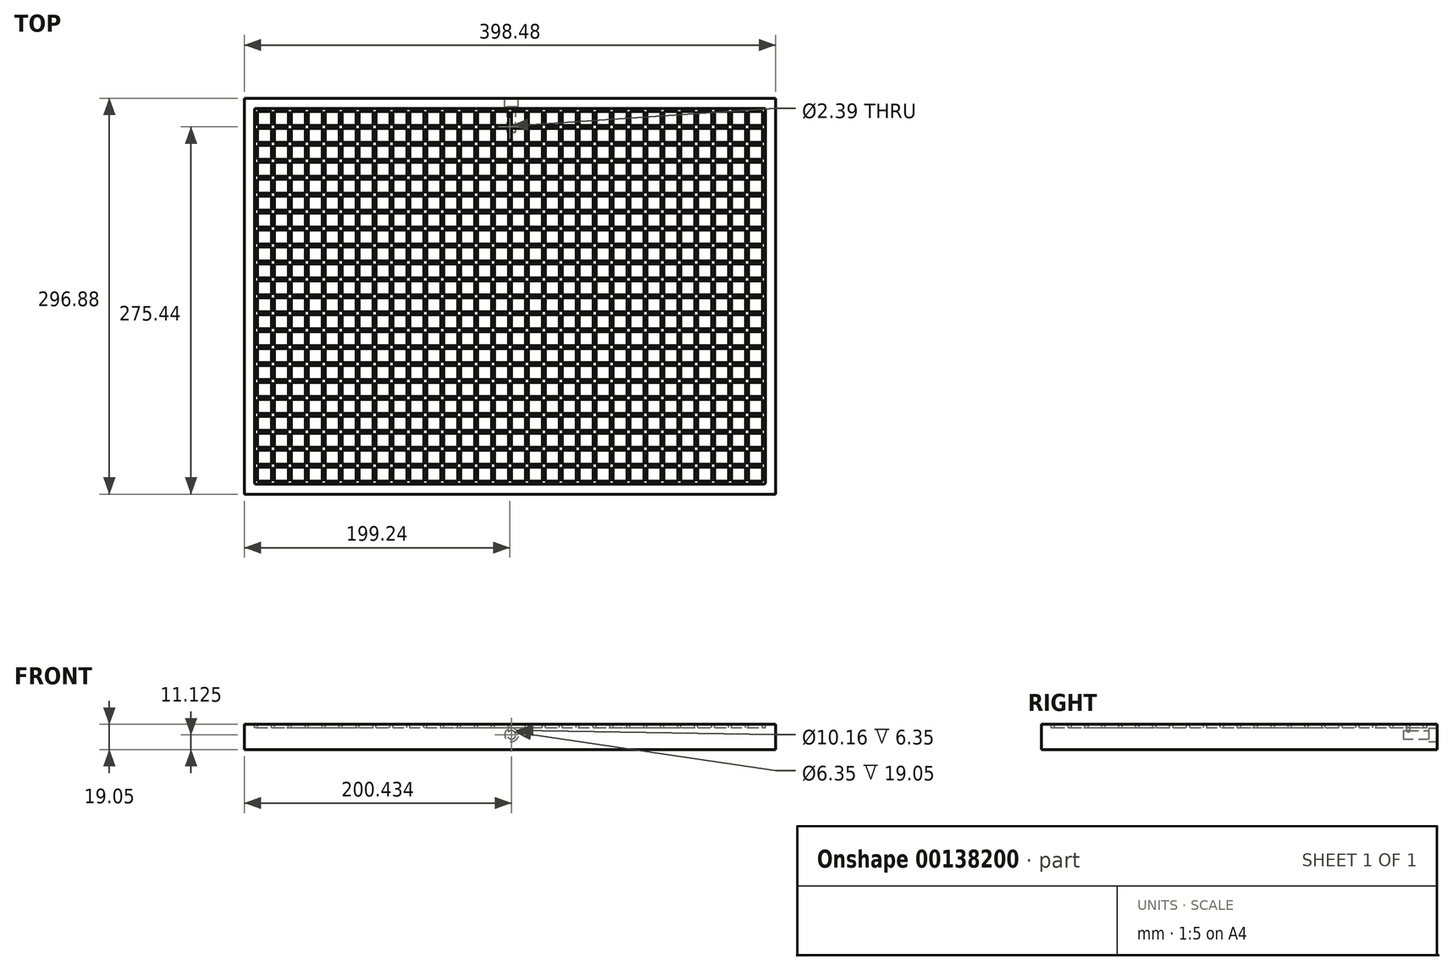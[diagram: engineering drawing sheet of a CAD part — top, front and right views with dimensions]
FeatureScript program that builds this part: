
annotation { "Feature Type Name" : "Feature", "Feature Type Description" : "" }
export const myFeature = defineFeature(function(context is Context, id is Id, definition is map)
    precondition{}
    {
        {
            var Q0;
            Q0=qCreatedBy(makeId("Top.planeOp"),FACE);
            var sketch = newSketch(context, id + "F0", { "sketchPlane" : qUnion([Q0])});
            skLineSegment(sketch, "E0.bottom", {"start": v(0, 0) * mm, "end": v(406.4, 0) * mm});
            skLineSegment(sketch, "E0.top", {"start": v(0, 304.8) * mm, "end": v(406.4, 304.8) * mm});
            skLineSegment(sketch, "E0.left", {"start": v(0, 0) * mm, "end": v(0, 304.8) * mm});
            skLineSegment(sketch, "E0.right", {"start": v(406.4, 0) * mm, "end": v(406.4, 304.8) * mm});
            skSolve(sketch);
        }
        {
            var Q0;
            Q0=qSketchRegion(id+"F0",true);
            extrude(context, id + "F1", {"entities" : qUnion([Q0]), "depth" : 19.05 * mm});
        }
        {
            var Q0;
            Q0=makeQuery(id+"F1.opExtrude","CAP_FACE",FACE,{"disambiguationData":[OSD([sQuery(id+"F0.wireOp",EDGE,"E0.bottom"),sQuery(id+"F0.wireOp",EDGE,"E0.top"),sQuery(id+"F0.wireOp",EDGE,"E0.left"),sQuery(id+"F0.wireOp",EDGE,"E0.right")])],"isStart":false});
            var sketch = newSketch(context, id + "F2", { "sketchPlane" : qUnion([Q0])});
            skLineSegment(sketch, "E1.bottom", {"start": v(12.7, 11.5) * mm, "end": v(393.7, 11.5) * mm});
            skLineSegment(sketch, "E1.top", {"start": v(12.7, 293.3) * mm, "end": v(393.7, 293.3) * mm});
            skLineSegment(sketch, "E1.left", {"start": v(11.5, 12.7) * mm, "end": v(11.5, 292.1) * mm});
            skLineSegment(sketch, "E1.right", {"start": v(394.9, 12.7) * mm, "end": v(394.9, 292.1) * mm});
            skLineSegment(sketch, "E2.bottom", {"start": v(13.9, 13.9) * mm, "end": v(24.2, 13.9) * mm});
            skLineSegment(sketch, "E2.top", {"start": v(13.9, 24.2) * mm, "end": v(24.2, 24.2) * mm});
            skLineSegment(sketch, "E2.left", {"start": v(13.9, 13.9) * mm, "end": v(13.9, 24.2) * mm});
            skLineSegment(sketch, "E2.right", {"start": v(24.2, 13.9) * mm, "end": v(24.2, 24.2) * mm});
            skLineSegment(sketch, "E3.0.1.0", {"start": v(13.9, 26.6) * mm, "end": v(13.9, 36.9) * mm});
            skLineSegment(sketch, "E3.0.1.1", {"start": v(13.9, 36.9) * mm, "end": v(24.2, 36.9) * mm});
            skLineSegment(sketch, "E3.0.1.2", {"start": v(13.9, 26.6) * mm, "end": v(24.2, 26.6) * mm});
            skLineSegment(sketch, "E3.0.1.3", {"start": v(24.2, 26.6) * mm, "end": v(24.2, 36.9) * mm});
            skLineSegment(sketch, "E3.0.2.0", {"start": v(13.9, 39.3) * mm, "end": v(13.9, 49.6) * mm});
            skLineSegment(sketch, "E3.0.2.1", {"start": v(13.9, 49.6) * mm, "end": v(24.2, 49.6) * mm});
            skLineSegment(sketch, "E3.0.2.2", {"start": v(13.9, 39.3) * mm, "end": v(24.2, 39.3) * mm});
            skLineSegment(sketch, "E3.0.2.3", {"start": v(24.2, 39.3) * mm, "end": v(24.2, 49.6) * mm});
            skLineSegment(sketch, "E3.0.3.0", {"start": v(13.9, 52) * mm, "end": v(13.9, 62.3) * mm});
            skLineSegment(sketch, "E3.0.3.1", {"start": v(13.9, 62.3) * mm, "end": v(24.2, 62.3) * mm});
            skLineSegment(sketch, "E3.0.3.2", {"start": v(13.9, 52) * mm, "end": v(24.2, 52) * mm});
            skLineSegment(sketch, "E3.0.3.3", {"start": v(24.2, 52) * mm, "end": v(24.2, 62.3) * mm});
            skLineSegment(sketch, "E3.0.4.0", {"start": v(13.9, 64.7) * mm, "end": v(13.9, 75) * mm});
            skLineSegment(sketch, "E3.0.4.1", {"start": v(13.9, 75) * mm, "end": v(24.2, 75) * mm});
            skLineSegment(sketch, "E3.0.4.2", {"start": v(13.9, 64.7) * mm, "end": v(24.2, 64.7) * mm});
            skLineSegment(sketch, "E3.0.4.3", {"start": v(24.2, 64.7) * mm, "end": v(24.2, 75) * mm});
            skLineSegment(sketch, "E3.0.5.0", {"start": v(13.9, 77.4) * mm, "end": v(13.9, 87.7) * mm});
            skLineSegment(sketch, "E3.0.5.1", {"start": v(13.9, 87.7) * mm, "end": v(24.2, 87.7) * mm});
            skLineSegment(sketch, "E3.0.5.2", {"start": v(13.9, 77.4) * mm, "end": v(24.2, 77.4) * mm});
            skLineSegment(sketch, "E3.0.5.3", {"start": v(24.2, 77.4) * mm, "end": v(24.2, 87.7) * mm});
            skLineSegment(sketch, "E3.0.6.0", {"start": v(13.9, 90.1) * mm, "end": v(13.9, 100.4) * mm});
            skLineSegment(sketch, "E3.0.6.1", {"start": v(13.9, 100.4) * mm, "end": v(24.2, 100.4) * mm});
            skLineSegment(sketch, "E3.0.6.2", {"start": v(13.9, 90.1) * mm, "end": v(24.2, 90.1) * mm});
            skLineSegment(sketch, "E3.0.6.3", {"start": v(24.2, 90.1) * mm, "end": v(24.2, 100.4) * mm});
            skLineSegment(sketch, "E3.0.7.0", {"start": v(13.9, 102.8) * mm, "end": v(13.9, 113.1) * mm});
            skLineSegment(sketch, "E3.0.7.1", {"start": v(13.9, 113.1) * mm, "end": v(24.2, 113.1) * mm});
            skLineSegment(sketch, "E3.0.7.2", {"start": v(13.9, 102.8) * mm, "end": v(24.2, 102.8) * mm});
            skLineSegment(sketch, "E3.0.7.3", {"start": v(24.2, 102.8) * mm, "end": v(24.2, 113.1) * mm});
            skLineSegment(sketch, "E3.0.8.0", {"start": v(13.9, 115.5) * mm, "end": v(13.9, 125.8) * mm});
            skLineSegment(sketch, "E3.0.8.1", {"start": v(13.9, 125.8) * mm, "end": v(24.2, 125.8) * mm});
            skLineSegment(sketch, "E3.0.8.2", {"start": v(13.9, 115.5) * mm, "end": v(24.2, 115.5) * mm});
            skLineSegment(sketch, "E3.0.8.3", {"start": v(24.2, 115.5) * mm, "end": v(24.2, 125.8) * mm});
            skLineSegment(sketch, "E3.0.9.0", {"start": v(13.9, 128.2) * mm, "end": v(13.9, 138.5) * mm});
            skLineSegment(sketch, "E3.0.9.1", {"start": v(13.9, 138.5) * mm, "end": v(24.2, 138.5) * mm});
            skLineSegment(sketch, "E3.0.9.2", {"start": v(13.9, 128.2) * mm, "end": v(24.2, 128.2) * mm});
            skLineSegment(sketch, "E3.0.9.3", {"start": v(24.2, 128.2) * mm, "end": v(24.2, 138.5) * mm});
            skLineSegment(sketch, "E3.0.10.0", {"start": v(13.9, 140.9) * mm, "end": v(13.9, 151.2) * mm});
            skLineSegment(sketch, "E3.0.10.1", {"start": v(13.9, 151.2) * mm, "end": v(24.2, 151.2) * mm});
            skLineSegment(sketch, "E3.0.10.2", {"start": v(13.9, 140.9) * mm, "end": v(24.2, 140.9) * mm});
            skLineSegment(sketch, "E3.0.10.3", {"start": v(24.2, 140.9) * mm, "end": v(24.2, 151.2) * mm});
            skLineSegment(sketch, "E3.0.11.0", {"start": v(13.9, 153.6) * mm, "end": v(13.9, 163.9) * mm});
            skLineSegment(sketch, "E3.0.11.1", {"start": v(13.9, 163.9) * mm, "end": v(24.2, 163.9) * mm});
            skLineSegment(sketch, "E3.0.11.2", {"start": v(13.9, 153.6) * mm, "end": v(24.2, 153.6) * mm});
            skLineSegment(sketch, "E3.0.11.3", {"start": v(24.2, 153.6) * mm, "end": v(24.2, 163.9) * mm});
            skLineSegment(sketch, "E3.0.12.0", {"start": v(13.9, 166.3) * mm, "end": v(13.9, 176.6) * mm});
            skLineSegment(sketch, "E3.0.12.1", {"start": v(13.9, 176.6) * mm, "end": v(24.2, 176.6) * mm});
            skLineSegment(sketch, "E3.0.12.2", {"start": v(13.9, 166.3) * mm, "end": v(24.2, 166.3) * mm});
            skLineSegment(sketch, "E3.0.12.3", {"start": v(24.2, 166.3) * mm, "end": v(24.2, 176.6) * mm});
            skLineSegment(sketch, "E3.0.13.0", {"start": v(13.9, 179) * mm, "end": v(13.9, 189.3) * mm});
            skLineSegment(sketch, "E3.0.13.1", {"start": v(13.9, 189.3) * mm, "end": v(24.2, 189.3) * mm});
            skLineSegment(sketch, "E3.0.13.2", {"start": v(13.9, 179) * mm, "end": v(24.2, 179) * mm});
            skLineSegment(sketch, "E3.0.13.3", {"start": v(24.2, 179) * mm, "end": v(24.2, 189.3) * mm});
            skLineSegment(sketch, "E3.0.14.0", {"start": v(13.9, 191.7) * mm, "end": v(13.9, 202) * mm});
            skLineSegment(sketch, "E3.0.14.1", {"start": v(13.9, 202) * mm, "end": v(24.2, 202) * mm});
            skLineSegment(sketch, "E3.0.14.2", {"start": v(13.9, 191.7) * mm, "end": v(24.2, 191.7) * mm});
            skLineSegment(sketch, "E3.0.14.3", {"start": v(24.2, 191.7) * mm, "end": v(24.2, 202) * mm});
            skLineSegment(sketch, "E3.0.15.0", {"start": v(13.9, 204.4) * mm, "end": v(13.9, 214.7) * mm});
            skLineSegment(sketch, "E3.0.15.1", {"start": v(13.9, 214.7) * mm, "end": v(24.2, 214.7) * mm});
            skLineSegment(sketch, "E3.0.15.2", {"start": v(13.9, 204.4) * mm, "end": v(24.2, 204.4) * mm});
            skLineSegment(sketch, "E3.0.15.3", {"start": v(24.2, 204.4) * mm, "end": v(24.2, 214.7) * mm});
            skLineSegment(sketch, "E3.0.16.0", {"start": v(13.9, 217.1) * mm, "end": v(13.9, 227.4) * mm});
            skLineSegment(sketch, "E3.0.16.1", {"start": v(13.9, 227.4) * mm, "end": v(24.2, 227.4) * mm});
            skLineSegment(sketch, "E3.0.16.2", {"start": v(13.9, 217.1) * mm, "end": v(24.2, 217.1) * mm});
            skLineSegment(sketch, "E3.0.16.3", {"start": v(24.2, 217.1) * mm, "end": v(24.2, 227.4) * mm});
            skLineSegment(sketch, "E3.0.17.0", {"start": v(13.9, 229.8) * mm, "end": v(13.9, 240.1) * mm});
            skLineSegment(sketch, "E3.0.17.1", {"start": v(13.9, 240.1) * mm, "end": v(24.2, 240.1) * mm});
            skLineSegment(sketch, "E3.0.17.2", {"start": v(13.9, 229.8) * mm, "end": v(24.2, 229.8) * mm});
            skLineSegment(sketch, "E3.0.17.3", {"start": v(24.2, 229.8) * mm, "end": v(24.2, 240.1) * mm});
            skLineSegment(sketch, "E3.0.18.0", {"start": v(13.9, 242.5) * mm, "end": v(13.9, 252.8) * mm});
            skLineSegment(sketch, "E3.0.18.1", {"start": v(13.9, 252.8) * mm, "end": v(24.2, 252.8) * mm});
            skLineSegment(sketch, "E3.0.18.2", {"start": v(13.9, 242.5) * mm, "end": v(24.2, 242.5) * mm});
            skLineSegment(sketch, "E3.0.18.3", {"start": v(24.2, 242.5) * mm, "end": v(24.2, 252.8) * mm});
            skLineSegment(sketch, "E3.0.19.0", {"start": v(13.9, 255.2) * mm, "end": v(13.9, 265.5) * mm});
            skLineSegment(sketch, "E3.0.19.1", {"start": v(13.9, 265.5) * mm, "end": v(24.2, 265.5) * mm});
            skLineSegment(sketch, "E3.0.19.2", {"start": v(13.9, 255.2) * mm, "end": v(24.2, 255.2) * mm});
            skLineSegment(sketch, "E3.0.19.3", {"start": v(24.2, 255.2) * mm, "end": v(24.2, 265.5) * mm});
            skLineSegment(sketch, "E3.0.20.0", {"start": v(13.9, 267.9) * mm, "end": v(13.9, 278.2) * mm});
            skLineSegment(sketch, "E3.0.20.1", {"start": v(13.9, 278.2) * mm, "end": v(24.2, 278.2) * mm});
            skLineSegment(sketch, "E3.0.20.2", {"start": v(13.9, 267.9) * mm, "end": v(24.2, 267.9) * mm});
            skLineSegment(sketch, "E3.0.20.3", {"start": v(24.2, 267.9) * mm, "end": v(24.2, 278.2) * mm});
            skLineSegment(sketch, "E3.0.21.0", {"start": v(13.9, 280.6) * mm, "end": v(13.9, 290.9) * mm});
            skLineSegment(sketch, "E3.0.21.1", {"start": v(13.9, 290.9) * mm, "end": v(24.2, 290.9) * mm});
            skLineSegment(sketch, "E3.0.21.2", {"start": v(13.9, 280.6) * mm, "end": v(24.2, 280.6) * mm});
            skLineSegment(sketch, "E3.0.21.3", {"start": v(24.2, 280.6) * mm, "end": v(24.2, 290.9) * mm});
            skLineSegment(sketch, "E3.1.0.0", {"start": v(26.6, 13.9) * mm, "end": v(26.6, 24.2) * mm});
            skLineSegment(sketch, "E3.1.0.1", {"start": v(26.6, 24.2) * mm, "end": v(36.9, 24.2) * mm});
            skLineSegment(sketch, "E3.1.0.2", {"start": v(26.6, 13.9) * mm, "end": v(36.9, 13.9) * mm});
            skLineSegment(sketch, "E3.1.0.3", {"start": v(36.9, 13.9) * mm, "end": v(36.9, 24.2) * mm});
            skLineSegment(sketch, "E3.1.1.0", {"start": v(26.6, 26.6) * mm, "end": v(26.6, 36.9) * mm});
            skLineSegment(sketch, "E3.1.1.1", {"start": v(26.6, 36.9) * mm, "end": v(36.9, 36.9) * mm});
            skLineSegment(sketch, "E3.1.1.2", {"start": v(26.6, 26.6) * mm, "end": v(36.9, 26.6) * mm});
            skLineSegment(sketch, "E3.1.1.3", {"start": v(36.9, 26.6) * mm, "end": v(36.9, 36.9) * mm});
            skLineSegment(sketch, "E3.1.2.0", {"start": v(26.6, 39.3) * mm, "end": v(26.6, 49.6) * mm});
            skLineSegment(sketch, "E3.1.2.1", {"start": v(26.6, 49.6) * mm, "end": v(36.9, 49.6) * mm});
            skLineSegment(sketch, "E3.1.2.2", {"start": v(26.6, 39.3) * mm, "end": v(36.9, 39.3) * mm});
            skLineSegment(sketch, "E3.1.2.3", {"start": v(36.9, 39.3) * mm, "end": v(36.9, 49.6) * mm});
            skLineSegment(sketch, "E3.1.3.0", {"start": v(26.6, 52) * mm, "end": v(26.6, 62.3) * mm});
            skLineSegment(sketch, "E3.1.3.1", {"start": v(26.6, 62.3) * mm, "end": v(36.9, 62.3) * mm});
            skLineSegment(sketch, "E3.1.3.2", {"start": v(26.6, 52) * mm, "end": v(36.9, 52) * mm});
            skLineSegment(sketch, "E3.1.3.3", {"start": v(36.9, 52) * mm, "end": v(36.9, 62.3) * mm});
            skLineSegment(sketch, "E3.1.4.0", {"start": v(26.6, 64.7) * mm, "end": v(26.6, 75) * mm});
            skLineSegment(sketch, "E3.1.4.1", {"start": v(26.6, 75) * mm, "end": v(36.9, 75) * mm});
            skLineSegment(sketch, "E3.1.4.2", {"start": v(26.6, 64.7) * mm, "end": v(36.9, 64.7) * mm});
            skLineSegment(sketch, "E3.1.4.3", {"start": v(36.9, 64.7) * mm, "end": v(36.9, 75) * mm});
            skLineSegment(sketch, "E3.1.5.0", {"start": v(26.6, 77.4) * mm, "end": v(26.6, 87.7) * mm});
            skLineSegment(sketch, "E3.1.5.1", {"start": v(26.6, 87.7) * mm, "end": v(36.9, 87.7) * mm});
            skLineSegment(sketch, "E3.1.5.2", {"start": v(26.6, 77.4) * mm, "end": v(36.9, 77.4) * mm});
            skLineSegment(sketch, "E3.1.5.3", {"start": v(36.9, 77.4) * mm, "end": v(36.9, 87.7) * mm});
            skLineSegment(sketch, "E3.1.6.0", {"start": v(26.6, 90.1) * mm, "end": v(26.6, 100.4) * mm});
            skLineSegment(sketch, "E3.1.6.1", {"start": v(26.6, 100.4) * mm, "end": v(36.9, 100.4) * mm});
            skLineSegment(sketch, "E3.1.6.2", {"start": v(26.6, 90.1) * mm, "end": v(36.9, 90.1) * mm});
            skLineSegment(sketch, "E3.1.6.3", {"start": v(36.9, 90.1) * mm, "end": v(36.9, 100.4) * mm});
            skLineSegment(sketch, "E3.1.7.0", {"start": v(26.6, 102.8) * mm, "end": v(26.6, 113.1) * mm});
            skLineSegment(sketch, "E3.1.7.1", {"start": v(26.6, 113.1) * mm, "end": v(36.9, 113.1) * mm});
            skLineSegment(sketch, "E3.1.7.2", {"start": v(26.6, 102.8) * mm, "end": v(36.9, 102.8) * mm});
            skLineSegment(sketch, "E3.1.7.3", {"start": v(36.9, 102.8) * mm, "end": v(36.9, 113.1) * mm});
            skLineSegment(sketch, "E3.1.8.0", {"start": v(26.6, 115.5) * mm, "end": v(26.6, 125.8) * mm});
            skLineSegment(sketch, "E3.1.8.1", {"start": v(26.6, 125.8) * mm, "end": v(36.9, 125.8) * mm});
            skLineSegment(sketch, "E3.1.8.2", {"start": v(26.6, 115.5) * mm, "end": v(36.9, 115.5) * mm});
            skLineSegment(sketch, "E3.1.8.3", {"start": v(36.9, 115.5) * mm, "end": v(36.9, 125.8) * mm});
            skLineSegment(sketch, "E3.1.9.0", {"start": v(26.6, 128.2) * mm, "end": v(26.6, 138.5) * mm});
            skLineSegment(sketch, "E3.1.9.1", {"start": v(26.6, 138.5) * mm, "end": v(36.9, 138.5) * mm});
            skLineSegment(sketch, "E3.1.9.2", {"start": v(26.6, 128.2) * mm, "end": v(36.9, 128.2) * mm});
            skLineSegment(sketch, "E3.1.9.3", {"start": v(36.9, 128.2) * mm, "end": v(36.9, 138.5) * mm});
            skLineSegment(sketch, "E3.1.10.0", {"start": v(26.6, 140.9) * mm, "end": v(26.6, 151.2) * mm});
            skLineSegment(sketch, "E3.1.10.1", {"start": v(26.6, 151.2) * mm, "end": v(36.9, 151.2) * mm});
            skLineSegment(sketch, "E3.1.10.2", {"start": v(26.6, 140.9) * mm, "end": v(36.9, 140.9) * mm});
            skLineSegment(sketch, "E3.1.10.3", {"start": v(36.9, 140.9) * mm, "end": v(36.9, 151.2) * mm});
            skLineSegment(sketch, "E3.1.11.0", {"start": v(26.6, 153.6) * mm, "end": v(26.6, 163.9) * mm});
            skLineSegment(sketch, "E3.1.11.1", {"start": v(26.6, 163.9) * mm, "end": v(36.9, 163.9) * mm});
            skLineSegment(sketch, "E3.1.11.2", {"start": v(26.6, 153.6) * mm, "end": v(36.9, 153.6) * mm});
            skLineSegment(sketch, "E3.1.11.3", {"start": v(36.9, 153.6) * mm, "end": v(36.9, 163.9) * mm});
            skLineSegment(sketch, "E3.1.12.0", {"start": v(26.6, 166.3) * mm, "end": v(26.6, 176.6) * mm});
            skLineSegment(sketch, "E3.1.12.1", {"start": v(26.6, 176.6) * mm, "end": v(36.9, 176.6) * mm});
            skLineSegment(sketch, "E3.1.12.2", {"start": v(26.6, 166.3) * mm, "end": v(36.9, 166.3) * mm});
            skLineSegment(sketch, "E3.1.12.3", {"start": v(36.9, 166.3) * mm, "end": v(36.9, 176.6) * mm});
            skLineSegment(sketch, "E3.1.13.0", {"start": v(26.6, 179) * mm, "end": v(26.6, 189.3) * mm});
            skLineSegment(sketch, "E3.1.13.1", {"start": v(26.6, 189.3) * mm, "end": v(36.9, 189.3) * mm});
            skLineSegment(sketch, "E3.1.13.2", {"start": v(26.6, 179) * mm, "end": v(36.9, 179) * mm});
            skLineSegment(sketch, "E3.1.13.3", {"start": v(36.9, 179) * mm, "end": v(36.9, 189.3) * mm});
            skLineSegment(sketch, "E3.1.14.0", {"start": v(26.6, 191.7) * mm, "end": v(26.6, 202) * mm});
            skLineSegment(sketch, "E3.1.14.1", {"start": v(26.6, 202) * mm, "end": v(36.9, 202) * mm});
            skLineSegment(sketch, "E3.1.14.2", {"start": v(26.6, 191.7) * mm, "end": v(36.9, 191.7) * mm});
            skLineSegment(sketch, "E3.1.14.3", {"start": v(36.9, 191.7) * mm, "end": v(36.9, 202) * mm});
            skLineSegment(sketch, "E3.1.15.0", {"start": v(26.6, 204.4) * mm, "end": v(26.6, 214.7) * mm});
            skLineSegment(sketch, "E3.1.15.1", {"start": v(26.6, 214.7) * mm, "end": v(36.9, 214.7) * mm});
            skLineSegment(sketch, "E3.1.15.2", {"start": v(26.6, 204.4) * mm, "end": v(36.9, 204.4) * mm});
            skLineSegment(sketch, "E3.1.15.3", {"start": v(36.9, 204.4) * mm, "end": v(36.9, 214.7) * mm});
            skLineSegment(sketch, "E3.1.16.0", {"start": v(26.6, 217.1) * mm, "end": v(26.6, 227.4) * mm});
            skLineSegment(sketch, "E3.1.16.1", {"start": v(26.6, 227.4) * mm, "end": v(36.9, 227.4) * mm});
            skLineSegment(sketch, "E3.1.16.2", {"start": v(26.6, 217.1) * mm, "end": v(36.9, 217.1) * mm});
            skLineSegment(sketch, "E3.1.16.3", {"start": v(36.9, 217.1) * mm, "end": v(36.9, 227.4) * mm});
            skLineSegment(sketch, "E3.1.17.0", {"start": v(26.6, 229.8) * mm, "end": v(26.6, 240.1) * mm});
            skLineSegment(sketch, "E3.1.17.1", {"start": v(26.6, 240.1) * mm, "end": v(36.9, 240.1) * mm});
            skLineSegment(sketch, "E3.1.17.2", {"start": v(26.6, 229.8) * mm, "end": v(36.9, 229.8) * mm});
            skLineSegment(sketch, "E3.1.17.3", {"start": v(36.9, 229.8) * mm, "end": v(36.9, 240.1) * mm});
            skLineSegment(sketch, "E3.1.18.0", {"start": v(26.6, 242.5) * mm, "end": v(26.6, 252.8) * mm});
            skLineSegment(sketch, "E3.1.18.1", {"start": v(26.6, 252.8) * mm, "end": v(36.9, 252.8) * mm});
            skLineSegment(sketch, "E3.1.18.2", {"start": v(26.6, 242.5) * mm, "end": v(36.9, 242.5) * mm});
            skLineSegment(sketch, "E3.1.18.3", {"start": v(36.9, 242.5) * mm, "end": v(36.9, 252.8) * mm});
            skLineSegment(sketch, "E3.1.19.0", {"start": v(26.6, 255.2) * mm, "end": v(26.6, 265.5) * mm});
            skLineSegment(sketch, "E3.1.19.1", {"start": v(26.6, 265.5) * mm, "end": v(36.9, 265.5) * mm});
            skLineSegment(sketch, "E3.1.19.2", {"start": v(26.6, 255.2) * mm, "end": v(36.9, 255.2) * mm});
            skLineSegment(sketch, "E3.1.19.3", {"start": v(36.9, 255.2) * mm, "end": v(36.9, 265.5) * mm});
            skLineSegment(sketch, "E3.1.20.0", {"start": v(26.6, 267.9) * mm, "end": v(26.6, 278.2) * mm});
            skLineSegment(sketch, "E3.1.20.1", {"start": v(26.6, 278.2) * mm, "end": v(36.9, 278.2) * mm});
            skLineSegment(sketch, "E3.1.20.2", {"start": v(26.6, 267.9) * mm, "end": v(36.9, 267.9) * mm});
            skLineSegment(sketch, "E3.1.20.3", {"start": v(36.9, 267.9) * mm, "end": v(36.9, 278.2) * mm});
            skLineSegment(sketch, "E3.1.21.0", {"start": v(26.6, 280.6) * mm, "end": v(26.6, 290.9) * mm});
            skLineSegment(sketch, "E3.1.21.1", {"start": v(26.6, 290.9) * mm, "end": v(36.9, 290.9) * mm});
            skLineSegment(sketch, "E3.1.21.2", {"start": v(26.6, 280.6) * mm, "end": v(36.9, 280.6) * mm});
            skLineSegment(sketch, "E3.1.21.3", {"start": v(36.9, 280.6) * mm, "end": v(36.9, 290.9) * mm});
            skLineSegment(sketch, "E3.2.0.0", {"start": v(39.3, 13.9) * mm, "end": v(39.3, 24.2) * mm});
            skLineSegment(sketch, "E3.2.0.1", {"start": v(39.3, 24.2) * mm, "end": v(49.6, 24.2) * mm});
            skLineSegment(sketch, "E3.2.0.2", {"start": v(39.3, 13.9) * mm, "end": v(49.6, 13.9) * mm});
            skLineSegment(sketch, "E3.2.0.3", {"start": v(49.6, 13.9) * mm, "end": v(49.6, 24.2) * mm});
            skLineSegment(sketch, "E3.2.1.0", {"start": v(39.3, 26.6) * mm, "end": v(39.3, 36.9) * mm});
            skLineSegment(sketch, "E3.2.1.1", {"start": v(39.3, 36.9) * mm, "end": v(49.6, 36.9) * mm});
            skLineSegment(sketch, "E3.2.1.2", {"start": v(39.3, 26.6) * mm, "end": v(49.6, 26.6) * mm});
            skLineSegment(sketch, "E3.2.1.3", {"start": v(49.6, 26.6) * mm, "end": v(49.6, 36.9) * mm});
            skLineSegment(sketch, "E3.2.2.0", {"start": v(39.3, 39.3) * mm, "end": v(39.3, 49.6) * mm});
            skLineSegment(sketch, "E3.2.2.1", {"start": v(39.3, 49.6) * mm, "end": v(49.6, 49.6) * mm});
            skLineSegment(sketch, "E3.2.2.2", {"start": v(39.3, 39.3) * mm, "end": v(49.6, 39.3) * mm});
            skLineSegment(sketch, "E3.2.2.3", {"start": v(49.6, 39.3) * mm, "end": v(49.6, 49.6) * mm});
            skLineSegment(sketch, "E3.2.3.0", {"start": v(39.3, 52) * mm, "end": v(39.3, 62.3) * mm});
            skLineSegment(sketch, "E3.2.3.1", {"start": v(39.3, 62.3) * mm, "end": v(49.6, 62.3) * mm});
            skLineSegment(sketch, "E3.2.3.2", {"start": v(39.3, 52) * mm, "end": v(49.6, 52) * mm});
            skLineSegment(sketch, "E3.2.3.3", {"start": v(49.6, 52) * mm, "end": v(49.6, 62.3) * mm});
            skLineSegment(sketch, "E3.2.4.0", {"start": v(39.3, 64.7) * mm, "end": v(39.3, 75) * mm});
            skLineSegment(sketch, "E3.2.4.1", {"start": v(39.3, 75) * mm, "end": v(49.6, 75) * mm});
            skLineSegment(sketch, "E3.2.4.2", {"start": v(39.3, 64.7) * mm, "end": v(49.6, 64.7) * mm});
            skLineSegment(sketch, "E3.2.4.3", {"start": v(49.6, 64.7) * mm, "end": v(49.6, 75) * mm});
            skLineSegment(sketch, "E3.2.5.0", {"start": v(39.3, 77.4) * mm, "end": v(39.3, 87.7) * mm});
            skLineSegment(sketch, "E3.2.5.1", {"start": v(39.3, 87.7) * mm, "end": v(49.6, 87.7) * mm});
            skLineSegment(sketch, "E3.2.5.2", {"start": v(39.3, 77.4) * mm, "end": v(49.6, 77.4) * mm});
            skLineSegment(sketch, "E3.2.5.3", {"start": v(49.6, 77.4) * mm, "end": v(49.6, 87.7) * mm});
            skLineSegment(sketch, "E3.2.6.0", {"start": v(39.3, 90.1) * mm, "end": v(39.3, 100.4) * mm});
            skLineSegment(sketch, "E3.2.6.1", {"start": v(39.3, 100.4) * mm, "end": v(49.6, 100.4) * mm});
            skLineSegment(sketch, "E3.2.6.2", {"start": v(39.3, 90.1) * mm, "end": v(49.6, 90.1) * mm});
            skLineSegment(sketch, "E3.2.6.3", {"start": v(49.6, 90.1) * mm, "end": v(49.6, 100.4) * mm});
            skLineSegment(sketch, "E3.2.7.0", {"start": v(39.3, 102.8) * mm, "end": v(39.3, 113.1) * mm});
            skLineSegment(sketch, "E3.2.7.1", {"start": v(39.3, 113.1) * mm, "end": v(49.6, 113.1) * mm});
            skLineSegment(sketch, "E3.2.7.2", {"start": v(39.3, 102.8) * mm, "end": v(49.6, 102.8) * mm});
            skLineSegment(sketch, "E3.2.7.3", {"start": v(49.6, 102.8) * mm, "end": v(49.6, 113.1) * mm});
            skLineSegment(sketch, "E3.2.8.0", {"start": v(39.3, 115.5) * mm, "end": v(39.3, 125.8) * mm});
            skLineSegment(sketch, "E3.2.8.1", {"start": v(39.3, 125.8) * mm, "end": v(49.6, 125.8) * mm});
            skLineSegment(sketch, "E3.2.8.2", {"start": v(39.3, 115.5) * mm, "end": v(49.6, 115.5) * mm});
            skLineSegment(sketch, "E3.2.8.3", {"start": v(49.6, 115.5) * mm, "end": v(49.6, 125.8) * mm});
            skLineSegment(sketch, "E3.2.9.0", {"start": v(39.3, 128.2) * mm, "end": v(39.3, 138.5) * mm});
            skLineSegment(sketch, "E3.2.9.1", {"start": v(39.3, 138.5) * mm, "end": v(49.6, 138.5) * mm});
            skLineSegment(sketch, "E3.2.9.2", {"start": v(39.3, 128.2) * mm, "end": v(49.6, 128.2) * mm});
            skLineSegment(sketch, "E3.2.9.3", {"start": v(49.6, 128.2) * mm, "end": v(49.6, 138.5) * mm});
            skLineSegment(sketch, "E3.2.10.0", {"start": v(39.3, 140.9) * mm, "end": v(39.3, 151.2) * mm});
            skLineSegment(sketch, "E3.2.10.1", {"start": v(39.3, 151.2) * mm, "end": v(49.6, 151.2) * mm});
            skLineSegment(sketch, "E3.2.10.2", {"start": v(39.3, 140.9) * mm, "end": v(49.6, 140.9) * mm});
            skLineSegment(sketch, "E3.2.10.3", {"start": v(49.6, 140.9) * mm, "end": v(49.6, 151.2) * mm});
            skLineSegment(sketch, "E3.2.11.0", {"start": v(39.3, 153.6) * mm, "end": v(39.3, 163.9) * mm});
            skLineSegment(sketch, "E3.2.11.1", {"start": v(39.3, 163.9) * mm, "end": v(49.6, 163.9) * mm});
            skLineSegment(sketch, "E3.2.11.2", {"start": v(39.3, 153.6) * mm, "end": v(49.6, 153.6) * mm});
            skLineSegment(sketch, "E3.2.11.3", {"start": v(49.6, 153.6) * mm, "end": v(49.6, 163.9) * mm});
            skLineSegment(sketch, "E3.2.12.0", {"start": v(39.3, 166.3) * mm, "end": v(39.3, 176.6) * mm});
            skLineSegment(sketch, "E3.2.12.1", {"start": v(39.3, 176.6) * mm, "end": v(49.6, 176.6) * mm});
            skLineSegment(sketch, "E3.2.12.2", {"start": v(39.3, 166.3) * mm, "end": v(49.6, 166.3) * mm});
            skLineSegment(sketch, "E3.2.12.3", {"start": v(49.6, 166.3) * mm, "end": v(49.6, 176.6) * mm});
            skLineSegment(sketch, "E3.2.13.0", {"start": v(39.3, 179) * mm, "end": v(39.3, 189.3) * mm});
            skLineSegment(sketch, "E3.2.13.1", {"start": v(39.3, 189.3) * mm, "end": v(49.6, 189.3) * mm});
            skLineSegment(sketch, "E3.2.13.2", {"start": v(39.3, 179) * mm, "end": v(49.6, 179) * mm});
            skLineSegment(sketch, "E3.2.13.3", {"start": v(49.6, 179) * mm, "end": v(49.6, 189.3) * mm});
            skLineSegment(sketch, "E3.2.14.0", {"start": v(39.3, 191.7) * mm, "end": v(39.3, 202) * mm});
            skLineSegment(sketch, "E3.2.14.1", {"start": v(39.3, 202) * mm, "end": v(49.6, 202) * mm});
            skLineSegment(sketch, "E3.2.14.2", {"start": v(39.3, 191.7) * mm, "end": v(49.6, 191.7) * mm});
            skLineSegment(sketch, "E3.2.14.3", {"start": v(49.6, 191.7) * mm, "end": v(49.6, 202) * mm});
            skLineSegment(sketch, "E3.2.15.0", {"start": v(39.3, 204.4) * mm, "end": v(39.3, 214.7) * mm});
            skLineSegment(sketch, "E3.2.15.1", {"start": v(39.3, 214.7) * mm, "end": v(49.6, 214.7) * mm});
            skLineSegment(sketch, "E3.2.15.2", {"start": v(39.3, 204.4) * mm, "end": v(49.6, 204.4) * mm});
            skLineSegment(sketch, "E3.2.15.3", {"start": v(49.6, 204.4) * mm, "end": v(49.6, 214.7) * mm});
            skLineSegment(sketch, "E3.2.16.0", {"start": v(39.3, 217.1) * mm, "end": v(39.3, 227.4) * mm});
            skLineSegment(sketch, "E3.2.16.1", {"start": v(39.3, 227.4) * mm, "end": v(49.6, 227.4) * mm});
            skLineSegment(sketch, "E3.2.16.2", {"start": v(39.3, 217.1) * mm, "end": v(49.6, 217.1) * mm});
            skLineSegment(sketch, "E3.2.16.3", {"start": v(49.6, 217.1) * mm, "end": v(49.6, 227.4) * mm});
            skLineSegment(sketch, "E3.2.17.0", {"start": v(39.3, 229.8) * mm, "end": v(39.3, 240.1) * mm});
            skLineSegment(sketch, "E3.2.17.1", {"start": v(39.3, 240.1) * mm, "end": v(49.6, 240.1) * mm});
            skLineSegment(sketch, "E3.2.17.2", {"start": v(39.3, 229.8) * mm, "end": v(49.6, 229.8) * mm});
            skLineSegment(sketch, "E3.2.17.3", {"start": v(49.6, 229.8) * mm, "end": v(49.6, 240.1) * mm});
            skLineSegment(sketch, "E3.2.18.0", {"start": v(39.3, 242.5) * mm, "end": v(39.3, 252.8) * mm});
            skLineSegment(sketch, "E3.2.18.1", {"start": v(39.3, 252.8) * mm, "end": v(49.6, 252.8) * mm});
            skLineSegment(sketch, "E3.2.18.2", {"start": v(39.3, 242.5) * mm, "end": v(49.6, 242.5) * mm});
            skLineSegment(sketch, "E3.2.18.3", {"start": v(49.6, 242.5) * mm, "end": v(49.6, 252.8) * mm});
            skLineSegment(sketch, "E3.2.19.0", {"start": v(39.3, 255.2) * mm, "end": v(39.3, 265.5) * mm});
            skLineSegment(sketch, "E3.2.19.1", {"start": v(39.3, 265.5) * mm, "end": v(49.6, 265.5) * mm});
            skLineSegment(sketch, "E3.2.19.2", {"start": v(39.3, 255.2) * mm, "end": v(49.6, 255.2) * mm});
            skLineSegment(sketch, "E3.2.19.3", {"start": v(49.6, 255.2) * mm, "end": v(49.6, 265.5) * mm});
            skLineSegment(sketch, "E3.2.20.0", {"start": v(39.3, 267.9) * mm, "end": v(39.3, 278.2) * mm});
            skLineSegment(sketch, "E3.2.20.1", {"start": v(39.3, 278.2) * mm, "end": v(49.6, 278.2) * mm});
            skLineSegment(sketch, "E3.2.20.2", {"start": v(39.3, 267.9) * mm, "end": v(49.6, 267.9) * mm});
            skLineSegment(sketch, "E3.2.20.3", {"start": v(49.6, 267.9) * mm, "end": v(49.6, 278.2) * mm});
            skLineSegment(sketch, "E3.2.21.0", {"start": v(39.3, 280.6) * mm, "end": v(39.3, 290.9) * mm});
            skLineSegment(sketch, "E3.2.21.1", {"start": v(39.3, 290.9) * mm, "end": v(49.6, 290.9) * mm});
            skLineSegment(sketch, "E3.2.21.2", {"start": v(39.3, 280.6) * mm, "end": v(49.6, 280.6) * mm});
            skLineSegment(sketch, "E3.2.21.3", {"start": v(49.6, 280.6) * mm, "end": v(49.6, 290.9) * mm});
            skLineSegment(sketch, "E3.3.0.0", {"start": v(52, 13.9) * mm, "end": v(52, 24.2) * mm});
            skLineSegment(sketch, "E3.3.0.1", {"start": v(52, 24.2) * mm, "end": v(62.3, 24.2) * mm});
            skLineSegment(sketch, "E3.3.0.2", {"start": v(52, 13.9) * mm, "end": v(62.3, 13.9) * mm});
            skLineSegment(sketch, "E3.3.0.3", {"start": v(62.3, 13.9) * mm, "end": v(62.3, 24.2) * mm});
            skLineSegment(sketch, "E3.3.1.0", {"start": v(52, 26.6) * mm, "end": v(52, 36.9) * mm});
            skLineSegment(sketch, "E3.3.1.1", {"start": v(52, 36.9) * mm, "end": v(62.3, 36.9) * mm});
            skLineSegment(sketch, "E3.3.1.2", {"start": v(52, 26.6) * mm, "end": v(62.3, 26.6) * mm});
            skLineSegment(sketch, "E3.3.1.3", {"start": v(62.3, 26.6) * mm, "end": v(62.3, 36.9) * mm});
            skLineSegment(sketch, "E3.3.2.0", {"start": v(52, 39.3) * mm, "end": v(52, 49.6) * mm});
            skLineSegment(sketch, "E3.3.2.1", {"start": v(52, 49.6) * mm, "end": v(62.3, 49.6) * mm});
            skLineSegment(sketch, "E3.3.2.2", {"start": v(52, 39.3) * mm, "end": v(62.3, 39.3) * mm});
            skLineSegment(sketch, "E3.3.2.3", {"start": v(62.3, 39.3) * mm, "end": v(62.3, 49.6) * mm});
            skLineSegment(sketch, "E3.3.3.0", {"start": v(52, 52) * mm, "end": v(52, 62.3) * mm});
            skLineSegment(sketch, "E3.3.3.1", {"start": v(52, 62.3) * mm, "end": v(62.3, 62.3) * mm});
            skLineSegment(sketch, "E3.3.3.2", {"start": v(52, 52) * mm, "end": v(62.3, 52) * mm});
            skLineSegment(sketch, "E3.3.3.3", {"start": v(62.3, 52) * mm, "end": v(62.3, 62.3) * mm});
            skLineSegment(sketch, "E3.3.4.0", {"start": v(52, 64.7) * mm, "end": v(52, 75) * mm});
            skLineSegment(sketch, "E3.3.4.1", {"start": v(52, 75) * mm, "end": v(62.3, 75) * mm});
            skLineSegment(sketch, "E3.3.4.2", {"start": v(52, 64.7) * mm, "end": v(62.3, 64.7) * mm});
            skLineSegment(sketch, "E3.3.4.3", {"start": v(62.3, 64.7) * mm, "end": v(62.3, 75) * mm});
            skLineSegment(sketch, "E3.3.5.0", {"start": v(52, 77.4) * mm, "end": v(52, 87.7) * mm});
            skLineSegment(sketch, "E3.3.5.1", {"start": v(52, 87.7) * mm, "end": v(62.3, 87.7) * mm});
            skLineSegment(sketch, "E3.3.5.2", {"start": v(52, 77.4) * mm, "end": v(62.3, 77.4) * mm});
            skLineSegment(sketch, "E3.3.5.3", {"start": v(62.3, 77.4) * mm, "end": v(62.3, 87.7) * mm});
            skLineSegment(sketch, "E3.3.6.0", {"start": v(52, 90.1) * mm, "end": v(52, 100.4) * mm});
            skLineSegment(sketch, "E3.3.6.1", {"start": v(52, 100.4) * mm, "end": v(62.3, 100.4) * mm});
            skLineSegment(sketch, "E3.3.6.2", {"start": v(52, 90.1) * mm, "end": v(62.3, 90.1) * mm});
            skLineSegment(sketch, "E3.3.6.3", {"start": v(62.3, 90.1) * mm, "end": v(62.3, 100.4) * mm});
            skLineSegment(sketch, "E3.3.7.0", {"start": v(52, 102.8) * mm, "end": v(52, 113.1) * mm});
            skLineSegment(sketch, "E3.3.7.1", {"start": v(52, 113.1) * mm, "end": v(62.3, 113.1) * mm});
            skLineSegment(sketch, "E3.3.7.2", {"start": v(52, 102.8) * mm, "end": v(62.3, 102.8) * mm});
            skLineSegment(sketch, "E3.3.7.3", {"start": v(62.3, 102.8) * mm, "end": v(62.3, 113.1) * mm});
            skLineSegment(sketch, "E3.3.8.0", {"start": v(52, 115.5) * mm, "end": v(52, 125.8) * mm});
            skLineSegment(sketch, "E3.3.8.1", {"start": v(52, 125.8) * mm, "end": v(62.3, 125.8) * mm});
            skLineSegment(sketch, "E3.3.8.2", {"start": v(52, 115.5) * mm, "end": v(62.3, 115.5) * mm});
            skLineSegment(sketch, "E3.3.8.3", {"start": v(62.3, 115.5) * mm, "end": v(62.3, 125.8) * mm});
            skLineSegment(sketch, "E3.3.9.0", {"start": v(52, 128.2) * mm, "end": v(52, 138.5) * mm});
            skLineSegment(sketch, "E3.3.9.1", {"start": v(52, 138.5) * mm, "end": v(62.3, 138.5) * mm});
            skLineSegment(sketch, "E3.3.9.2", {"start": v(52, 128.2) * mm, "end": v(62.3, 128.2) * mm});
            skLineSegment(sketch, "E3.3.9.3", {"start": v(62.3, 128.2) * mm, "end": v(62.3, 138.5) * mm});
            skLineSegment(sketch, "E3.3.10.0", {"start": v(52, 140.9) * mm, "end": v(52, 151.2) * mm});
            skLineSegment(sketch, "E3.3.10.1", {"start": v(52, 151.2) * mm, "end": v(62.3, 151.2) * mm});
            skLineSegment(sketch, "E3.3.10.2", {"start": v(52, 140.9) * mm, "end": v(62.3, 140.9) * mm});
            skLineSegment(sketch, "E3.3.10.3", {"start": v(62.3, 140.9) * mm, "end": v(62.3, 151.2) * mm});
            skLineSegment(sketch, "E3.3.11.0", {"start": v(52, 153.6) * mm, "end": v(52, 163.9) * mm});
            skLineSegment(sketch, "E3.3.11.1", {"start": v(52, 163.9) * mm, "end": v(62.3, 163.9) * mm});
            skLineSegment(sketch, "E3.3.11.2", {"start": v(52, 153.6) * mm, "end": v(62.3, 153.6) * mm});
            skLineSegment(sketch, "E3.3.11.3", {"start": v(62.3, 153.6) * mm, "end": v(62.3, 163.9) * mm});
            skLineSegment(sketch, "E3.3.12.0", {"start": v(52, 166.3) * mm, "end": v(52, 176.6) * mm});
            skLineSegment(sketch, "E3.3.12.1", {"start": v(52, 176.6) * mm, "end": v(62.3, 176.6) * mm});
            skLineSegment(sketch, "E3.3.12.2", {"start": v(52, 166.3) * mm, "end": v(62.3, 166.3) * mm});
            skLineSegment(sketch, "E3.3.12.3", {"start": v(62.3, 166.3) * mm, "end": v(62.3, 176.6) * mm});
            skLineSegment(sketch, "E3.3.13.0", {"start": v(52, 179) * mm, "end": v(52, 189.3) * mm});
            skLineSegment(sketch, "E3.3.13.1", {"start": v(52, 189.3) * mm, "end": v(62.3, 189.3) * mm});
            skLineSegment(sketch, "E3.3.13.2", {"start": v(52, 179) * mm, "end": v(62.3, 179) * mm});
            skLineSegment(sketch, "E3.3.13.3", {"start": v(62.3, 179) * mm, "end": v(62.3, 189.3) * mm});
            skLineSegment(sketch, "E3.3.14.0", {"start": v(52, 191.7) * mm, "end": v(52, 202) * mm});
            skLineSegment(sketch, "E3.3.14.1", {"start": v(52, 202) * mm, "end": v(62.3, 202) * mm});
            skLineSegment(sketch, "E3.3.14.2", {"start": v(52, 191.7) * mm, "end": v(62.3, 191.7) * mm});
            skLineSegment(sketch, "E3.3.14.3", {"start": v(62.3, 191.7) * mm, "end": v(62.3, 202) * mm});
            skLineSegment(sketch, "E3.3.15.0", {"start": v(52, 204.4) * mm, "end": v(52, 214.7) * mm});
            skLineSegment(sketch, "E3.3.15.1", {"start": v(52, 214.7) * mm, "end": v(62.3, 214.7) * mm});
            skLineSegment(sketch, "E3.3.15.2", {"start": v(52, 204.4) * mm, "end": v(62.3, 204.4) * mm});
            skLineSegment(sketch, "E3.3.15.3", {"start": v(62.3, 204.4) * mm, "end": v(62.3, 214.7) * mm});
            skLineSegment(sketch, "E3.3.16.0", {"start": v(52, 217.1) * mm, "end": v(52, 227.4) * mm});
            skLineSegment(sketch, "E3.3.16.1", {"start": v(52, 227.4) * mm, "end": v(62.3, 227.4) * mm});
            skLineSegment(sketch, "E3.3.16.2", {"start": v(52, 217.1) * mm, "end": v(62.3, 217.1) * mm});
            skLineSegment(sketch, "E3.3.16.3", {"start": v(62.3, 217.1) * mm, "end": v(62.3, 227.4) * mm});
            skLineSegment(sketch, "E3.3.17.0", {"start": v(52, 229.8) * mm, "end": v(52, 240.1) * mm});
            skLineSegment(sketch, "E3.3.17.1", {"start": v(52, 240.1) * mm, "end": v(62.3, 240.1) * mm});
            skLineSegment(sketch, "E3.3.17.2", {"start": v(52, 229.8) * mm, "end": v(62.3, 229.8) * mm});
            skLineSegment(sketch, "E3.3.17.3", {"start": v(62.3, 229.8) * mm, "end": v(62.3, 240.1) * mm});
            skLineSegment(sketch, "E3.3.18.0", {"start": v(52, 242.5) * mm, "end": v(52, 252.8) * mm});
            skLineSegment(sketch, "E3.3.18.1", {"start": v(52, 252.8) * mm, "end": v(62.3, 252.8) * mm});
            skLineSegment(sketch, "E3.3.18.2", {"start": v(52, 242.5) * mm, "end": v(62.3, 242.5) * mm});
            skLineSegment(sketch, "E3.3.18.3", {"start": v(62.3, 242.5) * mm, "end": v(62.3, 252.8) * mm});
            skLineSegment(sketch, "E3.3.19.0", {"start": v(52, 255.2) * mm, "end": v(52, 265.5) * mm});
            skLineSegment(sketch, "E3.3.19.1", {"start": v(52, 265.5) * mm, "end": v(62.3, 265.5) * mm});
            skLineSegment(sketch, "E3.3.19.2", {"start": v(52, 255.2) * mm, "end": v(62.3, 255.2) * mm});
            skLineSegment(sketch, "E3.3.19.3", {"start": v(62.3, 255.2) * mm, "end": v(62.3, 265.5) * mm});
            skLineSegment(sketch, "E3.3.20.0", {"start": v(52, 267.9) * mm, "end": v(52, 278.2) * mm});
            skLineSegment(sketch, "E3.3.20.1", {"start": v(52, 278.2) * mm, "end": v(62.3, 278.2) * mm});
            skLineSegment(sketch, "E3.3.20.2", {"start": v(52, 267.9) * mm, "end": v(62.3, 267.9) * mm});
            skLineSegment(sketch, "E3.3.20.3", {"start": v(62.3, 267.9) * mm, "end": v(62.3, 278.2) * mm});
            skLineSegment(sketch, "E3.3.21.0", {"start": v(52, 280.6) * mm, "end": v(52, 290.9) * mm});
            skLineSegment(sketch, "E3.3.21.1", {"start": v(52, 290.9) * mm, "end": v(62.3, 290.9) * mm});
            skLineSegment(sketch, "E3.3.21.2", {"start": v(52, 280.6) * mm, "end": v(62.3, 280.6) * mm});
            skLineSegment(sketch, "E3.3.21.3", {"start": v(62.3, 280.6) * mm, "end": v(62.3, 290.9) * mm});
            skLineSegment(sketch, "E3.4.0.0", {"start": v(64.7, 13.9) * mm, "end": v(64.7, 24.2) * mm});
            skLineSegment(sketch, "E3.4.0.1", {"start": v(64.7, 24.2) * mm, "end": v(75, 24.2) * mm});
            skLineSegment(sketch, "E3.4.0.2", {"start": v(64.7, 13.9) * mm, "end": v(75, 13.9) * mm});
            skLineSegment(sketch, "E3.4.0.3", {"start": v(75, 13.9) * mm, "end": v(75, 24.2) * mm});
            skLineSegment(sketch, "E3.4.1.0", {"start": v(64.7, 26.6) * mm, "end": v(64.7, 36.9) * mm});
            skLineSegment(sketch, "E3.4.1.1", {"start": v(64.7, 36.9) * mm, "end": v(75, 36.9) * mm});
            skLineSegment(sketch, "E3.4.1.2", {"start": v(64.7, 26.6) * mm, "end": v(75, 26.6) * mm});
            skLineSegment(sketch, "E3.4.1.3", {"start": v(75, 26.6) * mm, "end": v(75, 36.9) * mm});
            skLineSegment(sketch, "E3.4.2.0", {"start": v(64.7, 39.3) * mm, "end": v(64.7, 49.6) * mm});
            skLineSegment(sketch, "E3.4.2.1", {"start": v(64.7, 49.6) * mm, "end": v(75, 49.6) * mm});
            skLineSegment(sketch, "E3.4.2.2", {"start": v(64.7, 39.3) * mm, "end": v(75, 39.3) * mm});
            skLineSegment(sketch, "E3.4.2.3", {"start": v(75, 39.3) * mm, "end": v(75, 49.6) * mm});
            skLineSegment(sketch, "E3.4.3.0", {"start": v(64.7, 52) * mm, "end": v(64.7, 62.3) * mm});
            skLineSegment(sketch, "E3.4.3.1", {"start": v(64.7, 62.3) * mm, "end": v(75, 62.3) * mm});
            skLineSegment(sketch, "E3.4.3.2", {"start": v(64.7, 52) * mm, "end": v(75, 52) * mm});
            skLineSegment(sketch, "E3.4.3.3", {"start": v(75, 52) * mm, "end": v(75, 62.3) * mm});
            skLineSegment(sketch, "E3.4.4.0", {"start": v(64.7, 64.7) * mm, "end": v(64.7, 75) * mm});
            skLineSegment(sketch, "E3.4.4.1", {"start": v(64.7, 75) * mm, "end": v(75, 75) * mm});
            skLineSegment(sketch, "E3.4.4.2", {"start": v(64.7, 64.7) * mm, "end": v(75, 64.7) * mm});
            skLineSegment(sketch, "E3.4.4.3", {"start": v(75, 64.7) * mm, "end": v(75, 75) * mm});
            skLineSegment(sketch, "E3.4.5.0", {"start": v(64.7, 77.4) * mm, "end": v(64.7, 87.7) * mm});
            skLineSegment(sketch, "E3.4.5.1", {"start": v(64.7, 87.7) * mm, "end": v(75, 87.7) * mm});
            skLineSegment(sketch, "E3.4.5.2", {"start": v(64.7, 77.4) * mm, "end": v(75, 77.4) * mm});
            skLineSegment(sketch, "E3.4.5.3", {"start": v(75, 77.4) * mm, "end": v(75, 87.7) * mm});
            skLineSegment(sketch, "E3.4.6.0", {"start": v(64.7, 90.1) * mm, "end": v(64.7, 100.4) * mm});
            skLineSegment(sketch, "E3.4.6.1", {"start": v(64.7, 100.4) * mm, "end": v(75, 100.4) * mm});
            skLineSegment(sketch, "E3.4.6.2", {"start": v(64.7, 90.1) * mm, "end": v(75, 90.1) * mm});
            skLineSegment(sketch, "E3.4.6.3", {"start": v(75, 90.1) * mm, "end": v(75, 100.4) * mm});
            skLineSegment(sketch, "E3.4.7.0", {"start": v(64.7, 102.8) * mm, "end": v(64.7, 113.1) * mm});
            skLineSegment(sketch, "E3.4.7.1", {"start": v(64.7, 113.1) * mm, "end": v(75, 113.1) * mm});
            skLineSegment(sketch, "E3.4.7.2", {"start": v(64.7, 102.8) * mm, "end": v(75, 102.8) * mm});
            skLineSegment(sketch, "E3.4.7.3", {"start": v(75, 102.8) * mm, "end": v(75, 113.1) * mm});
            skLineSegment(sketch, "E3.4.8.0", {"start": v(64.7, 115.5) * mm, "end": v(64.7, 125.8) * mm});
            skLineSegment(sketch, "E3.4.8.1", {"start": v(64.7, 125.8) * mm, "end": v(75, 125.8) * mm});
            skLineSegment(sketch, "E3.4.8.2", {"start": v(64.7, 115.5) * mm, "end": v(75, 115.5) * mm});
            skLineSegment(sketch, "E3.4.8.3", {"start": v(75, 115.5) * mm, "end": v(75, 125.8) * mm});
            skLineSegment(sketch, "E3.4.9.0", {"start": v(64.7, 128.2) * mm, "end": v(64.7, 138.5) * mm});
            skLineSegment(sketch, "E3.4.9.1", {"start": v(64.7, 138.5) * mm, "end": v(75, 138.5) * mm});
            skLineSegment(sketch, "E3.4.9.2", {"start": v(64.7, 128.2) * mm, "end": v(75, 128.2) * mm});
            skLineSegment(sketch, "E3.4.9.3", {"start": v(75, 128.2) * mm, "end": v(75, 138.5) * mm});
            skLineSegment(sketch, "E3.4.10.0", {"start": v(64.7, 140.9) * mm, "end": v(64.7, 151.2) * mm});
            skLineSegment(sketch, "E3.4.10.1", {"start": v(64.7, 151.2) * mm, "end": v(75, 151.2) * mm});
            skLineSegment(sketch, "E3.4.10.2", {"start": v(64.7, 140.9) * mm, "end": v(75, 140.9) * mm});
            skLineSegment(sketch, "E3.4.10.3", {"start": v(75, 140.9) * mm, "end": v(75, 151.2) * mm});
            skLineSegment(sketch, "E3.4.11.0", {"start": v(64.7, 153.6) * mm, "end": v(64.7, 163.9) * mm});
            skLineSegment(sketch, "E3.4.11.1", {"start": v(64.7, 163.9) * mm, "end": v(75, 163.9) * mm});
            skLineSegment(sketch, "E3.4.11.2", {"start": v(64.7, 153.6) * mm, "end": v(75, 153.6) * mm});
            skLineSegment(sketch, "E3.4.11.3", {"start": v(75, 153.6) * mm, "end": v(75, 163.9) * mm});
            skLineSegment(sketch, "E3.4.12.0", {"start": v(64.7, 166.3) * mm, "end": v(64.7, 176.6) * mm});
            skLineSegment(sketch, "E3.4.12.1", {"start": v(64.7, 176.6) * mm, "end": v(75, 176.6) * mm});
            skLineSegment(sketch, "E3.4.12.2", {"start": v(64.7, 166.3) * mm, "end": v(75, 166.3) * mm});
            skLineSegment(sketch, "E3.4.12.3", {"start": v(75, 166.3) * mm, "end": v(75, 176.6) * mm});
            skLineSegment(sketch, "E3.4.13.0", {"start": v(64.7, 179) * mm, "end": v(64.7, 189.3) * mm});
            skLineSegment(sketch, "E3.4.13.1", {"start": v(64.7, 189.3) * mm, "end": v(75, 189.3) * mm});
            skLineSegment(sketch, "E3.4.13.2", {"start": v(64.7, 179) * mm, "end": v(75, 179) * mm});
            skLineSegment(sketch, "E3.4.13.3", {"start": v(75, 179) * mm, "end": v(75, 189.3) * mm});
            skLineSegment(sketch, "E3.4.14.0", {"start": v(64.7, 191.7) * mm, "end": v(64.7, 202) * mm});
            skLineSegment(sketch, "E3.4.14.1", {"start": v(64.7, 202) * mm, "end": v(75, 202) * mm});
            skLineSegment(sketch, "E3.4.14.2", {"start": v(64.7, 191.7) * mm, "end": v(75, 191.7) * mm});
            skLineSegment(sketch, "E3.4.14.3", {"start": v(75, 191.7) * mm, "end": v(75, 202) * mm});
            skLineSegment(sketch, "E3.4.15.0", {"start": v(64.7, 204.4) * mm, "end": v(64.7, 214.7) * mm});
            skLineSegment(sketch, "E3.4.15.1", {"start": v(64.7, 214.7) * mm, "end": v(75, 214.7) * mm});
            skLineSegment(sketch, "E3.4.15.2", {"start": v(64.7, 204.4) * mm, "end": v(75, 204.4) * mm});
            skLineSegment(sketch, "E3.4.15.3", {"start": v(75, 204.4) * mm, "end": v(75, 214.7) * mm});
            skLineSegment(sketch, "E3.4.16.0", {"start": v(64.7, 217.1) * mm, "end": v(64.7, 227.4) * mm});
            skLineSegment(sketch, "E3.4.16.1", {"start": v(64.7, 227.4) * mm, "end": v(75, 227.4) * mm});
            skLineSegment(sketch, "E3.4.16.2", {"start": v(64.7, 217.1) * mm, "end": v(75, 217.1) * mm});
            skLineSegment(sketch, "E3.4.16.3", {"start": v(75, 217.1) * mm, "end": v(75, 227.4) * mm});
            skLineSegment(sketch, "E3.4.17.0", {"start": v(64.7, 229.8) * mm, "end": v(64.7, 240.1) * mm});
            skLineSegment(sketch, "E3.4.17.1", {"start": v(64.7, 240.1) * mm, "end": v(75, 240.1) * mm});
            skLineSegment(sketch, "E3.4.17.2", {"start": v(64.7, 229.8) * mm, "end": v(75, 229.8) * mm});
            skLineSegment(sketch, "E3.4.17.3", {"start": v(75, 229.8) * mm, "end": v(75, 240.1) * mm});
            skLineSegment(sketch, "E3.4.18.0", {"start": v(64.7, 242.5) * mm, "end": v(64.7, 252.8) * mm});
            skLineSegment(sketch, "E3.4.18.1", {"start": v(64.7, 252.8) * mm, "end": v(75, 252.8) * mm});
            skLineSegment(sketch, "E3.4.18.2", {"start": v(64.7, 242.5) * mm, "end": v(75, 242.5) * mm});
            skLineSegment(sketch, "E3.4.18.3", {"start": v(75, 242.5) * mm, "end": v(75, 252.8) * mm});
            skLineSegment(sketch, "E3.4.19.0", {"start": v(64.7, 255.2) * mm, "end": v(64.7, 265.5) * mm});
            skLineSegment(sketch, "E3.4.19.1", {"start": v(64.7, 265.5) * mm, "end": v(75, 265.5) * mm});
            skLineSegment(sketch, "E3.4.19.2", {"start": v(64.7, 255.2) * mm, "end": v(75, 255.2) * mm});
            skLineSegment(sketch, "E3.4.19.3", {"start": v(75, 255.2) * mm, "end": v(75, 265.5) * mm});
            skLineSegment(sketch, "E3.4.20.0", {"start": v(64.7, 267.9) * mm, "end": v(64.7, 278.2) * mm});
            skLineSegment(sketch, "E3.4.20.1", {"start": v(64.7, 278.2) * mm, "end": v(75, 278.2) * mm});
            skLineSegment(sketch, "E3.4.20.2", {"start": v(64.7, 267.9) * mm, "end": v(75, 267.9) * mm});
            skLineSegment(sketch, "E3.4.20.3", {"start": v(75, 267.9) * mm, "end": v(75, 278.2) * mm});
            skLineSegment(sketch, "E3.4.21.0", {"start": v(64.7, 280.6) * mm, "end": v(64.7, 290.9) * mm});
            skLineSegment(sketch, "E3.4.21.1", {"start": v(64.7, 290.9) * mm, "end": v(75, 290.9) * mm});
            skLineSegment(sketch, "E3.4.21.2", {"start": v(64.7, 280.6) * mm, "end": v(75, 280.6) * mm});
            skLineSegment(sketch, "E3.4.21.3", {"start": v(75, 280.6) * mm, "end": v(75, 290.9) * mm});
            skLineSegment(sketch, "E3.5.0.0", {"start": v(77.4, 13.9) * mm, "end": v(77.4, 24.2) * mm});
            skLineSegment(sketch, "E3.5.0.1", {"start": v(77.4, 24.2) * mm, "end": v(87.7, 24.2) * mm});
            skLineSegment(sketch, "E3.5.0.2", {"start": v(77.4, 13.9) * mm, "end": v(87.7, 13.9) * mm});
            skLineSegment(sketch, "E3.5.0.3", {"start": v(87.7, 13.9) * mm, "end": v(87.7, 24.2) * mm});
            skLineSegment(sketch, "E3.5.1.0", {"start": v(77.4, 26.6) * mm, "end": v(77.4, 36.9) * mm});
            skLineSegment(sketch, "E3.5.1.1", {"start": v(77.4, 36.9) * mm, "end": v(87.7, 36.9) * mm});
            skLineSegment(sketch, "E3.5.1.2", {"start": v(77.4, 26.6) * mm, "end": v(87.7, 26.6) * mm});
            skLineSegment(sketch, "E3.5.1.3", {"start": v(87.7, 26.6) * mm, "end": v(87.7, 36.9) * mm});
            skLineSegment(sketch, "E3.5.2.0", {"start": v(77.4, 39.3) * mm, "end": v(77.4, 49.6) * mm});
            skLineSegment(sketch, "E3.5.2.1", {"start": v(77.4, 49.6) * mm, "end": v(87.7, 49.6) * mm});
            skLineSegment(sketch, "E3.5.2.2", {"start": v(77.4, 39.3) * mm, "end": v(87.7, 39.3) * mm});
            skLineSegment(sketch, "E3.5.2.3", {"start": v(87.7, 39.3) * mm, "end": v(87.7, 49.6) * mm});
            skLineSegment(sketch, "E3.5.3.0", {"start": v(77.4, 52) * mm, "end": v(77.4, 62.3) * mm});
            skLineSegment(sketch, "E3.5.3.1", {"start": v(77.4, 62.3) * mm, "end": v(87.7, 62.3) * mm});
            skLineSegment(sketch, "E3.5.3.2", {"start": v(77.4, 52) * mm, "end": v(87.7, 52) * mm});
            skLineSegment(sketch, "E3.5.3.3", {"start": v(87.7, 52) * mm, "end": v(87.7, 62.3) * mm});
            skLineSegment(sketch, "E3.5.4.0", {"start": v(77.4, 64.7) * mm, "end": v(77.4, 75) * mm});
            skLineSegment(sketch, "E3.5.4.1", {"start": v(77.4, 75) * mm, "end": v(87.7, 75) * mm});
            skLineSegment(sketch, "E3.5.4.2", {"start": v(77.4, 64.7) * mm, "end": v(87.7, 64.7) * mm});
            skLineSegment(sketch, "E3.5.4.3", {"start": v(87.7, 64.7) * mm, "end": v(87.7, 75) * mm});
            skLineSegment(sketch, "E3.5.5.0", {"start": v(77.4, 77.4) * mm, "end": v(77.4, 87.7) * mm});
            skLineSegment(sketch, "E3.5.5.1", {"start": v(77.4, 87.7) * mm, "end": v(87.7, 87.7) * mm});
            skLineSegment(sketch, "E3.5.5.2", {"start": v(77.4, 77.4) * mm, "end": v(87.7, 77.4) * mm});
            skLineSegment(sketch, "E3.5.5.3", {"start": v(87.7, 77.4) * mm, "end": v(87.7, 87.7) * mm});
            skLineSegment(sketch, "E3.5.6.0", {"start": v(77.4, 90.1) * mm, "end": v(77.4, 100.4) * mm});
            skLineSegment(sketch, "E3.5.6.1", {"start": v(77.4, 100.4) * mm, "end": v(87.7, 100.4) * mm});
            skLineSegment(sketch, "E3.5.6.2", {"start": v(77.4, 90.1) * mm, "end": v(87.7, 90.1) * mm});
            skLineSegment(sketch, "E3.5.6.3", {"start": v(87.7, 90.1) * mm, "end": v(87.7, 100.4) * mm});
            skLineSegment(sketch, "E3.5.7.0", {"start": v(77.4, 102.8) * mm, "end": v(77.4, 113.1) * mm});
            skLineSegment(sketch, "E3.5.7.1", {"start": v(77.4, 113.1) * mm, "end": v(87.7, 113.1) * mm});
            skLineSegment(sketch, "E3.5.7.2", {"start": v(77.4, 102.8) * mm, "end": v(87.7, 102.8) * mm});
            skLineSegment(sketch, "E3.5.7.3", {"start": v(87.7, 102.8) * mm, "end": v(87.7, 113.1) * mm});
            skLineSegment(sketch, "E3.5.8.0", {"start": v(77.4, 115.5) * mm, "end": v(77.4, 125.8) * mm});
            skLineSegment(sketch, "E3.5.8.1", {"start": v(77.4, 125.8) * mm, "end": v(87.7, 125.8) * mm});
            skLineSegment(sketch, "E3.5.8.2", {"start": v(77.4, 115.5) * mm, "end": v(87.7, 115.5) * mm});
            skLineSegment(sketch, "E3.5.8.3", {"start": v(87.7, 115.5) * mm, "end": v(87.7, 125.8) * mm});
            skLineSegment(sketch, "E3.5.9.0", {"start": v(77.4, 128.2) * mm, "end": v(77.4, 138.5) * mm});
            skLineSegment(sketch, "E3.5.9.1", {"start": v(77.4, 138.5) * mm, "end": v(87.7, 138.5) * mm});
            skLineSegment(sketch, "E3.5.9.2", {"start": v(77.4, 128.2) * mm, "end": v(87.7, 128.2) * mm});
            skLineSegment(sketch, "E3.5.9.3", {"start": v(87.7, 128.2) * mm, "end": v(87.7, 138.5) * mm});
            skLineSegment(sketch, "E3.5.10.0", {"start": v(77.4, 140.9) * mm, "end": v(77.4, 151.2) * mm});
            skLineSegment(sketch, "E3.5.10.1", {"start": v(77.4, 151.2) * mm, "end": v(87.7, 151.2) * mm});
            skLineSegment(sketch, "E3.5.10.2", {"start": v(77.4, 140.9) * mm, "end": v(87.7, 140.9) * mm});
            skLineSegment(sketch, "E3.5.10.3", {"start": v(87.7, 140.9) * mm, "end": v(87.7, 151.2) * mm});
            skLineSegment(sketch, "E3.5.11.0", {"start": v(77.4, 153.6) * mm, "end": v(77.4, 163.9) * mm});
            skLineSegment(sketch, "E3.5.11.1", {"start": v(77.4, 163.9) * mm, "end": v(87.7, 163.9) * mm});
            skLineSegment(sketch, "E3.5.11.2", {"start": v(77.4, 153.6) * mm, "end": v(87.7, 153.6) * mm});
            skLineSegment(sketch, "E3.5.11.3", {"start": v(87.7, 153.6) * mm, "end": v(87.7, 163.9) * mm});
            skLineSegment(sketch, "E3.5.12.0", {"start": v(77.4, 166.3) * mm, "end": v(77.4, 176.6) * mm});
            skLineSegment(sketch, "E3.5.12.1", {"start": v(77.4, 176.6) * mm, "end": v(87.7, 176.6) * mm});
            skLineSegment(sketch, "E3.5.12.2", {"start": v(77.4, 166.3) * mm, "end": v(87.7, 166.3) * mm});
            skLineSegment(sketch, "E3.5.12.3", {"start": v(87.7, 166.3) * mm, "end": v(87.7, 176.6) * mm});
            skLineSegment(sketch, "E3.5.13.0", {"start": v(77.4, 179) * mm, "end": v(77.4, 189.3) * mm});
            skLineSegment(sketch, "E3.5.13.1", {"start": v(77.4, 189.3) * mm, "end": v(87.7, 189.3) * mm});
            skLineSegment(sketch, "E3.5.13.2", {"start": v(77.4, 179) * mm, "end": v(87.7, 179) * mm});
            skLineSegment(sketch, "E3.5.13.3", {"start": v(87.7, 179) * mm, "end": v(87.7, 189.3) * mm});
            skLineSegment(sketch, "E3.5.14.0", {"start": v(77.4, 191.7) * mm, "end": v(77.4, 202) * mm});
            skLineSegment(sketch, "E3.5.14.1", {"start": v(77.4, 202) * mm, "end": v(87.7, 202) * mm});
            skLineSegment(sketch, "E3.5.14.2", {"start": v(77.4, 191.7) * mm, "end": v(87.7, 191.7) * mm});
            skLineSegment(sketch, "E3.5.14.3", {"start": v(87.7, 191.7) * mm, "end": v(87.7, 202) * mm});
            skLineSegment(sketch, "E3.5.15.0", {"start": v(77.4, 204.4) * mm, "end": v(77.4, 214.7) * mm});
            skLineSegment(sketch, "E3.5.15.1", {"start": v(77.4, 214.7) * mm, "end": v(87.7, 214.7) * mm});
            skLineSegment(sketch, "E3.5.15.2", {"start": v(77.4, 204.4) * mm, "end": v(87.7, 204.4) * mm});
            skLineSegment(sketch, "E3.5.15.3", {"start": v(87.7, 204.4) * mm, "end": v(87.7, 214.7) * mm});
            skLineSegment(sketch, "E3.5.16.0", {"start": v(77.4, 217.1) * mm, "end": v(77.4, 227.4) * mm});
            skLineSegment(sketch, "E3.5.16.1", {"start": v(77.4, 227.4) * mm, "end": v(87.7, 227.4) * mm});
            skLineSegment(sketch, "E3.5.16.2", {"start": v(77.4, 217.1) * mm, "end": v(87.7, 217.1) * mm});
            skLineSegment(sketch, "E3.5.16.3", {"start": v(87.7, 217.1) * mm, "end": v(87.7, 227.4) * mm});
            skLineSegment(sketch, "E3.5.17.0", {"start": v(77.4, 229.8) * mm, "end": v(77.4, 240.1) * mm});
            skLineSegment(sketch, "E3.5.17.1", {"start": v(77.4, 240.1) * mm, "end": v(87.7, 240.1) * mm});
            skLineSegment(sketch, "E3.5.17.2", {"start": v(77.4, 229.8) * mm, "end": v(87.7, 229.8) * mm});
            skLineSegment(sketch, "E3.5.17.3", {"start": v(87.7, 229.8) * mm, "end": v(87.7, 240.1) * mm});
            skLineSegment(sketch, "E3.5.18.0", {"start": v(77.4, 242.5) * mm, "end": v(77.4, 252.8) * mm});
            skLineSegment(sketch, "E3.5.18.1", {"start": v(77.4, 252.8) * mm, "end": v(87.7, 252.8) * mm});
            skLineSegment(sketch, "E3.5.18.2", {"start": v(77.4, 242.5) * mm, "end": v(87.7, 242.5) * mm});
            skLineSegment(sketch, "E3.5.18.3", {"start": v(87.7, 242.5) * mm, "end": v(87.7, 252.8) * mm});
            skLineSegment(sketch, "E3.5.19.0", {"start": v(77.4, 255.2) * mm, "end": v(77.4, 265.5) * mm});
            skLineSegment(sketch, "E3.5.19.1", {"start": v(77.4, 265.5) * mm, "end": v(87.7, 265.5) * mm});
            skLineSegment(sketch, "E3.5.19.2", {"start": v(77.4, 255.2) * mm, "end": v(87.7, 255.2) * mm});
            skLineSegment(sketch, "E3.5.19.3", {"start": v(87.7, 255.2) * mm, "end": v(87.7, 265.5) * mm});
            skLineSegment(sketch, "E3.5.20.0", {"start": v(77.4, 267.9) * mm, "end": v(77.4, 278.2) * mm});
            skLineSegment(sketch, "E3.5.20.1", {"start": v(77.4, 278.2) * mm, "end": v(87.7, 278.2) * mm});
            skLineSegment(sketch, "E3.5.20.2", {"start": v(77.4, 267.9) * mm, "end": v(87.7, 267.9) * mm});
            skLineSegment(sketch, "E3.5.20.3", {"start": v(87.7, 267.9) * mm, "end": v(87.7, 278.2) * mm});
            skLineSegment(sketch, "E3.5.21.0", {"start": v(77.4, 280.6) * mm, "end": v(77.4, 290.9) * mm});
            skLineSegment(sketch, "E3.5.21.1", {"start": v(77.4, 290.9) * mm, "end": v(87.7, 290.9) * mm});
            skLineSegment(sketch, "E3.5.21.2", {"start": v(77.4, 280.6) * mm, "end": v(87.7, 280.6) * mm});
            skLineSegment(sketch, "E3.5.21.3", {"start": v(87.7, 280.6) * mm, "end": v(87.7, 290.9) * mm});
            skLineSegment(sketch, "E3.6.0.0", {"start": v(90.1, 13.9) * mm, "end": v(90.1, 24.2) * mm});
            skLineSegment(sketch, "E3.6.0.1", {"start": v(90.1, 24.2) * mm, "end": v(100.4, 24.2) * mm});
            skLineSegment(sketch, "E3.6.0.2", {"start": v(90.1, 13.9) * mm, "end": v(100.4, 13.9) * mm});
            skLineSegment(sketch, "E3.6.0.3", {"start": v(100.4, 13.9) * mm, "end": v(100.4, 24.2) * mm});
            skLineSegment(sketch, "E3.6.1.0", {"start": v(90.1, 26.6) * mm, "end": v(90.1, 36.9) * mm});
            skLineSegment(sketch, "E3.6.1.1", {"start": v(90.1, 36.9) * mm, "end": v(100.4, 36.9) * mm});
            skLineSegment(sketch, "E3.6.1.2", {"start": v(90.1, 26.6) * mm, "end": v(100.4, 26.6) * mm});
            skLineSegment(sketch, "E3.6.1.3", {"start": v(100.4, 26.6) * mm, "end": v(100.4, 36.9) * mm});
            skLineSegment(sketch, "E3.6.2.0", {"start": v(90.1, 39.3) * mm, "end": v(90.1, 49.6) * mm});
            skLineSegment(sketch, "E3.6.2.1", {"start": v(90.1, 49.6) * mm, "end": v(100.4, 49.6) * mm});
            skLineSegment(sketch, "E3.6.2.2", {"start": v(90.1, 39.3) * mm, "end": v(100.4, 39.3) * mm});
            skLineSegment(sketch, "E3.6.2.3", {"start": v(100.4, 39.3) * mm, "end": v(100.4, 49.6) * mm});
            skLineSegment(sketch, "E3.6.3.0", {"start": v(90.1, 52) * mm, "end": v(90.1, 62.3) * mm});
            skLineSegment(sketch, "E3.6.3.1", {"start": v(90.1, 62.3) * mm, "end": v(100.4, 62.3) * mm});
            skLineSegment(sketch, "E3.6.3.2", {"start": v(90.1, 52) * mm, "end": v(100.4, 52) * mm});
            skLineSegment(sketch, "E3.6.3.3", {"start": v(100.4, 52) * mm, "end": v(100.4, 62.3) * mm});
            skLineSegment(sketch, "E3.6.4.0", {"start": v(90.1, 64.7) * mm, "end": v(90.1, 75) * mm});
            skLineSegment(sketch, "E3.6.4.1", {"start": v(90.1, 75) * mm, "end": v(100.4, 75) * mm});
            skLineSegment(sketch, "E3.6.4.2", {"start": v(90.1, 64.7) * mm, "end": v(100.4, 64.7) * mm});
            skLineSegment(sketch, "E3.6.4.3", {"start": v(100.4, 64.7) * mm, "end": v(100.4, 75) * mm});
            skLineSegment(sketch, "E3.6.5.0", {"start": v(90.1, 77.4) * mm, "end": v(90.1, 87.7) * mm});
            skLineSegment(sketch, "E3.6.5.1", {"start": v(90.1, 87.7) * mm, "end": v(100.4, 87.7) * mm});
            skLineSegment(sketch, "E3.6.5.2", {"start": v(90.1, 77.4) * mm, "end": v(100.4, 77.4) * mm});
            skLineSegment(sketch, "E3.6.5.3", {"start": v(100.4, 77.4) * mm, "end": v(100.4, 87.7) * mm});
            skLineSegment(sketch, "E3.6.6.0", {"start": v(90.1, 90.1) * mm, "end": v(90.1, 100.4) * mm});
            skLineSegment(sketch, "E3.6.6.1", {"start": v(90.1, 100.4) * mm, "end": v(100.4, 100.4) * mm});
            skLineSegment(sketch, "E3.6.6.2", {"start": v(90.1, 90.1) * mm, "end": v(100.4, 90.1) * mm});
            skLineSegment(sketch, "E3.6.6.3", {"start": v(100.4, 90.1) * mm, "end": v(100.4, 100.4) * mm});
            skLineSegment(sketch, "E3.6.7.0", {"start": v(90.1, 102.8) * mm, "end": v(90.1, 113.1) * mm});
            skLineSegment(sketch, "E3.6.7.1", {"start": v(90.1, 113.1) * mm, "end": v(100.4, 113.1) * mm});
            skLineSegment(sketch, "E3.6.7.2", {"start": v(90.1, 102.8) * mm, "end": v(100.4, 102.8) * mm});
            skLineSegment(sketch, "E3.6.7.3", {"start": v(100.4, 102.8) * mm, "end": v(100.4, 113.1) * mm});
            skLineSegment(sketch, "E3.6.8.0", {"start": v(90.1, 115.5) * mm, "end": v(90.1, 125.8) * mm});
            skLineSegment(sketch, "E3.6.8.1", {"start": v(90.1, 125.8) * mm, "end": v(100.4, 125.8) * mm});
            skLineSegment(sketch, "E3.6.8.2", {"start": v(90.1, 115.5) * mm, "end": v(100.4, 115.5) * mm});
            skLineSegment(sketch, "E3.6.8.3", {"start": v(100.4, 115.5) * mm, "end": v(100.4, 125.8) * mm});
            skLineSegment(sketch, "E3.6.9.0", {"start": v(90.1, 128.2) * mm, "end": v(90.1, 138.5) * mm});
            skLineSegment(sketch, "E3.6.9.1", {"start": v(90.1, 138.5) * mm, "end": v(100.4, 138.5) * mm});
            skLineSegment(sketch, "E3.6.9.2", {"start": v(90.1, 128.2) * mm, "end": v(100.4, 128.2) * mm});
            skLineSegment(sketch, "E3.6.9.3", {"start": v(100.4, 128.2) * mm, "end": v(100.4, 138.5) * mm});
            skLineSegment(sketch, "E3.6.10.0", {"start": v(90.1, 140.9) * mm, "end": v(90.1, 151.2) * mm});
            skLineSegment(sketch, "E3.6.10.1", {"start": v(90.1, 151.2) * mm, "end": v(100.4, 151.2) * mm});
            skLineSegment(sketch, "E3.6.10.2", {"start": v(90.1, 140.9) * mm, "end": v(100.4, 140.9) * mm});
            skLineSegment(sketch, "E3.6.10.3", {"start": v(100.4, 140.9) * mm, "end": v(100.4, 151.2) * mm});
            skLineSegment(sketch, "E3.6.11.0", {"start": v(90.1, 153.6) * mm, "end": v(90.1, 163.9) * mm});
            skLineSegment(sketch, "E3.6.11.1", {"start": v(90.1, 163.9) * mm, "end": v(100.4, 163.9) * mm});
            skLineSegment(sketch, "E3.6.11.2", {"start": v(90.1, 153.6) * mm, "end": v(100.4, 153.6) * mm});
            skLineSegment(sketch, "E3.6.11.3", {"start": v(100.4, 153.6) * mm, "end": v(100.4, 163.9) * mm});
            skLineSegment(sketch, "E3.6.12.0", {"start": v(90.1, 166.3) * mm, "end": v(90.1, 176.6) * mm});
            skLineSegment(sketch, "E3.6.12.1", {"start": v(90.1, 176.6) * mm, "end": v(100.4, 176.6) * mm});
            skLineSegment(sketch, "E3.6.12.2", {"start": v(90.1, 166.3) * mm, "end": v(100.4, 166.3) * mm});
            skLineSegment(sketch, "E3.6.12.3", {"start": v(100.4, 166.3) * mm, "end": v(100.4, 176.6) * mm});
            skLineSegment(sketch, "E3.6.13.0", {"start": v(90.1, 179) * mm, "end": v(90.1, 189.3) * mm});
            skLineSegment(sketch, "E3.6.13.1", {"start": v(90.1, 189.3) * mm, "end": v(100.4, 189.3) * mm});
            skLineSegment(sketch, "E3.6.13.2", {"start": v(90.1, 179) * mm, "end": v(100.4, 179) * mm});
            skLineSegment(sketch, "E3.6.13.3", {"start": v(100.4, 179) * mm, "end": v(100.4, 189.3) * mm});
            skLineSegment(sketch, "E3.6.14.0", {"start": v(90.1, 191.7) * mm, "end": v(90.1, 202) * mm});
            skLineSegment(sketch, "E3.6.14.1", {"start": v(90.1, 202) * mm, "end": v(100.4, 202) * mm});
            skLineSegment(sketch, "E3.6.14.2", {"start": v(90.1, 191.7) * mm, "end": v(100.4, 191.7) * mm});
            skLineSegment(sketch, "E3.6.14.3", {"start": v(100.4, 191.7) * mm, "end": v(100.4, 202) * mm});
            skLineSegment(sketch, "E3.6.15.0", {"start": v(90.1, 204.4) * mm, "end": v(90.1, 214.7) * mm});
            skLineSegment(sketch, "E3.6.15.1", {"start": v(90.1, 214.7) * mm, "end": v(100.4, 214.7) * mm});
            skLineSegment(sketch, "E3.6.15.2", {"start": v(90.1, 204.4) * mm, "end": v(100.4, 204.4) * mm});
            skLineSegment(sketch, "E3.6.15.3", {"start": v(100.4, 204.4) * mm, "end": v(100.4, 214.7) * mm});
            skLineSegment(sketch, "E3.6.16.0", {"start": v(90.1, 217.1) * mm, "end": v(90.1, 227.4) * mm});
            skLineSegment(sketch, "E3.6.16.1", {"start": v(90.1, 227.4) * mm, "end": v(100.4, 227.4) * mm});
            skLineSegment(sketch, "E3.6.16.2", {"start": v(90.1, 217.1) * mm, "end": v(100.4, 217.1) * mm});
            skLineSegment(sketch, "E3.6.16.3", {"start": v(100.4, 217.1) * mm, "end": v(100.4, 227.4) * mm});
            skLineSegment(sketch, "E3.6.17.0", {"start": v(90.1, 229.8) * mm, "end": v(90.1, 240.1) * mm});
            skLineSegment(sketch, "E3.6.17.1", {"start": v(90.1, 240.1) * mm, "end": v(100.4, 240.1) * mm});
            skLineSegment(sketch, "E3.6.17.2", {"start": v(90.1, 229.8) * mm, "end": v(100.4, 229.8) * mm});
            skLineSegment(sketch, "E3.6.17.3", {"start": v(100.4, 229.8) * mm, "end": v(100.4, 240.1) * mm});
            skLineSegment(sketch, "E3.6.18.0", {"start": v(90.1, 242.5) * mm, "end": v(90.1, 252.8) * mm});
            skLineSegment(sketch, "E3.6.18.1", {"start": v(90.1, 252.8) * mm, "end": v(100.4, 252.8) * mm});
            skLineSegment(sketch, "E3.6.18.2", {"start": v(90.1, 242.5) * mm, "end": v(100.4, 242.5) * mm});
            skLineSegment(sketch, "E3.6.18.3", {"start": v(100.4, 242.5) * mm, "end": v(100.4, 252.8) * mm});
            skLineSegment(sketch, "E3.6.19.0", {"start": v(90.1, 255.2) * mm, "end": v(90.1, 265.5) * mm});
            skLineSegment(sketch, "E3.6.19.1", {"start": v(90.1, 265.5) * mm, "end": v(100.4, 265.5) * mm});
            skLineSegment(sketch, "E3.6.19.2", {"start": v(90.1, 255.2) * mm, "end": v(100.4, 255.2) * mm});
            skLineSegment(sketch, "E3.6.19.3", {"start": v(100.4, 255.2) * mm, "end": v(100.4, 265.5) * mm});
            skLineSegment(sketch, "E3.6.20.0", {"start": v(90.1, 267.9) * mm, "end": v(90.1, 278.2) * mm});
            skLineSegment(sketch, "E3.6.20.1", {"start": v(90.1, 278.2) * mm, "end": v(100.4, 278.2) * mm});
            skLineSegment(sketch, "E3.6.20.2", {"start": v(90.1, 267.9) * mm, "end": v(100.4, 267.9) * mm});
            skLineSegment(sketch, "E3.6.20.3", {"start": v(100.4, 267.9) * mm, "end": v(100.4, 278.2) * mm});
            skLineSegment(sketch, "E3.6.21.0", {"start": v(90.1, 280.6) * mm, "end": v(90.1, 290.9) * mm});
            skLineSegment(sketch, "E3.6.21.1", {"start": v(90.1, 290.9) * mm, "end": v(100.4, 290.9) * mm});
            skLineSegment(sketch, "E3.6.21.2", {"start": v(90.1, 280.6) * mm, "end": v(100.4, 280.6) * mm});
            skLineSegment(sketch, "E3.6.21.3", {"start": v(100.4, 280.6) * mm, "end": v(100.4, 290.9) * mm});
            skLineSegment(sketch, "E3.7.0.0", {"start": v(102.8, 13.9) * mm, "end": v(102.8, 24.2) * mm});
            skLineSegment(sketch, "E3.7.0.1", {"start": v(102.8, 24.2) * mm, "end": v(113.1, 24.2) * mm});
            skLineSegment(sketch, "E3.7.0.2", {"start": v(102.8, 13.9) * mm, "end": v(113.1, 13.9) * mm});
            skLineSegment(sketch, "E3.7.0.3", {"start": v(113.1, 13.9) * mm, "end": v(113.1, 24.2) * mm});
            skLineSegment(sketch, "E3.7.1.0", {"start": v(102.8, 26.6) * mm, "end": v(102.8, 36.9) * mm});
            skLineSegment(sketch, "E3.7.1.1", {"start": v(102.8, 36.9) * mm, "end": v(113.1, 36.9) * mm});
            skLineSegment(sketch, "E3.7.1.2", {"start": v(102.8, 26.6) * mm, "end": v(113.1, 26.6) * mm});
            skLineSegment(sketch, "E3.7.1.3", {"start": v(113.1, 26.6) * mm, "end": v(113.1, 36.9) * mm});
            skLineSegment(sketch, "E3.7.2.0", {"start": v(102.8, 39.3) * mm, "end": v(102.8, 49.6) * mm});
            skLineSegment(sketch, "E3.7.2.1", {"start": v(102.8, 49.6) * mm, "end": v(113.1, 49.6) * mm});
            skLineSegment(sketch, "E3.7.2.2", {"start": v(102.8, 39.3) * mm, "end": v(113.1, 39.3) * mm});
            skLineSegment(sketch, "E3.7.2.3", {"start": v(113.1, 39.3) * mm, "end": v(113.1, 49.6) * mm});
            skLineSegment(sketch, "E3.7.3.0", {"start": v(102.8, 52) * mm, "end": v(102.8, 62.3) * mm});
            skLineSegment(sketch, "E3.7.3.1", {"start": v(102.8, 62.3) * mm, "end": v(113.1, 62.3) * mm});
            skLineSegment(sketch, "E3.7.3.2", {"start": v(102.8, 52) * mm, "end": v(113.1, 52) * mm});
            skLineSegment(sketch, "E3.7.3.3", {"start": v(113.1, 52) * mm, "end": v(113.1, 62.3) * mm});
            skLineSegment(sketch, "E3.7.4.0", {"start": v(102.8, 64.7) * mm, "end": v(102.8, 75) * mm});
            skLineSegment(sketch, "E3.7.4.1", {"start": v(102.8, 75) * mm, "end": v(113.1, 75) * mm});
            skLineSegment(sketch, "E3.7.4.2", {"start": v(102.8, 64.7) * mm, "end": v(113.1, 64.7) * mm});
            skLineSegment(sketch, "E3.7.4.3", {"start": v(113.1, 64.7) * mm, "end": v(113.1, 75) * mm});
            skLineSegment(sketch, "E3.7.5.0", {"start": v(102.8, 77.4) * mm, "end": v(102.8, 87.7) * mm});
            skLineSegment(sketch, "E3.7.5.1", {"start": v(102.8, 87.7) * mm, "end": v(113.1, 87.7) * mm});
            skLineSegment(sketch, "E3.7.5.2", {"start": v(102.8, 77.4) * mm, "end": v(113.1, 77.4) * mm});
            skLineSegment(sketch, "E3.7.5.3", {"start": v(113.1, 77.4) * mm, "end": v(113.1, 87.7) * mm});
            skLineSegment(sketch, "E3.7.6.0", {"start": v(102.8, 90.1) * mm, "end": v(102.8, 100.4) * mm});
            skLineSegment(sketch, "E3.7.6.1", {"start": v(102.8, 100.4) * mm, "end": v(113.1, 100.4) * mm});
            skLineSegment(sketch, "E3.7.6.2", {"start": v(102.8, 90.1) * mm, "end": v(113.1, 90.1) * mm});
            skLineSegment(sketch, "E3.7.6.3", {"start": v(113.1, 90.1) * mm, "end": v(113.1, 100.4) * mm});
            skLineSegment(sketch, "E3.7.7.0", {"start": v(102.8, 102.8) * mm, "end": v(102.8, 113.1) * mm});
            skLineSegment(sketch, "E3.7.7.1", {"start": v(102.8, 113.1) * mm, "end": v(113.1, 113.1) * mm});
            skLineSegment(sketch, "E3.7.7.2", {"start": v(102.8, 102.8) * mm, "end": v(113.1, 102.8) * mm});
            skLineSegment(sketch, "E3.7.7.3", {"start": v(113.1, 102.8) * mm, "end": v(113.1, 113.1) * mm});
            skLineSegment(sketch, "E3.7.8.0", {"start": v(102.8, 115.5) * mm, "end": v(102.8, 125.8) * mm});
            skLineSegment(sketch, "E3.7.8.1", {"start": v(102.8, 125.8) * mm, "end": v(113.1, 125.8) * mm});
            skLineSegment(sketch, "E3.7.8.2", {"start": v(102.8, 115.5) * mm, "end": v(113.1, 115.5) * mm});
            skLineSegment(sketch, "E3.7.8.3", {"start": v(113.1, 115.5) * mm, "end": v(113.1, 125.8) * mm});
            skLineSegment(sketch, "E3.7.9.0", {"start": v(102.8, 128.2) * mm, "end": v(102.8, 138.5) * mm});
            skLineSegment(sketch, "E3.7.9.1", {"start": v(102.8, 138.5) * mm, "end": v(113.1, 138.5) * mm});
            skLineSegment(sketch, "E3.7.9.2", {"start": v(102.8, 128.2) * mm, "end": v(113.1, 128.2) * mm});
            skLineSegment(sketch, "E3.7.9.3", {"start": v(113.1, 128.2) * mm, "end": v(113.1, 138.5) * mm});
            skLineSegment(sketch, "E3.7.10.0", {"start": v(102.8, 140.9) * mm, "end": v(102.8, 151.2) * mm});
            skLineSegment(sketch, "E3.7.10.1", {"start": v(102.8, 151.2) * mm, "end": v(113.1, 151.2) * mm});
            skLineSegment(sketch, "E3.7.10.2", {"start": v(102.8, 140.9) * mm, "end": v(113.1, 140.9) * mm});
            skLineSegment(sketch, "E3.7.10.3", {"start": v(113.1, 140.9) * mm, "end": v(113.1, 151.2) * mm});
            skLineSegment(sketch, "E3.7.11.0", {"start": v(102.8, 153.6) * mm, "end": v(102.8, 163.9) * mm});
            skLineSegment(sketch, "E3.7.11.1", {"start": v(102.8, 163.9) * mm, "end": v(113.1, 163.9) * mm});
            skLineSegment(sketch, "E3.7.11.2", {"start": v(102.8, 153.6) * mm, "end": v(113.1, 153.6) * mm});
            skLineSegment(sketch, "E3.7.11.3", {"start": v(113.1, 153.6) * mm, "end": v(113.1, 163.9) * mm});
            skLineSegment(sketch, "E3.7.12.0", {"start": v(102.8, 166.3) * mm, "end": v(102.8, 176.6) * mm});
            skLineSegment(sketch, "E3.7.12.1", {"start": v(102.8, 176.6) * mm, "end": v(113.1, 176.6) * mm});
            skLineSegment(sketch, "E3.7.12.2", {"start": v(102.8, 166.3) * mm, "end": v(113.1, 166.3) * mm});
            skLineSegment(sketch, "E3.7.12.3", {"start": v(113.1, 166.3) * mm, "end": v(113.1, 176.6) * mm});
            skLineSegment(sketch, "E3.7.13.0", {"start": v(102.8, 179) * mm, "end": v(102.8, 189.3) * mm});
            skLineSegment(sketch, "E3.7.13.1", {"start": v(102.8, 189.3) * mm, "end": v(113.1, 189.3) * mm});
            skLineSegment(sketch, "E3.7.13.2", {"start": v(102.8, 179) * mm, "end": v(113.1, 179) * mm});
            skLineSegment(sketch, "E3.7.13.3", {"start": v(113.1, 179) * mm, "end": v(113.1, 189.3) * mm});
            skLineSegment(sketch, "E3.7.14.0", {"start": v(102.8, 191.7) * mm, "end": v(102.8, 202) * mm});
            skLineSegment(sketch, "E3.7.14.1", {"start": v(102.8, 202) * mm, "end": v(113.1, 202) * mm});
            skLineSegment(sketch, "E3.7.14.2", {"start": v(102.8, 191.7) * mm, "end": v(113.1, 191.7) * mm});
            skLineSegment(sketch, "E3.7.14.3", {"start": v(113.1, 191.7) * mm, "end": v(113.1, 202) * mm});
            skLineSegment(sketch, "E3.7.15.0", {"start": v(102.8, 204.4) * mm, "end": v(102.8, 214.7) * mm});
            skLineSegment(sketch, "E3.7.15.1", {"start": v(102.8, 214.7) * mm, "end": v(113.1, 214.7) * mm});
            skLineSegment(sketch, "E3.7.15.2", {"start": v(102.8, 204.4) * mm, "end": v(113.1, 204.4) * mm});
            skLineSegment(sketch, "E3.7.15.3", {"start": v(113.1, 204.4) * mm, "end": v(113.1, 214.7) * mm});
            skLineSegment(sketch, "E3.7.16.0", {"start": v(102.8, 217.1) * mm, "end": v(102.8, 227.4) * mm});
            skLineSegment(sketch, "E3.7.16.1", {"start": v(102.8, 227.4) * mm, "end": v(113.1, 227.4) * mm});
            skLineSegment(sketch, "E3.7.16.2", {"start": v(102.8, 217.1) * mm, "end": v(113.1, 217.1) * mm});
            skLineSegment(sketch, "E3.7.16.3", {"start": v(113.1, 217.1) * mm, "end": v(113.1, 227.4) * mm});
            skLineSegment(sketch, "E3.7.17.0", {"start": v(102.8, 229.8) * mm, "end": v(102.8, 240.1) * mm});
            skLineSegment(sketch, "E3.7.17.1", {"start": v(102.8, 240.1) * mm, "end": v(113.1, 240.1) * mm});
            skLineSegment(sketch, "E3.7.17.2", {"start": v(102.8, 229.8) * mm, "end": v(113.1, 229.8) * mm});
            skLineSegment(sketch, "E3.7.17.3", {"start": v(113.1, 229.8) * mm, "end": v(113.1, 240.1) * mm});
            skLineSegment(sketch, "E3.7.18.0", {"start": v(102.8, 242.5) * mm, "end": v(102.8, 252.8) * mm});
            skLineSegment(sketch, "E3.7.18.1", {"start": v(102.8, 252.8) * mm, "end": v(113.1, 252.8) * mm});
            skLineSegment(sketch, "E3.7.18.2", {"start": v(102.8, 242.5) * mm, "end": v(113.1, 242.5) * mm});
            skLineSegment(sketch, "E3.7.18.3", {"start": v(113.1, 242.5) * mm, "end": v(113.1, 252.8) * mm});
            skLineSegment(sketch, "E3.7.19.0", {"start": v(102.8, 255.2) * mm, "end": v(102.8, 265.5) * mm});
            skLineSegment(sketch, "E3.7.19.1", {"start": v(102.8, 265.5) * mm, "end": v(113.1, 265.5) * mm});
            skLineSegment(sketch, "E3.7.19.2", {"start": v(102.8, 255.2) * mm, "end": v(113.1, 255.2) * mm});
            skLineSegment(sketch, "E3.7.19.3", {"start": v(113.1, 255.2) * mm, "end": v(113.1, 265.5) * mm});
            skLineSegment(sketch, "E3.7.20.0", {"start": v(102.8, 267.9) * mm, "end": v(102.8, 278.2) * mm});
            skLineSegment(sketch, "E3.7.20.1", {"start": v(102.8, 278.2) * mm, "end": v(113.1, 278.2) * mm});
            skLineSegment(sketch, "E3.7.20.2", {"start": v(102.8, 267.9) * mm, "end": v(113.1, 267.9) * mm});
            skLineSegment(sketch, "E3.7.20.3", {"start": v(113.1, 267.9) * mm, "end": v(113.1, 278.2) * mm});
            skLineSegment(sketch, "E3.7.21.0", {"start": v(102.8, 280.6) * mm, "end": v(102.8, 290.9) * mm});
            skLineSegment(sketch, "E3.7.21.1", {"start": v(102.8, 290.9) * mm, "end": v(113.1, 290.9) * mm});
            skLineSegment(sketch, "E3.7.21.2", {"start": v(102.8, 280.6) * mm, "end": v(113.1, 280.6) * mm});
            skLineSegment(sketch, "E3.7.21.3", {"start": v(113.1, 280.6) * mm, "end": v(113.1, 290.9) * mm});
            skLineSegment(sketch, "E3.8.0.0", {"start": v(115.5, 13.9) * mm, "end": v(115.5, 24.2) * mm});
            skLineSegment(sketch, "E3.8.0.1", {"start": v(115.5, 24.2) * mm, "end": v(125.8, 24.2) * mm});
            skLineSegment(sketch, "E3.8.0.2", {"start": v(115.5, 13.9) * mm, "end": v(125.8, 13.9) * mm});
            skLineSegment(sketch, "E3.8.0.3", {"start": v(125.8, 13.9) * mm, "end": v(125.8, 24.2) * mm});
            skLineSegment(sketch, "E3.8.1.0", {"start": v(115.5, 26.6) * mm, "end": v(115.5, 36.9) * mm});
            skLineSegment(sketch, "E3.8.1.1", {"start": v(115.5, 36.9) * mm, "end": v(125.8, 36.9) * mm});
            skLineSegment(sketch, "E3.8.1.2", {"start": v(115.5, 26.6) * mm, "end": v(125.8, 26.6) * mm});
            skLineSegment(sketch, "E3.8.1.3", {"start": v(125.8, 26.6) * mm, "end": v(125.8, 36.9) * mm});
            skLineSegment(sketch, "E3.8.2.0", {"start": v(115.5, 39.3) * mm, "end": v(115.5, 49.6) * mm});
            skLineSegment(sketch, "E3.8.2.1", {"start": v(115.5, 49.6) * mm, "end": v(125.8, 49.6) * mm});
            skLineSegment(sketch, "E3.8.2.2", {"start": v(115.5, 39.3) * mm, "end": v(125.8, 39.3) * mm});
            skLineSegment(sketch, "E3.8.2.3", {"start": v(125.8, 39.3) * mm, "end": v(125.8, 49.6) * mm});
            skLineSegment(sketch, "E3.8.3.0", {"start": v(115.5, 52) * mm, "end": v(115.5, 62.3) * mm});
            skLineSegment(sketch, "E3.8.3.1", {"start": v(115.5, 62.3) * mm, "end": v(125.8, 62.3) * mm});
            skLineSegment(sketch, "E3.8.3.2", {"start": v(115.5, 52) * mm, "end": v(125.8, 52) * mm});
            skLineSegment(sketch, "E3.8.3.3", {"start": v(125.8, 52) * mm, "end": v(125.8, 62.3) * mm});
            skLineSegment(sketch, "E3.8.4.0", {"start": v(115.5, 64.7) * mm, "end": v(115.5, 75) * mm});
            skLineSegment(sketch, "E3.8.4.1", {"start": v(115.5, 75) * mm, "end": v(125.8, 75) * mm});
            skLineSegment(sketch, "E3.8.4.2", {"start": v(115.5, 64.7) * mm, "end": v(125.8, 64.7) * mm});
            skLineSegment(sketch, "E3.8.4.3", {"start": v(125.8, 64.7) * mm, "end": v(125.8, 75) * mm});
            skLineSegment(sketch, "E3.8.5.0", {"start": v(115.5, 77.4) * mm, "end": v(115.5, 87.7) * mm});
            skLineSegment(sketch, "E3.8.5.1", {"start": v(115.5, 87.7) * mm, "end": v(125.8, 87.7) * mm});
            skLineSegment(sketch, "E3.8.5.2", {"start": v(115.5, 77.4) * mm, "end": v(125.8, 77.4) * mm});
            skLineSegment(sketch, "E3.8.5.3", {"start": v(125.8, 77.4) * mm, "end": v(125.8, 87.7) * mm});
            skLineSegment(sketch, "E3.8.6.0", {"start": v(115.5, 90.1) * mm, "end": v(115.5, 100.4) * mm});
            skLineSegment(sketch, "E3.8.6.1", {"start": v(115.5, 100.4) * mm, "end": v(125.8, 100.4) * mm});
            skLineSegment(sketch, "E3.8.6.2", {"start": v(115.5, 90.1) * mm, "end": v(125.8, 90.1) * mm});
            skLineSegment(sketch, "E3.8.6.3", {"start": v(125.8, 90.1) * mm, "end": v(125.8, 100.4) * mm});
            skLineSegment(sketch, "E3.8.7.0", {"start": v(115.5, 102.8) * mm, "end": v(115.5, 113.1) * mm});
            skLineSegment(sketch, "E3.8.7.1", {"start": v(115.5, 113.1) * mm, "end": v(125.8, 113.1) * mm});
            skLineSegment(sketch, "E3.8.7.2", {"start": v(115.5, 102.8) * mm, "end": v(125.8, 102.8) * mm});
            skLineSegment(sketch, "E3.8.7.3", {"start": v(125.8, 102.8) * mm, "end": v(125.8, 113.1) * mm});
            skLineSegment(sketch, "E3.8.8.0", {"start": v(115.5, 115.5) * mm, "end": v(115.5, 125.8) * mm});
            skLineSegment(sketch, "E3.8.8.1", {"start": v(115.5, 125.8) * mm, "end": v(125.8, 125.8) * mm});
            skLineSegment(sketch, "E3.8.8.2", {"start": v(115.5, 115.5) * mm, "end": v(125.8, 115.5) * mm});
            skLineSegment(sketch, "E3.8.8.3", {"start": v(125.8, 115.5) * mm, "end": v(125.8, 125.8) * mm});
            skLineSegment(sketch, "E3.8.9.0", {"start": v(115.5, 128.2) * mm, "end": v(115.5, 138.5) * mm});
            skLineSegment(sketch, "E3.8.9.1", {"start": v(115.5, 138.5) * mm, "end": v(125.8, 138.5) * mm});
            skLineSegment(sketch, "E3.8.9.2", {"start": v(115.5, 128.2) * mm, "end": v(125.8, 128.2) * mm});
            skLineSegment(sketch, "E3.8.9.3", {"start": v(125.8, 128.2) * mm, "end": v(125.8, 138.5) * mm});
            skLineSegment(sketch, "E3.8.10.0", {"start": v(115.5, 140.9) * mm, "end": v(115.5, 151.2) * mm});
            skLineSegment(sketch, "E3.8.10.1", {"start": v(115.5, 151.2) * mm, "end": v(125.8, 151.2) * mm});
            skLineSegment(sketch, "E3.8.10.2", {"start": v(115.5, 140.9) * mm, "end": v(125.8, 140.9) * mm});
            skLineSegment(sketch, "E3.8.10.3", {"start": v(125.8, 140.9) * mm, "end": v(125.8, 151.2) * mm});
            skLineSegment(sketch, "E3.8.11.0", {"start": v(115.5, 153.6) * mm, "end": v(115.5, 163.9) * mm});
            skLineSegment(sketch, "E3.8.11.1", {"start": v(115.5, 163.9) * mm, "end": v(125.8, 163.9) * mm});
            skLineSegment(sketch, "E3.8.11.2", {"start": v(115.5, 153.6) * mm, "end": v(125.8, 153.6) * mm});
            skLineSegment(sketch, "E3.8.11.3", {"start": v(125.8, 153.6) * mm, "end": v(125.8, 163.9) * mm});
            skLineSegment(sketch, "E3.8.12.0", {"start": v(115.5, 166.3) * mm, "end": v(115.5, 176.6) * mm});
            skLineSegment(sketch, "E3.8.12.1", {"start": v(115.5, 176.6) * mm, "end": v(125.8, 176.6) * mm});
            skLineSegment(sketch, "E3.8.12.2", {"start": v(115.5, 166.3) * mm, "end": v(125.8, 166.3) * mm});
            skLineSegment(sketch, "E3.8.12.3", {"start": v(125.8, 166.3) * mm, "end": v(125.8, 176.6) * mm});
            skLineSegment(sketch, "E3.8.13.0", {"start": v(115.5, 179) * mm, "end": v(115.5, 189.3) * mm});
            skLineSegment(sketch, "E3.8.13.1", {"start": v(115.5, 189.3) * mm, "end": v(125.8, 189.3) * mm});
            skLineSegment(sketch, "E3.8.13.2", {"start": v(115.5, 179) * mm, "end": v(125.8, 179) * mm});
            skLineSegment(sketch, "E3.8.13.3", {"start": v(125.8, 179) * mm, "end": v(125.8, 189.3) * mm});
            skLineSegment(sketch, "E3.8.14.0", {"start": v(115.5, 191.7) * mm, "end": v(115.5, 202) * mm});
            skLineSegment(sketch, "E3.8.14.1", {"start": v(115.5, 202) * mm, "end": v(125.8, 202) * mm});
            skLineSegment(sketch, "E3.8.14.2", {"start": v(115.5, 191.7) * mm, "end": v(125.8, 191.7) * mm});
            skLineSegment(sketch, "E3.8.14.3", {"start": v(125.8, 191.7) * mm, "end": v(125.8, 202) * mm});
            skLineSegment(sketch, "E3.8.15.0", {"start": v(115.5, 204.4) * mm, "end": v(115.5, 214.7) * mm});
            skLineSegment(sketch, "E3.8.15.1", {"start": v(115.5, 214.7) * mm, "end": v(125.8, 214.7) * mm});
            skLineSegment(sketch, "E3.8.15.2", {"start": v(115.5, 204.4) * mm, "end": v(125.8, 204.4) * mm});
            skLineSegment(sketch, "E3.8.15.3", {"start": v(125.8, 204.4) * mm, "end": v(125.8, 214.7) * mm});
            skLineSegment(sketch, "E3.8.16.0", {"start": v(115.5, 217.1) * mm, "end": v(115.5, 227.4) * mm});
            skLineSegment(sketch, "E3.8.16.1", {"start": v(115.5, 227.4) * mm, "end": v(125.8, 227.4) * mm});
            skLineSegment(sketch, "E3.8.16.2", {"start": v(115.5, 217.1) * mm, "end": v(125.8, 217.1) * mm});
            skLineSegment(sketch, "E3.8.16.3", {"start": v(125.8, 217.1) * mm, "end": v(125.8, 227.4) * mm});
            skLineSegment(sketch, "E3.8.17.0", {"start": v(115.5, 229.8) * mm, "end": v(115.5, 240.1) * mm});
            skLineSegment(sketch, "E3.8.17.1", {"start": v(115.5, 240.1) * mm, "end": v(125.8, 240.1) * mm});
            skLineSegment(sketch, "E3.8.17.2", {"start": v(115.5, 229.8) * mm, "end": v(125.8, 229.8) * mm});
            skLineSegment(sketch, "E3.8.17.3", {"start": v(125.8, 229.8) * mm, "end": v(125.8, 240.1) * mm});
            skLineSegment(sketch, "E3.8.18.0", {"start": v(115.5, 242.5) * mm, "end": v(115.5, 252.8) * mm});
            skLineSegment(sketch, "E3.8.18.1", {"start": v(115.5, 252.8) * mm, "end": v(125.8, 252.8) * mm});
            skLineSegment(sketch, "E3.8.18.2", {"start": v(115.5, 242.5) * mm, "end": v(125.8, 242.5) * mm});
            skLineSegment(sketch, "E3.8.18.3", {"start": v(125.8, 242.5) * mm, "end": v(125.8, 252.8) * mm});
            skLineSegment(sketch, "E3.8.19.0", {"start": v(115.5, 255.2) * mm, "end": v(115.5, 265.5) * mm});
            skLineSegment(sketch, "E3.8.19.1", {"start": v(115.5, 265.5) * mm, "end": v(125.8, 265.5) * mm});
            skLineSegment(sketch, "E3.8.19.2", {"start": v(115.5, 255.2) * mm, "end": v(125.8, 255.2) * mm});
            skLineSegment(sketch, "E3.8.19.3", {"start": v(125.8, 255.2) * mm, "end": v(125.8, 265.5) * mm});
            skLineSegment(sketch, "E3.8.20.0", {"start": v(115.5, 267.9) * mm, "end": v(115.5, 278.2) * mm});
            skLineSegment(sketch, "E3.8.20.1", {"start": v(115.5, 278.2) * mm, "end": v(125.8, 278.2) * mm});
            skLineSegment(sketch, "E3.8.20.2", {"start": v(115.5, 267.9) * mm, "end": v(125.8, 267.9) * mm});
            skLineSegment(sketch, "E3.8.20.3", {"start": v(125.8, 267.9) * mm, "end": v(125.8, 278.2) * mm});
            skLineSegment(sketch, "E3.8.21.0", {"start": v(115.5, 280.6) * mm, "end": v(115.5, 290.9) * mm});
            skLineSegment(sketch, "E3.8.21.1", {"start": v(115.5, 290.9) * mm, "end": v(125.8, 290.9) * mm});
            skLineSegment(sketch, "E3.8.21.2", {"start": v(115.5, 280.6) * mm, "end": v(125.8, 280.6) * mm});
            skLineSegment(sketch, "E3.8.21.3", {"start": v(125.8, 280.6) * mm, "end": v(125.8, 290.9) * mm});
            skLineSegment(sketch, "E3.9.0.0", {"start": v(128.2, 13.9) * mm, "end": v(128.2, 24.2) * mm});
            skLineSegment(sketch, "E3.9.0.1", {"start": v(128.2, 24.2) * mm, "end": v(138.5, 24.2) * mm});
            skLineSegment(sketch, "E3.9.0.2", {"start": v(128.2, 13.9) * mm, "end": v(138.5, 13.9) * mm});
            skLineSegment(sketch, "E3.9.0.3", {"start": v(138.5, 13.9) * mm, "end": v(138.5, 24.2) * mm});
            skLineSegment(sketch, "E3.9.1.0", {"start": v(128.2, 26.6) * mm, "end": v(128.2, 36.9) * mm});
            skLineSegment(sketch, "E3.9.1.1", {"start": v(128.2, 36.9) * mm, "end": v(138.5, 36.9) * mm});
            skLineSegment(sketch, "E3.9.1.2", {"start": v(128.2, 26.6) * mm, "end": v(138.5, 26.6) * mm});
            skLineSegment(sketch, "E3.9.1.3", {"start": v(138.5, 26.6) * mm, "end": v(138.5, 36.9) * mm});
            skLineSegment(sketch, "E3.9.2.0", {"start": v(128.2, 39.3) * mm, "end": v(128.2, 49.6) * mm});
            skLineSegment(sketch, "E3.9.2.1", {"start": v(128.2, 49.6) * mm, "end": v(138.5, 49.6) * mm});
            skLineSegment(sketch, "E3.9.2.2", {"start": v(128.2, 39.3) * mm, "end": v(138.5, 39.3) * mm});
            skLineSegment(sketch, "E3.9.2.3", {"start": v(138.5, 39.3) * mm, "end": v(138.5, 49.6) * mm});
            skLineSegment(sketch, "E3.9.3.0", {"start": v(128.2, 52) * mm, "end": v(128.2, 62.3) * mm});
            skLineSegment(sketch, "E3.9.3.1", {"start": v(128.2, 62.3) * mm, "end": v(138.5, 62.3) * mm});
            skLineSegment(sketch, "E3.9.3.2", {"start": v(128.2, 52) * mm, "end": v(138.5, 52) * mm});
            skLineSegment(sketch, "E3.9.3.3", {"start": v(138.5, 52) * mm, "end": v(138.5, 62.3) * mm});
            skLineSegment(sketch, "E3.9.4.0", {"start": v(128.2, 64.7) * mm, "end": v(128.2, 75) * mm});
            skLineSegment(sketch, "E3.9.4.1", {"start": v(128.2, 75) * mm, "end": v(138.5, 75) * mm});
            skLineSegment(sketch, "E3.9.4.2", {"start": v(128.2, 64.7) * mm, "end": v(138.5, 64.7) * mm});
            skLineSegment(sketch, "E3.9.4.3", {"start": v(138.5, 64.7) * mm, "end": v(138.5, 75) * mm});
            skLineSegment(sketch, "E3.9.5.0", {"start": v(128.2, 77.4) * mm, "end": v(128.2, 87.7) * mm});
            skLineSegment(sketch, "E3.9.5.1", {"start": v(128.2, 87.7) * mm, "end": v(138.5, 87.7) * mm});
            skLineSegment(sketch, "E3.9.5.2", {"start": v(128.2, 77.4) * mm, "end": v(138.5, 77.4) * mm});
            skLineSegment(sketch, "E3.9.5.3", {"start": v(138.5, 77.4) * mm, "end": v(138.5, 87.7) * mm});
            skLineSegment(sketch, "E3.9.6.0", {"start": v(128.2, 90.1) * mm, "end": v(128.2, 100.4) * mm});
            skLineSegment(sketch, "E3.9.6.1", {"start": v(128.2, 100.4) * mm, "end": v(138.5, 100.4) * mm});
            skLineSegment(sketch, "E3.9.6.2", {"start": v(128.2, 90.1) * mm, "end": v(138.5, 90.1) * mm});
            skLineSegment(sketch, "E3.9.6.3", {"start": v(138.5, 90.1) * mm, "end": v(138.5, 100.4) * mm});
            skLineSegment(sketch, "E3.9.7.0", {"start": v(128.2, 102.8) * mm, "end": v(128.2, 113.1) * mm});
            skLineSegment(sketch, "E3.9.7.1", {"start": v(128.2, 113.1) * mm, "end": v(138.5, 113.1) * mm});
            skLineSegment(sketch, "E3.9.7.2", {"start": v(128.2, 102.8) * mm, "end": v(138.5, 102.8) * mm});
            skLineSegment(sketch, "E3.9.7.3", {"start": v(138.5, 102.8) * mm, "end": v(138.5, 113.1) * mm});
            skLineSegment(sketch, "E3.9.8.0", {"start": v(128.2, 115.5) * mm, "end": v(128.2, 125.8) * mm});
            skLineSegment(sketch, "E3.9.8.1", {"start": v(128.2, 125.8) * mm, "end": v(138.5, 125.8) * mm});
            skLineSegment(sketch, "E3.9.8.2", {"start": v(128.2, 115.5) * mm, "end": v(138.5, 115.5) * mm});
            skLineSegment(sketch, "E3.9.8.3", {"start": v(138.5, 115.5) * mm, "end": v(138.5, 125.8) * mm});
            skLineSegment(sketch, "E3.9.9.0", {"start": v(128.2, 128.2) * mm, "end": v(128.2, 138.5) * mm});
            skLineSegment(sketch, "E3.9.9.1", {"start": v(128.2, 138.5) * mm, "end": v(138.5, 138.5) * mm});
            skLineSegment(sketch, "E3.9.9.2", {"start": v(128.2, 128.2) * mm, "end": v(138.5, 128.2) * mm});
            skLineSegment(sketch, "E3.9.9.3", {"start": v(138.5, 128.2) * mm, "end": v(138.5, 138.5) * mm});
            skLineSegment(sketch, "E3.9.10.0", {"start": v(128.2, 140.9) * mm, "end": v(128.2, 151.2) * mm});
            skLineSegment(sketch, "E3.9.10.1", {"start": v(128.2, 151.2) * mm, "end": v(138.5, 151.2) * mm});
            skLineSegment(sketch, "E3.9.10.2", {"start": v(128.2, 140.9) * mm, "end": v(138.5, 140.9) * mm});
            skLineSegment(sketch, "E3.9.10.3", {"start": v(138.5, 140.9) * mm, "end": v(138.5, 151.2) * mm});
            skLineSegment(sketch, "E3.9.11.0", {"start": v(128.2, 153.6) * mm, "end": v(128.2, 163.9) * mm});
            skLineSegment(sketch, "E3.9.11.1", {"start": v(128.2, 163.9) * mm, "end": v(138.5, 163.9) * mm});
            skLineSegment(sketch, "E3.9.11.2", {"start": v(128.2, 153.6) * mm, "end": v(138.5, 153.6) * mm});
            skLineSegment(sketch, "E3.9.11.3", {"start": v(138.5, 153.6) * mm, "end": v(138.5, 163.9) * mm});
            skLineSegment(sketch, "E3.9.12.0", {"start": v(128.2, 166.3) * mm, "end": v(128.2, 176.6) * mm});
            skLineSegment(sketch, "E3.9.12.1", {"start": v(128.2, 176.6) * mm, "end": v(138.5, 176.6) * mm});
            skLineSegment(sketch, "E3.9.12.2", {"start": v(128.2, 166.3) * mm, "end": v(138.5, 166.3) * mm});
            skLineSegment(sketch, "E3.9.12.3", {"start": v(138.5, 166.3) * mm, "end": v(138.5, 176.6) * mm});
            skLineSegment(sketch, "E3.9.13.0", {"start": v(128.2, 179) * mm, "end": v(128.2, 189.3) * mm});
            skLineSegment(sketch, "E3.9.13.1", {"start": v(128.2, 189.3) * mm, "end": v(138.5, 189.3) * mm});
            skLineSegment(sketch, "E3.9.13.2", {"start": v(128.2, 179) * mm, "end": v(138.5, 179) * mm});
            skLineSegment(sketch, "E3.9.13.3", {"start": v(138.5, 179) * mm, "end": v(138.5, 189.3) * mm});
            skLineSegment(sketch, "E3.9.14.0", {"start": v(128.2, 191.7) * mm, "end": v(128.2, 202) * mm});
            skLineSegment(sketch, "E3.9.14.1", {"start": v(128.2, 202) * mm, "end": v(138.5, 202) * mm});
            skLineSegment(sketch, "E3.9.14.2", {"start": v(128.2, 191.7) * mm, "end": v(138.5, 191.7) * mm});
            skLineSegment(sketch, "E3.9.14.3", {"start": v(138.5, 191.7) * mm, "end": v(138.5, 202) * mm});
            skLineSegment(sketch, "E3.9.15.0", {"start": v(128.2, 204.4) * mm, "end": v(128.2, 214.7) * mm});
            skLineSegment(sketch, "E3.9.15.1", {"start": v(128.2, 214.7) * mm, "end": v(138.5, 214.7) * mm});
            skLineSegment(sketch, "E3.9.15.2", {"start": v(128.2, 204.4) * mm, "end": v(138.5, 204.4) * mm});
            skLineSegment(sketch, "E3.9.15.3", {"start": v(138.5, 204.4) * mm, "end": v(138.5, 214.7) * mm});
            skLineSegment(sketch, "E3.9.16.0", {"start": v(128.2, 217.1) * mm, "end": v(128.2, 227.4) * mm});
            skLineSegment(sketch, "E3.9.16.1", {"start": v(128.2, 227.4) * mm, "end": v(138.5, 227.4) * mm});
            skLineSegment(sketch, "E3.9.16.2", {"start": v(128.2, 217.1) * mm, "end": v(138.5, 217.1) * mm});
            skLineSegment(sketch, "E3.9.16.3", {"start": v(138.5, 217.1) * mm, "end": v(138.5, 227.4) * mm});
            skLineSegment(sketch, "E3.9.17.0", {"start": v(128.2, 229.8) * mm, "end": v(128.2, 240.1) * mm});
            skLineSegment(sketch, "E3.9.17.1", {"start": v(128.2, 240.1) * mm, "end": v(138.5, 240.1) * mm});
            skLineSegment(sketch, "E3.9.17.2", {"start": v(128.2, 229.8) * mm, "end": v(138.5, 229.8) * mm});
            skLineSegment(sketch, "E3.9.17.3", {"start": v(138.5, 229.8) * mm, "end": v(138.5, 240.1) * mm});
            skLineSegment(sketch, "E3.9.18.0", {"start": v(128.2, 242.5) * mm, "end": v(128.2, 252.8) * mm});
            skLineSegment(sketch, "E3.9.18.1", {"start": v(128.2, 252.8) * mm, "end": v(138.5, 252.8) * mm});
            skLineSegment(sketch, "E3.9.18.2", {"start": v(128.2, 242.5) * mm, "end": v(138.5, 242.5) * mm});
            skLineSegment(sketch, "E3.9.18.3", {"start": v(138.5, 242.5) * mm, "end": v(138.5, 252.8) * mm});
            skLineSegment(sketch, "E3.9.19.0", {"start": v(128.2, 255.2) * mm, "end": v(128.2, 265.5) * mm});
            skLineSegment(sketch, "E3.9.19.1", {"start": v(128.2, 265.5) * mm, "end": v(138.5, 265.5) * mm});
            skLineSegment(sketch, "E3.9.19.2", {"start": v(128.2, 255.2) * mm, "end": v(138.5, 255.2) * mm});
            skLineSegment(sketch, "E3.9.19.3", {"start": v(138.5, 255.2) * mm, "end": v(138.5, 265.5) * mm});
            skLineSegment(sketch, "E3.9.20.0", {"start": v(128.2, 267.9) * mm, "end": v(128.2, 278.2) * mm});
            skLineSegment(sketch, "E3.9.20.1", {"start": v(128.2, 278.2) * mm, "end": v(138.5, 278.2) * mm});
            skLineSegment(sketch, "E3.9.20.2", {"start": v(128.2, 267.9) * mm, "end": v(138.5, 267.9) * mm});
            skLineSegment(sketch, "E3.9.20.3", {"start": v(138.5, 267.9) * mm, "end": v(138.5, 278.2) * mm});
            skLineSegment(sketch, "E3.9.21.0", {"start": v(128.2, 280.6) * mm, "end": v(128.2, 290.9) * mm});
            skLineSegment(sketch, "E3.9.21.1", {"start": v(128.2, 290.9) * mm, "end": v(138.5, 290.9) * mm});
            skLineSegment(sketch, "E3.9.21.2", {"start": v(128.2, 280.6) * mm, "end": v(138.5, 280.6) * mm});
            skLineSegment(sketch, "E3.9.21.3", {"start": v(138.5, 280.6) * mm, "end": v(138.5, 290.9) * mm});
            skLineSegment(sketch, "E3.10.0.0", {"start": v(140.9, 13.9) * mm, "end": v(140.9, 24.2) * mm});
            skLineSegment(sketch, "E3.10.0.1", {"start": v(140.9, 24.2) * mm, "end": v(151.2, 24.2) * mm});
            skLineSegment(sketch, "E3.10.0.2", {"start": v(140.9, 13.9) * mm, "end": v(151.2, 13.9) * mm});
            skLineSegment(sketch, "E3.10.0.3", {"start": v(151.2, 13.9) * mm, "end": v(151.2, 24.2) * mm});
            skLineSegment(sketch, "E3.10.1.0", {"start": v(140.9, 26.6) * mm, "end": v(140.9, 36.9) * mm});
            skLineSegment(sketch, "E3.10.1.1", {"start": v(140.9, 36.9) * mm, "end": v(151.2, 36.9) * mm});
            skLineSegment(sketch, "E3.10.1.2", {"start": v(140.9, 26.6) * mm, "end": v(151.2, 26.6) * mm});
            skLineSegment(sketch, "E3.10.1.3", {"start": v(151.2, 26.6) * mm, "end": v(151.2, 36.9) * mm});
            skLineSegment(sketch, "E3.10.2.0", {"start": v(140.9, 39.3) * mm, "end": v(140.9, 49.6) * mm});
            skLineSegment(sketch, "E3.10.2.1", {"start": v(140.9, 49.6) * mm, "end": v(151.2, 49.6) * mm});
            skLineSegment(sketch, "E3.10.2.2", {"start": v(140.9, 39.3) * mm, "end": v(151.2, 39.3) * mm});
            skLineSegment(sketch, "E3.10.2.3", {"start": v(151.2, 39.3) * mm, "end": v(151.2, 49.6) * mm});
            skLineSegment(sketch, "E3.10.3.0", {"start": v(140.9, 52) * mm, "end": v(140.9, 62.3) * mm});
            skLineSegment(sketch, "E3.10.3.1", {"start": v(140.9, 62.3) * mm, "end": v(151.2, 62.3) * mm});
            skLineSegment(sketch, "E3.10.3.2", {"start": v(140.9, 52) * mm, "end": v(151.2, 52) * mm});
            skLineSegment(sketch, "E3.10.3.3", {"start": v(151.2, 52) * mm, "end": v(151.2, 62.3) * mm});
            skLineSegment(sketch, "E3.10.4.0", {"start": v(140.9, 64.7) * mm, "end": v(140.9, 75) * mm});
            skLineSegment(sketch, "E3.10.4.1", {"start": v(140.9, 75) * mm, "end": v(151.2, 75) * mm});
            skLineSegment(sketch, "E3.10.4.2", {"start": v(140.9, 64.7) * mm, "end": v(151.2, 64.7) * mm});
            skLineSegment(sketch, "E3.10.4.3", {"start": v(151.2, 64.7) * mm, "end": v(151.2, 75) * mm});
            skLineSegment(sketch, "E3.10.5.0", {"start": v(140.9, 77.4) * mm, "end": v(140.9, 87.7) * mm});
            skLineSegment(sketch, "E3.10.5.1", {"start": v(140.9, 87.7) * mm, "end": v(151.2, 87.7) * mm});
            skLineSegment(sketch, "E3.10.5.2", {"start": v(140.9, 77.4) * mm, "end": v(151.2, 77.4) * mm});
            skLineSegment(sketch, "E3.10.5.3", {"start": v(151.2, 77.4) * mm, "end": v(151.2, 87.7) * mm});
            skLineSegment(sketch, "E3.10.6.0", {"start": v(140.9, 90.1) * mm, "end": v(140.9, 100.4) * mm});
            skLineSegment(sketch, "E3.10.6.1", {"start": v(140.9, 100.4) * mm, "end": v(151.2, 100.4) * mm});
            skLineSegment(sketch, "E3.10.6.2", {"start": v(140.9, 90.1) * mm, "end": v(151.2, 90.1) * mm});
            skLineSegment(sketch, "E3.10.6.3", {"start": v(151.2, 90.1) * mm, "end": v(151.2, 100.4) * mm});
            skLineSegment(sketch, "E3.10.7.0", {"start": v(140.9, 102.8) * mm, "end": v(140.9, 113.1) * mm});
            skLineSegment(sketch, "E3.10.7.1", {"start": v(140.9, 113.1) * mm, "end": v(151.2, 113.1) * mm});
            skLineSegment(sketch, "E3.10.7.2", {"start": v(140.9, 102.8) * mm, "end": v(151.2, 102.8) * mm});
            skLineSegment(sketch, "E3.10.7.3", {"start": v(151.2, 102.8) * mm, "end": v(151.2, 113.1) * mm});
            skLineSegment(sketch, "E3.10.8.0", {"start": v(140.9, 115.5) * mm, "end": v(140.9, 125.8) * mm});
            skLineSegment(sketch, "E3.10.8.1", {"start": v(140.9, 125.8) * mm, "end": v(151.2, 125.8) * mm});
            skLineSegment(sketch, "E3.10.8.2", {"start": v(140.9, 115.5) * mm, "end": v(151.2, 115.5) * mm});
            skLineSegment(sketch, "E3.10.8.3", {"start": v(151.2, 115.5) * mm, "end": v(151.2, 125.8) * mm});
            skLineSegment(sketch, "E3.10.9.0", {"start": v(140.9, 128.2) * mm, "end": v(140.9, 138.5) * mm});
            skLineSegment(sketch, "E3.10.9.1", {"start": v(140.9, 138.5) * mm, "end": v(151.2, 138.5) * mm});
            skLineSegment(sketch, "E3.10.9.2", {"start": v(140.9, 128.2) * mm, "end": v(151.2, 128.2) * mm});
            skLineSegment(sketch, "E3.10.9.3", {"start": v(151.2, 128.2) * mm, "end": v(151.2, 138.5) * mm});
            skLineSegment(sketch, "E3.10.10.0", {"start": v(140.9, 140.9) * mm, "end": v(140.9, 151.2) * mm});
            skLineSegment(sketch, "E3.10.10.1", {"start": v(140.9, 151.2) * mm, "end": v(151.2, 151.2) * mm});
            skLineSegment(sketch, "E3.10.10.2", {"start": v(140.9, 140.9) * mm, "end": v(151.2, 140.9) * mm});
            skLineSegment(sketch, "E3.10.10.3", {"start": v(151.2, 140.9) * mm, "end": v(151.2, 151.2) * mm});
            skLineSegment(sketch, "E3.10.11.0", {"start": v(140.9, 153.6) * mm, "end": v(140.9, 163.9) * mm});
            skLineSegment(sketch, "E3.10.11.1", {"start": v(140.9, 163.9) * mm, "end": v(151.2, 163.9) * mm});
            skLineSegment(sketch, "E3.10.11.2", {"start": v(140.9, 153.6) * mm, "end": v(151.2, 153.6) * mm});
            skLineSegment(sketch, "E3.10.11.3", {"start": v(151.2, 153.6) * mm, "end": v(151.2, 163.9) * mm});
            skLineSegment(sketch, "E3.10.12.0", {"start": v(140.9, 166.3) * mm, "end": v(140.9, 176.6) * mm});
            skLineSegment(sketch, "E3.10.12.1", {"start": v(140.9, 176.6) * mm, "end": v(151.2, 176.6) * mm});
            skLineSegment(sketch, "E3.10.12.2", {"start": v(140.9, 166.3) * mm, "end": v(151.2, 166.3) * mm});
            skLineSegment(sketch, "E3.10.12.3", {"start": v(151.2, 166.3) * mm, "end": v(151.2, 176.6) * mm});
            skLineSegment(sketch, "E3.10.13.0", {"start": v(140.9, 179) * mm, "end": v(140.9, 189.3) * mm});
            skLineSegment(sketch, "E3.10.13.1", {"start": v(140.9, 189.3) * mm, "end": v(151.2, 189.3) * mm});
            skLineSegment(sketch, "E3.10.13.2", {"start": v(140.9, 179) * mm, "end": v(151.2, 179) * mm});
            skLineSegment(sketch, "E3.10.13.3", {"start": v(151.2, 179) * mm, "end": v(151.2, 189.3) * mm});
            skLineSegment(sketch, "E3.10.14.0", {"start": v(140.9, 191.7) * mm, "end": v(140.9, 202) * mm});
            skLineSegment(sketch, "E3.10.14.1", {"start": v(140.9, 202) * mm, "end": v(151.2, 202) * mm});
            skLineSegment(sketch, "E3.10.14.2", {"start": v(140.9, 191.7) * mm, "end": v(151.2, 191.7) * mm});
            skLineSegment(sketch, "E3.10.14.3", {"start": v(151.2, 191.7) * mm, "end": v(151.2, 202) * mm});
            skLineSegment(sketch, "E3.10.15.0", {"start": v(140.9, 204.4) * mm, "end": v(140.9, 214.7) * mm});
            skLineSegment(sketch, "E3.10.15.1", {"start": v(140.9, 214.7) * mm, "end": v(151.2, 214.7) * mm});
            skLineSegment(sketch, "E3.10.15.2", {"start": v(140.9, 204.4) * mm, "end": v(151.2, 204.4) * mm});
            skLineSegment(sketch, "E3.10.15.3", {"start": v(151.2, 204.4) * mm, "end": v(151.2, 214.7) * mm});
            skLineSegment(sketch, "E3.10.16.0", {"start": v(140.9, 217.1) * mm, "end": v(140.9, 227.4) * mm});
            skLineSegment(sketch, "E3.10.16.1", {"start": v(140.9, 227.4) * mm, "end": v(151.2, 227.4) * mm});
            skLineSegment(sketch, "E3.10.16.2", {"start": v(140.9, 217.1) * mm, "end": v(151.2, 217.1) * mm});
            skLineSegment(sketch, "E3.10.16.3", {"start": v(151.2, 217.1) * mm, "end": v(151.2, 227.4) * mm});
            skLineSegment(sketch, "E3.10.17.0", {"start": v(140.9, 229.8) * mm, "end": v(140.9, 240.1) * mm});
            skLineSegment(sketch, "E3.10.17.1", {"start": v(140.9, 240.1) * mm, "end": v(151.2, 240.1) * mm});
            skLineSegment(sketch, "E3.10.17.2", {"start": v(140.9, 229.8) * mm, "end": v(151.2, 229.8) * mm});
            skLineSegment(sketch, "E3.10.17.3", {"start": v(151.2, 229.8) * mm, "end": v(151.2, 240.1) * mm});
            skLineSegment(sketch, "E3.10.18.0", {"start": v(140.9, 242.5) * mm, "end": v(140.9, 252.8) * mm});
            skLineSegment(sketch, "E3.10.18.1", {"start": v(140.9, 252.8) * mm, "end": v(151.2, 252.8) * mm});
            skLineSegment(sketch, "E3.10.18.2", {"start": v(140.9, 242.5) * mm, "end": v(151.2, 242.5) * mm});
            skLineSegment(sketch, "E3.10.18.3", {"start": v(151.2, 242.5) * mm, "end": v(151.2, 252.8) * mm});
            skLineSegment(sketch, "E3.10.19.0", {"start": v(140.9, 255.2) * mm, "end": v(140.9, 265.5) * mm});
            skLineSegment(sketch, "E3.10.19.1", {"start": v(140.9, 265.5) * mm, "end": v(151.2, 265.5) * mm});
            skLineSegment(sketch, "E3.10.19.2", {"start": v(140.9, 255.2) * mm, "end": v(151.2, 255.2) * mm});
            skLineSegment(sketch, "E3.10.19.3", {"start": v(151.2, 255.2) * mm, "end": v(151.2, 265.5) * mm});
            skLineSegment(sketch, "E3.10.20.0", {"start": v(140.9, 267.9) * mm, "end": v(140.9, 278.2) * mm});
            skLineSegment(sketch, "E3.10.20.1", {"start": v(140.9, 278.2) * mm, "end": v(151.2, 278.2) * mm});
            skLineSegment(sketch, "E3.10.20.2", {"start": v(140.9, 267.9) * mm, "end": v(151.2, 267.9) * mm});
            skLineSegment(sketch, "E3.10.20.3", {"start": v(151.2, 267.9) * mm, "end": v(151.2, 278.2) * mm});
            skLineSegment(sketch, "E3.10.21.0", {"start": v(140.9, 280.6) * mm, "end": v(140.9, 290.9) * mm});
            skLineSegment(sketch, "E3.10.21.1", {"start": v(140.9, 290.9) * mm, "end": v(151.2, 290.9) * mm});
            skLineSegment(sketch, "E3.10.21.2", {"start": v(140.9, 280.6) * mm, "end": v(151.2, 280.6) * mm});
            skLineSegment(sketch, "E3.10.21.3", {"start": v(151.2, 280.6) * mm, "end": v(151.2, 290.9) * mm});
            skLineSegment(sketch, "E3.11.0.0", {"start": v(153.6, 13.9) * mm, "end": v(153.6, 24.2) * mm});
            skLineSegment(sketch, "E3.11.0.1", {"start": v(153.6, 24.2) * mm, "end": v(163.9, 24.2) * mm});
            skLineSegment(sketch, "E3.11.0.2", {"start": v(153.6, 13.9) * mm, "end": v(163.9, 13.9) * mm});
            skLineSegment(sketch, "E3.11.0.3", {"start": v(163.9, 13.9) * mm, "end": v(163.9, 24.2) * mm});
            skLineSegment(sketch, "E3.11.1.0", {"start": v(153.6, 26.6) * mm, "end": v(153.6, 36.9) * mm});
            skLineSegment(sketch, "E3.11.1.1", {"start": v(153.6, 36.9) * mm, "end": v(163.9, 36.9) * mm});
            skLineSegment(sketch, "E3.11.1.2", {"start": v(153.6, 26.6) * mm, "end": v(163.9, 26.6) * mm});
            skLineSegment(sketch, "E3.11.1.3", {"start": v(163.9, 26.6) * mm, "end": v(163.9, 36.9) * mm});
            skLineSegment(sketch, "E3.11.2.0", {"start": v(153.6, 39.3) * mm, "end": v(153.6, 49.6) * mm});
            skLineSegment(sketch, "E3.11.2.1", {"start": v(153.6, 49.6) * mm, "end": v(163.9, 49.6) * mm});
            skLineSegment(sketch, "E3.11.2.2", {"start": v(153.6, 39.3) * mm, "end": v(163.9, 39.3) * mm});
            skLineSegment(sketch, "E3.11.2.3", {"start": v(163.9, 39.3) * mm, "end": v(163.9, 49.6) * mm});
            skLineSegment(sketch, "E3.11.3.0", {"start": v(153.6, 52) * mm, "end": v(153.6, 62.3) * mm});
            skLineSegment(sketch, "E3.11.3.1", {"start": v(153.6, 62.3) * mm, "end": v(163.9, 62.3) * mm});
            skLineSegment(sketch, "E3.11.3.2", {"start": v(153.6, 52) * mm, "end": v(163.9, 52) * mm});
            skLineSegment(sketch, "E3.11.3.3", {"start": v(163.9, 52) * mm, "end": v(163.9, 62.3) * mm});
            skLineSegment(sketch, "E3.11.4.0", {"start": v(153.6, 64.7) * mm, "end": v(153.6, 75) * mm});
            skLineSegment(sketch, "E3.11.4.1", {"start": v(153.6, 75) * mm, "end": v(163.9, 75) * mm});
            skLineSegment(sketch, "E3.11.4.2", {"start": v(153.6, 64.7) * mm, "end": v(163.9, 64.7) * mm});
            skLineSegment(sketch, "E3.11.4.3", {"start": v(163.9, 64.7) * mm, "end": v(163.9, 75) * mm});
            skLineSegment(sketch, "E3.11.5.0", {"start": v(153.6, 77.4) * mm, "end": v(153.6, 87.7) * mm});
            skLineSegment(sketch, "E3.11.5.1", {"start": v(153.6, 87.7) * mm, "end": v(163.9, 87.7) * mm});
            skLineSegment(sketch, "E3.11.5.2", {"start": v(153.6, 77.4) * mm, "end": v(163.9, 77.4) * mm});
            skLineSegment(sketch, "E3.11.5.3", {"start": v(163.9, 77.4) * mm, "end": v(163.9, 87.7) * mm});
            skLineSegment(sketch, "E3.11.6.0", {"start": v(153.6, 90.1) * mm, "end": v(153.6, 100.4) * mm});
            skLineSegment(sketch, "E3.11.6.1", {"start": v(153.6, 100.4) * mm, "end": v(163.9, 100.4) * mm});
            skLineSegment(sketch, "E3.11.6.2", {"start": v(153.6, 90.1) * mm, "end": v(163.9, 90.1) * mm});
            skLineSegment(sketch, "E3.11.6.3", {"start": v(163.9, 90.1) * mm, "end": v(163.9, 100.4) * mm});
            skLineSegment(sketch, "E3.11.7.0", {"start": v(153.6, 102.8) * mm, "end": v(153.6, 113.1) * mm});
            skLineSegment(sketch, "E3.11.7.1", {"start": v(153.6, 113.1) * mm, "end": v(163.9, 113.1) * mm});
            skLineSegment(sketch, "E3.11.7.2", {"start": v(153.6, 102.8) * mm, "end": v(163.9, 102.8) * mm});
            skLineSegment(sketch, "E3.11.7.3", {"start": v(163.9, 102.8) * mm, "end": v(163.9, 113.1) * mm});
            skLineSegment(sketch, "E3.11.8.0", {"start": v(153.6, 115.5) * mm, "end": v(153.6, 125.8) * mm});
            skLineSegment(sketch, "E3.11.8.1", {"start": v(153.6, 125.8) * mm, "end": v(163.9, 125.8) * mm});
            skLineSegment(sketch, "E3.11.8.2", {"start": v(153.6, 115.5) * mm, "end": v(163.9, 115.5) * mm});
            skLineSegment(sketch, "E3.11.8.3", {"start": v(163.9, 115.5) * mm, "end": v(163.9, 125.8) * mm});
            skLineSegment(sketch, "E3.11.9.0", {"start": v(153.6, 128.2) * mm, "end": v(153.6, 138.5) * mm});
            skLineSegment(sketch, "E3.11.9.1", {"start": v(153.6, 138.5) * mm, "end": v(163.9, 138.5) * mm});
            skLineSegment(sketch, "E3.11.9.2", {"start": v(153.6, 128.2) * mm, "end": v(163.9, 128.2) * mm});
            skLineSegment(sketch, "E3.11.9.3", {"start": v(163.9, 128.2) * mm, "end": v(163.9, 138.5) * mm});
            skLineSegment(sketch, "E3.11.10.0", {"start": v(153.6, 140.9) * mm, "end": v(153.6, 151.2) * mm});
            skLineSegment(sketch, "E3.11.10.1", {"start": v(153.6, 151.2) * mm, "end": v(163.9, 151.2) * mm});
            skLineSegment(sketch, "E3.11.10.2", {"start": v(153.6, 140.9) * mm, "end": v(163.9, 140.9) * mm});
            skLineSegment(sketch, "E3.11.10.3", {"start": v(163.9, 140.9) * mm, "end": v(163.9, 151.2) * mm});
            skLineSegment(sketch, "E3.11.11.0", {"start": v(153.6, 153.6) * mm, "end": v(153.6, 163.9) * mm});
            skLineSegment(sketch, "E3.11.11.1", {"start": v(153.6, 163.9) * mm, "end": v(163.9, 163.9) * mm});
            skLineSegment(sketch, "E3.11.11.2", {"start": v(153.6, 153.6) * mm, "end": v(163.9, 153.6) * mm});
            skLineSegment(sketch, "E3.11.11.3", {"start": v(163.9, 153.6) * mm, "end": v(163.9, 163.9) * mm});
            skLineSegment(sketch, "E3.11.12.0", {"start": v(153.6, 166.3) * mm, "end": v(153.6, 176.6) * mm});
            skLineSegment(sketch, "E3.11.12.1", {"start": v(153.6, 176.6) * mm, "end": v(163.9, 176.6) * mm});
            skLineSegment(sketch, "E3.11.12.2", {"start": v(153.6, 166.3) * mm, "end": v(163.9, 166.3) * mm});
            skLineSegment(sketch, "E3.11.12.3", {"start": v(163.9, 166.3) * mm, "end": v(163.9, 176.6) * mm});
            skLineSegment(sketch, "E3.11.13.0", {"start": v(153.6, 179) * mm, "end": v(153.6, 189.3) * mm});
            skLineSegment(sketch, "E3.11.13.1", {"start": v(153.6, 189.3) * mm, "end": v(163.9, 189.3) * mm});
            skLineSegment(sketch, "E3.11.13.2", {"start": v(153.6, 179) * mm, "end": v(163.9, 179) * mm});
            skLineSegment(sketch, "E3.11.13.3", {"start": v(163.9, 179) * mm, "end": v(163.9, 189.3) * mm});
            skLineSegment(sketch, "E3.11.14.0", {"start": v(153.6, 191.7) * mm, "end": v(153.6, 202) * mm});
            skLineSegment(sketch, "E3.11.14.1", {"start": v(153.6, 202) * mm, "end": v(163.9, 202) * mm});
            skLineSegment(sketch, "E3.11.14.2", {"start": v(153.6, 191.7) * mm, "end": v(163.9, 191.7) * mm});
            skLineSegment(sketch, "E3.11.14.3", {"start": v(163.9, 191.7) * mm, "end": v(163.9, 202) * mm});
            skLineSegment(sketch, "E3.11.15.0", {"start": v(153.6, 204.4) * mm, "end": v(153.6, 214.7) * mm});
            skLineSegment(sketch, "E3.11.15.1", {"start": v(153.6, 214.7) * mm, "end": v(163.9, 214.7) * mm});
            skLineSegment(sketch, "E3.11.15.2", {"start": v(153.6, 204.4) * mm, "end": v(163.9, 204.4) * mm});
            skLineSegment(sketch, "E3.11.15.3", {"start": v(163.9, 204.4) * mm, "end": v(163.9, 214.7) * mm});
            skLineSegment(sketch, "E3.11.16.0", {"start": v(153.6, 217.1) * mm, "end": v(153.6, 227.4) * mm});
            skLineSegment(sketch, "E3.11.16.1", {"start": v(153.6, 227.4) * mm, "end": v(163.9, 227.4) * mm});
            skLineSegment(sketch, "E3.11.16.2", {"start": v(153.6, 217.1) * mm, "end": v(163.9, 217.1) * mm});
            skLineSegment(sketch, "E3.11.16.3", {"start": v(163.9, 217.1) * mm, "end": v(163.9, 227.4) * mm});
            skLineSegment(sketch, "E3.11.17.0", {"start": v(153.6, 229.8) * mm, "end": v(153.6, 240.1) * mm});
            skLineSegment(sketch, "E3.11.17.1", {"start": v(153.6, 240.1) * mm, "end": v(163.9, 240.1) * mm});
            skLineSegment(sketch, "E3.11.17.2", {"start": v(153.6, 229.8) * mm, "end": v(163.9, 229.8) * mm});
            skLineSegment(sketch, "E3.11.17.3", {"start": v(163.9, 229.8) * mm, "end": v(163.9, 240.1) * mm});
            skLineSegment(sketch, "E3.11.18.0", {"start": v(153.6, 242.5) * mm, "end": v(153.6, 252.8) * mm});
            skLineSegment(sketch, "E3.11.18.1", {"start": v(153.6, 252.8) * mm, "end": v(163.9, 252.8) * mm});
            skLineSegment(sketch, "E3.11.18.2", {"start": v(153.6, 242.5) * mm, "end": v(163.9, 242.5) * mm});
            skLineSegment(sketch, "E3.11.18.3", {"start": v(163.9, 242.5) * mm, "end": v(163.9, 252.8) * mm});
            skLineSegment(sketch, "E3.11.19.0", {"start": v(153.6, 255.2) * mm, "end": v(153.6, 265.5) * mm});
            skLineSegment(sketch, "E3.11.19.1", {"start": v(153.6, 265.5) * mm, "end": v(163.9, 265.5) * mm});
            skLineSegment(sketch, "E3.11.19.2", {"start": v(153.6, 255.2) * mm, "end": v(163.9, 255.2) * mm});
            skLineSegment(sketch, "E3.11.19.3", {"start": v(163.9, 255.2) * mm, "end": v(163.9, 265.5) * mm});
            skLineSegment(sketch, "E3.11.20.0", {"start": v(153.6, 267.9) * mm, "end": v(153.6, 278.2) * mm});
            skLineSegment(sketch, "E3.11.20.1", {"start": v(153.6, 278.2) * mm, "end": v(163.9, 278.2) * mm});
            skLineSegment(sketch, "E3.11.20.2", {"start": v(153.6, 267.9) * mm, "end": v(163.9, 267.9) * mm});
            skLineSegment(sketch, "E3.11.20.3", {"start": v(163.9, 267.9) * mm, "end": v(163.9, 278.2) * mm});
            skLineSegment(sketch, "E3.11.21.0", {"start": v(153.6, 280.6) * mm, "end": v(153.6, 290.9) * mm});
            skLineSegment(sketch, "E3.11.21.1", {"start": v(153.6, 290.9) * mm, "end": v(163.9, 290.9) * mm});
            skLineSegment(sketch, "E3.11.21.2", {"start": v(153.6, 280.6) * mm, "end": v(163.9, 280.6) * mm});
            skLineSegment(sketch, "E3.11.21.3", {"start": v(163.9, 280.6) * mm, "end": v(163.9, 290.9) * mm});
            skLineSegment(sketch, "E3.12.0.0", {"start": v(166.3, 13.9) * mm, "end": v(166.3, 24.2) * mm});
            skLineSegment(sketch, "E3.12.0.1", {"start": v(166.3, 24.2) * mm, "end": v(176.6, 24.2) * mm});
            skLineSegment(sketch, "E3.12.0.2", {"start": v(166.3, 13.9) * mm, "end": v(176.6, 13.9) * mm});
            skLineSegment(sketch, "E3.12.0.3", {"start": v(176.6, 13.9) * mm, "end": v(176.6, 24.2) * mm});
            skLineSegment(sketch, "E3.12.1.0", {"start": v(166.3, 26.6) * mm, "end": v(166.3, 36.9) * mm});
            skLineSegment(sketch, "E3.12.1.1", {"start": v(166.3, 36.9) * mm, "end": v(176.6, 36.9) * mm});
            skLineSegment(sketch, "E3.12.1.2", {"start": v(166.3, 26.6) * mm, "end": v(176.6, 26.6) * mm});
            skLineSegment(sketch, "E3.12.1.3", {"start": v(176.6, 26.6) * mm, "end": v(176.6, 36.9) * mm});
            skLineSegment(sketch, "E3.12.2.0", {"start": v(166.3, 39.3) * mm, "end": v(166.3, 49.6) * mm});
            skLineSegment(sketch, "E3.12.2.1", {"start": v(166.3, 49.6) * mm, "end": v(176.6, 49.6) * mm});
            skLineSegment(sketch, "E3.12.2.2", {"start": v(166.3, 39.3) * mm, "end": v(176.6, 39.3) * mm});
            skLineSegment(sketch, "E3.12.2.3", {"start": v(176.6, 39.3) * mm, "end": v(176.6, 49.6) * mm});
            skLineSegment(sketch, "E3.12.3.0", {"start": v(166.3, 52) * mm, "end": v(166.3, 62.3) * mm});
            skLineSegment(sketch, "E3.12.3.1", {"start": v(166.3, 62.3) * mm, "end": v(176.6, 62.3) * mm});
            skLineSegment(sketch, "E3.12.3.2", {"start": v(166.3, 52) * mm, "end": v(176.6, 52) * mm});
            skLineSegment(sketch, "E3.12.3.3", {"start": v(176.6, 52) * mm, "end": v(176.6, 62.3) * mm});
            skLineSegment(sketch, "E3.12.4.0", {"start": v(166.3, 64.7) * mm, "end": v(166.3, 75) * mm});
            skLineSegment(sketch, "E3.12.4.1", {"start": v(166.3, 75) * mm, "end": v(176.6, 75) * mm});
            skLineSegment(sketch, "E3.12.4.2", {"start": v(166.3, 64.7) * mm, "end": v(176.6, 64.7) * mm});
            skLineSegment(sketch, "E3.12.4.3", {"start": v(176.6, 64.7) * mm, "end": v(176.6, 75) * mm});
            skLineSegment(sketch, "E3.12.5.0", {"start": v(166.3, 77.4) * mm, "end": v(166.3, 87.7) * mm});
            skLineSegment(sketch, "E3.12.5.1", {"start": v(166.3, 87.7) * mm, "end": v(176.6, 87.7) * mm});
            skLineSegment(sketch, "E3.12.5.2", {"start": v(166.3, 77.4) * mm, "end": v(176.6, 77.4) * mm});
            skLineSegment(sketch, "E3.12.5.3", {"start": v(176.6, 77.4) * mm, "end": v(176.6, 87.7) * mm});
            skLineSegment(sketch, "E3.12.6.0", {"start": v(166.3, 90.1) * mm, "end": v(166.3, 100.4) * mm});
            skLineSegment(sketch, "E3.12.6.1", {"start": v(166.3, 100.4) * mm, "end": v(176.6, 100.4) * mm});
            skLineSegment(sketch, "E3.12.6.2", {"start": v(166.3, 90.1) * mm, "end": v(176.6, 90.1) * mm});
            skLineSegment(sketch, "E3.12.6.3", {"start": v(176.6, 90.1) * mm, "end": v(176.6, 100.4) * mm});
            skLineSegment(sketch, "E3.12.7.0", {"start": v(166.3, 102.8) * mm, "end": v(166.3, 113.1) * mm});
            skLineSegment(sketch, "E3.12.7.1", {"start": v(166.3, 113.1) * mm, "end": v(176.6, 113.1) * mm});
            skLineSegment(sketch, "E3.12.7.2", {"start": v(166.3, 102.8) * mm, "end": v(176.6, 102.8) * mm});
            skLineSegment(sketch, "E3.12.7.3", {"start": v(176.6, 102.8) * mm, "end": v(176.6, 113.1) * mm});
            skLineSegment(sketch, "E3.12.8.0", {"start": v(166.3, 115.5) * mm, "end": v(166.3, 125.8) * mm});
            skLineSegment(sketch, "E3.12.8.1", {"start": v(166.3, 125.8) * mm, "end": v(176.6, 125.8) * mm});
            skLineSegment(sketch, "E3.12.8.2", {"start": v(166.3, 115.5) * mm, "end": v(176.6, 115.5) * mm});
            skLineSegment(sketch, "E3.12.8.3", {"start": v(176.6, 115.5) * mm, "end": v(176.6, 125.8) * mm});
            skLineSegment(sketch, "E3.12.9.0", {"start": v(166.3, 128.2) * mm, "end": v(166.3, 138.5) * mm});
            skLineSegment(sketch, "E3.12.9.1", {"start": v(166.3, 138.5) * mm, "end": v(176.6, 138.5) * mm});
            skLineSegment(sketch, "E3.12.9.2", {"start": v(166.3, 128.2) * mm, "end": v(176.6, 128.2) * mm});
            skLineSegment(sketch, "E3.12.9.3", {"start": v(176.6, 128.2) * mm, "end": v(176.6, 138.5) * mm});
            skLineSegment(sketch, "E3.12.10.0", {"start": v(166.3, 140.9) * mm, "end": v(166.3, 151.2) * mm});
            skLineSegment(sketch, "E3.12.10.1", {"start": v(166.3, 151.2) * mm, "end": v(176.6, 151.2) * mm});
            skLineSegment(sketch, "E3.12.10.2", {"start": v(166.3, 140.9) * mm, "end": v(176.6, 140.9) * mm});
            skLineSegment(sketch, "E3.12.10.3", {"start": v(176.6, 140.9) * mm, "end": v(176.6, 151.2) * mm});
            skLineSegment(sketch, "E3.12.11.0", {"start": v(166.3, 153.6) * mm, "end": v(166.3, 163.9) * mm});
            skLineSegment(sketch, "E3.12.11.1", {"start": v(166.3, 163.9) * mm, "end": v(176.6, 163.9) * mm});
            skLineSegment(sketch, "E3.12.11.2", {"start": v(166.3, 153.6) * mm, "end": v(176.6, 153.6) * mm});
            skLineSegment(sketch, "E3.12.11.3", {"start": v(176.6, 153.6) * mm, "end": v(176.6, 163.9) * mm});
            skLineSegment(sketch, "E3.12.12.0", {"start": v(166.3, 166.3) * mm, "end": v(166.3, 176.6) * mm});
            skLineSegment(sketch, "E3.12.12.1", {"start": v(166.3, 176.6) * mm, "end": v(176.6, 176.6) * mm});
            skLineSegment(sketch, "E3.12.12.2", {"start": v(166.3, 166.3) * mm, "end": v(176.6, 166.3) * mm});
            skLineSegment(sketch, "E3.12.12.3", {"start": v(176.6, 166.3) * mm, "end": v(176.6, 176.6) * mm});
            skLineSegment(sketch, "E3.12.13.0", {"start": v(166.3, 179) * mm, "end": v(166.3, 189.3) * mm});
            skLineSegment(sketch, "E3.12.13.1", {"start": v(166.3, 189.3) * mm, "end": v(176.6, 189.3) * mm});
            skLineSegment(sketch, "E3.12.13.2", {"start": v(166.3, 179) * mm, "end": v(176.6, 179) * mm});
            skLineSegment(sketch, "E3.12.13.3", {"start": v(176.6, 179) * mm, "end": v(176.6, 189.3) * mm});
            skLineSegment(sketch, "E3.12.14.0", {"start": v(166.3, 191.7) * mm, "end": v(166.3, 202) * mm});
            skLineSegment(sketch, "E3.12.14.1", {"start": v(166.3, 202) * mm, "end": v(176.6, 202) * mm});
            skLineSegment(sketch, "E3.12.14.2", {"start": v(166.3, 191.7) * mm, "end": v(176.6, 191.7) * mm});
            skLineSegment(sketch, "E3.12.14.3", {"start": v(176.6, 191.7) * mm, "end": v(176.6, 202) * mm});
            skLineSegment(sketch, "E3.12.15.0", {"start": v(166.3, 204.4) * mm, "end": v(166.3, 214.7) * mm});
            skLineSegment(sketch, "E3.12.15.1", {"start": v(166.3, 214.7) * mm, "end": v(176.6, 214.7) * mm});
            skLineSegment(sketch, "E3.12.15.2", {"start": v(166.3, 204.4) * mm, "end": v(176.6, 204.4) * mm});
            skLineSegment(sketch, "E3.12.15.3", {"start": v(176.6, 204.4) * mm, "end": v(176.6, 214.7) * mm});
            skLineSegment(sketch, "E3.12.16.0", {"start": v(166.3, 217.1) * mm, "end": v(166.3, 227.4) * mm});
            skLineSegment(sketch, "E3.12.16.1", {"start": v(166.3, 227.4) * mm, "end": v(176.6, 227.4) * mm});
            skLineSegment(sketch, "E3.12.16.2", {"start": v(166.3, 217.1) * mm, "end": v(176.6, 217.1) * mm});
            skLineSegment(sketch, "E3.12.16.3", {"start": v(176.6, 217.1) * mm, "end": v(176.6, 227.4) * mm});
            skLineSegment(sketch, "E3.12.17.0", {"start": v(166.3, 229.8) * mm, "end": v(166.3, 240.1) * mm});
            skLineSegment(sketch, "E3.12.17.1", {"start": v(166.3, 240.1) * mm, "end": v(176.6, 240.1) * mm});
            skLineSegment(sketch, "E3.12.17.2", {"start": v(166.3, 229.8) * mm, "end": v(176.6, 229.8) * mm});
            skLineSegment(sketch, "E3.12.17.3", {"start": v(176.6, 229.8) * mm, "end": v(176.6, 240.1) * mm});
            skLineSegment(sketch, "E3.12.18.0", {"start": v(166.3, 242.5) * mm, "end": v(166.3, 252.8) * mm});
            skLineSegment(sketch, "E3.12.18.1", {"start": v(166.3, 252.8) * mm, "end": v(176.6, 252.8) * mm});
            skLineSegment(sketch, "E3.12.18.2", {"start": v(166.3, 242.5) * mm, "end": v(176.6, 242.5) * mm});
            skLineSegment(sketch, "E3.12.18.3", {"start": v(176.6, 242.5) * mm, "end": v(176.6, 252.8) * mm});
            skLineSegment(sketch, "E3.12.19.0", {"start": v(166.3, 255.2) * mm, "end": v(166.3, 265.5) * mm});
            skLineSegment(sketch, "E3.12.19.1", {"start": v(166.3, 265.5) * mm, "end": v(176.6, 265.5) * mm});
            skLineSegment(sketch, "E3.12.19.2", {"start": v(166.3, 255.2) * mm, "end": v(176.6, 255.2) * mm});
            skLineSegment(sketch, "E3.12.19.3", {"start": v(176.6, 255.2) * mm, "end": v(176.6, 265.5) * mm});
            skLineSegment(sketch, "E3.12.20.0", {"start": v(166.3, 267.9) * mm, "end": v(166.3, 278.2) * mm});
            skLineSegment(sketch, "E3.12.20.1", {"start": v(166.3, 278.2) * mm, "end": v(176.6, 278.2) * mm});
            skLineSegment(sketch, "E3.12.20.2", {"start": v(166.3, 267.9) * mm, "end": v(176.6, 267.9) * mm});
            skLineSegment(sketch, "E3.12.20.3", {"start": v(176.6, 267.9) * mm, "end": v(176.6, 278.2) * mm});
            skLineSegment(sketch, "E3.12.21.0", {"start": v(166.3, 280.6) * mm, "end": v(166.3, 290.9) * mm});
            skLineSegment(sketch, "E3.12.21.1", {"start": v(166.3, 290.9) * mm, "end": v(176.6, 290.9) * mm});
            skLineSegment(sketch, "E3.12.21.2", {"start": v(166.3, 280.6) * mm, "end": v(176.6, 280.6) * mm});
            skLineSegment(sketch, "E3.12.21.3", {"start": v(176.6, 280.6) * mm, "end": v(176.6, 290.9) * mm});
            skLineSegment(sketch, "E3.13.0.0", {"start": v(179, 13.9) * mm, "end": v(179, 24.2) * mm});
            skLineSegment(sketch, "E3.13.0.1", {"start": v(179, 24.2) * mm, "end": v(189.3, 24.2) * mm});
            skLineSegment(sketch, "E3.13.0.2", {"start": v(179, 13.9) * mm, "end": v(189.3, 13.9) * mm});
            skLineSegment(sketch, "E3.13.0.3", {"start": v(189.3, 13.9) * mm, "end": v(189.3, 24.2) * mm});
            skLineSegment(sketch, "E3.13.1.0", {"start": v(179, 26.6) * mm, "end": v(179, 36.9) * mm});
            skLineSegment(sketch, "E3.13.1.1", {"start": v(179, 36.9) * mm, "end": v(189.3, 36.9) * mm});
            skLineSegment(sketch, "E3.13.1.2", {"start": v(179, 26.6) * mm, "end": v(189.3, 26.6) * mm});
            skLineSegment(sketch, "E3.13.1.3", {"start": v(189.3, 26.6) * mm, "end": v(189.3, 36.9) * mm});
            skLineSegment(sketch, "E3.13.2.0", {"start": v(179, 39.3) * mm, "end": v(179, 49.6) * mm});
            skLineSegment(sketch, "E3.13.2.1", {"start": v(179, 49.6) * mm, "end": v(189.3, 49.6) * mm});
            skLineSegment(sketch, "E3.13.2.2", {"start": v(179, 39.3) * mm, "end": v(189.3, 39.3) * mm});
            skLineSegment(sketch, "E3.13.2.3", {"start": v(189.3, 39.3) * mm, "end": v(189.3, 49.6) * mm});
            skLineSegment(sketch, "E3.13.3.0", {"start": v(179, 52) * mm, "end": v(179, 62.3) * mm});
            skLineSegment(sketch, "E3.13.3.1", {"start": v(179, 62.3) * mm, "end": v(189.3, 62.3) * mm});
            skLineSegment(sketch, "E3.13.3.2", {"start": v(179, 52) * mm, "end": v(189.3, 52) * mm});
            skLineSegment(sketch, "E3.13.3.3", {"start": v(189.3, 52) * mm, "end": v(189.3, 62.3) * mm});
            skLineSegment(sketch, "E3.13.4.0", {"start": v(179, 64.7) * mm, "end": v(179, 75) * mm});
            skLineSegment(sketch, "E3.13.4.1", {"start": v(179, 75) * mm, "end": v(189.3, 75) * mm});
            skLineSegment(sketch, "E3.13.4.2", {"start": v(179, 64.7) * mm, "end": v(189.3, 64.7) * mm});
            skLineSegment(sketch, "E3.13.4.3", {"start": v(189.3, 64.7) * mm, "end": v(189.3, 75) * mm});
            skLineSegment(sketch, "E3.13.5.0", {"start": v(179, 77.4) * mm, "end": v(179, 87.7) * mm});
            skLineSegment(sketch, "E3.13.5.1", {"start": v(179, 87.7) * mm, "end": v(189.3, 87.7) * mm});
            skLineSegment(sketch, "E3.13.5.2", {"start": v(179, 77.4) * mm, "end": v(189.3, 77.4) * mm});
            skLineSegment(sketch, "E3.13.5.3", {"start": v(189.3, 77.4) * mm, "end": v(189.3, 87.7) * mm});
            skLineSegment(sketch, "E3.13.6.0", {"start": v(179, 90.1) * mm, "end": v(179, 100.4) * mm});
            skLineSegment(sketch, "E3.13.6.1", {"start": v(179, 100.4) * mm, "end": v(189.3, 100.4) * mm});
            skLineSegment(sketch, "E3.13.6.2", {"start": v(179, 90.1) * mm, "end": v(189.3, 90.1) * mm});
            skLineSegment(sketch, "E3.13.6.3", {"start": v(189.3, 90.1) * mm, "end": v(189.3, 100.4) * mm});
            skLineSegment(sketch, "E3.13.7.0", {"start": v(179, 102.8) * mm, "end": v(179, 113.1) * mm});
            skLineSegment(sketch, "E3.13.7.1", {"start": v(179, 113.1) * mm, "end": v(189.3, 113.1) * mm});
            skLineSegment(sketch, "E3.13.7.2", {"start": v(179, 102.8) * mm, "end": v(189.3, 102.8) * mm});
            skLineSegment(sketch, "E3.13.7.3", {"start": v(189.3, 102.8) * mm, "end": v(189.3, 113.1) * mm});
            skLineSegment(sketch, "E3.13.8.0", {"start": v(179, 115.5) * mm, "end": v(179, 125.8) * mm});
            skLineSegment(sketch, "E3.13.8.1", {"start": v(179, 125.8) * mm, "end": v(189.3, 125.8) * mm});
            skLineSegment(sketch, "E3.13.8.2", {"start": v(179, 115.5) * mm, "end": v(189.3, 115.5) * mm});
            skLineSegment(sketch, "E3.13.8.3", {"start": v(189.3, 115.5) * mm, "end": v(189.3, 125.8) * mm});
            skLineSegment(sketch, "E3.13.9.0", {"start": v(179, 128.2) * mm, "end": v(179, 138.5) * mm});
            skLineSegment(sketch, "E3.13.9.1", {"start": v(179, 138.5) * mm, "end": v(189.3, 138.5) * mm});
            skLineSegment(sketch, "E3.13.9.2", {"start": v(179, 128.2) * mm, "end": v(189.3, 128.2) * mm});
            skLineSegment(sketch, "E3.13.9.3", {"start": v(189.3, 128.2) * mm, "end": v(189.3, 138.5) * mm});
            skLineSegment(sketch, "E3.13.10.0", {"start": v(179, 140.9) * mm, "end": v(179, 151.2) * mm});
            skLineSegment(sketch, "E3.13.10.1", {"start": v(179, 151.2) * mm, "end": v(189.3, 151.2) * mm});
            skLineSegment(sketch, "E3.13.10.2", {"start": v(179, 140.9) * mm, "end": v(189.3, 140.9) * mm});
            skLineSegment(sketch, "E3.13.10.3", {"start": v(189.3, 140.9) * mm, "end": v(189.3, 151.2) * mm});
            skLineSegment(sketch, "E3.13.11.0", {"start": v(179, 153.6) * mm, "end": v(179, 163.9) * mm});
            skLineSegment(sketch, "E3.13.11.1", {"start": v(179, 163.9) * mm, "end": v(189.3, 163.9) * mm});
            skLineSegment(sketch, "E3.13.11.2", {"start": v(179, 153.6) * mm, "end": v(189.3, 153.6) * mm});
            skLineSegment(sketch, "E3.13.11.3", {"start": v(189.3, 153.6) * mm, "end": v(189.3, 163.9) * mm});
            skLineSegment(sketch, "E3.13.12.0", {"start": v(179, 166.3) * mm, "end": v(179, 176.6) * mm});
            skLineSegment(sketch, "E3.13.12.1", {"start": v(179, 176.6) * mm, "end": v(189.3, 176.6) * mm});
            skLineSegment(sketch, "E3.13.12.2", {"start": v(179, 166.3) * mm, "end": v(189.3, 166.3) * mm});
            skLineSegment(sketch, "E3.13.12.3", {"start": v(189.3, 166.3) * mm, "end": v(189.3, 176.6) * mm});
            skLineSegment(sketch, "E3.13.13.0", {"start": v(179, 179) * mm, "end": v(179, 189.3) * mm});
            skLineSegment(sketch, "E3.13.13.1", {"start": v(179, 189.3) * mm, "end": v(189.3, 189.3) * mm});
            skLineSegment(sketch, "E3.13.13.2", {"start": v(179, 179) * mm, "end": v(189.3, 179) * mm});
            skLineSegment(sketch, "E3.13.13.3", {"start": v(189.3, 179) * mm, "end": v(189.3, 189.3) * mm});
            skLineSegment(sketch, "E3.13.14.0", {"start": v(179, 191.7) * mm, "end": v(179, 202) * mm});
            skLineSegment(sketch, "E3.13.14.1", {"start": v(179, 202) * mm, "end": v(189.3, 202) * mm});
            skLineSegment(sketch, "E3.13.14.2", {"start": v(179, 191.7) * mm, "end": v(189.3, 191.7) * mm});
            skLineSegment(sketch, "E3.13.14.3", {"start": v(189.3, 191.7) * mm, "end": v(189.3, 202) * mm});
            skLineSegment(sketch, "E3.13.15.0", {"start": v(179, 204.4) * mm, "end": v(179, 214.7) * mm});
            skLineSegment(sketch, "E3.13.15.1", {"start": v(179, 214.7) * mm, "end": v(189.3, 214.7) * mm});
            skLineSegment(sketch, "E3.13.15.2", {"start": v(179, 204.4) * mm, "end": v(189.3, 204.4) * mm});
            skLineSegment(sketch, "E3.13.15.3", {"start": v(189.3, 204.4) * mm, "end": v(189.3, 214.7) * mm});
            skLineSegment(sketch, "E3.13.16.0", {"start": v(179, 217.1) * mm, "end": v(179, 227.4) * mm});
            skLineSegment(sketch, "E3.13.16.1", {"start": v(179, 227.4) * mm, "end": v(189.3, 227.4) * mm});
            skLineSegment(sketch, "E3.13.16.2", {"start": v(179, 217.1) * mm, "end": v(189.3, 217.1) * mm});
            skLineSegment(sketch, "E3.13.16.3", {"start": v(189.3, 217.1) * mm, "end": v(189.3, 227.4) * mm});
            skLineSegment(sketch, "E3.13.17.0", {"start": v(179, 229.8) * mm, "end": v(179, 240.1) * mm});
            skLineSegment(sketch, "E3.13.17.1", {"start": v(179, 240.1) * mm, "end": v(189.3, 240.1) * mm});
            skLineSegment(sketch, "E3.13.17.2", {"start": v(179, 229.8) * mm, "end": v(189.3, 229.8) * mm});
            skLineSegment(sketch, "E3.13.17.3", {"start": v(189.3, 229.8) * mm, "end": v(189.3, 240.1) * mm});
            skLineSegment(sketch, "E3.13.18.0", {"start": v(179, 242.5) * mm, "end": v(179, 252.8) * mm});
            skLineSegment(sketch, "E3.13.18.1", {"start": v(179, 252.8) * mm, "end": v(189.3, 252.8) * mm});
            skLineSegment(sketch, "E3.13.18.2", {"start": v(179, 242.5) * mm, "end": v(189.3, 242.5) * mm});
            skLineSegment(sketch, "E3.13.18.3", {"start": v(189.3, 242.5) * mm, "end": v(189.3, 252.8) * mm});
            skLineSegment(sketch, "E3.13.19.0", {"start": v(179, 255.2) * mm, "end": v(179, 265.5) * mm});
            skLineSegment(sketch, "E3.13.19.1", {"start": v(179, 265.5) * mm, "end": v(189.3, 265.5) * mm});
            skLineSegment(sketch, "E3.13.19.2", {"start": v(179, 255.2) * mm, "end": v(189.3, 255.2) * mm});
            skLineSegment(sketch, "E3.13.19.3", {"start": v(189.3, 255.2) * mm, "end": v(189.3, 265.5) * mm});
            skLineSegment(sketch, "E3.13.20.0", {"start": v(179, 267.9) * mm, "end": v(179, 278.2) * mm});
            skLineSegment(sketch, "E3.13.20.1", {"start": v(179, 278.2) * mm, "end": v(189.3, 278.2) * mm});
            skLineSegment(sketch, "E3.13.20.2", {"start": v(179, 267.9) * mm, "end": v(189.3, 267.9) * mm});
            skLineSegment(sketch, "E3.13.20.3", {"start": v(189.3, 267.9) * mm, "end": v(189.3, 278.2) * mm});
            skLineSegment(sketch, "E3.13.21.0", {"start": v(179, 280.6) * mm, "end": v(179, 290.9) * mm});
            skLineSegment(sketch, "E3.13.21.1", {"start": v(179, 290.9) * mm, "end": v(189.3, 290.9) * mm});
            skLineSegment(sketch, "E3.13.21.2", {"start": v(179, 280.6) * mm, "end": v(189.3, 280.6) * mm});
            skLineSegment(sketch, "E3.13.21.3", {"start": v(189.3, 280.6) * mm, "end": v(189.3, 290.9) * mm});
            skLineSegment(sketch, "E3.14.0.0", {"start": v(191.7, 13.9) * mm, "end": v(191.7, 24.2) * mm});
            skLineSegment(sketch, "E3.14.0.1", {"start": v(191.7, 24.2) * mm, "end": v(202, 24.2) * mm});
            skLineSegment(sketch, "E3.14.0.2", {"start": v(191.7, 13.9) * mm, "end": v(202, 13.9) * mm});
            skLineSegment(sketch, "E3.14.0.3", {"start": v(202, 13.9) * mm, "end": v(202, 24.2) * mm});
            skLineSegment(sketch, "E3.14.1.0", {"start": v(191.7, 26.6) * mm, "end": v(191.7, 36.9) * mm});
            skLineSegment(sketch, "E3.14.1.1", {"start": v(191.7, 36.9) * mm, "end": v(202, 36.9) * mm});
            skLineSegment(sketch, "E3.14.1.2", {"start": v(191.7, 26.6) * mm, "end": v(202, 26.6) * mm});
            skLineSegment(sketch, "E3.14.1.3", {"start": v(202, 26.6) * mm, "end": v(202, 36.9) * mm});
            skLineSegment(sketch, "E3.14.2.0", {"start": v(191.7, 39.3) * mm, "end": v(191.7, 49.6) * mm});
            skLineSegment(sketch, "E3.14.2.1", {"start": v(191.7, 49.6) * mm, "end": v(202, 49.6) * mm});
            skLineSegment(sketch, "E3.14.2.2", {"start": v(191.7, 39.3) * mm, "end": v(202, 39.3) * mm});
            skLineSegment(sketch, "E3.14.2.3", {"start": v(202, 39.3) * mm, "end": v(202, 49.6) * mm});
            skLineSegment(sketch, "E3.14.3.0", {"start": v(191.7, 52) * mm, "end": v(191.7, 62.3) * mm});
            skLineSegment(sketch, "E3.14.3.1", {"start": v(191.7, 62.3) * mm, "end": v(202, 62.3) * mm});
            skLineSegment(sketch, "E3.14.3.2", {"start": v(191.7, 52) * mm, "end": v(202, 52) * mm});
            skLineSegment(sketch, "E3.14.3.3", {"start": v(202, 52) * mm, "end": v(202, 62.3) * mm});
            skLineSegment(sketch, "E3.14.4.0", {"start": v(191.7, 64.7) * mm, "end": v(191.7, 75) * mm});
            skLineSegment(sketch, "E3.14.4.1", {"start": v(191.7, 75) * mm, "end": v(202, 75) * mm});
            skLineSegment(sketch, "E3.14.4.2", {"start": v(191.7, 64.7) * mm, "end": v(202, 64.7) * mm});
            skLineSegment(sketch, "E3.14.4.3", {"start": v(202, 64.7) * mm, "end": v(202, 75) * mm});
            skLineSegment(sketch, "E3.14.5.0", {"start": v(191.7, 77.4) * mm, "end": v(191.7, 87.7) * mm});
            skLineSegment(sketch, "E3.14.5.1", {"start": v(191.7, 87.7) * mm, "end": v(202, 87.7) * mm});
            skLineSegment(sketch, "E3.14.5.2", {"start": v(191.7, 77.4) * mm, "end": v(202, 77.4) * mm});
            skLineSegment(sketch, "E3.14.5.3", {"start": v(202, 77.4) * mm, "end": v(202, 87.7) * mm});
            skLineSegment(sketch, "E3.14.6.0", {"start": v(191.7, 90.1) * mm, "end": v(191.7, 100.4) * mm});
            skLineSegment(sketch, "E3.14.6.1", {"start": v(191.7, 100.4) * mm, "end": v(202, 100.4) * mm});
            skLineSegment(sketch, "E3.14.6.2", {"start": v(191.7, 90.1) * mm, "end": v(202, 90.1) * mm});
            skLineSegment(sketch, "E3.14.6.3", {"start": v(202, 90.1) * mm, "end": v(202, 100.4) * mm});
            skLineSegment(sketch, "E3.14.7.0", {"start": v(191.7, 102.8) * mm, "end": v(191.7, 113.1) * mm});
            skLineSegment(sketch, "E3.14.7.1", {"start": v(191.7, 113.1) * mm, "end": v(202, 113.1) * mm});
            skLineSegment(sketch, "E3.14.7.2", {"start": v(191.7, 102.8) * mm, "end": v(202, 102.8) * mm});
            skLineSegment(sketch, "E3.14.7.3", {"start": v(202, 102.8) * mm, "end": v(202, 113.1) * mm});
            skLineSegment(sketch, "E3.14.8.0", {"start": v(191.7, 115.5) * mm, "end": v(191.7, 125.8) * mm});
            skLineSegment(sketch, "E3.14.8.1", {"start": v(191.7, 125.8) * mm, "end": v(202, 125.8) * mm});
            skLineSegment(sketch, "E3.14.8.2", {"start": v(191.7, 115.5) * mm, "end": v(202, 115.5) * mm});
            skLineSegment(sketch, "E3.14.8.3", {"start": v(202, 115.5) * mm, "end": v(202, 125.8) * mm});
            skLineSegment(sketch, "E3.14.9.0", {"start": v(191.7, 128.2) * mm, "end": v(191.7, 138.5) * mm});
            skLineSegment(sketch, "E3.14.9.1", {"start": v(191.7, 138.5) * mm, "end": v(202, 138.5) * mm});
            skLineSegment(sketch, "E3.14.9.2", {"start": v(191.7, 128.2) * mm, "end": v(202, 128.2) * mm});
            skLineSegment(sketch, "E3.14.9.3", {"start": v(202, 128.2) * mm, "end": v(202, 138.5) * mm});
            skLineSegment(sketch, "E3.14.10.0", {"start": v(191.7, 140.9) * mm, "end": v(191.7, 151.2) * mm});
            skLineSegment(sketch, "E3.14.10.1", {"start": v(191.7, 151.2) * mm, "end": v(202, 151.2) * mm});
            skLineSegment(sketch, "E3.14.10.2", {"start": v(191.7, 140.9) * mm, "end": v(202, 140.9) * mm});
            skLineSegment(sketch, "E3.14.10.3", {"start": v(202, 140.9) * mm, "end": v(202, 151.2) * mm});
            skLineSegment(sketch, "E3.14.11.0", {"start": v(191.7, 153.6) * mm, "end": v(191.7, 163.9) * mm});
            skLineSegment(sketch, "E3.14.11.1", {"start": v(191.7, 163.9) * mm, "end": v(202, 163.9) * mm});
            skLineSegment(sketch, "E3.14.11.2", {"start": v(191.7, 153.6) * mm, "end": v(202, 153.6) * mm});
            skLineSegment(sketch, "E3.14.11.3", {"start": v(202, 153.6) * mm, "end": v(202, 163.9) * mm});
            skLineSegment(sketch, "E3.14.12.0", {"start": v(191.7, 166.3) * mm, "end": v(191.7, 176.6) * mm});
            skLineSegment(sketch, "E3.14.12.1", {"start": v(191.7, 176.6) * mm, "end": v(202, 176.6) * mm});
            skLineSegment(sketch, "E3.14.12.2", {"start": v(191.7, 166.3) * mm, "end": v(202, 166.3) * mm});
            skLineSegment(sketch, "E3.14.12.3", {"start": v(202, 166.3) * mm, "end": v(202, 176.6) * mm});
            skLineSegment(sketch, "E3.14.13.0", {"start": v(191.7, 179) * mm, "end": v(191.7, 189.3) * mm});
            skLineSegment(sketch, "E3.14.13.1", {"start": v(191.7, 189.3) * mm, "end": v(202, 189.3) * mm});
            skLineSegment(sketch, "E3.14.13.2", {"start": v(191.7, 179) * mm, "end": v(202, 179) * mm});
            skLineSegment(sketch, "E3.14.13.3", {"start": v(202, 179) * mm, "end": v(202, 189.3) * mm});
            skLineSegment(sketch, "E3.14.14.0", {"start": v(191.7, 191.7) * mm, "end": v(191.7, 202) * mm});
            skLineSegment(sketch, "E3.14.14.1", {"start": v(191.7, 202) * mm, "end": v(202, 202) * mm});
            skLineSegment(sketch, "E3.14.14.2", {"start": v(191.7, 191.7) * mm, "end": v(202, 191.7) * mm});
            skLineSegment(sketch, "E3.14.14.3", {"start": v(202, 191.7) * mm, "end": v(202, 202) * mm});
            skLineSegment(sketch, "E3.14.15.0", {"start": v(191.7, 204.4) * mm, "end": v(191.7, 214.7) * mm});
            skLineSegment(sketch, "E3.14.15.1", {"start": v(191.7, 214.7) * mm, "end": v(202, 214.7) * mm});
            skLineSegment(sketch, "E3.14.15.2", {"start": v(191.7, 204.4) * mm, "end": v(202, 204.4) * mm});
            skLineSegment(sketch, "E3.14.15.3", {"start": v(202, 204.4) * mm, "end": v(202, 214.7) * mm});
            skLineSegment(sketch, "E3.14.16.0", {"start": v(191.7, 217.1) * mm, "end": v(191.7, 227.4) * mm});
            skLineSegment(sketch, "E3.14.16.1", {"start": v(191.7, 227.4) * mm, "end": v(202, 227.4) * mm});
            skLineSegment(sketch, "E3.14.16.2", {"start": v(191.7, 217.1) * mm, "end": v(202, 217.1) * mm});
            skLineSegment(sketch, "E3.14.16.3", {"start": v(202, 217.1) * mm, "end": v(202, 227.4) * mm});
            skLineSegment(sketch, "E3.14.17.0", {"start": v(191.7, 229.8) * mm, "end": v(191.7, 240.1) * mm});
            skLineSegment(sketch, "E3.14.17.1", {"start": v(191.7, 240.1) * mm, "end": v(202, 240.1) * mm});
            skLineSegment(sketch, "E3.14.17.2", {"start": v(191.7, 229.8) * mm, "end": v(202, 229.8) * mm});
            skLineSegment(sketch, "E3.14.17.3", {"start": v(202, 229.8) * mm, "end": v(202, 240.1) * mm});
            skLineSegment(sketch, "E3.14.18.0", {"start": v(191.7, 242.5) * mm, "end": v(191.7, 252.8) * mm});
            skLineSegment(sketch, "E3.14.18.1", {"start": v(191.7, 252.8) * mm, "end": v(202, 252.8) * mm});
            skLineSegment(sketch, "E3.14.18.2", {"start": v(191.7, 242.5) * mm, "end": v(202, 242.5) * mm});
            skLineSegment(sketch, "E3.14.18.3", {"start": v(202, 242.5) * mm, "end": v(202, 252.8) * mm});
            skLineSegment(sketch, "E3.14.19.0", {"start": v(191.7, 255.2) * mm, "end": v(191.7, 265.5) * mm});
            skLineSegment(sketch, "E3.14.19.1", {"start": v(191.7, 265.5) * mm, "end": v(202, 265.5) * mm});
            skLineSegment(sketch, "E3.14.19.2", {"start": v(191.7, 255.2) * mm, "end": v(202, 255.2) * mm});
            skLineSegment(sketch, "E3.14.19.3", {"start": v(202, 255.2) * mm, "end": v(202, 265.5) * mm});
            skLineSegment(sketch, "E3.14.20.0", {"start": v(191.7, 267.9) * mm, "end": v(191.7, 278.2) * mm});
            skLineSegment(sketch, "E3.14.20.1", {"start": v(191.7, 278.2) * mm, "end": v(202, 278.2) * mm});
            skLineSegment(sketch, "E3.14.20.2", {"start": v(191.7, 267.9) * mm, "end": v(202, 267.9) * mm});
            skLineSegment(sketch, "E3.14.20.3", {"start": v(202, 267.9) * mm, "end": v(202, 278.2) * mm});
            skLineSegment(sketch, "E3.14.21.0", {"start": v(191.7, 280.6) * mm, "end": v(191.7, 290.9) * mm});
            skLineSegment(sketch, "E3.14.21.1", {"start": v(191.7, 290.9) * mm, "end": v(202, 290.9) * mm});
            skLineSegment(sketch, "E3.14.21.2", {"start": v(191.7, 280.6) * mm, "end": v(202, 280.6) * mm});
            skLineSegment(sketch, "E3.14.21.3", {"start": v(202, 280.6) * mm, "end": v(202, 290.9) * mm});
            skLineSegment(sketch, "E3.15.0.0", {"start": v(204.4, 13.9) * mm, "end": v(204.4, 24.2) * mm});
            skLineSegment(sketch, "E3.15.0.1", {"start": v(204.4, 24.2) * mm, "end": v(214.7, 24.2) * mm});
            skLineSegment(sketch, "E3.15.0.2", {"start": v(204.4, 13.9) * mm, "end": v(214.7, 13.9) * mm});
            skLineSegment(sketch, "E3.15.0.3", {"start": v(214.7, 13.9) * mm, "end": v(214.7, 24.2) * mm});
            skLineSegment(sketch, "E3.15.1.0", {"start": v(204.4, 26.6) * mm, "end": v(204.4, 36.9) * mm});
            skLineSegment(sketch, "E3.15.1.1", {"start": v(204.4, 36.9) * mm, "end": v(214.7, 36.9) * mm});
            skLineSegment(sketch, "E3.15.1.2", {"start": v(204.4, 26.6) * mm, "end": v(214.7, 26.6) * mm});
            skLineSegment(sketch, "E3.15.1.3", {"start": v(214.7, 26.6) * mm, "end": v(214.7, 36.9) * mm});
            skLineSegment(sketch, "E3.15.2.0", {"start": v(204.4, 39.3) * mm, "end": v(204.4, 49.6) * mm});
            skLineSegment(sketch, "E3.15.2.1", {"start": v(204.4, 49.6) * mm, "end": v(214.7, 49.6) * mm});
            skLineSegment(sketch, "E3.15.2.2", {"start": v(204.4, 39.3) * mm, "end": v(214.7, 39.3) * mm});
            skLineSegment(sketch, "E3.15.2.3", {"start": v(214.7, 39.3) * mm, "end": v(214.7, 49.6) * mm});
            skLineSegment(sketch, "E3.15.3.0", {"start": v(204.4, 52) * mm, "end": v(204.4, 62.3) * mm});
            skLineSegment(sketch, "E3.15.3.1", {"start": v(204.4, 62.3) * mm, "end": v(214.7, 62.3) * mm});
            skLineSegment(sketch, "E3.15.3.2", {"start": v(204.4, 52) * mm, "end": v(214.7, 52) * mm});
            skLineSegment(sketch, "E3.15.3.3", {"start": v(214.7, 52) * mm, "end": v(214.7, 62.3) * mm});
            skLineSegment(sketch, "E3.15.4.0", {"start": v(204.4, 64.7) * mm, "end": v(204.4, 75) * mm});
            skLineSegment(sketch, "E3.15.4.1", {"start": v(204.4, 75) * mm, "end": v(214.7, 75) * mm});
            skLineSegment(sketch, "E3.15.4.2", {"start": v(204.4, 64.7) * mm, "end": v(214.7, 64.7) * mm});
            skLineSegment(sketch, "E3.15.4.3", {"start": v(214.7, 64.7) * mm, "end": v(214.7, 75) * mm});
            skLineSegment(sketch, "E3.15.5.0", {"start": v(204.4, 77.4) * mm, "end": v(204.4, 87.7) * mm});
            skLineSegment(sketch, "E3.15.5.1", {"start": v(204.4, 87.7) * mm, "end": v(214.7, 87.7) * mm});
            skLineSegment(sketch, "E3.15.5.2", {"start": v(204.4, 77.4) * mm, "end": v(214.7, 77.4) * mm});
            skLineSegment(sketch, "E3.15.5.3", {"start": v(214.7, 77.4) * mm, "end": v(214.7, 87.7) * mm});
            skLineSegment(sketch, "E3.15.6.0", {"start": v(204.4, 90.1) * mm, "end": v(204.4, 100.4) * mm});
            skLineSegment(sketch, "E3.15.6.1", {"start": v(204.4, 100.4) * mm, "end": v(214.7, 100.4) * mm});
            skLineSegment(sketch, "E3.15.6.2", {"start": v(204.4, 90.1) * mm, "end": v(214.7, 90.1) * mm});
            skLineSegment(sketch, "E3.15.6.3", {"start": v(214.7, 90.1) * mm, "end": v(214.7, 100.4) * mm});
            skLineSegment(sketch, "E3.15.7.0", {"start": v(204.4, 102.8) * mm, "end": v(204.4, 113.1) * mm});
            skLineSegment(sketch, "E3.15.7.1", {"start": v(204.4, 113.1) * mm, "end": v(214.7, 113.1) * mm});
            skLineSegment(sketch, "E3.15.7.2", {"start": v(204.4, 102.8) * mm, "end": v(214.7, 102.8) * mm});
            skLineSegment(sketch, "E3.15.7.3", {"start": v(214.7, 102.8) * mm, "end": v(214.7, 113.1) * mm});
            skLineSegment(sketch, "E3.15.8.0", {"start": v(204.4, 115.5) * mm, "end": v(204.4, 125.8) * mm});
            skLineSegment(sketch, "E3.15.8.1", {"start": v(204.4, 125.8) * mm, "end": v(214.7, 125.8) * mm});
            skLineSegment(sketch, "E3.15.8.2", {"start": v(204.4, 115.5) * mm, "end": v(214.7, 115.5) * mm});
            skLineSegment(sketch, "E3.15.8.3", {"start": v(214.7, 115.5) * mm, "end": v(214.7, 125.8) * mm});
            skLineSegment(sketch, "E3.15.9.0", {"start": v(204.4, 128.2) * mm, "end": v(204.4, 138.5) * mm});
            skLineSegment(sketch, "E3.15.9.1", {"start": v(204.4, 138.5) * mm, "end": v(214.7, 138.5) * mm});
            skLineSegment(sketch, "E3.15.9.2", {"start": v(204.4, 128.2) * mm, "end": v(214.7, 128.2) * mm});
            skLineSegment(sketch, "E3.15.9.3", {"start": v(214.7, 128.2) * mm, "end": v(214.7, 138.5) * mm});
            skLineSegment(sketch, "E3.15.10.0", {"start": v(204.4, 140.9) * mm, "end": v(204.4, 151.2) * mm});
            skLineSegment(sketch, "E3.15.10.1", {"start": v(204.4, 151.2) * mm, "end": v(214.7, 151.2) * mm});
            skLineSegment(sketch, "E3.15.10.2", {"start": v(204.4, 140.9) * mm, "end": v(214.7, 140.9) * mm});
            skLineSegment(sketch, "E3.15.10.3", {"start": v(214.7, 140.9) * mm, "end": v(214.7, 151.2) * mm});
            skLineSegment(sketch, "E3.15.11.0", {"start": v(204.4, 153.6) * mm, "end": v(204.4, 163.9) * mm});
            skLineSegment(sketch, "E3.15.11.1", {"start": v(204.4, 163.9) * mm, "end": v(214.7, 163.9) * mm});
            skLineSegment(sketch, "E3.15.11.2", {"start": v(204.4, 153.6) * mm, "end": v(214.7, 153.6) * mm});
            skLineSegment(sketch, "E3.15.11.3", {"start": v(214.7, 153.6) * mm, "end": v(214.7, 163.9) * mm});
            skLineSegment(sketch, "E3.15.12.0", {"start": v(204.4, 166.3) * mm, "end": v(204.4, 176.6) * mm});
            skLineSegment(sketch, "E3.15.12.1", {"start": v(204.4, 176.6) * mm, "end": v(214.7, 176.6) * mm});
            skLineSegment(sketch, "E3.15.12.2", {"start": v(204.4, 166.3) * mm, "end": v(214.7, 166.3) * mm});
            skLineSegment(sketch, "E3.15.12.3", {"start": v(214.7, 166.3) * mm, "end": v(214.7, 176.6) * mm});
            skLineSegment(sketch, "E3.15.13.0", {"start": v(204.4, 179) * mm, "end": v(204.4, 189.3) * mm});
            skLineSegment(sketch, "E3.15.13.1", {"start": v(204.4, 189.3) * mm, "end": v(214.7, 189.3) * mm});
            skLineSegment(sketch, "E3.15.13.2", {"start": v(204.4, 179) * mm, "end": v(214.7, 179) * mm});
            skLineSegment(sketch, "E3.15.13.3", {"start": v(214.7, 179) * mm, "end": v(214.7, 189.3) * mm});
            skLineSegment(sketch, "E3.15.14.0", {"start": v(204.4, 191.7) * mm, "end": v(204.4, 202) * mm});
            skLineSegment(sketch, "E3.15.14.1", {"start": v(204.4, 202) * mm, "end": v(214.7, 202) * mm});
            skLineSegment(sketch, "E3.15.14.2", {"start": v(204.4, 191.7) * mm, "end": v(214.7, 191.7) * mm});
            skLineSegment(sketch, "E3.15.14.3", {"start": v(214.7, 191.7) * mm, "end": v(214.7, 202) * mm});
            skLineSegment(sketch, "E3.15.15.0", {"start": v(204.4, 204.4) * mm, "end": v(204.4, 214.7) * mm});
            skLineSegment(sketch, "E3.15.15.1", {"start": v(204.4, 214.7) * mm, "end": v(214.7, 214.7) * mm});
            skLineSegment(sketch, "E3.15.15.2", {"start": v(204.4, 204.4) * mm, "end": v(214.7, 204.4) * mm});
            skLineSegment(sketch, "E3.15.15.3", {"start": v(214.7, 204.4) * mm, "end": v(214.7, 214.7) * mm});
            skLineSegment(sketch, "E3.15.16.0", {"start": v(204.4, 217.1) * mm, "end": v(204.4, 227.4) * mm});
            skLineSegment(sketch, "E3.15.16.1", {"start": v(204.4, 227.4) * mm, "end": v(214.7, 227.4) * mm});
            skLineSegment(sketch, "E3.15.16.2", {"start": v(204.4, 217.1) * mm, "end": v(214.7, 217.1) * mm});
            skLineSegment(sketch, "E3.15.16.3", {"start": v(214.7, 217.1) * mm, "end": v(214.7, 227.4) * mm});
            skLineSegment(sketch, "E3.15.17.0", {"start": v(204.4, 229.8) * mm, "end": v(204.4, 240.1) * mm});
            skLineSegment(sketch, "E3.15.17.1", {"start": v(204.4, 240.1) * mm, "end": v(214.7, 240.1) * mm});
            skLineSegment(sketch, "E3.15.17.2", {"start": v(204.4, 229.8) * mm, "end": v(214.7, 229.8) * mm});
            skLineSegment(sketch, "E3.15.17.3", {"start": v(214.7, 229.8) * mm, "end": v(214.7, 240.1) * mm});
            skLineSegment(sketch, "E3.15.18.0", {"start": v(204.4, 242.5) * mm, "end": v(204.4, 252.8) * mm});
            skLineSegment(sketch, "E3.15.18.1", {"start": v(204.4, 252.8) * mm, "end": v(214.7, 252.8) * mm});
            skLineSegment(sketch, "E3.15.18.2", {"start": v(204.4, 242.5) * mm, "end": v(214.7, 242.5) * mm});
            skLineSegment(sketch, "E3.15.18.3", {"start": v(214.7, 242.5) * mm, "end": v(214.7, 252.8) * mm});
            skLineSegment(sketch, "E3.15.19.0", {"start": v(204.4, 255.2) * mm, "end": v(204.4, 265.5) * mm});
            skLineSegment(sketch, "E3.15.19.1", {"start": v(204.4, 265.5) * mm, "end": v(214.7, 265.5) * mm});
            skLineSegment(sketch, "E3.15.19.2", {"start": v(204.4, 255.2) * mm, "end": v(214.7, 255.2) * mm});
            skLineSegment(sketch, "E3.15.19.3", {"start": v(214.7, 255.2) * mm, "end": v(214.7, 265.5) * mm});
            skLineSegment(sketch, "E3.15.20.0", {"start": v(204.4, 267.9) * mm, "end": v(204.4, 278.2) * mm});
            skLineSegment(sketch, "E3.15.20.1", {"start": v(204.4, 278.2) * mm, "end": v(214.7, 278.2) * mm});
            skLineSegment(sketch, "E3.15.20.2", {"start": v(204.4, 267.9) * mm, "end": v(214.7, 267.9) * mm});
            skLineSegment(sketch, "E3.15.20.3", {"start": v(214.7, 267.9) * mm, "end": v(214.7, 278.2) * mm});
            skLineSegment(sketch, "E3.15.21.0", {"start": v(204.4, 280.6) * mm, "end": v(204.4, 290.9) * mm});
            skLineSegment(sketch, "E3.15.21.1", {"start": v(204.4, 290.9) * mm, "end": v(214.7, 290.9) * mm});
            skLineSegment(sketch, "E3.15.21.2", {"start": v(204.4, 280.6) * mm, "end": v(214.7, 280.6) * mm});
            skLineSegment(sketch, "E3.15.21.3", {"start": v(214.7, 280.6) * mm, "end": v(214.7, 290.9) * mm});
            skLineSegment(sketch, "E3.16.0.0", {"start": v(217.1, 13.9) * mm, "end": v(217.1, 24.2) * mm});
            skLineSegment(sketch, "E3.16.0.1", {"start": v(217.1, 24.2) * mm, "end": v(227.4, 24.2) * mm});
            skLineSegment(sketch, "E3.16.0.2", {"start": v(217.1, 13.9) * mm, "end": v(227.4, 13.9) * mm});
            skLineSegment(sketch, "E3.16.0.3", {"start": v(227.4, 13.9) * mm, "end": v(227.4, 24.2) * mm});
            skLineSegment(sketch, "E3.16.1.0", {"start": v(217.1, 26.6) * mm, "end": v(217.1, 36.9) * mm});
            skLineSegment(sketch, "E3.16.1.1", {"start": v(217.1, 36.9) * mm, "end": v(227.4, 36.9) * mm});
            skLineSegment(sketch, "E3.16.1.2", {"start": v(217.1, 26.6) * mm, "end": v(227.4, 26.6) * mm});
            skLineSegment(sketch, "E3.16.1.3", {"start": v(227.4, 26.6) * mm, "end": v(227.4, 36.9) * mm});
            skLineSegment(sketch, "E3.16.2.0", {"start": v(217.1, 39.3) * mm, "end": v(217.1, 49.6) * mm});
            skLineSegment(sketch, "E3.16.2.1", {"start": v(217.1, 49.6) * mm, "end": v(227.4, 49.6) * mm});
            skLineSegment(sketch, "E3.16.2.2", {"start": v(217.1, 39.3) * mm, "end": v(227.4, 39.3) * mm});
            skLineSegment(sketch, "E3.16.2.3", {"start": v(227.4, 39.3) * mm, "end": v(227.4, 49.6) * mm});
            skLineSegment(sketch, "E3.16.3.0", {"start": v(217.1, 52) * mm, "end": v(217.1, 62.3) * mm});
            skLineSegment(sketch, "E3.16.3.1", {"start": v(217.1, 62.3) * mm, "end": v(227.4, 62.3) * mm});
            skLineSegment(sketch, "E3.16.3.2", {"start": v(217.1, 52) * mm, "end": v(227.4, 52) * mm});
            skLineSegment(sketch, "E3.16.3.3", {"start": v(227.4, 52) * mm, "end": v(227.4, 62.3) * mm});
            skLineSegment(sketch, "E3.16.4.0", {"start": v(217.1, 64.7) * mm, "end": v(217.1, 75) * mm});
            skLineSegment(sketch, "E3.16.4.1", {"start": v(217.1, 75) * mm, "end": v(227.4, 75) * mm});
            skLineSegment(sketch, "E3.16.4.2", {"start": v(217.1, 64.7) * mm, "end": v(227.4, 64.7) * mm});
            skLineSegment(sketch, "E3.16.4.3", {"start": v(227.4, 64.7) * mm, "end": v(227.4, 75) * mm});
            skLineSegment(sketch, "E3.16.5.0", {"start": v(217.1, 77.4) * mm, "end": v(217.1, 87.7) * mm});
            skLineSegment(sketch, "E3.16.5.1", {"start": v(217.1, 87.7) * mm, "end": v(227.4, 87.7) * mm});
            skLineSegment(sketch, "E3.16.5.2", {"start": v(217.1, 77.4) * mm, "end": v(227.4, 77.4) * mm});
            skLineSegment(sketch, "E3.16.5.3", {"start": v(227.4, 77.4) * mm, "end": v(227.4, 87.7) * mm});
            skLineSegment(sketch, "E3.16.6.0", {"start": v(217.1, 90.1) * mm, "end": v(217.1, 100.4) * mm});
            skLineSegment(sketch, "E3.16.6.1", {"start": v(217.1, 100.4) * mm, "end": v(227.4, 100.4) * mm});
            skLineSegment(sketch, "E3.16.6.2", {"start": v(217.1, 90.1) * mm, "end": v(227.4, 90.1) * mm});
            skLineSegment(sketch, "E3.16.6.3", {"start": v(227.4, 90.1) * mm, "end": v(227.4, 100.4) * mm});
            skLineSegment(sketch, "E3.16.7.0", {"start": v(217.1, 102.8) * mm, "end": v(217.1, 113.1) * mm});
            skLineSegment(sketch, "E3.16.7.1", {"start": v(217.1, 113.1) * mm, "end": v(227.4, 113.1) * mm});
            skLineSegment(sketch, "E3.16.7.2", {"start": v(217.1, 102.8) * mm, "end": v(227.4, 102.8) * mm});
            skLineSegment(sketch, "E3.16.7.3", {"start": v(227.4, 102.8) * mm, "end": v(227.4, 113.1) * mm});
            skLineSegment(sketch, "E3.16.8.0", {"start": v(217.1, 115.5) * mm, "end": v(217.1, 125.8) * mm});
            skLineSegment(sketch, "E3.16.8.1", {"start": v(217.1, 125.8) * mm, "end": v(227.4, 125.8) * mm});
            skLineSegment(sketch, "E3.16.8.2", {"start": v(217.1, 115.5) * mm, "end": v(227.4, 115.5) * mm});
            skLineSegment(sketch, "E3.16.8.3", {"start": v(227.4, 115.5) * mm, "end": v(227.4, 125.8) * mm});
            skLineSegment(sketch, "E3.16.9.0", {"start": v(217.1, 128.2) * mm, "end": v(217.1, 138.5) * mm});
            skLineSegment(sketch, "E3.16.9.1", {"start": v(217.1, 138.5) * mm, "end": v(227.4, 138.5) * mm});
            skLineSegment(sketch, "E3.16.9.2", {"start": v(217.1, 128.2) * mm, "end": v(227.4, 128.2) * mm});
            skLineSegment(sketch, "E3.16.9.3", {"start": v(227.4, 128.2) * mm, "end": v(227.4, 138.5) * mm});
            skLineSegment(sketch, "E3.16.10.0", {"start": v(217.1, 140.9) * mm, "end": v(217.1, 151.2) * mm});
            skLineSegment(sketch, "E3.16.10.1", {"start": v(217.1, 151.2) * mm, "end": v(227.4, 151.2) * mm});
            skLineSegment(sketch, "E3.16.10.2", {"start": v(217.1, 140.9) * mm, "end": v(227.4, 140.9) * mm});
            skLineSegment(sketch, "E3.16.10.3", {"start": v(227.4, 140.9) * mm, "end": v(227.4, 151.2) * mm});
            skLineSegment(sketch, "E3.16.11.0", {"start": v(217.1, 153.6) * mm, "end": v(217.1, 163.9) * mm});
            skLineSegment(sketch, "E3.16.11.1", {"start": v(217.1, 163.9) * mm, "end": v(227.4, 163.9) * mm});
            skLineSegment(sketch, "E3.16.11.2", {"start": v(217.1, 153.6) * mm, "end": v(227.4, 153.6) * mm});
            skLineSegment(sketch, "E3.16.11.3", {"start": v(227.4, 153.6) * mm, "end": v(227.4, 163.9) * mm});
            skLineSegment(sketch, "E3.16.12.0", {"start": v(217.1, 166.3) * mm, "end": v(217.1, 176.6) * mm});
            skLineSegment(sketch, "E3.16.12.1", {"start": v(217.1, 176.6) * mm, "end": v(227.4, 176.6) * mm});
            skLineSegment(sketch, "E3.16.12.2", {"start": v(217.1, 166.3) * mm, "end": v(227.4, 166.3) * mm});
            skLineSegment(sketch, "E3.16.12.3", {"start": v(227.4, 166.3) * mm, "end": v(227.4, 176.6) * mm});
            skLineSegment(sketch, "E3.16.13.0", {"start": v(217.1, 179) * mm, "end": v(217.1, 189.3) * mm});
            skLineSegment(sketch, "E3.16.13.1", {"start": v(217.1, 189.3) * mm, "end": v(227.4, 189.3) * mm});
            skLineSegment(sketch, "E3.16.13.2", {"start": v(217.1, 179) * mm, "end": v(227.4, 179) * mm});
            skLineSegment(sketch, "E3.16.13.3", {"start": v(227.4, 179) * mm, "end": v(227.4, 189.3) * mm});
            skLineSegment(sketch, "E3.16.14.0", {"start": v(217.1, 191.7) * mm, "end": v(217.1, 202) * mm});
            skLineSegment(sketch, "E3.16.14.1", {"start": v(217.1, 202) * mm, "end": v(227.4, 202) * mm});
            skLineSegment(sketch, "E3.16.14.2", {"start": v(217.1, 191.7) * mm, "end": v(227.4, 191.7) * mm});
            skLineSegment(sketch, "E3.16.14.3", {"start": v(227.4, 191.7) * mm, "end": v(227.4, 202) * mm});
            skLineSegment(sketch, "E3.16.15.0", {"start": v(217.1, 204.4) * mm, "end": v(217.1, 214.7) * mm});
            skLineSegment(sketch, "E3.16.15.1", {"start": v(217.1, 214.7) * mm, "end": v(227.4, 214.7) * mm});
            skLineSegment(sketch, "E3.16.15.2", {"start": v(217.1, 204.4) * mm, "end": v(227.4, 204.4) * mm});
            skLineSegment(sketch, "E3.16.15.3", {"start": v(227.4, 204.4) * mm, "end": v(227.4, 214.7) * mm});
            skLineSegment(sketch, "E3.16.16.0", {"start": v(217.1, 217.1) * mm, "end": v(217.1, 227.4) * mm});
            skLineSegment(sketch, "E3.16.16.1", {"start": v(217.1, 227.4) * mm, "end": v(227.4, 227.4) * mm});
            skLineSegment(sketch, "E3.16.16.2", {"start": v(217.1, 217.1) * mm, "end": v(227.4, 217.1) * mm});
            skLineSegment(sketch, "E3.16.16.3", {"start": v(227.4, 217.1) * mm, "end": v(227.4, 227.4) * mm});
            skLineSegment(sketch, "E3.16.17.0", {"start": v(217.1, 229.8) * mm, "end": v(217.1, 240.1) * mm});
            skLineSegment(sketch, "E3.16.17.1", {"start": v(217.1, 240.1) * mm, "end": v(227.4, 240.1) * mm});
            skLineSegment(sketch, "E3.16.17.2", {"start": v(217.1, 229.8) * mm, "end": v(227.4, 229.8) * mm});
            skLineSegment(sketch, "E3.16.17.3", {"start": v(227.4, 229.8) * mm, "end": v(227.4, 240.1) * mm});
            skLineSegment(sketch, "E3.16.18.0", {"start": v(217.1, 242.5) * mm, "end": v(217.1, 252.8) * mm});
            skLineSegment(sketch, "E3.16.18.1", {"start": v(217.1, 252.8) * mm, "end": v(227.4, 252.8) * mm});
            skLineSegment(sketch, "E3.16.18.2", {"start": v(217.1, 242.5) * mm, "end": v(227.4, 242.5) * mm});
            skLineSegment(sketch, "E3.16.18.3", {"start": v(227.4, 242.5) * mm, "end": v(227.4, 252.8) * mm});
            skLineSegment(sketch, "E3.16.19.0", {"start": v(217.1, 255.2) * mm, "end": v(217.1, 265.5) * mm});
            skLineSegment(sketch, "E3.16.19.1", {"start": v(217.1, 265.5) * mm, "end": v(227.4, 265.5) * mm});
            skLineSegment(sketch, "E3.16.19.2", {"start": v(217.1, 255.2) * mm, "end": v(227.4, 255.2) * mm});
            skLineSegment(sketch, "E3.16.19.3", {"start": v(227.4, 255.2) * mm, "end": v(227.4, 265.5) * mm});
            skLineSegment(sketch, "E3.16.20.0", {"start": v(217.1, 267.9) * mm, "end": v(217.1, 278.2) * mm});
            skLineSegment(sketch, "E3.16.20.1", {"start": v(217.1, 278.2) * mm, "end": v(227.4, 278.2) * mm});
            skLineSegment(sketch, "E3.16.20.2", {"start": v(217.1, 267.9) * mm, "end": v(227.4, 267.9) * mm});
            skLineSegment(sketch, "E3.16.20.3", {"start": v(227.4, 267.9) * mm, "end": v(227.4, 278.2) * mm});
            skLineSegment(sketch, "E3.16.21.0", {"start": v(217.1, 280.6) * mm, "end": v(217.1, 290.9) * mm});
            skLineSegment(sketch, "E3.16.21.1", {"start": v(217.1, 290.9) * mm, "end": v(227.4, 290.9) * mm});
            skLineSegment(sketch, "E3.16.21.2", {"start": v(217.1, 280.6) * mm, "end": v(227.4, 280.6) * mm});
            skLineSegment(sketch, "E3.16.21.3", {"start": v(227.4, 280.6) * mm, "end": v(227.4, 290.9) * mm});
            skLineSegment(sketch, "E3.17.0.0", {"start": v(229.8, 13.9) * mm, "end": v(229.8, 24.2) * mm});
            skLineSegment(sketch, "E3.17.0.1", {"start": v(229.8, 24.2) * mm, "end": v(240.1, 24.2) * mm});
            skLineSegment(sketch, "E3.17.0.2", {"start": v(229.8, 13.9) * mm, "end": v(240.1, 13.9) * mm});
            skLineSegment(sketch, "E3.17.0.3", {"start": v(240.1, 13.9) * mm, "end": v(240.1, 24.2) * mm});
            skLineSegment(sketch, "E3.17.1.0", {"start": v(229.8, 26.6) * mm, "end": v(229.8, 36.9) * mm});
            skLineSegment(sketch, "E3.17.1.1", {"start": v(229.8, 36.9) * mm, "end": v(240.1, 36.9) * mm});
            skLineSegment(sketch, "E3.17.1.2", {"start": v(229.8, 26.6) * mm, "end": v(240.1, 26.6) * mm});
            skLineSegment(sketch, "E3.17.1.3", {"start": v(240.1, 26.6) * mm, "end": v(240.1, 36.9) * mm});
            skLineSegment(sketch, "E3.17.2.0", {"start": v(229.8, 39.3) * mm, "end": v(229.8, 49.6) * mm});
            skLineSegment(sketch, "E3.17.2.1", {"start": v(229.8, 49.6) * mm, "end": v(240.1, 49.6) * mm});
            skLineSegment(sketch, "E3.17.2.2", {"start": v(229.8, 39.3) * mm, "end": v(240.1, 39.3) * mm});
            skLineSegment(sketch, "E3.17.2.3", {"start": v(240.1, 39.3) * mm, "end": v(240.1, 49.6) * mm});
            skLineSegment(sketch, "E3.17.3.0", {"start": v(229.8, 52) * mm, "end": v(229.8, 62.3) * mm});
            skLineSegment(sketch, "E3.17.3.1", {"start": v(229.8, 62.3) * mm, "end": v(240.1, 62.3) * mm});
            skLineSegment(sketch, "E3.17.3.2", {"start": v(229.8, 52) * mm, "end": v(240.1, 52) * mm});
            skLineSegment(sketch, "E3.17.3.3", {"start": v(240.1, 52) * mm, "end": v(240.1, 62.3) * mm});
            skLineSegment(sketch, "E3.17.4.0", {"start": v(229.8, 64.7) * mm, "end": v(229.8, 75) * mm});
            skLineSegment(sketch, "E3.17.4.1", {"start": v(229.8, 75) * mm, "end": v(240.1, 75) * mm});
            skLineSegment(sketch, "E3.17.4.2", {"start": v(229.8, 64.7) * mm, "end": v(240.1, 64.7) * mm});
            skLineSegment(sketch, "E3.17.4.3", {"start": v(240.1, 64.7) * mm, "end": v(240.1, 75) * mm});
            skLineSegment(sketch, "E3.17.5.0", {"start": v(229.8, 77.4) * mm, "end": v(229.8, 87.7) * mm});
            skLineSegment(sketch, "E3.17.5.1", {"start": v(229.8, 87.7) * mm, "end": v(240.1, 87.7) * mm});
            skLineSegment(sketch, "E3.17.5.2", {"start": v(229.8, 77.4) * mm, "end": v(240.1, 77.4) * mm});
            skLineSegment(sketch, "E3.17.5.3", {"start": v(240.1, 77.4) * mm, "end": v(240.1, 87.7) * mm});
            skLineSegment(sketch, "E3.17.6.0", {"start": v(229.8, 90.1) * mm, "end": v(229.8, 100.4) * mm});
            skLineSegment(sketch, "E3.17.6.1", {"start": v(229.8, 100.4) * mm, "end": v(240.1, 100.4) * mm});
            skLineSegment(sketch, "E3.17.6.2", {"start": v(229.8, 90.1) * mm, "end": v(240.1, 90.1) * mm});
            skLineSegment(sketch, "E3.17.6.3", {"start": v(240.1, 90.1) * mm, "end": v(240.1, 100.4) * mm});
            skLineSegment(sketch, "E3.17.7.0", {"start": v(229.8, 102.8) * mm, "end": v(229.8, 113.1) * mm});
            skLineSegment(sketch, "E3.17.7.1", {"start": v(229.8, 113.1) * mm, "end": v(240.1, 113.1) * mm});
            skLineSegment(sketch, "E3.17.7.2", {"start": v(229.8, 102.8) * mm, "end": v(240.1, 102.8) * mm});
            skLineSegment(sketch, "E3.17.7.3", {"start": v(240.1, 102.8) * mm, "end": v(240.1, 113.1) * mm});
            skLineSegment(sketch, "E3.17.8.0", {"start": v(229.8, 115.5) * mm, "end": v(229.8, 125.8) * mm});
            skLineSegment(sketch, "E3.17.8.1", {"start": v(229.8, 125.8) * mm, "end": v(240.1, 125.8) * mm});
            skLineSegment(sketch, "E3.17.8.2", {"start": v(229.8, 115.5) * mm, "end": v(240.1, 115.5) * mm});
            skLineSegment(sketch, "E3.17.8.3", {"start": v(240.1, 115.5) * mm, "end": v(240.1, 125.8) * mm});
            skLineSegment(sketch, "E3.17.9.0", {"start": v(229.8, 128.2) * mm, "end": v(229.8, 138.5) * mm});
            skLineSegment(sketch, "E3.17.9.1", {"start": v(229.8, 138.5) * mm, "end": v(240.1, 138.5) * mm});
            skLineSegment(sketch, "E3.17.9.2", {"start": v(229.8, 128.2) * mm, "end": v(240.1, 128.2) * mm});
            skLineSegment(sketch, "E3.17.9.3", {"start": v(240.1, 128.2) * mm, "end": v(240.1, 138.5) * mm});
            skLineSegment(sketch, "E3.17.10.0", {"start": v(229.8, 140.9) * mm, "end": v(229.8, 151.2) * mm});
            skLineSegment(sketch, "E3.17.10.1", {"start": v(229.8, 151.2) * mm, "end": v(240.1, 151.2) * mm});
            skLineSegment(sketch, "E3.17.10.2", {"start": v(229.8, 140.9) * mm, "end": v(240.1, 140.9) * mm});
            skLineSegment(sketch, "E3.17.10.3", {"start": v(240.1, 140.9) * mm, "end": v(240.1, 151.2) * mm});
            skLineSegment(sketch, "E3.17.11.0", {"start": v(229.8, 153.6) * mm, "end": v(229.8, 163.9) * mm});
            skLineSegment(sketch, "E3.17.11.1", {"start": v(229.8, 163.9) * mm, "end": v(240.1, 163.9) * mm});
            skLineSegment(sketch, "E3.17.11.2", {"start": v(229.8, 153.6) * mm, "end": v(240.1, 153.6) * mm});
            skLineSegment(sketch, "E3.17.11.3", {"start": v(240.1, 153.6) * mm, "end": v(240.1, 163.9) * mm});
            skLineSegment(sketch, "E3.17.12.0", {"start": v(229.8, 166.3) * mm, "end": v(229.8, 176.6) * mm});
            skLineSegment(sketch, "E3.17.12.1", {"start": v(229.8, 176.6) * mm, "end": v(240.1, 176.6) * mm});
            skLineSegment(sketch, "E3.17.12.2", {"start": v(229.8, 166.3) * mm, "end": v(240.1, 166.3) * mm});
            skLineSegment(sketch, "E3.17.12.3", {"start": v(240.1, 166.3) * mm, "end": v(240.1, 176.6) * mm});
            skLineSegment(sketch, "E3.17.13.0", {"start": v(229.8, 179) * mm, "end": v(229.8, 189.3) * mm});
            skLineSegment(sketch, "E3.17.13.1", {"start": v(229.8, 189.3) * mm, "end": v(240.1, 189.3) * mm});
            skLineSegment(sketch, "E3.17.13.2", {"start": v(229.8, 179) * mm, "end": v(240.1, 179) * mm});
            skLineSegment(sketch, "E3.17.13.3", {"start": v(240.1, 179) * mm, "end": v(240.1, 189.3) * mm});
            skLineSegment(sketch, "E3.17.14.0", {"start": v(229.8, 191.7) * mm, "end": v(229.8, 202) * mm});
            skLineSegment(sketch, "E3.17.14.1", {"start": v(229.8, 202) * mm, "end": v(240.1, 202) * mm});
            skLineSegment(sketch, "E3.17.14.2", {"start": v(229.8, 191.7) * mm, "end": v(240.1, 191.7) * mm});
            skLineSegment(sketch, "E3.17.14.3", {"start": v(240.1, 191.7) * mm, "end": v(240.1, 202) * mm});
            skLineSegment(sketch, "E3.17.15.0", {"start": v(229.8, 204.4) * mm, "end": v(229.8, 214.7) * mm});
            skLineSegment(sketch, "E3.17.15.1", {"start": v(229.8, 214.7) * mm, "end": v(240.1, 214.7) * mm});
            skLineSegment(sketch, "E3.17.15.2", {"start": v(229.8, 204.4) * mm, "end": v(240.1, 204.4) * mm});
            skLineSegment(sketch, "E3.17.15.3", {"start": v(240.1, 204.4) * mm, "end": v(240.1, 214.7) * mm});
            skLineSegment(sketch, "E3.17.16.0", {"start": v(229.8, 217.1) * mm, "end": v(229.8, 227.4) * mm});
            skLineSegment(sketch, "E3.17.16.1", {"start": v(229.8, 227.4) * mm, "end": v(240.1, 227.4) * mm});
            skLineSegment(sketch, "E3.17.16.2", {"start": v(229.8, 217.1) * mm, "end": v(240.1, 217.1) * mm});
            skLineSegment(sketch, "E3.17.16.3", {"start": v(240.1, 217.1) * mm, "end": v(240.1, 227.4) * mm});
            skLineSegment(sketch, "E3.17.17.0", {"start": v(229.8, 229.8) * mm, "end": v(229.8, 240.1) * mm});
            skLineSegment(sketch, "E3.17.17.1", {"start": v(229.8, 240.1) * mm, "end": v(240.1, 240.1) * mm});
            skLineSegment(sketch, "E3.17.17.2", {"start": v(229.8, 229.8) * mm, "end": v(240.1, 229.8) * mm});
            skLineSegment(sketch, "E3.17.17.3", {"start": v(240.1, 229.8) * mm, "end": v(240.1, 240.1) * mm});
            skLineSegment(sketch, "E3.17.18.0", {"start": v(229.8, 242.5) * mm, "end": v(229.8, 252.8) * mm});
            skLineSegment(sketch, "E3.17.18.1", {"start": v(229.8, 252.8) * mm, "end": v(240.1, 252.8) * mm});
            skLineSegment(sketch, "E3.17.18.2", {"start": v(229.8, 242.5) * mm, "end": v(240.1, 242.5) * mm});
            skLineSegment(sketch, "E3.17.18.3", {"start": v(240.1, 242.5) * mm, "end": v(240.1, 252.8) * mm});
            skLineSegment(sketch, "E3.17.19.0", {"start": v(229.8, 255.2) * mm, "end": v(229.8, 265.5) * mm});
            skLineSegment(sketch, "E3.17.19.1", {"start": v(229.8, 265.5) * mm, "end": v(240.1, 265.5) * mm});
            skLineSegment(sketch, "E3.17.19.2", {"start": v(229.8, 255.2) * mm, "end": v(240.1, 255.2) * mm});
            skLineSegment(sketch, "E3.17.19.3", {"start": v(240.1, 255.2) * mm, "end": v(240.1, 265.5) * mm});
            skLineSegment(sketch, "E3.17.20.0", {"start": v(229.8, 267.9) * mm, "end": v(229.8, 278.2) * mm});
            skLineSegment(sketch, "E3.17.20.1", {"start": v(229.8, 278.2) * mm, "end": v(240.1, 278.2) * mm});
            skLineSegment(sketch, "E3.17.20.2", {"start": v(229.8, 267.9) * mm, "end": v(240.1, 267.9) * mm});
            skLineSegment(sketch, "E3.17.20.3", {"start": v(240.1, 267.9) * mm, "end": v(240.1, 278.2) * mm});
            skLineSegment(sketch, "E3.17.21.0", {"start": v(229.8, 280.6) * mm, "end": v(229.8, 290.9) * mm});
            skLineSegment(sketch, "E3.17.21.1", {"start": v(229.8, 290.9) * mm, "end": v(240.1, 290.9) * mm});
            skLineSegment(sketch, "E3.17.21.2", {"start": v(229.8, 280.6) * mm, "end": v(240.1, 280.6) * mm});
            skLineSegment(sketch, "E3.17.21.3", {"start": v(240.1, 280.6) * mm, "end": v(240.1, 290.9) * mm});
            skLineSegment(sketch, "E3.18.0.0", {"start": v(242.5, 13.9) * mm, "end": v(242.5, 24.2) * mm});
            skLineSegment(sketch, "E3.18.0.1", {"start": v(242.5, 24.2) * mm, "end": v(252.8, 24.2) * mm});
            skLineSegment(sketch, "E3.18.0.2", {"start": v(242.5, 13.9) * mm, "end": v(252.8, 13.9) * mm});
            skLineSegment(sketch, "E3.18.0.3", {"start": v(252.8, 13.9) * mm, "end": v(252.8, 24.2) * mm});
            skLineSegment(sketch, "E3.18.1.0", {"start": v(242.5, 26.6) * mm, "end": v(242.5, 36.9) * mm});
            skLineSegment(sketch, "E3.18.1.1", {"start": v(242.5, 36.9) * mm, "end": v(252.8, 36.9) * mm});
            skLineSegment(sketch, "E3.18.1.2", {"start": v(242.5, 26.6) * mm, "end": v(252.8, 26.6) * mm});
            skLineSegment(sketch, "E3.18.1.3", {"start": v(252.8, 26.6) * mm, "end": v(252.8, 36.9) * mm});
            skLineSegment(sketch, "E3.18.2.0", {"start": v(242.5, 39.3) * mm, "end": v(242.5, 49.6) * mm});
            skLineSegment(sketch, "E3.18.2.1", {"start": v(242.5, 49.6) * mm, "end": v(252.8, 49.6) * mm});
            skLineSegment(sketch, "E3.18.2.2", {"start": v(242.5, 39.3) * mm, "end": v(252.8, 39.3) * mm});
            skLineSegment(sketch, "E3.18.2.3", {"start": v(252.8, 39.3) * mm, "end": v(252.8, 49.6) * mm});
            skLineSegment(sketch, "E3.18.3.0", {"start": v(242.5, 52) * mm, "end": v(242.5, 62.3) * mm});
            skLineSegment(sketch, "E3.18.3.1", {"start": v(242.5, 62.3) * mm, "end": v(252.8, 62.3) * mm});
            skLineSegment(sketch, "E3.18.3.2", {"start": v(242.5, 52) * mm, "end": v(252.8, 52) * mm});
            skLineSegment(sketch, "E3.18.3.3", {"start": v(252.8, 52) * mm, "end": v(252.8, 62.3) * mm});
            skLineSegment(sketch, "E3.18.4.0", {"start": v(242.5, 64.7) * mm, "end": v(242.5, 75) * mm});
            skLineSegment(sketch, "E3.18.4.1", {"start": v(242.5, 75) * mm, "end": v(252.8, 75) * mm});
            skLineSegment(sketch, "E3.18.4.2", {"start": v(242.5, 64.7) * mm, "end": v(252.8, 64.7) * mm});
            skLineSegment(sketch, "E3.18.4.3", {"start": v(252.8, 64.7) * mm, "end": v(252.8, 75) * mm});
            skLineSegment(sketch, "E3.18.5.0", {"start": v(242.5, 77.4) * mm, "end": v(242.5, 87.7) * mm});
            skLineSegment(sketch, "E3.18.5.1", {"start": v(242.5, 87.7) * mm, "end": v(252.8, 87.7) * mm});
            skLineSegment(sketch, "E3.18.5.2", {"start": v(242.5, 77.4) * mm, "end": v(252.8, 77.4) * mm});
            skLineSegment(sketch, "E3.18.5.3", {"start": v(252.8, 77.4) * mm, "end": v(252.8, 87.7) * mm});
            skLineSegment(sketch, "E3.18.6.0", {"start": v(242.5, 90.1) * mm, "end": v(242.5, 100.4) * mm});
            skLineSegment(sketch, "E3.18.6.1", {"start": v(242.5, 100.4) * mm, "end": v(252.8, 100.4) * mm});
            skLineSegment(sketch, "E3.18.6.2", {"start": v(242.5, 90.1) * mm, "end": v(252.8, 90.1) * mm});
            skLineSegment(sketch, "E3.18.6.3", {"start": v(252.8, 90.1) * mm, "end": v(252.8, 100.4) * mm});
            skLineSegment(sketch, "E3.18.7.0", {"start": v(242.5, 102.8) * mm, "end": v(242.5, 113.1) * mm});
            skLineSegment(sketch, "E3.18.7.1", {"start": v(242.5, 113.1) * mm, "end": v(252.8, 113.1) * mm});
            skLineSegment(sketch, "E3.18.7.2", {"start": v(242.5, 102.8) * mm, "end": v(252.8, 102.8) * mm});
            skLineSegment(sketch, "E3.18.7.3", {"start": v(252.8, 102.8) * mm, "end": v(252.8, 113.1) * mm});
            skLineSegment(sketch, "E3.18.8.0", {"start": v(242.5, 115.5) * mm, "end": v(242.5, 125.8) * mm});
            skLineSegment(sketch, "E3.18.8.1", {"start": v(242.5, 125.8) * mm, "end": v(252.8, 125.8) * mm});
            skLineSegment(sketch, "E3.18.8.2", {"start": v(242.5, 115.5) * mm, "end": v(252.8, 115.5) * mm});
            skLineSegment(sketch, "E3.18.8.3", {"start": v(252.8, 115.5) * mm, "end": v(252.8, 125.8) * mm});
            skLineSegment(sketch, "E3.18.9.0", {"start": v(242.5, 128.2) * mm, "end": v(242.5, 138.5) * mm});
            skLineSegment(sketch, "E3.18.9.1", {"start": v(242.5, 138.5) * mm, "end": v(252.8, 138.5) * mm});
            skLineSegment(sketch, "E3.18.9.2", {"start": v(242.5, 128.2) * mm, "end": v(252.8, 128.2) * mm});
            skLineSegment(sketch, "E3.18.9.3", {"start": v(252.8, 128.2) * mm, "end": v(252.8, 138.5) * mm});
            skLineSegment(sketch, "E3.18.10.0", {"start": v(242.5, 140.9) * mm, "end": v(242.5, 151.2) * mm});
            skLineSegment(sketch, "E3.18.10.1", {"start": v(242.5, 151.2) * mm, "end": v(252.8, 151.2) * mm});
            skLineSegment(sketch, "E3.18.10.2", {"start": v(242.5, 140.9) * mm, "end": v(252.8, 140.9) * mm});
            skLineSegment(sketch, "E3.18.10.3", {"start": v(252.8, 140.9) * mm, "end": v(252.8, 151.2) * mm});
            skLineSegment(sketch, "E3.18.11.0", {"start": v(242.5, 153.6) * mm, "end": v(242.5, 163.9) * mm});
            skLineSegment(sketch, "E3.18.11.1", {"start": v(242.5, 163.9) * mm, "end": v(252.8, 163.9) * mm});
            skLineSegment(sketch, "E3.18.11.2", {"start": v(242.5, 153.6) * mm, "end": v(252.8, 153.6) * mm});
            skLineSegment(sketch, "E3.18.11.3", {"start": v(252.8, 153.6) * mm, "end": v(252.8, 163.9) * mm});
            skLineSegment(sketch, "E3.18.12.0", {"start": v(242.5, 166.3) * mm, "end": v(242.5, 176.6) * mm});
            skLineSegment(sketch, "E3.18.12.1", {"start": v(242.5, 176.6) * mm, "end": v(252.8, 176.6) * mm});
            skLineSegment(sketch, "E3.18.12.2", {"start": v(242.5, 166.3) * mm, "end": v(252.8, 166.3) * mm});
            skLineSegment(sketch, "E3.18.12.3", {"start": v(252.8, 166.3) * mm, "end": v(252.8, 176.6) * mm});
            skLineSegment(sketch, "E3.18.13.0", {"start": v(242.5, 179) * mm, "end": v(242.5, 189.3) * mm});
            skLineSegment(sketch, "E3.18.13.1", {"start": v(242.5, 189.3) * mm, "end": v(252.8, 189.3) * mm});
            skLineSegment(sketch, "E3.18.13.2", {"start": v(242.5, 179) * mm, "end": v(252.8, 179) * mm});
            skLineSegment(sketch, "E3.18.13.3", {"start": v(252.8, 179) * mm, "end": v(252.8, 189.3) * mm});
            skLineSegment(sketch, "E3.18.14.0", {"start": v(242.5, 191.7) * mm, "end": v(242.5, 202) * mm});
            skLineSegment(sketch, "E3.18.14.1", {"start": v(242.5, 202) * mm, "end": v(252.8, 202) * mm});
            skLineSegment(sketch, "E3.18.14.2", {"start": v(242.5, 191.7) * mm, "end": v(252.8, 191.7) * mm});
            skLineSegment(sketch, "E3.18.14.3", {"start": v(252.8, 191.7) * mm, "end": v(252.8, 202) * mm});
            skLineSegment(sketch, "E3.18.15.0", {"start": v(242.5, 204.4) * mm, "end": v(242.5, 214.7) * mm});
            skLineSegment(sketch, "E3.18.15.1", {"start": v(242.5, 214.7) * mm, "end": v(252.8, 214.7) * mm});
            skLineSegment(sketch, "E3.18.15.2", {"start": v(242.5, 204.4) * mm, "end": v(252.8, 204.4) * mm});
            skLineSegment(sketch, "E3.18.15.3", {"start": v(252.8, 204.4) * mm, "end": v(252.8, 214.7) * mm});
            skLineSegment(sketch, "E3.18.16.0", {"start": v(242.5, 217.1) * mm, "end": v(242.5, 227.4) * mm});
            skLineSegment(sketch, "E3.18.16.1", {"start": v(242.5, 227.4) * mm, "end": v(252.8, 227.4) * mm});
            skLineSegment(sketch, "E3.18.16.2", {"start": v(242.5, 217.1) * mm, "end": v(252.8, 217.1) * mm});
            skLineSegment(sketch, "E3.18.16.3", {"start": v(252.8, 217.1) * mm, "end": v(252.8, 227.4) * mm});
            skLineSegment(sketch, "E3.18.17.0", {"start": v(242.5, 229.8) * mm, "end": v(242.5, 240.1) * mm});
            skLineSegment(sketch, "E3.18.17.1", {"start": v(242.5, 240.1) * mm, "end": v(252.8, 240.1) * mm});
            skLineSegment(sketch, "E3.18.17.2", {"start": v(242.5, 229.8) * mm, "end": v(252.8, 229.8) * mm});
            skLineSegment(sketch, "E3.18.17.3", {"start": v(252.8, 229.8) * mm, "end": v(252.8, 240.1) * mm});
            skLineSegment(sketch, "E3.18.18.0", {"start": v(242.5, 242.5) * mm, "end": v(242.5, 252.8) * mm});
            skLineSegment(sketch, "E3.18.18.1", {"start": v(242.5, 252.8) * mm, "end": v(252.8, 252.8) * mm});
            skLineSegment(sketch, "E3.18.18.2", {"start": v(242.5, 242.5) * mm, "end": v(252.8, 242.5) * mm});
            skLineSegment(sketch, "E3.18.18.3", {"start": v(252.8, 242.5) * mm, "end": v(252.8, 252.8) * mm});
            skLineSegment(sketch, "E3.18.19.0", {"start": v(242.5, 255.2) * mm, "end": v(242.5, 265.5) * mm});
            skLineSegment(sketch, "E3.18.19.1", {"start": v(242.5, 265.5) * mm, "end": v(252.8, 265.5) * mm});
            skLineSegment(sketch, "E3.18.19.2", {"start": v(242.5, 255.2) * mm, "end": v(252.8, 255.2) * mm});
            skLineSegment(sketch, "E3.18.19.3", {"start": v(252.8, 255.2) * mm, "end": v(252.8, 265.5) * mm});
            skLineSegment(sketch, "E3.18.20.0", {"start": v(242.5, 267.9) * mm, "end": v(242.5, 278.2) * mm});
            skLineSegment(sketch, "E3.18.20.1", {"start": v(242.5, 278.2) * mm, "end": v(252.8, 278.2) * mm});
            skLineSegment(sketch, "E3.18.20.2", {"start": v(242.5, 267.9) * mm, "end": v(252.8, 267.9) * mm});
            skLineSegment(sketch, "E3.18.20.3", {"start": v(252.8, 267.9) * mm, "end": v(252.8, 278.2) * mm});
            skLineSegment(sketch, "E3.18.21.0", {"start": v(242.5, 280.6) * mm, "end": v(242.5, 290.9) * mm});
            skLineSegment(sketch, "E3.18.21.1", {"start": v(242.5, 290.9) * mm, "end": v(252.8, 290.9) * mm});
            skLineSegment(sketch, "E3.18.21.2", {"start": v(242.5, 280.6) * mm, "end": v(252.8, 280.6) * mm});
            skLineSegment(sketch, "E3.18.21.3", {"start": v(252.8, 280.6) * mm, "end": v(252.8, 290.9) * mm});
            skLineSegment(sketch, "E3.19.0.0", {"start": v(255.2, 13.9) * mm, "end": v(255.2, 24.2) * mm});
            skLineSegment(sketch, "E3.19.0.1", {"start": v(255.2, 24.2) * mm, "end": v(265.5, 24.2) * mm});
            skLineSegment(sketch, "E3.19.0.2", {"start": v(255.2, 13.9) * mm, "end": v(265.5, 13.9) * mm});
            skLineSegment(sketch, "E3.19.0.3", {"start": v(265.5, 13.9) * mm, "end": v(265.5, 24.2) * mm});
            skLineSegment(sketch, "E3.19.1.0", {"start": v(255.2, 26.6) * mm, "end": v(255.2, 36.9) * mm});
            skLineSegment(sketch, "E3.19.1.1", {"start": v(255.2, 36.9) * mm, "end": v(265.5, 36.9) * mm});
            skLineSegment(sketch, "E3.19.1.2", {"start": v(255.2, 26.6) * mm, "end": v(265.5, 26.6) * mm});
            skLineSegment(sketch, "E3.19.1.3", {"start": v(265.5, 26.6) * mm, "end": v(265.5, 36.9) * mm});
            skLineSegment(sketch, "E3.19.2.0", {"start": v(255.2, 39.3) * mm, "end": v(255.2, 49.6) * mm});
            skLineSegment(sketch, "E3.19.2.1", {"start": v(255.2, 49.6) * mm, "end": v(265.5, 49.6) * mm});
            skLineSegment(sketch, "E3.19.2.2", {"start": v(255.2, 39.3) * mm, "end": v(265.5, 39.3) * mm});
            skLineSegment(sketch, "E3.19.2.3", {"start": v(265.5, 39.3) * mm, "end": v(265.5, 49.6) * mm});
            skLineSegment(sketch, "E3.19.3.0", {"start": v(255.2, 52) * mm, "end": v(255.2, 62.3) * mm});
            skLineSegment(sketch, "E3.19.3.1", {"start": v(255.2, 62.3) * mm, "end": v(265.5, 62.3) * mm});
            skLineSegment(sketch, "E3.19.3.2", {"start": v(255.2, 52) * mm, "end": v(265.5, 52) * mm});
            skLineSegment(sketch, "E3.19.3.3", {"start": v(265.5, 52) * mm, "end": v(265.5, 62.3) * mm});
            skLineSegment(sketch, "E3.19.4.0", {"start": v(255.2, 64.7) * mm, "end": v(255.2, 75) * mm});
            skLineSegment(sketch, "E3.19.4.1", {"start": v(255.2, 75) * mm, "end": v(265.5, 75) * mm});
            skLineSegment(sketch, "E3.19.4.2", {"start": v(255.2, 64.7) * mm, "end": v(265.5, 64.7) * mm});
            skLineSegment(sketch, "E3.19.4.3", {"start": v(265.5, 64.7) * mm, "end": v(265.5, 75) * mm});
            skLineSegment(sketch, "E3.19.5.0", {"start": v(255.2, 77.4) * mm, "end": v(255.2, 87.7) * mm});
            skLineSegment(sketch, "E3.19.5.1", {"start": v(255.2, 87.7) * mm, "end": v(265.5, 87.7) * mm});
            skLineSegment(sketch, "E3.19.5.2", {"start": v(255.2, 77.4) * mm, "end": v(265.5, 77.4) * mm});
            skLineSegment(sketch, "E3.19.5.3", {"start": v(265.5, 77.4) * mm, "end": v(265.5, 87.7) * mm});
            skLineSegment(sketch, "E3.19.6.0", {"start": v(255.2, 90.1) * mm, "end": v(255.2, 100.4) * mm});
            skLineSegment(sketch, "E3.19.6.1", {"start": v(255.2, 100.4) * mm, "end": v(265.5, 100.4) * mm});
            skLineSegment(sketch, "E3.19.6.2", {"start": v(255.2, 90.1) * mm, "end": v(265.5, 90.1) * mm});
            skLineSegment(sketch, "E3.19.6.3", {"start": v(265.5, 90.1) * mm, "end": v(265.5, 100.4) * mm});
            skLineSegment(sketch, "E3.19.7.0", {"start": v(255.2, 102.8) * mm, "end": v(255.2, 113.1) * mm});
            skLineSegment(sketch, "E3.19.7.1", {"start": v(255.2, 113.1) * mm, "end": v(265.5, 113.1) * mm});
            skLineSegment(sketch, "E3.19.7.2", {"start": v(255.2, 102.8) * mm, "end": v(265.5, 102.8) * mm});
            skLineSegment(sketch, "E3.19.7.3", {"start": v(265.5, 102.8) * mm, "end": v(265.5, 113.1) * mm});
            skLineSegment(sketch, "E3.19.8.0", {"start": v(255.2, 115.5) * mm, "end": v(255.2, 125.8) * mm});
            skLineSegment(sketch, "E3.19.8.1", {"start": v(255.2, 125.8) * mm, "end": v(265.5, 125.8) * mm});
            skLineSegment(sketch, "E3.19.8.2", {"start": v(255.2, 115.5) * mm, "end": v(265.5, 115.5) * mm});
            skLineSegment(sketch, "E3.19.8.3", {"start": v(265.5, 115.5) * mm, "end": v(265.5, 125.8) * mm});
            skLineSegment(sketch, "E3.19.9.0", {"start": v(255.2, 128.2) * mm, "end": v(255.2, 138.5) * mm});
            skLineSegment(sketch, "E3.19.9.1", {"start": v(255.2, 138.5) * mm, "end": v(265.5, 138.5) * mm});
            skLineSegment(sketch, "E3.19.9.2", {"start": v(255.2, 128.2) * mm, "end": v(265.5, 128.2) * mm});
            skLineSegment(sketch, "E3.19.9.3", {"start": v(265.5, 128.2) * mm, "end": v(265.5, 138.5) * mm});
            skLineSegment(sketch, "E3.19.10.0", {"start": v(255.2, 140.9) * mm, "end": v(255.2, 151.2) * mm});
            skLineSegment(sketch, "E3.19.10.1", {"start": v(255.2, 151.2) * mm, "end": v(265.5, 151.2) * mm});
            skLineSegment(sketch, "E3.19.10.2", {"start": v(255.2, 140.9) * mm, "end": v(265.5, 140.9) * mm});
            skLineSegment(sketch, "E3.19.10.3", {"start": v(265.5, 140.9) * mm, "end": v(265.5, 151.2) * mm});
            skLineSegment(sketch, "E3.19.11.0", {"start": v(255.2, 153.6) * mm, "end": v(255.2, 163.9) * mm});
            skLineSegment(sketch, "E3.19.11.1", {"start": v(255.2, 163.9) * mm, "end": v(265.5, 163.9) * mm});
            skLineSegment(sketch, "E3.19.11.2", {"start": v(255.2, 153.6) * mm, "end": v(265.5, 153.6) * mm});
            skLineSegment(sketch, "E3.19.11.3", {"start": v(265.5, 153.6) * mm, "end": v(265.5, 163.9) * mm});
            skLineSegment(sketch, "E3.19.12.0", {"start": v(255.2, 166.3) * mm, "end": v(255.2, 176.6) * mm});
            skLineSegment(sketch, "E3.19.12.1", {"start": v(255.2, 176.6) * mm, "end": v(265.5, 176.6) * mm});
            skLineSegment(sketch, "E3.19.12.2", {"start": v(255.2, 166.3) * mm, "end": v(265.5, 166.3) * mm});
            skLineSegment(sketch, "E3.19.12.3", {"start": v(265.5, 166.3) * mm, "end": v(265.5, 176.6) * mm});
            skLineSegment(sketch, "E3.19.13.0", {"start": v(255.2, 179) * mm, "end": v(255.2, 189.3) * mm});
            skLineSegment(sketch, "E3.19.13.1", {"start": v(255.2, 189.3) * mm, "end": v(265.5, 189.3) * mm});
            skLineSegment(sketch, "E3.19.13.2", {"start": v(255.2, 179) * mm, "end": v(265.5, 179) * mm});
            skLineSegment(sketch, "E3.19.13.3", {"start": v(265.5, 179) * mm, "end": v(265.5, 189.3) * mm});
            skLineSegment(sketch, "E3.19.14.0", {"start": v(255.2, 191.7) * mm, "end": v(255.2, 202) * mm});
            skLineSegment(sketch, "E3.19.14.1", {"start": v(255.2, 202) * mm, "end": v(265.5, 202) * mm});
            skLineSegment(sketch, "E3.19.14.2", {"start": v(255.2, 191.7) * mm, "end": v(265.5, 191.7) * mm});
            skLineSegment(sketch, "E3.19.14.3", {"start": v(265.5, 191.7) * mm, "end": v(265.5, 202) * mm});
            skLineSegment(sketch, "E3.19.15.0", {"start": v(255.2, 204.4) * mm, "end": v(255.2, 214.7) * mm});
            skLineSegment(sketch, "E3.19.15.1", {"start": v(255.2, 214.7) * mm, "end": v(265.5, 214.7) * mm});
            skLineSegment(sketch, "E3.19.15.2", {"start": v(255.2, 204.4) * mm, "end": v(265.5, 204.4) * mm});
            skLineSegment(sketch, "E3.19.15.3", {"start": v(265.5, 204.4) * mm, "end": v(265.5, 214.7) * mm});
            skLineSegment(sketch, "E3.19.16.0", {"start": v(255.2, 217.1) * mm, "end": v(255.2, 227.4) * mm});
            skLineSegment(sketch, "E3.19.16.1", {"start": v(255.2, 227.4) * mm, "end": v(265.5, 227.4) * mm});
            skLineSegment(sketch, "E3.19.16.2", {"start": v(255.2, 217.1) * mm, "end": v(265.5, 217.1) * mm});
            skLineSegment(sketch, "E3.19.16.3", {"start": v(265.5, 217.1) * mm, "end": v(265.5, 227.4) * mm});
            skLineSegment(sketch, "E3.19.17.0", {"start": v(255.2, 229.8) * mm, "end": v(255.2, 240.1) * mm});
            skLineSegment(sketch, "E3.19.17.1", {"start": v(255.2, 240.1) * mm, "end": v(265.5, 240.1) * mm});
            skLineSegment(sketch, "E3.19.17.2", {"start": v(255.2, 229.8) * mm, "end": v(265.5, 229.8) * mm});
            skLineSegment(sketch, "E3.19.17.3", {"start": v(265.5, 229.8) * mm, "end": v(265.5, 240.1) * mm});
            skLineSegment(sketch, "E3.19.18.0", {"start": v(255.2, 242.5) * mm, "end": v(255.2, 252.8) * mm});
            skLineSegment(sketch, "E3.19.18.1", {"start": v(255.2, 252.8) * mm, "end": v(265.5, 252.8) * mm});
            skLineSegment(sketch, "E3.19.18.2", {"start": v(255.2, 242.5) * mm, "end": v(265.5, 242.5) * mm});
            skLineSegment(sketch, "E3.19.18.3", {"start": v(265.5, 242.5) * mm, "end": v(265.5, 252.8) * mm});
            skLineSegment(sketch, "E3.19.19.0", {"start": v(255.2, 255.2) * mm, "end": v(255.2, 265.5) * mm});
            skLineSegment(sketch, "E3.19.19.1", {"start": v(255.2, 265.5) * mm, "end": v(265.5, 265.5) * mm});
            skLineSegment(sketch, "E3.19.19.2", {"start": v(255.2, 255.2) * mm, "end": v(265.5, 255.2) * mm});
            skLineSegment(sketch, "E3.19.19.3", {"start": v(265.5, 255.2) * mm, "end": v(265.5, 265.5) * mm});
            skLineSegment(sketch, "E3.19.20.0", {"start": v(255.2, 267.9) * mm, "end": v(255.2, 278.2) * mm});
            skLineSegment(sketch, "E3.19.20.1", {"start": v(255.2, 278.2) * mm, "end": v(265.5, 278.2) * mm});
            skLineSegment(sketch, "E3.19.20.2", {"start": v(255.2, 267.9) * mm, "end": v(265.5, 267.9) * mm});
            skLineSegment(sketch, "E3.19.20.3", {"start": v(265.5, 267.9) * mm, "end": v(265.5, 278.2) * mm});
            skLineSegment(sketch, "E3.19.21.0", {"start": v(255.2, 280.6) * mm, "end": v(255.2, 290.9) * mm});
            skLineSegment(sketch, "E3.19.21.1", {"start": v(255.2, 290.9) * mm, "end": v(265.5, 290.9) * mm});
            skLineSegment(sketch, "E3.19.21.2", {"start": v(255.2, 280.6) * mm, "end": v(265.5, 280.6) * mm});
            skLineSegment(sketch, "E3.19.21.3", {"start": v(265.5, 280.6) * mm, "end": v(265.5, 290.9) * mm});
            skLineSegment(sketch, "E3.20.0.0", {"start": v(267.9, 13.9) * mm, "end": v(267.9, 24.2) * mm});
            skLineSegment(sketch, "E3.20.0.1", {"start": v(267.9, 24.2) * mm, "end": v(278.2, 24.2) * mm});
            skLineSegment(sketch, "E3.20.0.2", {"start": v(267.9, 13.9) * mm, "end": v(278.2, 13.9) * mm});
            skLineSegment(sketch, "E3.20.0.3", {"start": v(278.2, 13.9) * mm, "end": v(278.2, 24.2) * mm});
            skLineSegment(sketch, "E3.20.1.0", {"start": v(267.9, 26.6) * mm, "end": v(267.9, 36.9) * mm});
            skLineSegment(sketch, "E3.20.1.1", {"start": v(267.9, 36.9) * mm, "end": v(278.2, 36.9) * mm});
            skLineSegment(sketch, "E3.20.1.2", {"start": v(267.9, 26.6) * mm, "end": v(278.2, 26.6) * mm});
            skLineSegment(sketch, "E3.20.1.3", {"start": v(278.2, 26.6) * mm, "end": v(278.2, 36.9) * mm});
            skLineSegment(sketch, "E3.20.2.0", {"start": v(267.9, 39.3) * mm, "end": v(267.9, 49.6) * mm});
            skLineSegment(sketch, "E3.20.2.1", {"start": v(267.9, 49.6) * mm, "end": v(278.2, 49.6) * mm});
            skLineSegment(sketch, "E3.20.2.2", {"start": v(267.9, 39.3) * mm, "end": v(278.2, 39.3) * mm});
            skLineSegment(sketch, "E3.20.2.3", {"start": v(278.2, 39.3) * mm, "end": v(278.2, 49.6) * mm});
            skLineSegment(sketch, "E3.20.3.0", {"start": v(267.9, 52) * mm, "end": v(267.9, 62.3) * mm});
            skLineSegment(sketch, "E3.20.3.1", {"start": v(267.9, 62.3) * mm, "end": v(278.2, 62.3) * mm});
            skLineSegment(sketch, "E3.20.3.2", {"start": v(267.9, 52) * mm, "end": v(278.2, 52) * mm});
            skLineSegment(sketch, "E3.20.3.3", {"start": v(278.2, 52) * mm, "end": v(278.2, 62.3) * mm});
            skLineSegment(sketch, "E3.20.4.0", {"start": v(267.9, 64.7) * mm, "end": v(267.9, 75) * mm});
            skLineSegment(sketch, "E3.20.4.1", {"start": v(267.9, 75) * mm, "end": v(278.2, 75) * mm});
            skLineSegment(sketch, "E3.20.4.2", {"start": v(267.9, 64.7) * mm, "end": v(278.2, 64.7) * mm});
            skLineSegment(sketch, "E3.20.4.3", {"start": v(278.2, 64.7) * mm, "end": v(278.2, 75) * mm});
            skLineSegment(sketch, "E3.20.5.0", {"start": v(267.9, 77.4) * mm, "end": v(267.9, 87.7) * mm});
            skLineSegment(sketch, "E3.20.5.1", {"start": v(267.9, 87.7) * mm, "end": v(278.2, 87.7) * mm});
            skLineSegment(sketch, "E3.20.5.2", {"start": v(267.9, 77.4) * mm, "end": v(278.2, 77.4) * mm});
            skLineSegment(sketch, "E3.20.5.3", {"start": v(278.2, 77.4) * mm, "end": v(278.2, 87.7) * mm});
            skLineSegment(sketch, "E3.20.6.0", {"start": v(267.9, 90.1) * mm, "end": v(267.9, 100.4) * mm});
            skLineSegment(sketch, "E3.20.6.1", {"start": v(267.9, 100.4) * mm, "end": v(278.2, 100.4) * mm});
            skLineSegment(sketch, "E3.20.6.2", {"start": v(267.9, 90.1) * mm, "end": v(278.2, 90.1) * mm});
            skLineSegment(sketch, "E3.20.6.3", {"start": v(278.2, 90.1) * mm, "end": v(278.2, 100.4) * mm});
            skLineSegment(sketch, "E3.20.7.0", {"start": v(267.9, 102.8) * mm, "end": v(267.9, 113.1) * mm});
            skLineSegment(sketch, "E3.20.7.1", {"start": v(267.9, 113.1) * mm, "end": v(278.2, 113.1) * mm});
            skLineSegment(sketch, "E3.20.7.2", {"start": v(267.9, 102.8) * mm, "end": v(278.2, 102.8) * mm});
            skLineSegment(sketch, "E3.20.7.3", {"start": v(278.2, 102.8) * mm, "end": v(278.2, 113.1) * mm});
            skLineSegment(sketch, "E3.20.8.0", {"start": v(267.9, 115.5) * mm, "end": v(267.9, 125.8) * mm});
            skLineSegment(sketch, "E3.20.8.1", {"start": v(267.9, 125.8) * mm, "end": v(278.2, 125.8) * mm});
            skLineSegment(sketch, "E3.20.8.2", {"start": v(267.9, 115.5) * mm, "end": v(278.2, 115.5) * mm});
            skLineSegment(sketch, "E3.20.8.3", {"start": v(278.2, 115.5) * mm, "end": v(278.2, 125.8) * mm});
            skLineSegment(sketch, "E3.20.9.0", {"start": v(267.9, 128.2) * mm, "end": v(267.9, 138.5) * mm});
            skLineSegment(sketch, "E3.20.9.1", {"start": v(267.9, 138.5) * mm, "end": v(278.2, 138.5) * mm});
            skLineSegment(sketch, "E3.20.9.2", {"start": v(267.9, 128.2) * mm, "end": v(278.2, 128.2) * mm});
            skLineSegment(sketch, "E3.20.9.3", {"start": v(278.2, 128.2) * mm, "end": v(278.2, 138.5) * mm});
            skLineSegment(sketch, "E3.20.10.0", {"start": v(267.9, 140.9) * mm, "end": v(267.9, 151.2) * mm});
            skLineSegment(sketch, "E3.20.10.1", {"start": v(267.9, 151.2) * mm, "end": v(278.2, 151.2) * mm});
            skLineSegment(sketch, "E3.20.10.2", {"start": v(267.9, 140.9) * mm, "end": v(278.2, 140.9) * mm});
            skLineSegment(sketch, "E3.20.10.3", {"start": v(278.2, 140.9) * mm, "end": v(278.2, 151.2) * mm});
            skLineSegment(sketch, "E3.20.11.0", {"start": v(267.9, 153.6) * mm, "end": v(267.9, 163.9) * mm});
            skLineSegment(sketch, "E3.20.11.1", {"start": v(267.9, 163.9) * mm, "end": v(278.2, 163.9) * mm});
            skLineSegment(sketch, "E3.20.11.2", {"start": v(267.9, 153.6) * mm, "end": v(278.2, 153.6) * mm});
            skLineSegment(sketch, "E3.20.11.3", {"start": v(278.2, 153.6) * mm, "end": v(278.2, 163.9) * mm});
            skLineSegment(sketch, "E3.20.12.0", {"start": v(267.9, 166.3) * mm, "end": v(267.9, 176.6) * mm});
            skLineSegment(sketch, "E3.20.12.1", {"start": v(267.9, 176.6) * mm, "end": v(278.2, 176.6) * mm});
            skLineSegment(sketch, "E3.20.12.2", {"start": v(267.9, 166.3) * mm, "end": v(278.2, 166.3) * mm});
            skLineSegment(sketch, "E3.20.12.3", {"start": v(278.2, 166.3) * mm, "end": v(278.2, 176.6) * mm});
            skLineSegment(sketch, "E3.20.13.0", {"start": v(267.9, 179) * mm, "end": v(267.9, 189.3) * mm});
            skLineSegment(sketch, "E3.20.13.1", {"start": v(267.9, 189.3) * mm, "end": v(278.2, 189.3) * mm});
            skLineSegment(sketch, "E3.20.13.2", {"start": v(267.9, 179) * mm, "end": v(278.2, 179) * mm});
            skLineSegment(sketch, "E3.20.13.3", {"start": v(278.2, 179) * mm, "end": v(278.2, 189.3) * mm});
            skLineSegment(sketch, "E3.20.14.0", {"start": v(267.9, 191.7) * mm, "end": v(267.9, 202) * mm});
            skLineSegment(sketch, "E3.20.14.1", {"start": v(267.9, 202) * mm, "end": v(278.2, 202) * mm});
            skLineSegment(sketch, "E3.20.14.2", {"start": v(267.9, 191.7) * mm, "end": v(278.2, 191.7) * mm});
            skLineSegment(sketch, "E3.20.14.3", {"start": v(278.2, 191.7) * mm, "end": v(278.2, 202) * mm});
            skLineSegment(sketch, "E3.20.15.0", {"start": v(267.9, 204.4) * mm, "end": v(267.9, 214.7) * mm});
            skLineSegment(sketch, "E3.20.15.1", {"start": v(267.9, 214.7) * mm, "end": v(278.2, 214.7) * mm});
            skLineSegment(sketch, "E3.20.15.2", {"start": v(267.9, 204.4) * mm, "end": v(278.2, 204.4) * mm});
            skLineSegment(sketch, "E3.20.15.3", {"start": v(278.2, 204.4) * mm, "end": v(278.2, 214.7) * mm});
            skLineSegment(sketch, "E3.20.16.0", {"start": v(267.9, 217.1) * mm, "end": v(267.9, 227.4) * mm});
            skLineSegment(sketch, "E3.20.16.1", {"start": v(267.9, 227.4) * mm, "end": v(278.2, 227.4) * mm});
            skLineSegment(sketch, "E3.20.16.2", {"start": v(267.9, 217.1) * mm, "end": v(278.2, 217.1) * mm});
            skLineSegment(sketch, "E3.20.16.3", {"start": v(278.2, 217.1) * mm, "end": v(278.2, 227.4) * mm});
            skLineSegment(sketch, "E3.20.17.0", {"start": v(267.9, 229.8) * mm, "end": v(267.9, 240.1) * mm});
            skLineSegment(sketch, "E3.20.17.1", {"start": v(267.9, 240.1) * mm, "end": v(278.2, 240.1) * mm});
            skLineSegment(sketch, "E3.20.17.2", {"start": v(267.9, 229.8) * mm, "end": v(278.2, 229.8) * mm});
            skLineSegment(sketch, "E3.20.17.3", {"start": v(278.2, 229.8) * mm, "end": v(278.2, 240.1) * mm});
            skLineSegment(sketch, "E3.20.18.0", {"start": v(267.9, 242.5) * mm, "end": v(267.9, 252.8) * mm});
            skLineSegment(sketch, "E3.20.18.1", {"start": v(267.9, 252.8) * mm, "end": v(278.2, 252.8) * mm});
            skLineSegment(sketch, "E3.20.18.2", {"start": v(267.9, 242.5) * mm, "end": v(278.2, 242.5) * mm});
            skLineSegment(sketch, "E3.20.18.3", {"start": v(278.2, 242.5) * mm, "end": v(278.2, 252.8) * mm});
            skLineSegment(sketch, "E3.20.19.0", {"start": v(267.9, 255.2) * mm, "end": v(267.9, 265.5) * mm});
            skLineSegment(sketch, "E3.20.19.1", {"start": v(267.9, 265.5) * mm, "end": v(278.2, 265.5) * mm});
            skLineSegment(sketch, "E3.20.19.2", {"start": v(267.9, 255.2) * mm, "end": v(278.2, 255.2) * mm});
            skLineSegment(sketch, "E3.20.19.3", {"start": v(278.2, 255.2) * mm, "end": v(278.2, 265.5) * mm});
            skLineSegment(sketch, "E3.20.20.0", {"start": v(267.9, 267.9) * mm, "end": v(267.9, 278.2) * mm});
            skLineSegment(sketch, "E3.20.20.1", {"start": v(267.9, 278.2) * mm, "end": v(278.2, 278.2) * mm});
            skLineSegment(sketch, "E3.20.20.2", {"start": v(267.9, 267.9) * mm, "end": v(278.2, 267.9) * mm});
            skLineSegment(sketch, "E3.20.20.3", {"start": v(278.2, 267.9) * mm, "end": v(278.2, 278.2) * mm});
            skLineSegment(sketch, "E3.20.21.0", {"start": v(267.9, 280.6) * mm, "end": v(267.9, 290.9) * mm});
            skLineSegment(sketch, "E3.20.21.1", {"start": v(267.9, 290.9) * mm, "end": v(278.2, 290.9) * mm});
            skLineSegment(sketch, "E3.20.21.2", {"start": v(267.9, 280.6) * mm, "end": v(278.2, 280.6) * mm});
            skLineSegment(sketch, "E3.20.21.3", {"start": v(278.2, 280.6) * mm, "end": v(278.2, 290.9) * mm});
            skLineSegment(sketch, "E3.21.0.0", {"start": v(280.6, 13.9) * mm, "end": v(280.6, 24.2) * mm});
            skLineSegment(sketch, "E3.21.0.1", {"start": v(280.6, 24.2) * mm, "end": v(290.9, 24.2) * mm});
            skLineSegment(sketch, "E3.21.0.2", {"start": v(280.6, 13.9) * mm, "end": v(290.9, 13.9) * mm});
            skLineSegment(sketch, "E3.21.0.3", {"start": v(290.9, 13.9) * mm, "end": v(290.9, 24.2) * mm});
            skLineSegment(sketch, "E3.21.1.0", {"start": v(280.6, 26.6) * mm, "end": v(280.6, 36.9) * mm});
            skLineSegment(sketch, "E3.21.1.1", {"start": v(280.6, 36.9) * mm, "end": v(290.9, 36.9) * mm});
            skLineSegment(sketch, "E3.21.1.2", {"start": v(280.6, 26.6) * mm, "end": v(290.9, 26.6) * mm});
            skLineSegment(sketch, "E3.21.1.3", {"start": v(290.9, 26.6) * mm, "end": v(290.9, 36.9) * mm});
            skLineSegment(sketch, "E3.21.2.0", {"start": v(280.6, 39.3) * mm, "end": v(280.6, 49.6) * mm});
            skLineSegment(sketch, "E3.21.2.1", {"start": v(280.6, 49.6) * mm, "end": v(290.9, 49.6) * mm});
            skLineSegment(sketch, "E3.21.2.2", {"start": v(280.6, 39.3) * mm, "end": v(290.9, 39.3) * mm});
            skLineSegment(sketch, "E3.21.2.3", {"start": v(290.9, 39.3) * mm, "end": v(290.9, 49.6) * mm});
            skLineSegment(sketch, "E3.21.3.0", {"start": v(280.6, 52) * mm, "end": v(280.6, 62.3) * mm});
            skLineSegment(sketch, "E3.21.3.1", {"start": v(280.6, 62.3) * mm, "end": v(290.9, 62.3) * mm});
            skLineSegment(sketch, "E3.21.3.2", {"start": v(280.6, 52) * mm, "end": v(290.9, 52) * mm});
            skLineSegment(sketch, "E3.21.3.3", {"start": v(290.9, 52) * mm, "end": v(290.9, 62.3) * mm});
            skLineSegment(sketch, "E3.21.4.0", {"start": v(280.6, 64.7) * mm, "end": v(280.6, 75) * mm});
            skLineSegment(sketch, "E3.21.4.1", {"start": v(280.6, 75) * mm, "end": v(290.9, 75) * mm});
            skLineSegment(sketch, "E3.21.4.2", {"start": v(280.6, 64.7) * mm, "end": v(290.9, 64.7) * mm});
            skLineSegment(sketch, "E3.21.4.3", {"start": v(290.9, 64.7) * mm, "end": v(290.9, 75) * mm});
            skLineSegment(sketch, "E3.21.5.0", {"start": v(280.6, 77.4) * mm, "end": v(280.6, 87.7) * mm});
            skLineSegment(sketch, "E3.21.5.1", {"start": v(280.6, 87.7) * mm, "end": v(290.9, 87.7) * mm});
            skLineSegment(sketch, "E3.21.5.2", {"start": v(280.6, 77.4) * mm, "end": v(290.9, 77.4) * mm});
            skLineSegment(sketch, "E3.21.5.3", {"start": v(290.9, 77.4) * mm, "end": v(290.9, 87.7) * mm});
            skLineSegment(sketch, "E3.21.6.0", {"start": v(280.6, 90.1) * mm, "end": v(280.6, 100.4) * mm});
            skLineSegment(sketch, "E3.21.6.1", {"start": v(280.6, 100.4) * mm, "end": v(290.9, 100.4) * mm});
            skLineSegment(sketch, "E3.21.6.2", {"start": v(280.6, 90.1) * mm, "end": v(290.9, 90.1) * mm});
            skLineSegment(sketch, "E3.21.6.3", {"start": v(290.9, 90.1) * mm, "end": v(290.9, 100.4) * mm});
            skLineSegment(sketch, "E3.21.7.0", {"start": v(280.6, 102.8) * mm, "end": v(280.6, 113.1) * mm});
            skLineSegment(sketch, "E3.21.7.1", {"start": v(280.6, 113.1) * mm, "end": v(290.9, 113.1) * mm});
            skLineSegment(sketch, "E3.21.7.2", {"start": v(280.6, 102.8) * mm, "end": v(290.9, 102.8) * mm});
            skLineSegment(sketch, "E3.21.7.3", {"start": v(290.9, 102.8) * mm, "end": v(290.9, 113.1) * mm});
            skLineSegment(sketch, "E3.21.8.0", {"start": v(280.6, 115.5) * mm, "end": v(280.6, 125.8) * mm});
            skLineSegment(sketch, "E3.21.8.1", {"start": v(280.6, 125.8) * mm, "end": v(290.9, 125.8) * mm});
            skLineSegment(sketch, "E3.21.8.2", {"start": v(280.6, 115.5) * mm, "end": v(290.9, 115.5) * mm});
            skLineSegment(sketch, "E3.21.8.3", {"start": v(290.9, 115.5) * mm, "end": v(290.9, 125.8) * mm});
            skLineSegment(sketch, "E3.21.9.0", {"start": v(280.6, 128.2) * mm, "end": v(280.6, 138.5) * mm});
            skLineSegment(sketch, "E3.21.9.1", {"start": v(280.6, 138.5) * mm, "end": v(290.9, 138.5) * mm});
            skLineSegment(sketch, "E3.21.9.2", {"start": v(280.6, 128.2) * mm, "end": v(290.9, 128.2) * mm});
            skLineSegment(sketch, "E3.21.9.3", {"start": v(290.9, 128.2) * mm, "end": v(290.9, 138.5) * mm});
            skLineSegment(sketch, "E3.21.10.0", {"start": v(280.6, 140.9) * mm, "end": v(280.6, 151.2) * mm});
            skLineSegment(sketch, "E3.21.10.1", {"start": v(280.6, 151.2) * mm, "end": v(290.9, 151.2) * mm});
            skLineSegment(sketch, "E3.21.10.2", {"start": v(280.6, 140.9) * mm, "end": v(290.9, 140.9) * mm});
            skLineSegment(sketch, "E3.21.10.3", {"start": v(290.9, 140.9) * mm, "end": v(290.9, 151.2) * mm});
            skLineSegment(sketch, "E3.21.11.0", {"start": v(280.6, 153.6) * mm, "end": v(280.6, 163.9) * mm});
            skLineSegment(sketch, "E3.21.11.1", {"start": v(280.6, 163.9) * mm, "end": v(290.9, 163.9) * mm});
            skLineSegment(sketch, "E3.21.11.2", {"start": v(280.6, 153.6) * mm, "end": v(290.9, 153.6) * mm});
            skLineSegment(sketch, "E3.21.11.3", {"start": v(290.9, 153.6) * mm, "end": v(290.9, 163.9) * mm});
            skLineSegment(sketch, "E3.21.12.0", {"start": v(280.6, 166.3) * mm, "end": v(280.6, 176.6) * mm});
            skLineSegment(sketch, "E3.21.12.1", {"start": v(280.6, 176.6) * mm, "end": v(290.9, 176.6) * mm});
            skLineSegment(sketch, "E3.21.12.2", {"start": v(280.6, 166.3) * mm, "end": v(290.9, 166.3) * mm});
            skLineSegment(sketch, "E3.21.12.3", {"start": v(290.9, 166.3) * mm, "end": v(290.9, 176.6) * mm});
            skLineSegment(sketch, "E3.21.13.0", {"start": v(280.6, 179) * mm, "end": v(280.6, 189.3) * mm});
            skLineSegment(sketch, "E3.21.13.1", {"start": v(280.6, 189.3) * mm, "end": v(290.9, 189.3) * mm});
            skLineSegment(sketch, "E3.21.13.2", {"start": v(280.6, 179) * mm, "end": v(290.9, 179) * mm});
            skLineSegment(sketch, "E3.21.13.3", {"start": v(290.9, 179) * mm, "end": v(290.9, 189.3) * mm});
            skLineSegment(sketch, "E3.21.14.0", {"start": v(280.6, 191.7) * mm, "end": v(280.6, 202) * mm});
            skLineSegment(sketch, "E3.21.14.1", {"start": v(280.6, 202) * mm, "end": v(290.9, 202) * mm});
            skLineSegment(sketch, "E3.21.14.2", {"start": v(280.6, 191.7) * mm, "end": v(290.9, 191.7) * mm});
            skLineSegment(sketch, "E3.21.14.3", {"start": v(290.9, 191.7) * mm, "end": v(290.9, 202) * mm});
            skLineSegment(sketch, "E3.21.15.0", {"start": v(280.6, 204.4) * mm, "end": v(280.6, 214.7) * mm});
            skLineSegment(sketch, "E3.21.15.1", {"start": v(280.6, 214.7) * mm, "end": v(290.9, 214.7) * mm});
            skLineSegment(sketch, "E3.21.15.2", {"start": v(280.6, 204.4) * mm, "end": v(290.9, 204.4) * mm});
            skLineSegment(sketch, "E3.21.15.3", {"start": v(290.9, 204.4) * mm, "end": v(290.9, 214.7) * mm});
            skLineSegment(sketch, "E3.21.16.0", {"start": v(280.6, 217.1) * mm, "end": v(280.6, 227.4) * mm});
            skLineSegment(sketch, "E3.21.16.1", {"start": v(280.6, 227.4) * mm, "end": v(290.9, 227.4) * mm});
            skLineSegment(sketch, "E3.21.16.2", {"start": v(280.6, 217.1) * mm, "end": v(290.9, 217.1) * mm});
            skLineSegment(sketch, "E3.21.16.3", {"start": v(290.9, 217.1) * mm, "end": v(290.9, 227.4) * mm});
            skLineSegment(sketch, "E3.21.17.0", {"start": v(280.6, 229.8) * mm, "end": v(280.6, 240.1) * mm});
            skLineSegment(sketch, "E3.21.17.1", {"start": v(280.6, 240.1) * mm, "end": v(290.9, 240.1) * mm});
            skLineSegment(sketch, "E3.21.17.2", {"start": v(280.6, 229.8) * mm, "end": v(290.9, 229.8) * mm});
            skLineSegment(sketch, "E3.21.17.3", {"start": v(290.9, 229.8) * mm, "end": v(290.9, 240.1) * mm});
            skLineSegment(sketch, "E3.21.18.0", {"start": v(280.6, 242.5) * mm, "end": v(280.6, 252.8) * mm});
            skLineSegment(sketch, "E3.21.18.1", {"start": v(280.6, 252.8) * mm, "end": v(290.9, 252.8) * mm});
            skLineSegment(sketch, "E3.21.18.2", {"start": v(280.6, 242.5) * mm, "end": v(290.9, 242.5) * mm});
            skLineSegment(sketch, "E3.21.18.3", {"start": v(290.9, 242.5) * mm, "end": v(290.9, 252.8) * mm});
            skLineSegment(sketch, "E3.21.19.0", {"start": v(280.6, 255.2) * mm, "end": v(280.6, 265.5) * mm});
            skLineSegment(sketch, "E3.21.19.1", {"start": v(280.6, 265.5) * mm, "end": v(290.9, 265.5) * mm});
            skLineSegment(sketch, "E3.21.19.2", {"start": v(280.6, 255.2) * mm, "end": v(290.9, 255.2) * mm});
            skLineSegment(sketch, "E3.21.19.3", {"start": v(290.9, 255.2) * mm, "end": v(290.9, 265.5) * mm});
            skLineSegment(sketch, "E3.21.20.0", {"start": v(280.6, 267.9) * mm, "end": v(280.6, 278.2) * mm});
            skLineSegment(sketch, "E3.21.20.1", {"start": v(280.6, 278.2) * mm, "end": v(290.9, 278.2) * mm});
            skLineSegment(sketch, "E3.21.20.2", {"start": v(280.6, 267.9) * mm, "end": v(290.9, 267.9) * mm});
            skLineSegment(sketch, "E3.21.20.3", {"start": v(290.9, 267.9) * mm, "end": v(290.9, 278.2) * mm});
            skLineSegment(sketch, "E3.21.21.0", {"start": v(280.6, 280.6) * mm, "end": v(280.6, 290.9) * mm});
            skLineSegment(sketch, "E3.21.21.1", {"start": v(280.6, 290.9) * mm, "end": v(290.9, 290.9) * mm});
            skLineSegment(sketch, "E3.21.21.2", {"start": v(280.6, 280.6) * mm, "end": v(290.9, 280.6) * mm});
            skLineSegment(sketch, "E3.21.21.3", {"start": v(290.9, 280.6) * mm, "end": v(290.9, 290.9) * mm});
            skLineSegment(sketch, "E3.22.0.0", {"start": v(293.3, 13.9) * mm, "end": v(293.3, 24.2) * mm});
            skLineSegment(sketch, "E3.22.0.1", {"start": v(293.3, 24.2) * mm, "end": v(303.6, 24.2) * mm});
            skLineSegment(sketch, "E3.22.0.2", {"start": v(293.3, 13.9) * mm, "end": v(303.6, 13.9) * mm});
            skLineSegment(sketch, "E3.22.0.3", {"start": v(303.6, 13.9) * mm, "end": v(303.6, 24.2) * mm});
            skLineSegment(sketch, "E3.22.1.0", {"start": v(293.3, 26.6) * mm, "end": v(293.3, 36.9) * mm});
            skLineSegment(sketch, "E3.22.1.1", {"start": v(293.3, 36.9) * mm, "end": v(303.6, 36.9) * mm});
            skLineSegment(sketch, "E3.22.1.2", {"start": v(293.3, 26.6) * mm, "end": v(303.6, 26.6) * mm});
            skLineSegment(sketch, "E3.22.1.3", {"start": v(303.6, 26.6) * mm, "end": v(303.6, 36.9) * mm});
            skLineSegment(sketch, "E3.22.2.0", {"start": v(293.3, 39.3) * mm, "end": v(293.3, 49.6) * mm});
            skLineSegment(sketch, "E3.22.2.1", {"start": v(293.3, 49.6) * mm, "end": v(303.6, 49.6) * mm});
            skLineSegment(sketch, "E3.22.2.2", {"start": v(293.3, 39.3) * mm, "end": v(303.6, 39.3) * mm});
            skLineSegment(sketch, "E3.22.2.3", {"start": v(303.6, 39.3) * mm, "end": v(303.6, 49.6) * mm});
            skLineSegment(sketch, "E3.22.3.0", {"start": v(293.3, 52) * mm, "end": v(293.3, 62.3) * mm});
            skLineSegment(sketch, "E3.22.3.1", {"start": v(293.3, 62.3) * mm, "end": v(303.6, 62.3) * mm});
            skLineSegment(sketch, "E3.22.3.2", {"start": v(293.3, 52) * mm, "end": v(303.6, 52) * mm});
            skLineSegment(sketch, "E3.22.3.3", {"start": v(303.6, 52) * mm, "end": v(303.6, 62.3) * mm});
            skLineSegment(sketch, "E3.22.4.0", {"start": v(293.3, 64.7) * mm, "end": v(293.3, 75) * mm});
            skLineSegment(sketch, "E3.22.4.1", {"start": v(293.3, 75) * mm, "end": v(303.6, 75) * mm});
            skLineSegment(sketch, "E3.22.4.2", {"start": v(293.3, 64.7) * mm, "end": v(303.6, 64.7) * mm});
            skLineSegment(sketch, "E3.22.4.3", {"start": v(303.6, 64.7) * mm, "end": v(303.6, 75) * mm});
            skLineSegment(sketch, "E3.22.5.0", {"start": v(293.3, 77.4) * mm, "end": v(293.3, 87.7) * mm});
            skLineSegment(sketch, "E3.22.5.1", {"start": v(293.3, 87.7) * mm, "end": v(303.6, 87.7) * mm});
            skLineSegment(sketch, "E3.22.5.2", {"start": v(293.3, 77.4) * mm, "end": v(303.6, 77.4) * mm});
            skLineSegment(sketch, "E3.22.5.3", {"start": v(303.6, 77.4) * mm, "end": v(303.6, 87.7) * mm});
            skLineSegment(sketch, "E3.22.6.0", {"start": v(293.3, 90.1) * mm, "end": v(293.3, 100.4) * mm});
            skLineSegment(sketch, "E3.22.6.1", {"start": v(293.3, 100.4) * mm, "end": v(303.6, 100.4) * mm});
            skLineSegment(sketch, "E3.22.6.2", {"start": v(293.3, 90.1) * mm, "end": v(303.6, 90.1) * mm});
            skLineSegment(sketch, "E3.22.6.3", {"start": v(303.6, 90.1) * mm, "end": v(303.6, 100.4) * mm});
            skLineSegment(sketch, "E3.22.7.0", {"start": v(293.3, 102.8) * mm, "end": v(293.3, 113.1) * mm});
            skLineSegment(sketch, "E3.22.7.1", {"start": v(293.3, 113.1) * mm, "end": v(303.6, 113.1) * mm});
            skLineSegment(sketch, "E3.22.7.2", {"start": v(293.3, 102.8) * mm, "end": v(303.6, 102.8) * mm});
            skLineSegment(sketch, "E3.22.7.3", {"start": v(303.6, 102.8) * mm, "end": v(303.6, 113.1) * mm});
            skLineSegment(sketch, "E3.22.8.0", {"start": v(293.3, 115.5) * mm, "end": v(293.3, 125.8) * mm});
            skLineSegment(sketch, "E3.22.8.1", {"start": v(293.3, 125.8) * mm, "end": v(303.6, 125.8) * mm});
            skLineSegment(sketch, "E3.22.8.2", {"start": v(293.3, 115.5) * mm, "end": v(303.6, 115.5) * mm});
            skLineSegment(sketch, "E3.22.8.3", {"start": v(303.6, 115.5) * mm, "end": v(303.6, 125.8) * mm});
            skLineSegment(sketch, "E3.22.9.0", {"start": v(293.3, 128.2) * mm, "end": v(293.3, 138.5) * mm});
            skLineSegment(sketch, "E3.22.9.1", {"start": v(293.3, 138.5) * mm, "end": v(303.6, 138.5) * mm});
            skLineSegment(sketch, "E3.22.9.2", {"start": v(293.3, 128.2) * mm, "end": v(303.6, 128.2) * mm});
            skLineSegment(sketch, "E3.22.9.3", {"start": v(303.6, 128.2) * mm, "end": v(303.6, 138.5) * mm});
            skLineSegment(sketch, "E3.22.10.0", {"start": v(293.3, 140.9) * mm, "end": v(293.3, 151.2) * mm});
            skLineSegment(sketch, "E3.22.10.1", {"start": v(293.3, 151.2) * mm, "end": v(303.6, 151.2) * mm});
            skLineSegment(sketch, "E3.22.10.2", {"start": v(293.3, 140.9) * mm, "end": v(303.6, 140.9) * mm});
            skLineSegment(sketch, "E3.22.10.3", {"start": v(303.6, 140.9) * mm, "end": v(303.6, 151.2) * mm});
            skLineSegment(sketch, "E3.22.11.0", {"start": v(293.3, 153.6) * mm, "end": v(293.3, 163.9) * mm});
            skLineSegment(sketch, "E3.22.11.1", {"start": v(293.3, 163.9) * mm, "end": v(303.6, 163.9) * mm});
            skLineSegment(sketch, "E3.22.11.2", {"start": v(293.3, 153.6) * mm, "end": v(303.6, 153.6) * mm});
            skLineSegment(sketch, "E3.22.11.3", {"start": v(303.6, 153.6) * mm, "end": v(303.6, 163.9) * mm});
            skLineSegment(sketch, "E3.22.12.0", {"start": v(293.3, 166.3) * mm, "end": v(293.3, 176.6) * mm});
            skLineSegment(sketch, "E3.22.12.1", {"start": v(293.3, 176.6) * mm, "end": v(303.6, 176.6) * mm});
            skLineSegment(sketch, "E3.22.12.2", {"start": v(293.3, 166.3) * mm, "end": v(303.6, 166.3) * mm});
            skLineSegment(sketch, "E3.22.12.3", {"start": v(303.6, 166.3) * mm, "end": v(303.6, 176.6) * mm});
            skLineSegment(sketch, "E3.22.13.0", {"start": v(293.3, 179) * mm, "end": v(293.3, 189.3) * mm});
            skLineSegment(sketch, "E3.22.13.1", {"start": v(293.3, 189.3) * mm, "end": v(303.6, 189.3) * mm});
            skLineSegment(sketch, "E3.22.13.2", {"start": v(293.3, 179) * mm, "end": v(303.6, 179) * mm});
            skLineSegment(sketch, "E3.22.13.3", {"start": v(303.6, 179) * mm, "end": v(303.6, 189.3) * mm});
            skLineSegment(sketch, "E3.22.14.0", {"start": v(293.3, 191.7) * mm, "end": v(293.3, 202) * mm});
            skLineSegment(sketch, "E3.22.14.1", {"start": v(293.3, 202) * mm, "end": v(303.6, 202) * mm});
            skLineSegment(sketch, "E3.22.14.2", {"start": v(293.3, 191.7) * mm, "end": v(303.6, 191.7) * mm});
            skLineSegment(sketch, "E3.22.14.3", {"start": v(303.6, 191.7) * mm, "end": v(303.6, 202) * mm});
            skLineSegment(sketch, "E3.22.15.0", {"start": v(293.3, 204.4) * mm, "end": v(293.3, 214.7) * mm});
            skLineSegment(sketch, "E3.22.15.1", {"start": v(293.3, 214.7) * mm, "end": v(303.6, 214.7) * mm});
            skLineSegment(sketch, "E3.22.15.2", {"start": v(293.3, 204.4) * mm, "end": v(303.6, 204.4) * mm});
            skLineSegment(sketch, "E3.22.15.3", {"start": v(303.6, 204.4) * mm, "end": v(303.6, 214.7) * mm});
            skLineSegment(sketch, "E3.22.16.0", {"start": v(293.3, 217.1) * mm, "end": v(293.3, 227.4) * mm});
            skLineSegment(sketch, "E3.22.16.1", {"start": v(293.3, 227.4) * mm, "end": v(303.6, 227.4) * mm});
            skLineSegment(sketch, "E3.22.16.2", {"start": v(293.3, 217.1) * mm, "end": v(303.6, 217.1) * mm});
            skLineSegment(sketch, "E3.22.16.3", {"start": v(303.6, 217.1) * mm, "end": v(303.6, 227.4) * mm});
            skLineSegment(sketch, "E3.22.17.0", {"start": v(293.3, 229.8) * mm, "end": v(293.3, 240.1) * mm});
            skLineSegment(sketch, "E3.22.17.1", {"start": v(293.3, 240.1) * mm, "end": v(303.6, 240.1) * mm});
            skLineSegment(sketch, "E3.22.17.2", {"start": v(293.3, 229.8) * mm, "end": v(303.6, 229.8) * mm});
            skLineSegment(sketch, "E3.22.17.3", {"start": v(303.6, 229.8) * mm, "end": v(303.6, 240.1) * mm});
            skLineSegment(sketch, "E3.22.18.0", {"start": v(293.3, 242.5) * mm, "end": v(293.3, 252.8) * mm});
            skLineSegment(sketch, "E3.22.18.1", {"start": v(293.3, 252.8) * mm, "end": v(303.6, 252.8) * mm});
            skLineSegment(sketch, "E3.22.18.2", {"start": v(293.3, 242.5) * mm, "end": v(303.6, 242.5) * mm});
            skLineSegment(sketch, "E3.22.18.3", {"start": v(303.6, 242.5) * mm, "end": v(303.6, 252.8) * mm});
            skLineSegment(sketch, "E3.22.19.0", {"start": v(293.3, 255.2) * mm, "end": v(293.3, 265.5) * mm});
            skLineSegment(sketch, "E3.22.19.1", {"start": v(293.3, 265.5) * mm, "end": v(303.6, 265.5) * mm});
            skLineSegment(sketch, "E3.22.19.2", {"start": v(293.3, 255.2) * mm, "end": v(303.6, 255.2) * mm});
            skLineSegment(sketch, "E3.22.19.3", {"start": v(303.6, 255.2) * mm, "end": v(303.6, 265.5) * mm});
            skLineSegment(sketch, "E3.22.20.0", {"start": v(293.3, 267.9) * mm, "end": v(293.3, 278.2) * mm});
            skLineSegment(sketch, "E3.22.20.1", {"start": v(293.3, 278.2) * mm, "end": v(303.6, 278.2) * mm});
            skLineSegment(sketch, "E3.22.20.2", {"start": v(293.3, 267.9) * mm, "end": v(303.6, 267.9) * mm});
            skLineSegment(sketch, "E3.22.20.3", {"start": v(303.6, 267.9) * mm, "end": v(303.6, 278.2) * mm});
            skLineSegment(sketch, "E3.22.21.0", {"start": v(293.3, 280.6) * mm, "end": v(293.3, 290.9) * mm});
            skLineSegment(sketch, "E3.22.21.1", {"start": v(293.3, 290.9) * mm, "end": v(303.6, 290.9) * mm});
            skLineSegment(sketch, "E3.22.21.2", {"start": v(293.3, 280.6) * mm, "end": v(303.6, 280.6) * mm});
            skLineSegment(sketch, "E3.22.21.3", {"start": v(303.6, 280.6) * mm, "end": v(303.6, 290.9) * mm});
            skLineSegment(sketch, "E3.23.0.0", {"start": v(306, 13.9) * mm, "end": v(306, 24.2) * mm});
            skLineSegment(sketch, "E3.23.0.1", {"start": v(306, 24.2) * mm, "end": v(316.3, 24.2) * mm});
            skLineSegment(sketch, "E3.23.0.2", {"start": v(306, 13.9) * mm, "end": v(316.3, 13.9) * mm});
            skLineSegment(sketch, "E3.23.0.3", {"start": v(316.3, 13.9) * mm, "end": v(316.3, 24.2) * mm});
            skLineSegment(sketch, "E3.23.1.0", {"start": v(306, 26.6) * mm, "end": v(306, 36.9) * mm});
            skLineSegment(sketch, "E3.23.1.1", {"start": v(306, 36.9) * mm, "end": v(316.3, 36.9) * mm});
            skLineSegment(sketch, "E3.23.1.2", {"start": v(306, 26.6) * mm, "end": v(316.3, 26.6) * mm});
            skLineSegment(sketch, "E3.23.1.3", {"start": v(316.3, 26.6) * mm, "end": v(316.3, 36.9) * mm});
            skLineSegment(sketch, "E3.23.2.0", {"start": v(306, 39.3) * mm, "end": v(306, 49.6) * mm});
            skLineSegment(sketch, "E3.23.2.1", {"start": v(306, 49.6) * mm, "end": v(316.3, 49.6) * mm});
            skLineSegment(sketch, "E3.23.2.2", {"start": v(306, 39.3) * mm, "end": v(316.3, 39.3) * mm});
            skLineSegment(sketch, "E3.23.2.3", {"start": v(316.3, 39.3) * mm, "end": v(316.3, 49.6) * mm});
            skLineSegment(sketch, "E3.23.3.0", {"start": v(306, 52) * mm, "end": v(306, 62.3) * mm});
            skLineSegment(sketch, "E3.23.3.1", {"start": v(306, 62.3) * mm, "end": v(316.3, 62.3) * mm});
            skLineSegment(sketch, "E3.23.3.2", {"start": v(306, 52) * mm, "end": v(316.3, 52) * mm});
            skLineSegment(sketch, "E3.23.3.3", {"start": v(316.3, 52) * mm, "end": v(316.3, 62.3) * mm});
            skLineSegment(sketch, "E3.23.4.0", {"start": v(306, 64.7) * mm, "end": v(306, 75) * mm});
            skLineSegment(sketch, "E3.23.4.1", {"start": v(306, 75) * mm, "end": v(316.3, 75) * mm});
            skLineSegment(sketch, "E3.23.4.2", {"start": v(306, 64.7) * mm, "end": v(316.3, 64.7) * mm});
            skLineSegment(sketch, "E3.23.4.3", {"start": v(316.3, 64.7) * mm, "end": v(316.3, 75) * mm});
            skLineSegment(sketch, "E3.23.5.0", {"start": v(306, 77.4) * mm, "end": v(306, 87.7) * mm});
            skLineSegment(sketch, "E3.23.5.1", {"start": v(306, 87.7) * mm, "end": v(316.3, 87.7) * mm});
            skLineSegment(sketch, "E3.23.5.2", {"start": v(306, 77.4) * mm, "end": v(316.3, 77.4) * mm});
            skLineSegment(sketch, "E3.23.5.3", {"start": v(316.3, 77.4) * mm, "end": v(316.3, 87.7) * mm});
            skLineSegment(sketch, "E3.23.6.0", {"start": v(306, 90.1) * mm, "end": v(306, 100.4) * mm});
            skLineSegment(sketch, "E3.23.6.1", {"start": v(306, 100.4) * mm, "end": v(316.3, 100.4) * mm});
            skLineSegment(sketch, "E3.23.6.2", {"start": v(306, 90.1) * mm, "end": v(316.3, 90.1) * mm});
            skLineSegment(sketch, "E3.23.6.3", {"start": v(316.3, 90.1) * mm, "end": v(316.3, 100.4) * mm});
            skLineSegment(sketch, "E3.23.7.0", {"start": v(306, 102.8) * mm, "end": v(306, 113.1) * mm});
            skLineSegment(sketch, "E3.23.7.1", {"start": v(306, 113.1) * mm, "end": v(316.3, 113.1) * mm});
            skLineSegment(sketch, "E3.23.7.2", {"start": v(306, 102.8) * mm, "end": v(316.3, 102.8) * mm});
            skLineSegment(sketch, "E3.23.7.3", {"start": v(316.3, 102.8) * mm, "end": v(316.3, 113.1) * mm});
            skLineSegment(sketch, "E3.23.8.0", {"start": v(306, 115.5) * mm, "end": v(306, 125.8) * mm});
            skLineSegment(sketch, "E3.23.8.1", {"start": v(306, 125.8) * mm, "end": v(316.3, 125.8) * mm});
            skLineSegment(sketch, "E3.23.8.2", {"start": v(306, 115.5) * mm, "end": v(316.3, 115.5) * mm});
            skLineSegment(sketch, "E3.23.8.3", {"start": v(316.3, 115.5) * mm, "end": v(316.3, 125.8) * mm});
            skLineSegment(sketch, "E3.23.9.0", {"start": v(306, 128.2) * mm, "end": v(306, 138.5) * mm});
            skLineSegment(sketch, "E3.23.9.1", {"start": v(306, 138.5) * mm, "end": v(316.3, 138.5) * mm});
            skLineSegment(sketch, "E3.23.9.2", {"start": v(306, 128.2) * mm, "end": v(316.3, 128.2) * mm});
            skLineSegment(sketch, "E3.23.9.3", {"start": v(316.3, 128.2) * mm, "end": v(316.3, 138.5) * mm});
            skLineSegment(sketch, "E3.23.10.0", {"start": v(306, 140.9) * mm, "end": v(306, 151.2) * mm});
            skLineSegment(sketch, "E3.23.10.1", {"start": v(306, 151.2) * mm, "end": v(316.3, 151.2) * mm});
            skLineSegment(sketch, "E3.23.10.2", {"start": v(306, 140.9) * mm, "end": v(316.3, 140.9) * mm});
            skLineSegment(sketch, "E3.23.10.3", {"start": v(316.3, 140.9) * mm, "end": v(316.3, 151.2) * mm});
            skLineSegment(sketch, "E3.23.11.0", {"start": v(306, 153.6) * mm, "end": v(306, 163.9) * mm});
            skLineSegment(sketch, "E3.23.11.1", {"start": v(306, 163.9) * mm, "end": v(316.3, 163.9) * mm});
            skLineSegment(sketch, "E3.23.11.2", {"start": v(306, 153.6) * mm, "end": v(316.3, 153.6) * mm});
            skLineSegment(sketch, "E3.23.11.3", {"start": v(316.3, 153.6) * mm, "end": v(316.3, 163.9) * mm});
            skLineSegment(sketch, "E3.23.12.0", {"start": v(306, 166.3) * mm, "end": v(306, 176.6) * mm});
            skLineSegment(sketch, "E3.23.12.1", {"start": v(306, 176.6) * mm, "end": v(316.3, 176.6) * mm});
            skLineSegment(sketch, "E3.23.12.2", {"start": v(306, 166.3) * mm, "end": v(316.3, 166.3) * mm});
            skLineSegment(sketch, "E3.23.12.3", {"start": v(316.3, 166.3) * mm, "end": v(316.3, 176.6) * mm});
            skLineSegment(sketch, "E3.23.13.0", {"start": v(306, 179) * mm, "end": v(306, 189.3) * mm});
            skLineSegment(sketch, "E3.23.13.1", {"start": v(306, 189.3) * mm, "end": v(316.3, 189.3) * mm});
            skLineSegment(sketch, "E3.23.13.2", {"start": v(306, 179) * mm, "end": v(316.3, 179) * mm});
            skLineSegment(sketch, "E3.23.13.3", {"start": v(316.3, 179) * mm, "end": v(316.3, 189.3) * mm});
            skLineSegment(sketch, "E3.23.14.0", {"start": v(306, 191.7) * mm, "end": v(306, 202) * mm});
            skLineSegment(sketch, "E3.23.14.1", {"start": v(306, 202) * mm, "end": v(316.3, 202) * mm});
            skLineSegment(sketch, "E3.23.14.2", {"start": v(306, 191.7) * mm, "end": v(316.3, 191.7) * mm});
            skLineSegment(sketch, "E3.23.14.3", {"start": v(316.3, 191.7) * mm, "end": v(316.3, 202) * mm});
            skLineSegment(sketch, "E3.23.15.0", {"start": v(306, 204.4) * mm, "end": v(306, 214.7) * mm});
            skLineSegment(sketch, "E3.23.15.1", {"start": v(306, 214.7) * mm, "end": v(316.3, 214.7) * mm});
            skLineSegment(sketch, "E3.23.15.2", {"start": v(306, 204.4) * mm, "end": v(316.3, 204.4) * mm});
            skLineSegment(sketch, "E3.23.15.3", {"start": v(316.3, 204.4) * mm, "end": v(316.3, 214.7) * mm});
            skLineSegment(sketch, "E3.23.16.0", {"start": v(306, 217.1) * mm, "end": v(306, 227.4) * mm});
            skLineSegment(sketch, "E3.23.16.1", {"start": v(306, 227.4) * mm, "end": v(316.3, 227.4) * mm});
            skLineSegment(sketch, "E3.23.16.2", {"start": v(306, 217.1) * mm, "end": v(316.3, 217.1) * mm});
            skLineSegment(sketch, "E3.23.16.3", {"start": v(316.3, 217.1) * mm, "end": v(316.3, 227.4) * mm});
            skLineSegment(sketch, "E3.23.17.0", {"start": v(306, 229.8) * mm, "end": v(306, 240.1) * mm});
            skLineSegment(sketch, "E3.23.17.1", {"start": v(306, 240.1) * mm, "end": v(316.3, 240.1) * mm});
            skLineSegment(sketch, "E3.23.17.2", {"start": v(306, 229.8) * mm, "end": v(316.3, 229.8) * mm});
            skLineSegment(sketch, "E3.23.17.3", {"start": v(316.3, 229.8) * mm, "end": v(316.3, 240.1) * mm});
            skLineSegment(sketch, "E3.23.18.0", {"start": v(306, 242.5) * mm, "end": v(306, 252.8) * mm});
            skLineSegment(sketch, "E3.23.18.1", {"start": v(306, 252.8) * mm, "end": v(316.3, 252.8) * mm});
            skLineSegment(sketch, "E3.23.18.2", {"start": v(306, 242.5) * mm, "end": v(316.3, 242.5) * mm});
            skLineSegment(sketch, "E3.23.18.3", {"start": v(316.3, 242.5) * mm, "end": v(316.3, 252.8) * mm});
            skLineSegment(sketch, "E3.23.19.0", {"start": v(306, 255.2) * mm, "end": v(306, 265.5) * mm});
            skLineSegment(sketch, "E3.23.19.1", {"start": v(306, 265.5) * mm, "end": v(316.3, 265.5) * mm});
            skLineSegment(sketch, "E3.23.19.2", {"start": v(306, 255.2) * mm, "end": v(316.3, 255.2) * mm});
            skLineSegment(sketch, "E3.23.19.3", {"start": v(316.3, 255.2) * mm, "end": v(316.3, 265.5) * mm});
            skLineSegment(sketch, "E3.23.20.0", {"start": v(306, 267.9) * mm, "end": v(306, 278.2) * mm});
            skLineSegment(sketch, "E3.23.20.1", {"start": v(306, 278.2) * mm, "end": v(316.3, 278.2) * mm});
            skLineSegment(sketch, "E3.23.20.2", {"start": v(306, 267.9) * mm, "end": v(316.3, 267.9) * mm});
            skLineSegment(sketch, "E3.23.20.3", {"start": v(316.3, 267.9) * mm, "end": v(316.3, 278.2) * mm});
            skLineSegment(sketch, "E3.23.21.0", {"start": v(306, 280.6) * mm, "end": v(306, 290.9) * mm});
            skLineSegment(sketch, "E3.23.21.1", {"start": v(306, 290.9) * mm, "end": v(316.3, 290.9) * mm});
            skLineSegment(sketch, "E3.23.21.2", {"start": v(306, 280.6) * mm, "end": v(316.3, 280.6) * mm});
            skLineSegment(sketch, "E3.23.21.3", {"start": v(316.3, 280.6) * mm, "end": v(316.3, 290.9) * mm});
            skLineSegment(sketch, "E3.24.0.0", {"start": v(318.7, 13.9) * mm, "end": v(318.7, 24.2) * mm});
            skLineSegment(sketch, "E3.24.0.1", {"start": v(318.7, 24.2) * mm, "end": v(329, 24.2) * mm});
            skLineSegment(sketch, "E3.24.0.2", {"start": v(318.7, 13.9) * mm, "end": v(329, 13.9) * mm});
            skLineSegment(sketch, "E3.24.0.3", {"start": v(329, 13.9) * mm, "end": v(329, 24.2) * mm});
            skLineSegment(sketch, "E3.24.1.0", {"start": v(318.7, 26.6) * mm, "end": v(318.7, 36.9) * mm});
            skLineSegment(sketch, "E3.24.1.1", {"start": v(318.7, 36.9) * mm, "end": v(329, 36.9) * mm});
            skLineSegment(sketch, "E3.24.1.2", {"start": v(318.7, 26.6) * mm, "end": v(329, 26.6) * mm});
            skLineSegment(sketch, "E3.24.1.3", {"start": v(329, 26.6) * mm, "end": v(329, 36.9) * mm});
            skLineSegment(sketch, "E3.24.2.0", {"start": v(318.7, 39.3) * mm, "end": v(318.7, 49.6) * mm});
            skLineSegment(sketch, "E3.24.2.1", {"start": v(318.7, 49.6) * mm, "end": v(329, 49.6) * mm});
            skLineSegment(sketch, "E3.24.2.2", {"start": v(318.7, 39.3) * mm, "end": v(329, 39.3) * mm});
            skLineSegment(sketch, "E3.24.2.3", {"start": v(329, 39.3) * mm, "end": v(329, 49.6) * mm});
            skLineSegment(sketch, "E3.24.3.0", {"start": v(318.7, 52) * mm, "end": v(318.7, 62.3) * mm});
            skLineSegment(sketch, "E3.24.3.1", {"start": v(318.7, 62.3) * mm, "end": v(329, 62.3) * mm});
            skLineSegment(sketch, "E3.24.3.2", {"start": v(318.7, 52) * mm, "end": v(329, 52) * mm});
            skLineSegment(sketch, "E3.24.3.3", {"start": v(329, 52) * mm, "end": v(329, 62.3) * mm});
            skLineSegment(sketch, "E3.24.4.0", {"start": v(318.7, 64.7) * mm, "end": v(318.7, 75) * mm});
            skLineSegment(sketch, "E3.24.4.1", {"start": v(318.7, 75) * mm, "end": v(329, 75) * mm});
            skLineSegment(sketch, "E3.24.4.2", {"start": v(318.7, 64.7) * mm, "end": v(329, 64.7) * mm});
            skLineSegment(sketch, "E3.24.4.3", {"start": v(329, 64.7) * mm, "end": v(329, 75) * mm});
            skLineSegment(sketch, "E3.24.5.0", {"start": v(318.7, 77.4) * mm, "end": v(318.7, 87.7) * mm});
            skLineSegment(sketch, "E3.24.5.1", {"start": v(318.7, 87.7) * mm, "end": v(329, 87.7) * mm});
            skLineSegment(sketch, "E3.24.5.2", {"start": v(318.7, 77.4) * mm, "end": v(329, 77.4) * mm});
            skLineSegment(sketch, "E3.24.5.3", {"start": v(329, 77.4) * mm, "end": v(329, 87.7) * mm});
            skLineSegment(sketch, "E3.24.6.0", {"start": v(318.7, 90.1) * mm, "end": v(318.7, 100.4) * mm});
            skLineSegment(sketch, "E3.24.6.1", {"start": v(318.7, 100.4) * mm, "end": v(329, 100.4) * mm});
            skLineSegment(sketch, "E3.24.6.2", {"start": v(318.7, 90.1) * mm, "end": v(329, 90.1) * mm});
            skLineSegment(sketch, "E3.24.6.3", {"start": v(329, 90.1) * mm, "end": v(329, 100.4) * mm});
            skLineSegment(sketch, "E3.24.7.0", {"start": v(318.7, 102.8) * mm, "end": v(318.7, 113.1) * mm});
            skLineSegment(sketch, "E3.24.7.1", {"start": v(318.7, 113.1) * mm, "end": v(329, 113.1) * mm});
            skLineSegment(sketch, "E3.24.7.2", {"start": v(318.7, 102.8) * mm, "end": v(329, 102.8) * mm});
            skLineSegment(sketch, "E3.24.7.3", {"start": v(329, 102.8) * mm, "end": v(329, 113.1) * mm});
            skLineSegment(sketch, "E3.24.8.0", {"start": v(318.7, 115.5) * mm, "end": v(318.7, 125.8) * mm});
            skLineSegment(sketch, "E3.24.8.1", {"start": v(318.7, 125.8) * mm, "end": v(329, 125.8) * mm});
            skLineSegment(sketch, "E3.24.8.2", {"start": v(318.7, 115.5) * mm, "end": v(329, 115.5) * mm});
            skLineSegment(sketch, "E3.24.8.3", {"start": v(329, 115.5) * mm, "end": v(329, 125.8) * mm});
            skLineSegment(sketch, "E3.24.9.0", {"start": v(318.7, 128.2) * mm, "end": v(318.7, 138.5) * mm});
            skLineSegment(sketch, "E3.24.9.1", {"start": v(318.7, 138.5) * mm, "end": v(329, 138.5) * mm});
            skLineSegment(sketch, "E3.24.9.2", {"start": v(318.7, 128.2) * mm, "end": v(329, 128.2) * mm});
            skLineSegment(sketch, "E3.24.9.3", {"start": v(329, 128.2) * mm, "end": v(329, 138.5) * mm});
            skLineSegment(sketch, "E3.24.10.0", {"start": v(318.7, 140.9) * mm, "end": v(318.7, 151.2) * mm});
            skLineSegment(sketch, "E3.24.10.1", {"start": v(318.7, 151.2) * mm, "end": v(329, 151.2) * mm});
            skLineSegment(sketch, "E3.24.10.2", {"start": v(318.7, 140.9) * mm, "end": v(329, 140.9) * mm});
            skLineSegment(sketch, "E3.24.10.3", {"start": v(329, 140.9) * mm, "end": v(329, 151.2) * mm});
            skLineSegment(sketch, "E3.24.11.0", {"start": v(318.7, 153.6) * mm, "end": v(318.7, 163.9) * mm});
            skLineSegment(sketch, "E3.24.11.1", {"start": v(318.7, 163.9) * mm, "end": v(329, 163.9) * mm});
            skLineSegment(sketch, "E3.24.11.2", {"start": v(318.7, 153.6) * mm, "end": v(329, 153.6) * mm});
            skLineSegment(sketch, "E3.24.11.3", {"start": v(329, 153.6) * mm, "end": v(329, 163.9) * mm});
            skLineSegment(sketch, "E3.24.12.0", {"start": v(318.7, 166.3) * mm, "end": v(318.7, 176.6) * mm});
            skLineSegment(sketch, "E3.24.12.1", {"start": v(318.7, 176.6) * mm, "end": v(329, 176.6) * mm});
            skLineSegment(sketch, "E3.24.12.2", {"start": v(318.7, 166.3) * mm, "end": v(329, 166.3) * mm});
            skLineSegment(sketch, "E3.24.12.3", {"start": v(329, 166.3) * mm, "end": v(329, 176.6) * mm});
            skLineSegment(sketch, "E3.24.13.0", {"start": v(318.7, 179) * mm, "end": v(318.7, 189.3) * mm});
            skLineSegment(sketch, "E3.24.13.1", {"start": v(318.7, 189.3) * mm, "end": v(329, 189.3) * mm});
            skLineSegment(sketch, "E3.24.13.2", {"start": v(318.7, 179) * mm, "end": v(329, 179) * mm});
            skLineSegment(sketch, "E3.24.13.3", {"start": v(329, 179) * mm, "end": v(329, 189.3) * mm});
            skLineSegment(sketch, "E3.24.14.0", {"start": v(318.7, 191.7) * mm, "end": v(318.7, 202) * mm});
            skLineSegment(sketch, "E3.24.14.1", {"start": v(318.7, 202) * mm, "end": v(329, 202) * mm});
            skLineSegment(sketch, "E3.24.14.2", {"start": v(318.7, 191.7) * mm, "end": v(329, 191.7) * mm});
            skLineSegment(sketch, "E3.24.14.3", {"start": v(329, 191.7) * mm, "end": v(329, 202) * mm});
            skLineSegment(sketch, "E3.24.15.0", {"start": v(318.7, 204.4) * mm, "end": v(318.7, 214.7) * mm});
            skLineSegment(sketch, "E3.24.15.1", {"start": v(318.7, 214.7) * mm, "end": v(329, 214.7) * mm});
            skLineSegment(sketch, "E3.24.15.2", {"start": v(318.7, 204.4) * mm, "end": v(329, 204.4) * mm});
            skLineSegment(sketch, "E3.24.15.3", {"start": v(329, 204.4) * mm, "end": v(329, 214.7) * mm});
            skLineSegment(sketch, "E3.24.16.0", {"start": v(318.7, 217.1) * mm, "end": v(318.7, 227.4) * mm});
            skLineSegment(sketch, "E3.24.16.1", {"start": v(318.7, 227.4) * mm, "end": v(329, 227.4) * mm});
            skLineSegment(sketch, "E3.24.16.2", {"start": v(318.7, 217.1) * mm, "end": v(329, 217.1) * mm});
            skLineSegment(sketch, "E3.24.16.3", {"start": v(329, 217.1) * mm, "end": v(329, 227.4) * mm});
            skLineSegment(sketch, "E3.24.17.0", {"start": v(318.7, 229.8) * mm, "end": v(318.7, 240.1) * mm});
            skLineSegment(sketch, "E3.24.17.1", {"start": v(318.7, 240.1) * mm, "end": v(329, 240.1) * mm});
            skLineSegment(sketch, "E3.24.17.2", {"start": v(318.7, 229.8) * mm, "end": v(329, 229.8) * mm});
            skLineSegment(sketch, "E3.24.17.3", {"start": v(329, 229.8) * mm, "end": v(329, 240.1) * mm});
            skLineSegment(sketch, "E3.24.18.0", {"start": v(318.7, 242.5) * mm, "end": v(318.7, 252.8) * mm});
            skLineSegment(sketch, "E3.24.18.1", {"start": v(318.7, 252.8) * mm, "end": v(329, 252.8) * mm});
            skLineSegment(sketch, "E3.24.18.2", {"start": v(318.7, 242.5) * mm, "end": v(329, 242.5) * mm});
            skLineSegment(sketch, "E3.24.18.3", {"start": v(329, 242.5) * mm, "end": v(329, 252.8) * mm});
            skLineSegment(sketch, "E3.24.19.0", {"start": v(318.7, 255.2) * mm, "end": v(318.7, 265.5) * mm});
            skLineSegment(sketch, "E3.24.19.1", {"start": v(318.7, 265.5) * mm, "end": v(329, 265.5) * mm});
            skLineSegment(sketch, "E3.24.19.2", {"start": v(318.7, 255.2) * mm, "end": v(329, 255.2) * mm});
            skLineSegment(sketch, "E3.24.19.3", {"start": v(329, 255.2) * mm, "end": v(329, 265.5) * mm});
            skLineSegment(sketch, "E3.24.20.0", {"start": v(318.7, 267.9) * mm, "end": v(318.7, 278.2) * mm});
            skLineSegment(sketch, "E3.24.20.1", {"start": v(318.7, 278.2) * mm, "end": v(329, 278.2) * mm});
            skLineSegment(sketch, "E3.24.20.2", {"start": v(318.7, 267.9) * mm, "end": v(329, 267.9) * mm});
            skLineSegment(sketch, "E3.24.20.3", {"start": v(329, 267.9) * mm, "end": v(329, 278.2) * mm});
            skLineSegment(sketch, "E3.24.21.0", {"start": v(318.7, 280.6) * mm, "end": v(318.7, 290.9) * mm});
            skLineSegment(sketch, "E3.24.21.1", {"start": v(318.7, 290.9) * mm, "end": v(329, 290.9) * mm});
            skLineSegment(sketch, "E3.24.21.2", {"start": v(318.7, 280.6) * mm, "end": v(329, 280.6) * mm});
            skLineSegment(sketch, "E3.24.21.3", {"start": v(329, 280.6) * mm, "end": v(329, 290.9) * mm});
            skLineSegment(sketch, "E3.25.0.0", {"start": v(331.4, 13.9) * mm, "end": v(331.4, 24.2) * mm});
            skLineSegment(sketch, "E3.25.0.1", {"start": v(331.4, 24.2) * mm, "end": v(341.7, 24.2) * mm});
            skLineSegment(sketch, "E3.25.0.2", {"start": v(331.4, 13.9) * mm, "end": v(341.7, 13.9) * mm});
            skLineSegment(sketch, "E3.25.0.3", {"start": v(341.7, 13.9) * mm, "end": v(341.7, 24.2) * mm});
            skLineSegment(sketch, "E3.25.1.0", {"start": v(331.4, 26.6) * mm, "end": v(331.4, 36.9) * mm});
            skLineSegment(sketch, "E3.25.1.1", {"start": v(331.4, 36.9) * mm, "end": v(341.7, 36.9) * mm});
            skLineSegment(sketch, "E3.25.1.2", {"start": v(331.4, 26.6) * mm, "end": v(341.7, 26.6) * mm});
            skLineSegment(sketch, "E3.25.1.3", {"start": v(341.7, 26.6) * mm, "end": v(341.7, 36.9) * mm});
            skLineSegment(sketch, "E3.25.2.0", {"start": v(331.4, 39.3) * mm, "end": v(331.4, 49.6) * mm});
            skLineSegment(sketch, "E3.25.2.1", {"start": v(331.4, 49.6) * mm, "end": v(341.7, 49.6) * mm});
            skLineSegment(sketch, "E3.25.2.2", {"start": v(331.4, 39.3) * mm, "end": v(341.7, 39.3) * mm});
            skLineSegment(sketch, "E3.25.2.3", {"start": v(341.7, 39.3) * mm, "end": v(341.7, 49.6) * mm});
            skLineSegment(sketch, "E3.25.3.0", {"start": v(331.4, 52) * mm, "end": v(331.4, 62.3) * mm});
            skLineSegment(sketch, "E3.25.3.1", {"start": v(331.4, 62.3) * mm, "end": v(341.7, 62.3) * mm});
            skLineSegment(sketch, "E3.25.3.2", {"start": v(331.4, 52) * mm, "end": v(341.7, 52) * mm});
            skLineSegment(sketch, "E3.25.3.3", {"start": v(341.7, 52) * mm, "end": v(341.7, 62.3) * mm});
            skLineSegment(sketch, "E3.25.4.0", {"start": v(331.4, 64.7) * mm, "end": v(331.4, 75) * mm});
            skLineSegment(sketch, "E3.25.4.1", {"start": v(331.4, 75) * mm, "end": v(341.7, 75) * mm});
            skLineSegment(sketch, "E3.25.4.2", {"start": v(331.4, 64.7) * mm, "end": v(341.7, 64.7) * mm});
            skLineSegment(sketch, "E3.25.4.3", {"start": v(341.7, 64.7) * mm, "end": v(341.7, 75) * mm});
            skLineSegment(sketch, "E3.25.5.0", {"start": v(331.4, 77.4) * mm, "end": v(331.4, 87.7) * mm});
            skLineSegment(sketch, "E3.25.5.1", {"start": v(331.4, 87.7) * mm, "end": v(341.7, 87.7) * mm});
            skLineSegment(sketch, "E3.25.5.2", {"start": v(331.4, 77.4) * mm, "end": v(341.7, 77.4) * mm});
            skLineSegment(sketch, "E3.25.5.3", {"start": v(341.7, 77.4) * mm, "end": v(341.7, 87.7) * mm});
            skLineSegment(sketch, "E3.25.6.0", {"start": v(331.4, 90.1) * mm, "end": v(331.4, 100.4) * mm});
            skLineSegment(sketch, "E3.25.6.1", {"start": v(331.4, 100.4) * mm, "end": v(341.7, 100.4) * mm});
            skLineSegment(sketch, "E3.25.6.2", {"start": v(331.4, 90.1) * mm, "end": v(341.7, 90.1) * mm});
            skLineSegment(sketch, "E3.25.6.3", {"start": v(341.7, 90.1) * mm, "end": v(341.7, 100.4) * mm});
            skLineSegment(sketch, "E3.25.7.0", {"start": v(331.4, 102.8) * mm, "end": v(331.4, 113.1) * mm});
            skLineSegment(sketch, "E3.25.7.1", {"start": v(331.4, 113.1) * mm, "end": v(341.7, 113.1) * mm});
            skLineSegment(sketch, "E3.25.7.2", {"start": v(331.4, 102.8) * mm, "end": v(341.7, 102.8) * mm});
            skLineSegment(sketch, "E3.25.7.3", {"start": v(341.7, 102.8) * mm, "end": v(341.7, 113.1) * mm});
            skLineSegment(sketch, "E3.25.8.0", {"start": v(331.4, 115.5) * mm, "end": v(331.4, 125.8) * mm});
            skLineSegment(sketch, "E3.25.8.1", {"start": v(331.4, 125.8) * mm, "end": v(341.7, 125.8) * mm});
            skLineSegment(sketch, "E3.25.8.2", {"start": v(331.4, 115.5) * mm, "end": v(341.7, 115.5) * mm});
            skLineSegment(sketch, "E3.25.8.3", {"start": v(341.7, 115.5) * mm, "end": v(341.7, 125.8) * mm});
            skLineSegment(sketch, "E3.25.9.0", {"start": v(331.4, 128.2) * mm, "end": v(331.4, 138.5) * mm});
            skLineSegment(sketch, "E3.25.9.1", {"start": v(331.4, 138.5) * mm, "end": v(341.7, 138.5) * mm});
            skLineSegment(sketch, "E3.25.9.2", {"start": v(331.4, 128.2) * mm, "end": v(341.7, 128.2) * mm});
            skLineSegment(sketch, "E3.25.9.3", {"start": v(341.7, 128.2) * mm, "end": v(341.7, 138.5) * mm});
            skLineSegment(sketch, "E3.25.10.0", {"start": v(331.4, 140.9) * mm, "end": v(331.4, 151.2) * mm});
            skLineSegment(sketch, "E3.25.10.1", {"start": v(331.4, 151.2) * mm, "end": v(341.7, 151.2) * mm});
            skLineSegment(sketch, "E3.25.10.2", {"start": v(331.4, 140.9) * mm, "end": v(341.7, 140.9) * mm});
            skLineSegment(sketch, "E3.25.10.3", {"start": v(341.7, 140.9) * mm, "end": v(341.7, 151.2) * mm});
            skLineSegment(sketch, "E3.25.11.0", {"start": v(331.4, 153.6) * mm, "end": v(331.4, 163.9) * mm});
            skLineSegment(sketch, "E3.25.11.1", {"start": v(331.4, 163.9) * mm, "end": v(341.7, 163.9) * mm});
            skLineSegment(sketch, "E3.25.11.2", {"start": v(331.4, 153.6) * mm, "end": v(341.7, 153.6) * mm});
            skLineSegment(sketch, "E3.25.11.3", {"start": v(341.7, 153.6) * mm, "end": v(341.7, 163.9) * mm});
            skLineSegment(sketch, "E3.25.12.0", {"start": v(331.4, 166.3) * mm, "end": v(331.4, 176.6) * mm});
            skLineSegment(sketch, "E3.25.12.1", {"start": v(331.4, 176.6) * mm, "end": v(341.7, 176.6) * mm});
            skLineSegment(sketch, "E3.25.12.2", {"start": v(331.4, 166.3) * mm, "end": v(341.7, 166.3) * mm});
            skLineSegment(sketch, "E3.25.12.3", {"start": v(341.7, 166.3) * mm, "end": v(341.7, 176.6) * mm});
            skLineSegment(sketch, "E3.25.13.0", {"start": v(331.4, 179) * mm, "end": v(331.4, 189.3) * mm});
            skLineSegment(sketch, "E3.25.13.1", {"start": v(331.4, 189.3) * mm, "end": v(341.7, 189.3) * mm});
            skLineSegment(sketch, "E3.25.13.2", {"start": v(331.4, 179) * mm, "end": v(341.7, 179) * mm});
            skLineSegment(sketch, "E3.25.13.3", {"start": v(341.7, 179) * mm, "end": v(341.7, 189.3) * mm});
            skLineSegment(sketch, "E3.25.14.0", {"start": v(331.4, 191.7) * mm, "end": v(331.4, 202) * mm});
            skLineSegment(sketch, "E3.25.14.1", {"start": v(331.4, 202) * mm, "end": v(341.7, 202) * mm});
            skLineSegment(sketch, "E3.25.14.2", {"start": v(331.4, 191.7) * mm, "end": v(341.7, 191.7) * mm});
            skLineSegment(sketch, "E3.25.14.3", {"start": v(341.7, 191.7) * mm, "end": v(341.7, 202) * mm});
            skLineSegment(sketch, "E3.25.15.0", {"start": v(331.4, 204.4) * mm, "end": v(331.4, 214.7) * mm});
            skLineSegment(sketch, "E3.25.15.1", {"start": v(331.4, 214.7) * mm, "end": v(341.7, 214.7) * mm});
            skLineSegment(sketch, "E3.25.15.2", {"start": v(331.4, 204.4) * mm, "end": v(341.7, 204.4) * mm});
            skLineSegment(sketch, "E3.25.15.3", {"start": v(341.7, 204.4) * mm, "end": v(341.7, 214.7) * mm});
            skLineSegment(sketch, "E3.25.16.0", {"start": v(331.4, 217.1) * mm, "end": v(331.4, 227.4) * mm});
            skLineSegment(sketch, "E3.25.16.1", {"start": v(331.4, 227.4) * mm, "end": v(341.7, 227.4) * mm});
            skLineSegment(sketch, "E3.25.16.2", {"start": v(331.4, 217.1) * mm, "end": v(341.7, 217.1) * mm});
            skLineSegment(sketch, "E3.25.16.3", {"start": v(341.7, 217.1) * mm, "end": v(341.7, 227.4) * mm});
            skLineSegment(sketch, "E3.25.17.0", {"start": v(331.4, 229.8) * mm, "end": v(331.4, 240.1) * mm});
            skLineSegment(sketch, "E3.25.17.1", {"start": v(331.4, 240.1) * mm, "end": v(341.7, 240.1) * mm});
            skLineSegment(sketch, "E3.25.17.2", {"start": v(331.4, 229.8) * mm, "end": v(341.7, 229.8) * mm});
            skLineSegment(sketch, "E3.25.17.3", {"start": v(341.7, 229.8) * mm, "end": v(341.7, 240.1) * mm});
            skLineSegment(sketch, "E3.25.18.0", {"start": v(331.4, 242.5) * mm, "end": v(331.4, 252.8) * mm});
            skLineSegment(sketch, "E3.25.18.1", {"start": v(331.4, 252.8) * mm, "end": v(341.7, 252.8) * mm});
            skLineSegment(sketch, "E3.25.18.2", {"start": v(331.4, 242.5) * mm, "end": v(341.7, 242.5) * mm});
            skLineSegment(sketch, "E3.25.18.3", {"start": v(341.7, 242.5) * mm, "end": v(341.7, 252.8) * mm});
            skLineSegment(sketch, "E3.25.19.0", {"start": v(331.4, 255.2) * mm, "end": v(331.4, 265.5) * mm});
            skLineSegment(sketch, "E3.25.19.1", {"start": v(331.4, 265.5) * mm, "end": v(341.7, 265.5) * mm});
            skLineSegment(sketch, "E3.25.19.2", {"start": v(331.4, 255.2) * mm, "end": v(341.7, 255.2) * mm});
            skLineSegment(sketch, "E3.25.19.3", {"start": v(341.7, 255.2) * mm, "end": v(341.7, 265.5) * mm});
            skLineSegment(sketch, "E3.25.20.0", {"start": v(331.4, 267.9) * mm, "end": v(331.4, 278.2) * mm});
            skLineSegment(sketch, "E3.25.20.1", {"start": v(331.4, 278.2) * mm, "end": v(341.7, 278.2) * mm});
            skLineSegment(sketch, "E3.25.20.2", {"start": v(331.4, 267.9) * mm, "end": v(341.7, 267.9) * mm});
            skLineSegment(sketch, "E3.25.20.3", {"start": v(341.7, 267.9) * mm, "end": v(341.7, 278.2) * mm});
            skLineSegment(sketch, "E3.25.21.0", {"start": v(331.4, 280.6) * mm, "end": v(331.4, 290.9) * mm});
            skLineSegment(sketch, "E3.25.21.1", {"start": v(331.4, 290.9) * mm, "end": v(341.7, 290.9) * mm});
            skLineSegment(sketch, "E3.25.21.2", {"start": v(331.4, 280.6) * mm, "end": v(341.7, 280.6) * mm});
            skLineSegment(sketch, "E3.25.21.3", {"start": v(341.7, 280.6) * mm, "end": v(341.7, 290.9) * mm});
            skLineSegment(sketch, "E3.26.0.0", {"start": v(344.1, 13.9) * mm, "end": v(344.1, 24.2) * mm});
            skLineSegment(sketch, "E3.26.0.1", {"start": v(344.1, 24.2) * mm, "end": v(354.4, 24.2) * mm});
            skLineSegment(sketch, "E3.26.0.2", {"start": v(344.1, 13.9) * mm, "end": v(354.4, 13.9) * mm});
            skLineSegment(sketch, "E3.26.0.3", {"start": v(354.4, 13.9) * mm, "end": v(354.4, 24.2) * mm});
            skLineSegment(sketch, "E3.26.1.0", {"start": v(344.1, 26.6) * mm, "end": v(344.1, 36.9) * mm});
            skLineSegment(sketch, "E3.26.1.1", {"start": v(344.1, 36.9) * mm, "end": v(354.4, 36.9) * mm});
            skLineSegment(sketch, "E3.26.1.2", {"start": v(344.1, 26.6) * mm, "end": v(354.4, 26.6) * mm});
            skLineSegment(sketch, "E3.26.1.3", {"start": v(354.4, 26.6) * mm, "end": v(354.4, 36.9) * mm});
            skLineSegment(sketch, "E3.26.2.0", {"start": v(344.1, 39.3) * mm, "end": v(344.1, 49.6) * mm});
            skLineSegment(sketch, "E3.26.2.1", {"start": v(344.1, 49.6) * mm, "end": v(354.4, 49.6) * mm});
            skLineSegment(sketch, "E3.26.2.2", {"start": v(344.1, 39.3) * mm, "end": v(354.4, 39.3) * mm});
            skLineSegment(sketch, "E3.26.2.3", {"start": v(354.4, 39.3) * mm, "end": v(354.4, 49.6) * mm});
            skLineSegment(sketch, "E3.26.3.0", {"start": v(344.1, 52) * mm, "end": v(344.1, 62.3) * mm});
            skLineSegment(sketch, "E3.26.3.1", {"start": v(344.1, 62.3) * mm, "end": v(354.4, 62.3) * mm});
            skLineSegment(sketch, "E3.26.3.2", {"start": v(344.1, 52) * mm, "end": v(354.4, 52) * mm});
            skLineSegment(sketch, "E3.26.3.3", {"start": v(354.4, 52) * mm, "end": v(354.4, 62.3) * mm});
            skLineSegment(sketch, "E3.26.4.0", {"start": v(344.1, 64.7) * mm, "end": v(344.1, 75) * mm});
            skLineSegment(sketch, "E3.26.4.1", {"start": v(344.1, 75) * mm, "end": v(354.4, 75) * mm});
            skLineSegment(sketch, "E3.26.4.2", {"start": v(344.1, 64.7) * mm, "end": v(354.4, 64.7) * mm});
            skLineSegment(sketch, "E3.26.4.3", {"start": v(354.4, 64.7) * mm, "end": v(354.4, 75) * mm});
            skLineSegment(sketch, "E3.26.5.0", {"start": v(344.1, 77.4) * mm, "end": v(344.1, 87.7) * mm});
            skLineSegment(sketch, "E3.26.5.1", {"start": v(344.1, 87.7) * mm, "end": v(354.4, 87.7) * mm});
            skLineSegment(sketch, "E3.26.5.2", {"start": v(344.1, 77.4) * mm, "end": v(354.4, 77.4) * mm});
            skLineSegment(sketch, "E3.26.5.3", {"start": v(354.4, 77.4) * mm, "end": v(354.4, 87.7) * mm});
            skLineSegment(sketch, "E3.26.6.0", {"start": v(344.1, 90.1) * mm, "end": v(344.1, 100.4) * mm});
            skLineSegment(sketch, "E3.26.6.1", {"start": v(344.1, 100.4) * mm, "end": v(354.4, 100.4) * mm});
            skLineSegment(sketch, "E3.26.6.2", {"start": v(344.1, 90.1) * mm, "end": v(354.4, 90.1) * mm});
            skLineSegment(sketch, "E3.26.6.3", {"start": v(354.4, 90.1) * mm, "end": v(354.4, 100.4) * mm});
            skLineSegment(sketch, "E3.26.7.0", {"start": v(344.1, 102.8) * mm, "end": v(344.1, 113.1) * mm});
            skLineSegment(sketch, "E3.26.7.1", {"start": v(344.1, 113.1) * mm, "end": v(354.4, 113.1) * mm});
            skLineSegment(sketch, "E3.26.7.2", {"start": v(344.1, 102.8) * mm, "end": v(354.4, 102.8) * mm});
            skLineSegment(sketch, "E3.26.7.3", {"start": v(354.4, 102.8) * mm, "end": v(354.4, 113.1) * mm});
            skLineSegment(sketch, "E3.26.8.0", {"start": v(344.1, 115.5) * mm, "end": v(344.1, 125.8) * mm});
            skLineSegment(sketch, "E3.26.8.1", {"start": v(344.1, 125.8) * mm, "end": v(354.4, 125.8) * mm});
            skLineSegment(sketch, "E3.26.8.2", {"start": v(344.1, 115.5) * mm, "end": v(354.4, 115.5) * mm});
            skLineSegment(sketch, "E3.26.8.3", {"start": v(354.4, 115.5) * mm, "end": v(354.4, 125.8) * mm});
            skLineSegment(sketch, "E3.26.9.0", {"start": v(344.1, 128.2) * mm, "end": v(344.1, 138.5) * mm});
            skLineSegment(sketch, "E3.26.9.1", {"start": v(344.1, 138.5) * mm, "end": v(354.4, 138.5) * mm});
            skLineSegment(sketch, "E3.26.9.2", {"start": v(344.1, 128.2) * mm, "end": v(354.4, 128.2) * mm});
            skLineSegment(sketch, "E3.26.9.3", {"start": v(354.4, 128.2) * mm, "end": v(354.4, 138.5) * mm});
            skLineSegment(sketch, "E3.26.10.0", {"start": v(344.1, 140.9) * mm, "end": v(344.1, 151.2) * mm});
            skLineSegment(sketch, "E3.26.10.1", {"start": v(344.1, 151.2) * mm, "end": v(354.4, 151.2) * mm});
            skLineSegment(sketch, "E3.26.10.2", {"start": v(344.1, 140.9) * mm, "end": v(354.4, 140.9) * mm});
            skLineSegment(sketch, "E3.26.10.3", {"start": v(354.4, 140.9) * mm, "end": v(354.4, 151.2) * mm});
            skLineSegment(sketch, "E3.26.11.0", {"start": v(344.1, 153.6) * mm, "end": v(344.1, 163.9) * mm});
            skLineSegment(sketch, "E3.26.11.1", {"start": v(344.1, 163.9) * mm, "end": v(354.4, 163.9) * mm});
            skLineSegment(sketch, "E3.26.11.2", {"start": v(344.1, 153.6) * mm, "end": v(354.4, 153.6) * mm});
            skLineSegment(sketch, "E3.26.11.3", {"start": v(354.4, 153.6) * mm, "end": v(354.4, 163.9) * mm});
            skLineSegment(sketch, "E3.26.12.0", {"start": v(344.1, 166.3) * mm, "end": v(344.1, 176.6) * mm});
            skLineSegment(sketch, "E3.26.12.1", {"start": v(344.1, 176.6) * mm, "end": v(354.4, 176.6) * mm});
            skLineSegment(sketch, "E3.26.12.2", {"start": v(344.1, 166.3) * mm, "end": v(354.4, 166.3) * mm});
            skLineSegment(sketch, "E3.26.12.3", {"start": v(354.4, 166.3) * mm, "end": v(354.4, 176.6) * mm});
            skLineSegment(sketch, "E3.26.13.0", {"start": v(344.1, 179) * mm, "end": v(344.1, 189.3) * mm});
            skLineSegment(sketch, "E3.26.13.1", {"start": v(344.1, 189.3) * mm, "end": v(354.4, 189.3) * mm});
            skLineSegment(sketch, "E3.26.13.2", {"start": v(344.1, 179) * mm, "end": v(354.4, 179) * mm});
            skLineSegment(sketch, "E3.26.13.3", {"start": v(354.4, 179) * mm, "end": v(354.4, 189.3) * mm});
            skLineSegment(sketch, "E3.26.14.0", {"start": v(344.1, 191.7) * mm, "end": v(344.1, 202) * mm});
            skLineSegment(sketch, "E3.26.14.1", {"start": v(344.1, 202) * mm, "end": v(354.4, 202) * mm});
            skLineSegment(sketch, "E3.26.14.2", {"start": v(344.1, 191.7) * mm, "end": v(354.4, 191.7) * mm});
            skLineSegment(sketch, "E3.26.14.3", {"start": v(354.4, 191.7) * mm, "end": v(354.4, 202) * mm});
            skLineSegment(sketch, "E3.26.15.0", {"start": v(344.1, 204.4) * mm, "end": v(344.1, 214.7) * mm});
            skLineSegment(sketch, "E3.26.15.1", {"start": v(344.1, 214.7) * mm, "end": v(354.4, 214.7) * mm});
            skLineSegment(sketch, "E3.26.15.2", {"start": v(344.1, 204.4) * mm, "end": v(354.4, 204.4) * mm});
            skLineSegment(sketch, "E3.26.15.3", {"start": v(354.4, 204.4) * mm, "end": v(354.4, 214.7) * mm});
            skLineSegment(sketch, "E3.26.16.0", {"start": v(344.1, 217.1) * mm, "end": v(344.1, 227.4) * mm});
            skLineSegment(sketch, "E3.26.16.1", {"start": v(344.1, 227.4) * mm, "end": v(354.4, 227.4) * mm});
            skLineSegment(sketch, "E3.26.16.2", {"start": v(344.1, 217.1) * mm, "end": v(354.4, 217.1) * mm});
            skLineSegment(sketch, "E3.26.16.3", {"start": v(354.4, 217.1) * mm, "end": v(354.4, 227.4) * mm});
            skLineSegment(sketch, "E3.26.17.0", {"start": v(344.1, 229.8) * mm, "end": v(344.1, 240.1) * mm});
            skLineSegment(sketch, "E3.26.17.1", {"start": v(344.1, 240.1) * mm, "end": v(354.4, 240.1) * mm});
            skLineSegment(sketch, "E3.26.17.2", {"start": v(344.1, 229.8) * mm, "end": v(354.4, 229.8) * mm});
            skLineSegment(sketch, "E3.26.17.3", {"start": v(354.4, 229.8) * mm, "end": v(354.4, 240.1) * mm});
            skLineSegment(sketch, "E3.26.18.0", {"start": v(344.1, 242.5) * mm, "end": v(344.1, 252.8) * mm});
            skLineSegment(sketch, "E3.26.18.1", {"start": v(344.1, 252.8) * mm, "end": v(354.4, 252.8) * mm});
            skLineSegment(sketch, "E3.26.18.2", {"start": v(344.1, 242.5) * mm, "end": v(354.4, 242.5) * mm});
            skLineSegment(sketch, "E3.26.18.3", {"start": v(354.4, 242.5) * mm, "end": v(354.4, 252.8) * mm});
            skLineSegment(sketch, "E3.26.19.0", {"start": v(344.1, 255.2) * mm, "end": v(344.1, 265.5) * mm});
            skLineSegment(sketch, "E3.26.19.1", {"start": v(344.1, 265.5) * mm, "end": v(354.4, 265.5) * mm});
            skLineSegment(sketch, "E3.26.19.2", {"start": v(344.1, 255.2) * mm, "end": v(354.4, 255.2) * mm});
            skLineSegment(sketch, "E3.26.19.3", {"start": v(354.4, 255.2) * mm, "end": v(354.4, 265.5) * mm});
            skLineSegment(sketch, "E3.26.20.0", {"start": v(344.1, 267.9) * mm, "end": v(344.1, 278.2) * mm});
            skLineSegment(sketch, "E3.26.20.1", {"start": v(344.1, 278.2) * mm, "end": v(354.4, 278.2) * mm});
            skLineSegment(sketch, "E3.26.20.2", {"start": v(344.1, 267.9) * mm, "end": v(354.4, 267.9) * mm});
            skLineSegment(sketch, "E3.26.20.3", {"start": v(354.4, 267.9) * mm, "end": v(354.4, 278.2) * mm});
            skLineSegment(sketch, "E3.26.21.0", {"start": v(344.1, 280.6) * mm, "end": v(344.1, 290.9) * mm});
            skLineSegment(sketch, "E3.26.21.1", {"start": v(344.1, 290.9) * mm, "end": v(354.4, 290.9) * mm});
            skLineSegment(sketch, "E3.26.21.2", {"start": v(344.1, 280.6) * mm, "end": v(354.4, 280.6) * mm});
            skLineSegment(sketch, "E3.26.21.3", {"start": v(354.4, 280.6) * mm, "end": v(354.4, 290.9) * mm});
            skLineSegment(sketch, "E3.27.0.0", {"start": v(356.8, 13.9) * mm, "end": v(356.8, 24.2) * mm});
            skLineSegment(sketch, "E3.27.0.1", {"start": v(356.8, 24.2) * mm, "end": v(367.1, 24.2) * mm});
            skLineSegment(sketch, "E3.27.0.2", {"start": v(356.8, 13.9) * mm, "end": v(367.1, 13.9) * mm});
            skLineSegment(sketch, "E3.27.0.3", {"start": v(367.1, 13.9) * mm, "end": v(367.1, 24.2) * mm});
            skLineSegment(sketch, "E3.27.1.0", {"start": v(356.8, 26.6) * mm, "end": v(356.8, 36.9) * mm});
            skLineSegment(sketch, "E3.27.1.1", {"start": v(356.8, 36.9) * mm, "end": v(367.1, 36.9) * mm});
            skLineSegment(sketch, "E3.27.1.2", {"start": v(356.8, 26.6) * mm, "end": v(367.1, 26.6) * mm});
            skLineSegment(sketch, "E3.27.1.3", {"start": v(367.1, 26.6) * mm, "end": v(367.1, 36.9) * mm});
            skLineSegment(sketch, "E3.27.2.0", {"start": v(356.8, 39.3) * mm, "end": v(356.8, 49.6) * mm});
            skLineSegment(sketch, "E3.27.2.1", {"start": v(356.8, 49.6) * mm, "end": v(367.1, 49.6) * mm});
            skLineSegment(sketch, "E3.27.2.2", {"start": v(356.8, 39.3) * mm, "end": v(367.1, 39.3) * mm});
            skLineSegment(sketch, "E3.27.2.3", {"start": v(367.1, 39.3) * mm, "end": v(367.1, 49.6) * mm});
            skLineSegment(sketch, "E3.27.3.0", {"start": v(356.8, 52) * mm, "end": v(356.8, 62.3) * mm});
            skLineSegment(sketch, "E3.27.3.1", {"start": v(356.8, 62.3) * mm, "end": v(367.1, 62.3) * mm});
            skLineSegment(sketch, "E3.27.3.2", {"start": v(356.8, 52) * mm, "end": v(367.1, 52) * mm});
            skLineSegment(sketch, "E3.27.3.3", {"start": v(367.1, 52) * mm, "end": v(367.1, 62.3) * mm});
            skLineSegment(sketch, "E3.27.4.0", {"start": v(356.8, 64.7) * mm, "end": v(356.8, 75) * mm});
            skLineSegment(sketch, "E3.27.4.1", {"start": v(356.8, 75) * mm, "end": v(367.1, 75) * mm});
            skLineSegment(sketch, "E3.27.4.2", {"start": v(356.8, 64.7) * mm, "end": v(367.1, 64.7) * mm});
            skLineSegment(sketch, "E3.27.4.3", {"start": v(367.1, 64.7) * mm, "end": v(367.1, 75) * mm});
            skLineSegment(sketch, "E3.27.5.0", {"start": v(356.8, 77.4) * mm, "end": v(356.8, 87.7) * mm});
            skLineSegment(sketch, "E3.27.5.1", {"start": v(356.8, 87.7) * mm, "end": v(367.1, 87.7) * mm});
            skLineSegment(sketch, "E3.27.5.2", {"start": v(356.8, 77.4) * mm, "end": v(367.1, 77.4) * mm});
            skLineSegment(sketch, "E3.27.5.3", {"start": v(367.1, 77.4) * mm, "end": v(367.1, 87.7) * mm});
            skLineSegment(sketch, "E3.27.6.0", {"start": v(356.8, 90.1) * mm, "end": v(356.8, 100.4) * mm});
            skLineSegment(sketch, "E3.27.6.1", {"start": v(356.8, 100.4) * mm, "end": v(367.1, 100.4) * mm});
            skLineSegment(sketch, "E3.27.6.2", {"start": v(356.8, 90.1) * mm, "end": v(367.1, 90.1) * mm});
            skLineSegment(sketch, "E3.27.6.3", {"start": v(367.1, 90.1) * mm, "end": v(367.1, 100.4) * mm});
            skLineSegment(sketch, "E3.27.7.0", {"start": v(356.8, 102.8) * mm, "end": v(356.8, 113.1) * mm});
            skLineSegment(sketch, "E3.27.7.1", {"start": v(356.8, 113.1) * mm, "end": v(367.1, 113.1) * mm});
            skLineSegment(sketch, "E3.27.7.2", {"start": v(356.8, 102.8) * mm, "end": v(367.1, 102.8) * mm});
            skLineSegment(sketch, "E3.27.7.3", {"start": v(367.1, 102.8) * mm, "end": v(367.1, 113.1) * mm});
            skLineSegment(sketch, "E3.27.8.0", {"start": v(356.8, 115.5) * mm, "end": v(356.8, 125.8) * mm});
            skLineSegment(sketch, "E3.27.8.1", {"start": v(356.8, 125.8) * mm, "end": v(367.1, 125.8) * mm});
            skLineSegment(sketch, "E3.27.8.2", {"start": v(356.8, 115.5) * mm, "end": v(367.1, 115.5) * mm});
            skLineSegment(sketch, "E3.27.8.3", {"start": v(367.1, 115.5) * mm, "end": v(367.1, 125.8) * mm});
            skLineSegment(sketch, "E3.27.9.0", {"start": v(356.8, 128.2) * mm, "end": v(356.8, 138.5) * mm});
            skLineSegment(sketch, "E3.27.9.1", {"start": v(356.8, 138.5) * mm, "end": v(367.1, 138.5) * mm});
            skLineSegment(sketch, "E3.27.9.2", {"start": v(356.8, 128.2) * mm, "end": v(367.1, 128.2) * mm});
            skLineSegment(sketch, "E3.27.9.3", {"start": v(367.1, 128.2) * mm, "end": v(367.1, 138.5) * mm});
            skLineSegment(sketch, "E3.27.10.0", {"start": v(356.8, 140.9) * mm, "end": v(356.8, 151.2) * mm});
            skLineSegment(sketch, "E3.27.10.1", {"start": v(356.8, 151.2) * mm, "end": v(367.1, 151.2) * mm});
            skLineSegment(sketch, "E3.27.10.2", {"start": v(356.8, 140.9) * mm, "end": v(367.1, 140.9) * mm});
            skLineSegment(sketch, "E3.27.10.3", {"start": v(367.1, 140.9) * mm, "end": v(367.1, 151.2) * mm});
            skLineSegment(sketch, "E3.27.11.0", {"start": v(356.8, 153.6) * mm, "end": v(356.8, 163.9) * mm});
            skLineSegment(sketch, "E3.27.11.1", {"start": v(356.8, 163.9) * mm, "end": v(367.1, 163.9) * mm});
            skLineSegment(sketch, "E3.27.11.2", {"start": v(356.8, 153.6) * mm, "end": v(367.1, 153.6) * mm});
            skLineSegment(sketch, "E3.27.11.3", {"start": v(367.1, 153.6) * mm, "end": v(367.1, 163.9) * mm});
            skLineSegment(sketch, "E3.27.12.0", {"start": v(356.8, 166.3) * mm, "end": v(356.8, 176.6) * mm});
            skLineSegment(sketch, "E3.27.12.1", {"start": v(356.8, 176.6) * mm, "end": v(367.1, 176.6) * mm});
            skLineSegment(sketch, "E3.27.12.2", {"start": v(356.8, 166.3) * mm, "end": v(367.1, 166.3) * mm});
            skLineSegment(sketch, "E3.27.12.3", {"start": v(367.1, 166.3) * mm, "end": v(367.1, 176.6) * mm});
            skLineSegment(sketch, "E3.27.13.0", {"start": v(356.8, 179) * mm, "end": v(356.8, 189.3) * mm});
            skLineSegment(sketch, "E3.27.13.1", {"start": v(356.8, 189.3) * mm, "end": v(367.1, 189.3) * mm});
            skLineSegment(sketch, "E3.27.13.2", {"start": v(356.8, 179) * mm, "end": v(367.1, 179) * mm});
            skLineSegment(sketch, "E3.27.13.3", {"start": v(367.1, 179) * mm, "end": v(367.1, 189.3) * mm});
            skLineSegment(sketch, "E3.27.14.0", {"start": v(356.8, 191.7) * mm, "end": v(356.8, 202) * mm});
            skLineSegment(sketch, "E3.27.14.1", {"start": v(356.8, 202) * mm, "end": v(367.1, 202) * mm});
            skLineSegment(sketch, "E3.27.14.2", {"start": v(356.8, 191.7) * mm, "end": v(367.1, 191.7) * mm});
            skLineSegment(sketch, "E3.27.14.3", {"start": v(367.1, 191.7) * mm, "end": v(367.1, 202) * mm});
            skLineSegment(sketch, "E3.27.15.0", {"start": v(356.8, 204.4) * mm, "end": v(356.8, 214.7) * mm});
            skLineSegment(sketch, "E3.27.15.1", {"start": v(356.8, 214.7) * mm, "end": v(367.1, 214.7) * mm});
            skLineSegment(sketch, "E3.27.15.2", {"start": v(356.8, 204.4) * mm, "end": v(367.1, 204.4) * mm});
            skLineSegment(sketch, "E3.27.15.3", {"start": v(367.1, 204.4) * mm, "end": v(367.1, 214.7) * mm});
            skLineSegment(sketch, "E3.27.16.0", {"start": v(356.8, 217.1) * mm, "end": v(356.8, 227.4) * mm});
            skLineSegment(sketch, "E3.27.16.1", {"start": v(356.8, 227.4) * mm, "end": v(367.1, 227.4) * mm});
            skLineSegment(sketch, "E3.27.16.2", {"start": v(356.8, 217.1) * mm, "end": v(367.1, 217.1) * mm});
            skLineSegment(sketch, "E3.27.16.3", {"start": v(367.1, 217.1) * mm, "end": v(367.1, 227.4) * mm});
            skLineSegment(sketch, "E3.27.17.0", {"start": v(356.8, 229.8) * mm, "end": v(356.8, 240.1) * mm});
            skLineSegment(sketch, "E3.27.17.1", {"start": v(356.8, 240.1) * mm, "end": v(367.1, 240.1) * mm});
            skLineSegment(sketch, "E3.27.17.2", {"start": v(356.8, 229.8) * mm, "end": v(367.1, 229.8) * mm});
            skLineSegment(sketch, "E3.27.17.3", {"start": v(367.1, 229.8) * mm, "end": v(367.1, 240.1) * mm});
            skLineSegment(sketch, "E3.27.18.0", {"start": v(356.8, 242.5) * mm, "end": v(356.8, 252.8) * mm});
            skLineSegment(sketch, "E3.27.18.1", {"start": v(356.8, 252.8) * mm, "end": v(367.1, 252.8) * mm});
            skLineSegment(sketch, "E3.27.18.2", {"start": v(356.8, 242.5) * mm, "end": v(367.1, 242.5) * mm});
            skLineSegment(sketch, "E3.27.18.3", {"start": v(367.1, 242.5) * mm, "end": v(367.1, 252.8) * mm});
            skLineSegment(sketch, "E3.27.19.0", {"start": v(356.8, 255.2) * mm, "end": v(356.8, 265.5) * mm});
            skLineSegment(sketch, "E3.27.19.1", {"start": v(356.8, 265.5) * mm, "end": v(367.1, 265.5) * mm});
            skLineSegment(sketch, "E3.27.19.2", {"start": v(356.8, 255.2) * mm, "end": v(367.1, 255.2) * mm});
            skLineSegment(sketch, "E3.27.19.3", {"start": v(367.1, 255.2) * mm, "end": v(367.1, 265.5) * mm});
            skLineSegment(sketch, "E3.27.20.0", {"start": v(356.8, 267.9) * mm, "end": v(356.8, 278.2) * mm});
            skLineSegment(sketch, "E3.27.20.1", {"start": v(356.8, 278.2) * mm, "end": v(367.1, 278.2) * mm});
            skLineSegment(sketch, "E3.27.20.2", {"start": v(356.8, 267.9) * mm, "end": v(367.1, 267.9) * mm});
            skLineSegment(sketch, "E3.27.20.3", {"start": v(367.1, 267.9) * mm, "end": v(367.1, 278.2) * mm});
            skLineSegment(sketch, "E3.27.21.0", {"start": v(356.8, 280.6) * mm, "end": v(356.8, 290.9) * mm});
            skLineSegment(sketch, "E3.27.21.1", {"start": v(356.8, 290.9) * mm, "end": v(367.1, 290.9) * mm});
            skLineSegment(sketch, "E3.27.21.2", {"start": v(356.8, 280.6) * mm, "end": v(367.1, 280.6) * mm});
            skLineSegment(sketch, "E3.27.21.3", {"start": v(367.1, 280.6) * mm, "end": v(367.1, 290.9) * mm});
            skLineSegment(sketch, "E3.28.0.0", {"start": v(369.5, 13.9) * mm, "end": v(369.5, 24.2) * mm});
            skLineSegment(sketch, "E3.28.0.1", {"start": v(369.5, 24.2) * mm, "end": v(379.8, 24.2) * mm});
            skLineSegment(sketch, "E3.28.0.2", {"start": v(369.5, 13.9) * mm, "end": v(379.8, 13.9) * mm});
            skLineSegment(sketch, "E3.28.0.3", {"start": v(379.8, 13.9) * mm, "end": v(379.8, 24.2) * mm});
            skLineSegment(sketch, "E3.28.1.0", {"start": v(369.5, 26.6) * mm, "end": v(369.5, 36.9) * mm});
            skLineSegment(sketch, "E3.28.1.1", {"start": v(369.5, 36.9) * mm, "end": v(379.8, 36.9) * mm});
            skLineSegment(sketch, "E3.28.1.2", {"start": v(369.5, 26.6) * mm, "end": v(379.8, 26.6) * mm});
            skLineSegment(sketch, "E3.28.1.3", {"start": v(379.8, 26.6) * mm, "end": v(379.8, 36.9) * mm});
            skLineSegment(sketch, "E3.28.2.0", {"start": v(369.5, 39.3) * mm, "end": v(369.5, 49.6) * mm});
            skLineSegment(sketch, "E3.28.2.1", {"start": v(369.5, 49.6) * mm, "end": v(379.8, 49.6) * mm});
            skLineSegment(sketch, "E3.28.2.2", {"start": v(369.5, 39.3) * mm, "end": v(379.8, 39.3) * mm});
            skLineSegment(sketch, "E3.28.2.3", {"start": v(379.8, 39.3) * mm, "end": v(379.8, 49.6) * mm});
            skLineSegment(sketch, "E3.28.3.0", {"start": v(369.5, 52) * mm, "end": v(369.5, 62.3) * mm});
            skLineSegment(sketch, "E3.28.3.1", {"start": v(369.5, 62.3) * mm, "end": v(379.8, 62.3) * mm});
            skLineSegment(sketch, "E3.28.3.2", {"start": v(369.5, 52) * mm, "end": v(379.8, 52) * mm});
            skLineSegment(sketch, "E3.28.3.3", {"start": v(379.8, 52) * mm, "end": v(379.8, 62.3) * mm});
            skLineSegment(sketch, "E3.28.4.0", {"start": v(369.5, 64.7) * mm, "end": v(369.5, 75) * mm});
            skLineSegment(sketch, "E3.28.4.1", {"start": v(369.5, 75) * mm, "end": v(379.8, 75) * mm});
            skLineSegment(sketch, "E3.28.4.2", {"start": v(369.5, 64.7) * mm, "end": v(379.8, 64.7) * mm});
            skLineSegment(sketch, "E3.28.4.3", {"start": v(379.8, 64.7) * mm, "end": v(379.8, 75) * mm});
            skLineSegment(sketch, "E3.28.5.0", {"start": v(369.5, 77.4) * mm, "end": v(369.5, 87.7) * mm});
            skLineSegment(sketch, "E3.28.5.1", {"start": v(369.5, 87.7) * mm, "end": v(379.8, 87.7) * mm});
            skLineSegment(sketch, "E3.28.5.2", {"start": v(369.5, 77.4) * mm, "end": v(379.8, 77.4) * mm});
            skLineSegment(sketch, "E3.28.5.3", {"start": v(379.8, 77.4) * mm, "end": v(379.8, 87.7) * mm});
            skLineSegment(sketch, "E3.28.6.0", {"start": v(369.5, 90.1) * mm, "end": v(369.5, 100.4) * mm});
            skLineSegment(sketch, "E3.28.6.1", {"start": v(369.5, 100.4) * mm, "end": v(379.8, 100.4) * mm});
            skLineSegment(sketch, "E3.28.6.2", {"start": v(369.5, 90.1) * mm, "end": v(379.8, 90.1) * mm});
            skLineSegment(sketch, "E3.28.6.3", {"start": v(379.8, 90.1) * mm, "end": v(379.8, 100.4) * mm});
            skLineSegment(sketch, "E3.28.7.0", {"start": v(369.5, 102.8) * mm, "end": v(369.5, 113.1) * mm});
            skLineSegment(sketch, "E3.28.7.1", {"start": v(369.5, 113.1) * mm, "end": v(379.8, 113.1) * mm});
            skLineSegment(sketch, "E3.28.7.2", {"start": v(369.5, 102.8) * mm, "end": v(379.8, 102.8) * mm});
            skLineSegment(sketch, "E3.28.7.3", {"start": v(379.8, 102.8) * mm, "end": v(379.8, 113.1) * mm});
            skLineSegment(sketch, "E3.28.8.0", {"start": v(369.5, 115.5) * mm, "end": v(369.5, 125.8) * mm});
            skLineSegment(sketch, "E3.28.8.1", {"start": v(369.5, 125.8) * mm, "end": v(379.8, 125.8) * mm});
            skLineSegment(sketch, "E3.28.8.2", {"start": v(369.5, 115.5) * mm, "end": v(379.8, 115.5) * mm});
            skLineSegment(sketch, "E3.28.8.3", {"start": v(379.8, 115.5) * mm, "end": v(379.8, 125.8) * mm});
            skLineSegment(sketch, "E3.28.9.0", {"start": v(369.5, 128.2) * mm, "end": v(369.5, 138.5) * mm});
            skLineSegment(sketch, "E3.28.9.1", {"start": v(369.5, 138.5) * mm, "end": v(379.8, 138.5) * mm});
            skLineSegment(sketch, "E3.28.9.2", {"start": v(369.5, 128.2) * mm, "end": v(379.8, 128.2) * mm});
            skLineSegment(sketch, "E3.28.9.3", {"start": v(379.8, 128.2) * mm, "end": v(379.8, 138.5) * mm});
            skLineSegment(sketch, "E3.28.10.0", {"start": v(369.5, 140.9) * mm, "end": v(369.5, 151.2) * mm});
            skLineSegment(sketch, "E3.28.10.1", {"start": v(369.5, 151.2) * mm, "end": v(379.8, 151.2) * mm});
            skLineSegment(sketch, "E3.28.10.2", {"start": v(369.5, 140.9) * mm, "end": v(379.8, 140.9) * mm});
            skLineSegment(sketch, "E3.28.10.3", {"start": v(379.8, 140.9) * mm, "end": v(379.8, 151.2) * mm});
            skLineSegment(sketch, "E3.28.11.0", {"start": v(369.5, 153.6) * mm, "end": v(369.5, 163.9) * mm});
            skLineSegment(sketch, "E3.28.11.1", {"start": v(369.5, 163.9) * mm, "end": v(379.8, 163.9) * mm});
            skLineSegment(sketch, "E3.28.11.2", {"start": v(369.5, 153.6) * mm, "end": v(379.8, 153.6) * mm});
            skLineSegment(sketch, "E3.28.11.3", {"start": v(379.8, 153.6) * mm, "end": v(379.8, 163.9) * mm});
            skLineSegment(sketch, "E3.28.12.0", {"start": v(369.5, 166.3) * mm, "end": v(369.5, 176.6) * mm});
            skLineSegment(sketch, "E3.28.12.1", {"start": v(369.5, 176.6) * mm, "end": v(379.8, 176.6) * mm});
            skLineSegment(sketch, "E3.28.12.2", {"start": v(369.5, 166.3) * mm, "end": v(379.8, 166.3) * mm});
            skLineSegment(sketch, "E3.28.12.3", {"start": v(379.8, 166.3) * mm, "end": v(379.8, 176.6) * mm});
            skLineSegment(sketch, "E3.28.13.0", {"start": v(369.5, 179) * mm, "end": v(369.5, 189.3) * mm});
            skLineSegment(sketch, "E3.28.13.1", {"start": v(369.5, 189.3) * mm, "end": v(379.8, 189.3) * mm});
            skLineSegment(sketch, "E3.28.13.2", {"start": v(369.5, 179) * mm, "end": v(379.8, 179) * mm});
            skLineSegment(sketch, "E3.28.13.3", {"start": v(379.8, 179) * mm, "end": v(379.8, 189.3) * mm});
            skLineSegment(sketch, "E3.28.14.0", {"start": v(369.5, 191.7) * mm, "end": v(369.5, 202) * mm});
            skLineSegment(sketch, "E3.28.14.1", {"start": v(369.5, 202) * mm, "end": v(379.8, 202) * mm});
            skLineSegment(sketch, "E3.28.14.2", {"start": v(369.5, 191.7) * mm, "end": v(379.8, 191.7) * mm});
            skLineSegment(sketch, "E3.28.14.3", {"start": v(379.8, 191.7) * mm, "end": v(379.8, 202) * mm});
            skLineSegment(sketch, "E3.28.15.0", {"start": v(369.5, 204.4) * mm, "end": v(369.5, 214.7) * mm});
            skLineSegment(sketch, "E3.28.15.1", {"start": v(369.5, 214.7) * mm, "end": v(379.8, 214.7) * mm});
            skLineSegment(sketch, "E3.28.15.2", {"start": v(369.5, 204.4) * mm, "end": v(379.8, 204.4) * mm});
            skLineSegment(sketch, "E3.28.15.3", {"start": v(379.8, 204.4) * mm, "end": v(379.8, 214.7) * mm});
            skLineSegment(sketch, "E3.28.16.0", {"start": v(369.5, 217.1) * mm, "end": v(369.5, 227.4) * mm});
            skLineSegment(sketch, "E3.28.16.1", {"start": v(369.5, 227.4) * mm, "end": v(379.8, 227.4) * mm});
            skLineSegment(sketch, "E3.28.16.2", {"start": v(369.5, 217.1) * mm, "end": v(379.8, 217.1) * mm});
            skLineSegment(sketch, "E3.28.16.3", {"start": v(379.8, 217.1) * mm, "end": v(379.8, 227.4) * mm});
            skLineSegment(sketch, "E3.28.17.0", {"start": v(369.5, 229.8) * mm, "end": v(369.5, 240.1) * mm});
            skLineSegment(sketch, "E3.28.17.1", {"start": v(369.5, 240.1) * mm, "end": v(379.8, 240.1) * mm});
            skLineSegment(sketch, "E3.28.17.2", {"start": v(369.5, 229.8) * mm, "end": v(379.8, 229.8) * mm});
            skLineSegment(sketch, "E3.28.17.3", {"start": v(379.8, 229.8) * mm, "end": v(379.8, 240.1) * mm});
            skLineSegment(sketch, "E3.28.18.0", {"start": v(369.5, 242.5) * mm, "end": v(369.5, 252.8) * mm});
            skLineSegment(sketch, "E3.28.18.1", {"start": v(369.5, 252.8) * mm, "end": v(379.8, 252.8) * mm});
            skLineSegment(sketch, "E3.28.18.2", {"start": v(369.5, 242.5) * mm, "end": v(379.8, 242.5) * mm});
            skLineSegment(sketch, "E3.28.18.3", {"start": v(379.8, 242.5) * mm, "end": v(379.8, 252.8) * mm});
            skLineSegment(sketch, "E3.28.19.0", {"start": v(369.5, 255.2) * mm, "end": v(369.5, 265.5) * mm});
            skLineSegment(sketch, "E3.28.19.1", {"start": v(369.5, 265.5) * mm, "end": v(379.8, 265.5) * mm});
            skLineSegment(sketch, "E3.28.19.2", {"start": v(369.5, 255.2) * mm, "end": v(379.8, 255.2) * mm});
            skLineSegment(sketch, "E3.28.19.3", {"start": v(379.8, 255.2) * mm, "end": v(379.8, 265.5) * mm});
            skLineSegment(sketch, "E3.28.20.0", {"start": v(369.5, 267.9) * mm, "end": v(369.5, 278.2) * mm});
            skLineSegment(sketch, "E3.28.20.1", {"start": v(369.5, 278.2) * mm, "end": v(379.8, 278.2) * mm});
            skLineSegment(sketch, "E3.28.20.2", {"start": v(369.5, 267.9) * mm, "end": v(379.8, 267.9) * mm});
            skLineSegment(sketch, "E3.28.20.3", {"start": v(379.8, 267.9) * mm, "end": v(379.8, 278.2) * mm});
            skLineSegment(sketch, "E3.28.21.0", {"start": v(369.5, 280.6) * mm, "end": v(369.5, 290.9) * mm});
            skLineSegment(sketch, "E3.28.21.1", {"start": v(369.5, 290.9) * mm, "end": v(379.8, 290.9) * mm});
            skLineSegment(sketch, "E3.28.21.2", {"start": v(369.5, 280.6) * mm, "end": v(379.8, 280.6) * mm});
            skLineSegment(sketch, "E3.28.21.3", {"start": v(379.8, 280.6) * mm, "end": v(379.8, 290.9) * mm});
            skLineSegment(sketch, "E3.29.0.0", {"start": v(382.2, 13.9) * mm, "end": v(382.2, 24.2) * mm});
            skLineSegment(sketch, "E3.29.0.1", {"start": v(382.2, 24.2) * mm, "end": v(392.5, 24.2) * mm});
            skLineSegment(sketch, "E3.29.0.2", {"start": v(382.2, 13.9) * mm, "end": v(392.5, 13.9) * mm});
            skLineSegment(sketch, "E3.29.0.3", {"start": v(392.5, 13.9) * mm, "end": v(392.5, 24.2) * mm});
            skLineSegment(sketch, "E3.29.1.0", {"start": v(382.2, 26.6) * mm, "end": v(382.2, 36.9) * mm});
            skLineSegment(sketch, "E3.29.1.1", {"start": v(382.2, 36.9) * mm, "end": v(392.5, 36.9) * mm});
            skLineSegment(sketch, "E3.29.1.2", {"start": v(382.2, 26.6) * mm, "end": v(392.5, 26.6) * mm});
            skLineSegment(sketch, "E3.29.1.3", {"start": v(392.5, 26.6) * mm, "end": v(392.5, 36.9) * mm});
            skLineSegment(sketch, "E3.29.2.0", {"start": v(382.2, 39.3) * mm, "end": v(382.2, 49.6) * mm});
            skLineSegment(sketch, "E3.29.2.1", {"start": v(382.2, 49.6) * mm, "end": v(392.5, 49.6) * mm});
            skLineSegment(sketch, "E3.29.2.2", {"start": v(382.2, 39.3) * mm, "end": v(392.5, 39.3) * mm});
            skLineSegment(sketch, "E3.29.2.3", {"start": v(392.5, 39.3) * mm, "end": v(392.5, 49.6) * mm});
            skLineSegment(sketch, "E3.29.3.0", {"start": v(382.2, 52) * mm, "end": v(382.2, 62.3) * mm});
            skLineSegment(sketch, "E3.29.3.1", {"start": v(382.2, 62.3) * mm, "end": v(392.5, 62.3) * mm});
            skLineSegment(sketch, "E3.29.3.2", {"start": v(382.2, 52) * mm, "end": v(392.5, 52) * mm});
            skLineSegment(sketch, "E3.29.3.3", {"start": v(392.5, 52) * mm, "end": v(392.5, 62.3) * mm});
            skLineSegment(sketch, "E3.29.4.0", {"start": v(382.2, 64.7) * mm, "end": v(382.2, 75) * mm});
            skLineSegment(sketch, "E3.29.4.1", {"start": v(382.2, 75) * mm, "end": v(392.5, 75) * mm});
            skLineSegment(sketch, "E3.29.4.2", {"start": v(382.2, 64.7) * mm, "end": v(392.5, 64.7) * mm});
            skLineSegment(sketch, "E3.29.4.3", {"start": v(392.5, 64.7) * mm, "end": v(392.5, 75) * mm});
            skLineSegment(sketch, "E3.29.5.0", {"start": v(382.2, 77.4) * mm, "end": v(382.2, 87.7) * mm});
            skLineSegment(sketch, "E3.29.5.1", {"start": v(382.2, 87.7) * mm, "end": v(392.5, 87.7) * mm});
            skLineSegment(sketch, "E3.29.5.2", {"start": v(382.2, 77.4) * mm, "end": v(392.5, 77.4) * mm});
            skLineSegment(sketch, "E3.29.5.3", {"start": v(392.5, 77.4) * mm, "end": v(392.5, 87.7) * mm});
            skLineSegment(sketch, "E3.29.6.0", {"start": v(382.2, 90.1) * mm, "end": v(382.2, 100.4) * mm});
            skLineSegment(sketch, "E3.29.6.1", {"start": v(382.2, 100.4) * mm, "end": v(392.5, 100.4) * mm});
            skLineSegment(sketch, "E3.29.6.2", {"start": v(382.2, 90.1) * mm, "end": v(392.5, 90.1) * mm});
            skLineSegment(sketch, "E3.29.6.3", {"start": v(392.5, 90.1) * mm, "end": v(392.5, 100.4) * mm});
            skLineSegment(sketch, "E3.29.7.0", {"start": v(382.2, 102.8) * mm, "end": v(382.2, 113.1) * mm});
            skLineSegment(sketch, "E3.29.7.1", {"start": v(382.2, 113.1) * mm, "end": v(392.5, 113.1) * mm});
            skLineSegment(sketch, "E3.29.7.2", {"start": v(382.2, 102.8) * mm, "end": v(392.5, 102.8) * mm});
            skLineSegment(sketch, "E3.29.7.3", {"start": v(392.5, 102.8) * mm, "end": v(392.5, 113.1) * mm});
            skLineSegment(sketch, "E3.29.8.0", {"start": v(382.2, 115.5) * mm, "end": v(382.2, 125.8) * mm});
            skLineSegment(sketch, "E3.29.8.1", {"start": v(382.2, 125.8) * mm, "end": v(392.5, 125.8) * mm});
            skLineSegment(sketch, "E3.29.8.2", {"start": v(382.2, 115.5) * mm, "end": v(392.5, 115.5) * mm});
            skLineSegment(sketch, "E3.29.8.3", {"start": v(392.5, 115.5) * mm, "end": v(392.5, 125.8) * mm});
            skLineSegment(sketch, "E3.29.9.0", {"start": v(382.2, 128.2) * mm, "end": v(382.2, 138.5) * mm});
            skLineSegment(sketch, "E3.29.9.1", {"start": v(382.2, 138.5) * mm, "end": v(392.5, 138.5) * mm});
            skLineSegment(sketch, "E3.29.9.2", {"start": v(382.2, 128.2) * mm, "end": v(392.5, 128.2) * mm});
            skLineSegment(sketch, "E3.29.9.3", {"start": v(392.5, 128.2) * mm, "end": v(392.5, 138.5) * mm});
            skLineSegment(sketch, "E3.29.10.0", {"start": v(382.2, 140.9) * mm, "end": v(382.2, 151.2) * mm});
            skLineSegment(sketch, "E3.29.10.1", {"start": v(382.2, 151.2) * mm, "end": v(392.5, 151.2) * mm});
            skLineSegment(sketch, "E3.29.10.2", {"start": v(382.2, 140.9) * mm, "end": v(392.5, 140.9) * mm});
            skLineSegment(sketch, "E3.29.10.3", {"start": v(392.5, 140.9) * mm, "end": v(392.5, 151.2) * mm});
            skLineSegment(sketch, "E3.29.11.0", {"start": v(382.2, 153.6) * mm, "end": v(382.2, 163.9) * mm});
            skLineSegment(sketch, "E3.29.11.1", {"start": v(382.2, 163.9) * mm, "end": v(392.5, 163.9) * mm});
            skLineSegment(sketch, "E3.29.11.2", {"start": v(382.2, 153.6) * mm, "end": v(392.5, 153.6) * mm});
            skLineSegment(sketch, "E3.29.11.3", {"start": v(392.5, 153.6) * mm, "end": v(392.5, 163.9) * mm});
            skLineSegment(sketch, "E3.29.12.0", {"start": v(382.2, 166.3) * mm, "end": v(382.2, 176.6) * mm});
            skLineSegment(sketch, "E3.29.12.1", {"start": v(382.2, 176.6) * mm, "end": v(392.5, 176.6) * mm});
            skLineSegment(sketch, "E3.29.12.2", {"start": v(382.2, 166.3) * mm, "end": v(392.5, 166.3) * mm});
            skLineSegment(sketch, "E3.29.12.3", {"start": v(392.5, 166.3) * mm, "end": v(392.5, 176.6) * mm});
            skLineSegment(sketch, "E3.29.13.0", {"start": v(382.2, 179) * mm, "end": v(382.2, 189.3) * mm});
            skLineSegment(sketch, "E3.29.13.1", {"start": v(382.2, 189.3) * mm, "end": v(392.5, 189.3) * mm});
            skLineSegment(sketch, "E3.29.13.2", {"start": v(382.2, 179) * mm, "end": v(392.5, 179) * mm});
            skLineSegment(sketch, "E3.29.13.3", {"start": v(392.5, 179) * mm, "end": v(392.5, 189.3) * mm});
            skLineSegment(sketch, "E3.29.14.0", {"start": v(382.2, 191.7) * mm, "end": v(382.2, 202) * mm});
            skLineSegment(sketch, "E3.29.14.1", {"start": v(382.2, 202) * mm, "end": v(392.5, 202) * mm});
            skLineSegment(sketch, "E3.29.14.2", {"start": v(382.2, 191.7) * mm, "end": v(392.5, 191.7) * mm});
            skLineSegment(sketch, "E3.29.14.3", {"start": v(392.5, 191.7) * mm, "end": v(392.5, 202) * mm});
            skLineSegment(sketch, "E3.29.15.0", {"start": v(382.2, 204.4) * mm, "end": v(382.2, 214.7) * mm});
            skLineSegment(sketch, "E3.29.15.1", {"start": v(382.2, 214.7) * mm, "end": v(392.5, 214.7) * mm});
            skLineSegment(sketch, "E3.29.15.2", {"start": v(382.2, 204.4) * mm, "end": v(392.5, 204.4) * mm});
            skLineSegment(sketch, "E3.29.15.3", {"start": v(392.5, 204.4) * mm, "end": v(392.5, 214.7) * mm});
            skLineSegment(sketch, "E3.29.16.0", {"start": v(382.2, 217.1) * mm, "end": v(382.2, 227.4) * mm});
            skLineSegment(sketch, "E3.29.16.1", {"start": v(382.2, 227.4) * mm, "end": v(392.5, 227.4) * mm});
            skLineSegment(sketch, "E3.29.16.2", {"start": v(382.2, 217.1) * mm, "end": v(392.5, 217.1) * mm});
            skLineSegment(sketch, "E3.29.16.3", {"start": v(392.5, 217.1) * mm, "end": v(392.5, 227.4) * mm});
            skLineSegment(sketch, "E3.29.17.0", {"start": v(382.2, 229.8) * mm, "end": v(382.2, 240.1) * mm});
            skLineSegment(sketch, "E3.29.17.1", {"start": v(382.2, 240.1) * mm, "end": v(392.5, 240.1) * mm});
            skLineSegment(sketch, "E3.29.17.2", {"start": v(382.2, 229.8) * mm, "end": v(392.5, 229.8) * mm});
            skLineSegment(sketch, "E3.29.17.3", {"start": v(392.5, 229.8) * mm, "end": v(392.5, 240.1) * mm});
            skLineSegment(sketch, "E3.29.18.0", {"start": v(382.2, 242.5) * mm, "end": v(382.2, 252.8) * mm});
            skLineSegment(sketch, "E3.29.18.1", {"start": v(382.2, 252.8) * mm, "end": v(392.5, 252.8) * mm});
            skLineSegment(sketch, "E3.29.18.2", {"start": v(382.2, 242.5) * mm, "end": v(392.5, 242.5) * mm});
            skLineSegment(sketch, "E3.29.18.3", {"start": v(392.5, 242.5) * mm, "end": v(392.5, 252.8) * mm});
            skLineSegment(sketch, "E3.29.19.0", {"start": v(382.2, 255.2) * mm, "end": v(382.2, 265.5) * mm});
            skLineSegment(sketch, "E3.29.19.1", {"start": v(382.2, 265.5) * mm, "end": v(392.5, 265.5) * mm});
            skLineSegment(sketch, "E3.29.19.2", {"start": v(382.2, 255.2) * mm, "end": v(392.5, 255.2) * mm});
            skLineSegment(sketch, "E3.29.19.3", {"start": v(392.5, 255.2) * mm, "end": v(392.5, 265.5) * mm});
            skLineSegment(sketch, "E3.29.20.0", {"start": v(382.2, 267.9) * mm, "end": v(382.2, 278.2) * mm});
            skLineSegment(sketch, "E3.29.20.1", {"start": v(382.2, 278.2) * mm, "end": v(392.5, 278.2) * mm});
            skLineSegment(sketch, "E3.29.20.2", {"start": v(382.2, 267.9) * mm, "end": v(392.5, 267.9) * mm});
            skLineSegment(sketch, "E3.29.20.3", {"start": v(392.5, 267.9) * mm, "end": v(392.5, 278.2) * mm});
            skLineSegment(sketch, "E3.29.21.0", {"start": v(382.2, 280.6) * mm, "end": v(382.2, 290.9) * mm});
            skLineSegment(sketch, "E3.29.21.1", {"start": v(382.2, 290.9) * mm, "end": v(392.5, 290.9) * mm});
            skLineSegment(sketch, "E3.29.21.2", {"start": v(382.2, 280.6) * mm, "end": v(392.5, 280.6) * mm});
            skLineSegment(sketch, "E3.29.21.3", {"start": v(392.5, 280.6) * mm, "end": v(392.5, 290.9) * mm});
            skLineSegment(sketch, "E3.direction1", {"start": v(15.09, 15.09) * mm, "end": v(27.79, 15.09) * mm, "construction": true});
            skLineSegment(sketch, "E3.direction2", {"start": v(15.09, 15.09) * mm, "end": v(15.09, 27.79) * mm, "construction": true});
            skPoint(sketch, "E4.visualSharp", {"position": v(11.5, 11.5) * mm});
            skArc(sketch, "E4.filletArc", {"start": v(11.5, 12.7) * mm, "mid": v(11.86, 11.86) * mm, "end": v(12.7, 11.5) * mm});
            skPoint(sketch, "E5.visualSharp", {"position": v(394.9, 11.5) * mm});
            skArc(sketch, "E5.filletArc", {"start": v(393.7, 11.5) * mm, "mid": v(394.54, 11.86) * mm, "end": v(394.9, 12.7) * mm});
            skPoint(sketch, "E6.visualSharp", {"position": v(394.9, 293.3) * mm});
            skArc(sketch, "E6.filletArc", {"start": v(394.9, 292.1) * mm, "mid": v(394.54, 292.94) * mm, "end": v(393.7, 293.3) * mm});
            skPoint(sketch, "E7.visualSharp", {"position": v(11.5, 293.3) * mm});
            skArc(sketch, "E7.filletArc", {"start": v(12.7, 293.3) * mm, "mid": v(11.86, 292.94) * mm, "end": v(11.5, 292.1) * mm});
            skSolve(sketch);
        }
        {
            var Q0;
            Q0=qSketchRegion(id+"F2",true);
            extrude(context, id + "F3", {"entities" : qUnion([Q0]), "operationType" : NewBodyOperationType.REMOVE, "oppositeDirection" : true, "depth" : 2.4 * mm});
        }
        {
            var Q0;
            Q0=makeQuery(id+"F3.boolean.opBoolean","COPY",FACE,{"derivedFrom":makeQuery(id+"F3.opExtrude","CAP_FACE",FACE,{"disambiguationData":[OSD([sQuery(id+"F2.wireOp",EDGE,"E1.bottom"),sQuery(id+"F2.wireOp",EDGE,"E1.top"),sQuery(id+"F2.wireOp",EDGE,"E1.left"),sQuery(id+"F2.wireOp",EDGE,"E1.right"),sQuery(id+"F2.wireOp",EDGE,"E2.bottom"),sQuery(id+"F2.wireOp",EDGE,"E2.top"),sQuery(id+"F2.wireOp",EDGE,"E2.left"),sQuery(id+"F2.wireOp",EDGE,"E2.right"),sQuery(id+"F2.wireOp",EDGE,"E3.0.1.0"),sQuery(id+"F2.wireOp",EDGE,"E3.0.1.1"),sQuery(id+"F2.wireOp",EDGE,"E3.0.1.2"),sQuery(id+"F2.wireOp",EDGE,"E3.0.1.3"),sQuery(id+"F2.wireOp",EDGE,"E3.0.2.0"),sQuery(id+"F2.wireOp",EDGE,"E3.0.2.1"),sQuery(id+"F2.wireOp",EDGE,"E3.0.2.2"),sQuery(id+"F2.wireOp",EDGE,"E3.0.2.3"),sQuery(id+"F2.wireOp",EDGE,"E3.0.3.0"),sQuery(id+"F2.wireOp",EDGE,"E3.0.3.1"),sQuery(id+"F2.wireOp",EDGE,"E3.0.3.2"),sQuery(id+"F2.wireOp",EDGE,"E3.0.3.3"),sQuery(id+"F2.wireOp",EDGE,"E3.0.4.0"),sQuery(id+"F2.wireOp",EDGE,"E3.0.4.1"),sQuery(id+"F2.wireOp",EDGE,"E3.0.4.2"),sQuery(id+"F2.wireOp",EDGE,"E3.0.4.3"),sQuery(id+"F2.wireOp",EDGE,"E3.0.5.0"),sQuery(id+"F2.wireOp",EDGE,"E3.0.5.1"),sQuery(id+"F2.wireOp",EDGE,"E3.0.5.2"),sQuery(id+"F2.wireOp",EDGE,"E3.0.5.3"),sQuery(id+"F2.wireOp",EDGE,"E3.0.6.0"),sQuery(id+"F2.wireOp",EDGE,"E3.0.6.1"),sQuery(id+"F2.wireOp",EDGE,"E3.0.6.2"),sQuery(id+"F2.wireOp",EDGE,"E3.0.6.3"),sQuery(id+"F2.wireOp",EDGE,"E3.0.7.0"),sQuery(id+"F2.wireOp",EDGE,"E3.0.7.1"),sQuery(id+"F2.wireOp",EDGE,"E3.0.7.2"),sQuery(id+"F2.wireOp",EDGE,"E3.0.7.3"),sQuery(id+"F2.wireOp",EDGE,"E3.0.8.0"),sQuery(id+"F2.wireOp",EDGE,"E3.0.8.1"),sQuery(id+"F2.wireOp",EDGE,"E3.0.8.2"),sQuery(id+"F2.wireOp",EDGE,"E3.0.8.3"),sQuery(id+"F2.wireOp",EDGE,"E3.0.9.0"),sQuery(id+"F2.wireOp",EDGE,"E3.0.9.1"),sQuery(id+"F2.wireOp",EDGE,"E3.0.9.2"),sQuery(id+"F2.wireOp",EDGE,"E3.0.9.3"),sQuery(id+"F2.wireOp",EDGE,"E3.0.10.0"),sQuery(id+"F2.wireOp",EDGE,"E3.0.10.1"),sQuery(id+"F2.wireOp",EDGE,"E3.0.10.2"),sQuery(id+"F2.wireOp",EDGE,"E3.0.10.3"),sQuery(id+"F2.wireOp",EDGE,"E3.0.11.0"),sQuery(id+"F2.wireOp",EDGE,"E3.0.11.1"),sQuery(id+"F2.wireOp",EDGE,"E3.0.11.2"),sQuery(id+"F2.wireOp",EDGE,"E3.0.11.3"),sQuery(id+"F2.wireOp",EDGE,"E3.0.12.0"),sQuery(id+"F2.wireOp",EDGE,"E3.0.12.1"),sQuery(id+"F2.wireOp",EDGE,"E3.0.12.2"),sQuery(id+"F2.wireOp",EDGE,"E3.0.12.3"),sQuery(id+"F2.wireOp",EDGE,"E3.0.13.0"),sQuery(id+"F2.wireOp",EDGE,"E3.0.13.1"),sQuery(id+"F2.wireOp",EDGE,"E3.0.13.2"),sQuery(id+"F2.wireOp",EDGE,"E3.0.13.3"),sQuery(id+"F2.wireOp",EDGE,"E3.0.14.0"),sQuery(id+"F2.wireOp",EDGE,"E3.0.14.1"),sQuery(id+"F2.wireOp",EDGE,"E3.0.14.2"),sQuery(id+"F2.wireOp",EDGE,"E3.0.14.3"),sQuery(id+"F2.wireOp",EDGE,"E3.0.15.0"),sQuery(id+"F2.wireOp",EDGE,"E3.0.15.1"),sQuery(id+"F2.wireOp",EDGE,"E3.0.15.2"),sQuery(id+"F2.wireOp",EDGE,"E3.0.15.3"),sQuery(id+"F2.wireOp",EDGE,"E3.0.16.0"),sQuery(id+"F2.wireOp",EDGE,"E3.0.16.1"),sQuery(id+"F2.wireOp",EDGE,"E3.0.16.2"),sQuery(id+"F2.wireOp",EDGE,"E3.0.16.3"),sQuery(id+"F2.wireOp",EDGE,"E3.0.17.0"),sQuery(id+"F2.wireOp",EDGE,"E3.0.17.1"),sQuery(id+"F2.wireOp",EDGE,"E3.0.17.2"),sQuery(id+"F2.wireOp",EDGE,"E3.0.17.3"),sQuery(id+"F2.wireOp",EDGE,"E3.0.18.0"),sQuery(id+"F2.wireOp",EDGE,"E3.0.18.1"),sQuery(id+"F2.wireOp",EDGE,"E3.0.18.2"),sQuery(id+"F2.wireOp",EDGE,"E3.0.18.3"),sQuery(id+"F2.wireOp",EDGE,"E3.0.19.0"),sQuery(id+"F2.wireOp",EDGE,"E3.0.19.1"),sQuery(id+"F2.wireOp",EDGE,"E3.0.19.2"),sQuery(id+"F2.wireOp",EDGE,"E3.0.19.3"),sQuery(id+"F2.wireOp",EDGE,"E3.0.20.0"),sQuery(id+"F2.wireOp",EDGE,"E3.0.20.1"),sQuery(id+"F2.wireOp",EDGE,"E3.0.20.2"),sQuery(id+"F2.wireOp",EDGE,"E3.0.20.3"),sQuery(id+"F2.wireOp",EDGE,"E3.0.21.0"),sQuery(id+"F2.wireOp",EDGE,"E3.0.21.1"),sQuery(id+"F2.wireOp",EDGE,"E3.0.21.2"),sQuery(id+"F2.wireOp",EDGE,"E3.0.21.3"),sQuery(id+"F2.wireOp",EDGE,"E3.1.0.0"),sQuery(id+"F2.wireOp",EDGE,"E3.1.0.1"),sQuery(id+"F2.wireOp",EDGE,"E3.1.0.2"),sQuery(id+"F2.wireOp",EDGE,"E3.1.0.3"),sQuery(id+"F2.wireOp",EDGE,"E3.1.1.0"),sQuery(id+"F2.wireOp",EDGE,"E3.1.1.1"),sQuery(id+"F2.wireOp",EDGE,"E3.1.1.2"),sQuery(id+"F2.wireOp",EDGE,"E3.1.1.3"),sQuery(id+"F2.wireOp",EDGE,"E3.1.2.0"),sQuery(id+"F2.wireOp",EDGE,"E3.1.2.1"),sQuery(id+"F2.wireOp",EDGE,"E3.1.2.2"),sQuery(id+"F2.wireOp",EDGE,"E3.1.2.3"),sQuery(id+"F2.wireOp",EDGE,"E3.1.3.0"),sQuery(id+"F2.wireOp",EDGE,"E3.1.3.1"),sQuery(id+"F2.wireOp",EDGE,"E3.1.3.2"),sQuery(id+"F2.wireOp",EDGE,"E3.1.3.3"),sQuery(id+"F2.wireOp",EDGE,"E3.1.4.0"),sQuery(id+"F2.wireOp",EDGE,"E3.1.4.1"),sQuery(id+"F2.wireOp",EDGE,"E3.1.4.2"),sQuery(id+"F2.wireOp",EDGE,"E3.1.4.3"),sQuery(id+"F2.wireOp",EDGE,"E3.1.5.0"),sQuery(id+"F2.wireOp",EDGE,"E3.1.5.1"),sQuery(id+"F2.wireOp",EDGE,"E3.1.5.2"),sQuery(id+"F2.wireOp",EDGE,"E3.1.5.3"),sQuery(id+"F2.wireOp",EDGE,"E3.1.6.0"),sQuery(id+"F2.wireOp",EDGE,"E3.1.6.1"),sQuery(id+"F2.wireOp",EDGE,"E3.1.6.2"),sQuery(id+"F2.wireOp",EDGE,"E3.1.6.3"),sQuery(id+"F2.wireOp",EDGE,"E3.1.7.0"),sQuery(id+"F2.wireOp",EDGE,"E3.1.7.1"),sQuery(id+"F2.wireOp",EDGE,"E3.1.7.2"),sQuery(id+"F2.wireOp",EDGE,"E3.1.7.3"),sQuery(id+"F2.wireOp",EDGE,"E3.1.8.0"),sQuery(id+"F2.wireOp",EDGE,"E3.1.8.1"),sQuery(id+"F2.wireOp",EDGE,"E3.1.8.2"),sQuery(id+"F2.wireOp",EDGE,"E3.1.8.3"),sQuery(id+"F2.wireOp",EDGE,"E3.1.9.0"),sQuery(id+"F2.wireOp",EDGE,"E3.1.9.1"),sQuery(id+"F2.wireOp",EDGE,"E3.1.9.2"),sQuery(id+"F2.wireOp",EDGE,"E3.1.9.3"),sQuery(id+"F2.wireOp",EDGE,"E3.1.10.0"),sQuery(id+"F2.wireOp",EDGE,"E3.1.10.1"),sQuery(id+"F2.wireOp",EDGE,"E3.1.10.2"),sQuery(id+"F2.wireOp",EDGE,"E3.1.10.3"),sQuery(id+"F2.wireOp",EDGE,"E3.1.11.0"),sQuery(id+"F2.wireOp",EDGE,"E3.1.11.1"),sQuery(id+"F2.wireOp",EDGE,"E3.1.11.2"),sQuery(id+"F2.wireOp",EDGE,"E3.1.11.3"),sQuery(id+"F2.wireOp",EDGE,"E3.1.12.0"),sQuery(id+"F2.wireOp",EDGE,"E3.1.12.1"),sQuery(id+"F2.wireOp",EDGE,"E3.1.12.2"),sQuery(id+"F2.wireOp",EDGE,"E3.1.12.3"),sQuery(id+"F2.wireOp",EDGE,"E3.1.13.0"),sQuery(id+"F2.wireOp",EDGE,"E3.1.13.1"),sQuery(id+"F2.wireOp",EDGE,"E3.1.13.2"),sQuery(id+"F2.wireOp",EDGE,"E3.1.13.3"),sQuery(id+"F2.wireOp",EDGE,"E3.1.14.0"),sQuery(id+"F2.wireOp",EDGE,"E3.1.14.1"),sQuery(id+"F2.wireOp",EDGE,"E3.1.14.2"),sQuery(id+"F2.wireOp",EDGE,"E3.1.14.3"),sQuery(id+"F2.wireOp",EDGE,"E3.1.15.0"),sQuery(id+"F2.wireOp",EDGE,"E3.1.15.1"),sQuery(id+"F2.wireOp",EDGE,"E3.1.15.2"),sQuery(id+"F2.wireOp",EDGE,"E3.1.15.3"),sQuery(id+"F2.wireOp",EDGE,"E3.1.16.0"),sQuery(id+"F2.wireOp",EDGE,"E3.1.16.1"),sQuery(id+"F2.wireOp",EDGE,"E3.1.16.2"),sQuery(id+"F2.wireOp",EDGE,"E3.1.16.3"),sQuery(id+"F2.wireOp",EDGE,"E3.1.17.0"),sQuery(id+"F2.wireOp",EDGE,"E3.1.17.1"),sQuery(id+"F2.wireOp",EDGE,"E3.1.17.2"),sQuery(id+"F2.wireOp",EDGE,"E3.1.17.3"),sQuery(id+"F2.wireOp",EDGE,"E3.1.18.0"),sQuery(id+"F2.wireOp",EDGE,"E3.1.18.1"),sQuery(id+"F2.wireOp",EDGE,"E3.1.18.2"),sQuery(id+"F2.wireOp",EDGE,"E3.1.18.3"),sQuery(id+"F2.wireOp",EDGE,"E3.1.19.0"),sQuery(id+"F2.wireOp",EDGE,"E3.1.19.1"),sQuery(id+"F2.wireOp",EDGE,"E3.1.19.2"),sQuery(id+"F2.wireOp",EDGE,"E3.1.19.3"),sQuery(id+"F2.wireOp",EDGE,"E3.1.20.0"),sQuery(id+"F2.wireOp",EDGE,"E3.1.20.1"),sQuery(id+"F2.wireOp",EDGE,"E3.1.20.2"),sQuery(id+"F2.wireOp",EDGE,"E3.1.20.3"),sQuery(id+"F2.wireOp",EDGE,"E3.1.21.0"),sQuery(id+"F2.wireOp",EDGE,"E3.1.21.1"),sQuery(id+"F2.wireOp",EDGE,"E3.1.21.2"),sQuery(id+"F2.wireOp",EDGE,"E3.1.21.3"),sQuery(id+"F2.wireOp",EDGE,"E3.2.0.0"),sQuery(id+"F2.wireOp",EDGE,"E3.2.0.1"),sQuery(id+"F2.wireOp",EDGE,"E3.2.0.2"),sQuery(id+"F2.wireOp",EDGE,"E3.2.0.3"),sQuery(id+"F2.wireOp",EDGE,"E3.2.1.0"),sQuery(id+"F2.wireOp",EDGE,"E3.2.1.1"),sQuery(id+"F2.wireOp",EDGE,"E3.2.1.2"),sQuery(id+"F2.wireOp",EDGE,"E3.2.1.3"),sQuery(id+"F2.wireOp",EDGE,"E3.2.2.0"),sQuery(id+"F2.wireOp",EDGE,"E3.2.2.1"),sQuery(id+"F2.wireOp",EDGE,"E3.2.2.2"),sQuery(id+"F2.wireOp",EDGE,"E3.2.2.3"),sQuery(id+"F2.wireOp",EDGE,"E3.2.3.0"),sQuery(id+"F2.wireOp",EDGE,"E3.2.3.1"),sQuery(id+"F2.wireOp",EDGE,"E3.2.3.2"),sQuery(id+"F2.wireOp",EDGE,"E3.2.3.3"),sQuery(id+"F2.wireOp",EDGE,"E3.2.4.0"),sQuery(id+"F2.wireOp",EDGE,"E3.2.4.1"),sQuery(id+"F2.wireOp",EDGE,"E3.2.4.2"),sQuery(id+"F2.wireOp",EDGE,"E3.2.4.3"),sQuery(id+"F2.wireOp",EDGE,"E3.2.5.0"),sQuery(id+"F2.wireOp",EDGE,"E3.2.5.1"),sQuery(id+"F2.wireOp",EDGE,"E3.2.5.2"),sQuery(id+"F2.wireOp",EDGE,"E3.2.5.3"),sQuery(id+"F2.wireOp",EDGE,"E3.2.6.0"),sQuery(id+"F2.wireOp",EDGE,"E3.2.6.1"),sQuery(id+"F2.wireOp",EDGE,"E3.2.6.2"),sQuery(id+"F2.wireOp",EDGE,"E3.2.6.3"),sQuery(id+"F2.wireOp",EDGE,"E3.2.7.0"),sQuery(id+"F2.wireOp",EDGE,"E3.2.7.1"),sQuery(id+"F2.wireOp",EDGE,"E3.2.7.2"),sQuery(id+"F2.wireOp",EDGE,"E3.2.7.3"),sQuery(id+"F2.wireOp",EDGE,"E3.2.8.0"),sQuery(id+"F2.wireOp",EDGE,"E3.2.8.1"),sQuery(id+"F2.wireOp",EDGE,"E3.2.8.2"),sQuery(id+"F2.wireOp",EDGE,"E3.2.8.3"),sQuery(id+"F2.wireOp",EDGE,"E3.2.9.0"),sQuery(id+"F2.wireOp",EDGE,"E3.2.9.1"),sQuery(id+"F2.wireOp",EDGE,"E3.2.9.2"),sQuery(id+"F2.wireOp",EDGE,"E3.2.9.3"),sQuery(id+"F2.wireOp",EDGE,"E3.2.10.0"),sQuery(id+"F2.wireOp",EDGE,"E3.2.10.1"),sQuery(id+"F2.wireOp",EDGE,"E3.2.10.2"),sQuery(id+"F2.wireOp",EDGE,"E3.2.10.3"),sQuery(id+"F2.wireOp",EDGE,"E3.2.11.0"),sQuery(id+"F2.wireOp",EDGE,"E3.2.11.1"),sQuery(id+"F2.wireOp",EDGE,"E3.2.11.2"),sQuery(id+"F2.wireOp",EDGE,"E3.2.11.3"),sQuery(id+"F2.wireOp",EDGE,"E3.2.12.0"),sQuery(id+"F2.wireOp",EDGE,"E3.2.12.1"),sQuery(id+"F2.wireOp",EDGE,"E3.2.12.2"),sQuery(id+"F2.wireOp",EDGE,"E3.2.12.3"),sQuery(id+"F2.wireOp",EDGE,"E3.2.13.0"),sQuery(id+"F2.wireOp",EDGE,"E3.2.13.1"),sQuery(id+"F2.wireOp",EDGE,"E3.2.13.2"),sQuery(id+"F2.wireOp",EDGE,"E3.2.13.3"),sQuery(id+"F2.wireOp",EDGE,"E3.2.14.0"),sQuery(id+"F2.wireOp",EDGE,"E3.2.14.1"),sQuery(id+"F2.wireOp",EDGE,"E3.2.14.2"),sQuery(id+"F2.wireOp",EDGE,"E3.2.14.3"),sQuery(id+"F2.wireOp",EDGE,"E3.2.15.0"),sQuery(id+"F2.wireOp",EDGE,"E3.2.15.1"),sQuery(id+"F2.wireOp",EDGE,"E3.2.15.2"),sQuery(id+"F2.wireOp",EDGE,"E3.2.15.3"),sQuery(id+"F2.wireOp",EDGE,"E3.2.16.0"),sQuery(id+"F2.wireOp",EDGE,"E3.2.16.1"),sQuery(id+"F2.wireOp",EDGE,"E3.2.16.2"),sQuery(id+"F2.wireOp",EDGE,"E3.2.16.3"),sQuery(id+"F2.wireOp",EDGE,"E3.2.17.0"),sQuery(id+"F2.wireOp",EDGE,"E3.2.17.1"),sQuery(id+"F2.wireOp",EDGE,"E3.2.17.2"),sQuery(id+"F2.wireOp",EDGE,"E3.2.17.3"),sQuery(id+"F2.wireOp",EDGE,"E3.2.18.0"),sQuery(id+"F2.wireOp",EDGE,"E3.2.18.1"),sQuery(id+"F2.wireOp",EDGE,"E3.2.18.2"),sQuery(id+"F2.wireOp",EDGE,"E3.2.18.3"),sQuery(id+"F2.wireOp",EDGE,"E3.2.19.0"),sQuery(id+"F2.wireOp",EDGE,"E3.2.19.1"),sQuery(id+"F2.wireOp",EDGE,"E3.2.19.2"),sQuery(id+"F2.wireOp",EDGE,"E3.2.19.3"),sQuery(id+"F2.wireOp",EDGE,"E3.2.20.0"),sQuery(id+"F2.wireOp",EDGE,"E3.2.20.1"),sQuery(id+"F2.wireOp",EDGE,"E3.2.20.2"),sQuery(id+"F2.wireOp",EDGE,"E3.2.20.3"),sQuery(id+"F2.wireOp",EDGE,"E3.2.21.0"),sQuery(id+"F2.wireOp",EDGE,"E3.2.21.1"),sQuery(id+"F2.wireOp",EDGE,"E3.2.21.2"),sQuery(id+"F2.wireOp",EDGE,"E3.2.21.3"),sQuery(id+"F2.wireOp",EDGE,"E3.3.0.0"),sQuery(id+"F2.wireOp",EDGE,"E3.3.0.1"),sQuery(id+"F2.wireOp",EDGE,"E3.3.0.2"),sQuery(id+"F2.wireOp",EDGE,"E3.3.0.3"),sQuery(id+"F2.wireOp",EDGE,"E3.3.1.0"),sQuery(id+"F2.wireOp",EDGE,"E3.3.1.1"),sQuery(id+"F2.wireOp",EDGE,"E3.3.1.2"),sQuery(id+"F2.wireOp",EDGE,"E3.3.1.3"),sQuery(id+"F2.wireOp",EDGE,"E3.3.2.0"),sQuery(id+"F2.wireOp",EDGE,"E3.3.2.1"),sQuery(id+"F2.wireOp",EDGE,"E3.3.2.2"),sQuery(id+"F2.wireOp",EDGE,"E3.3.2.3"),sQuery(id+"F2.wireOp",EDGE,"E3.3.3.0"),sQuery(id+"F2.wireOp",EDGE,"E3.3.3.1"),sQuery(id+"F2.wireOp",EDGE,"E3.3.3.2"),sQuery(id+"F2.wireOp",EDGE,"E3.3.3.3"),sQuery(id+"F2.wireOp",EDGE,"E3.3.4.0"),sQuery(id+"F2.wireOp",EDGE,"E3.3.4.1"),sQuery(id+"F2.wireOp",EDGE,"E3.3.4.2"),sQuery(id+"F2.wireOp",EDGE,"E3.3.4.3"),sQuery(id+"F2.wireOp",EDGE,"E3.3.5.0"),sQuery(id+"F2.wireOp",EDGE,"E3.3.5.1"),sQuery(id+"F2.wireOp",EDGE,"E3.3.5.2"),sQuery(id+"F2.wireOp",EDGE,"E3.3.5.3"),sQuery(id+"F2.wireOp",EDGE,"E3.3.6.0"),sQuery(id+"F2.wireOp",EDGE,"E3.3.6.1"),sQuery(id+"F2.wireOp",EDGE,"E3.3.6.2"),sQuery(id+"F2.wireOp",EDGE,"E3.3.6.3"),sQuery(id+"F2.wireOp",EDGE,"E3.3.7.0"),sQuery(id+"F2.wireOp",EDGE,"E3.3.7.1"),sQuery(id+"F2.wireOp",EDGE,"E3.3.7.2"),sQuery(id+"F2.wireOp",EDGE,"E3.3.7.3"),sQuery(id+"F2.wireOp",EDGE,"E3.3.8.0"),sQuery(id+"F2.wireOp",EDGE,"E3.3.8.1"),sQuery(id+"F2.wireOp",EDGE,"E3.3.8.2"),sQuery(id+"F2.wireOp",EDGE,"E3.3.8.3"),sQuery(id+"F2.wireOp",EDGE,"E3.3.9.0"),sQuery(id+"F2.wireOp",EDGE,"E3.3.9.1"),sQuery(id+"F2.wireOp",EDGE,"E3.3.9.2"),sQuery(id+"F2.wireOp",EDGE,"E3.3.9.3"),sQuery(id+"F2.wireOp",EDGE,"E3.3.10.0"),sQuery(id+"F2.wireOp",EDGE,"E3.3.10.1"),sQuery(id+"F2.wireOp",EDGE,"E3.3.10.2"),sQuery(id+"F2.wireOp",EDGE,"E3.3.10.3"),sQuery(id+"F2.wireOp",EDGE,"E3.3.11.0"),sQuery(id+"F2.wireOp",EDGE,"E3.3.11.1"),sQuery(id+"F2.wireOp",EDGE,"E3.3.11.2"),sQuery(id+"F2.wireOp",EDGE,"E3.3.11.3"),sQuery(id+"F2.wireOp",EDGE,"E3.3.12.0"),sQuery(id+"F2.wireOp",EDGE,"E3.3.12.1"),sQuery(id+"F2.wireOp",EDGE,"E3.3.12.2"),sQuery(id+"F2.wireOp",EDGE,"E3.3.12.3"),sQuery(id+"F2.wireOp",EDGE,"E3.3.13.0"),sQuery(id+"F2.wireOp",EDGE,"E3.3.13.1"),sQuery(id+"F2.wireOp",EDGE,"E3.3.13.2"),sQuery(id+"F2.wireOp",EDGE,"E3.3.13.3"),sQuery(id+"F2.wireOp",EDGE,"E3.3.14.0"),sQuery(id+"F2.wireOp",EDGE,"E3.3.14.1"),sQuery(id+"F2.wireOp",EDGE,"E3.3.14.2"),sQuery(id+"F2.wireOp",EDGE,"E3.3.14.3"),sQuery(id+"F2.wireOp",EDGE,"E3.3.15.0"),sQuery(id+"F2.wireOp",EDGE,"E3.3.15.1"),sQuery(id+"F2.wireOp",EDGE,"E3.3.15.2"),sQuery(id+"F2.wireOp",EDGE,"E3.3.15.3"),sQuery(id+"F2.wireOp",EDGE,"E3.3.16.0"),sQuery(id+"F2.wireOp",EDGE,"E3.3.16.1"),sQuery(id+"F2.wireOp",EDGE,"E3.3.16.2"),sQuery(id+"F2.wireOp",EDGE,"E3.3.16.3"),sQuery(id+"F2.wireOp",EDGE,"E3.3.17.0"),sQuery(id+"F2.wireOp",EDGE,"E3.3.17.1"),sQuery(id+"F2.wireOp",EDGE,"E3.3.17.2"),sQuery(id+"F2.wireOp",EDGE,"E3.3.17.3"),sQuery(id+"F2.wireOp",EDGE,"E3.3.18.0"),sQuery(id+"F2.wireOp",EDGE,"E3.3.18.1"),sQuery(id+"F2.wireOp",EDGE,"E3.3.18.2"),sQuery(id+"F2.wireOp",EDGE,"E3.3.18.3"),sQuery(id+"F2.wireOp",EDGE,"E3.3.19.0"),sQuery(id+"F2.wireOp",EDGE,"E3.3.19.1"),sQuery(id+"F2.wireOp",EDGE,"E3.3.19.2"),sQuery(id+"F2.wireOp",EDGE,"E3.3.19.3"),sQuery(id+"F2.wireOp",EDGE,"E3.3.20.0"),sQuery(id+"F2.wireOp",EDGE,"E3.3.20.1"),sQuery(id+"F2.wireOp",EDGE,"E3.3.20.2"),sQuery(id+"F2.wireOp",EDGE,"E3.3.20.3"),sQuery(id+"F2.wireOp",EDGE,"E3.3.21.0"),sQuery(id+"F2.wireOp",EDGE,"E3.3.21.1"),sQuery(id+"F2.wireOp",EDGE,"E3.3.21.2"),sQuery(id+"F2.wireOp",EDGE,"E3.3.21.3"),sQuery(id+"F2.wireOp",EDGE,"E3.4.0.0"),sQuery(id+"F2.wireOp",EDGE,"E3.4.0.1"),sQuery(id+"F2.wireOp",EDGE,"E3.4.0.2"),sQuery(id+"F2.wireOp",EDGE,"E3.4.0.3"),sQuery(id+"F2.wireOp",EDGE,"E3.4.1.0"),sQuery(id+"F2.wireOp",EDGE,"E3.4.1.1"),sQuery(id+"F2.wireOp",EDGE,"E3.4.1.2"),sQuery(id+"F2.wireOp",EDGE,"E3.4.1.3"),sQuery(id+"F2.wireOp",EDGE,"E3.4.2.0"),sQuery(id+"F2.wireOp",EDGE,"E3.4.2.1"),sQuery(id+"F2.wireOp",EDGE,"E3.4.2.2"),sQuery(id+"F2.wireOp",EDGE,"E3.4.2.3"),sQuery(id+"F2.wireOp",EDGE,"E3.4.3.0"),sQuery(id+"F2.wireOp",EDGE,"E3.4.3.1"),sQuery(id+"F2.wireOp",EDGE,"E3.4.3.2"),sQuery(id+"F2.wireOp",EDGE,"E3.4.3.3"),sQuery(id+"F2.wireOp",EDGE,"E3.4.4.0"),sQuery(id+"F2.wireOp",EDGE,"E3.4.4.1"),sQuery(id+"F2.wireOp",EDGE,"E3.4.4.2"),sQuery(id+"F2.wireOp",EDGE,"E3.4.4.3"),sQuery(id+"F2.wireOp",EDGE,"E3.4.5.0"),sQuery(id+"F2.wireOp",EDGE,"E3.4.5.1"),sQuery(id+"F2.wireOp",EDGE,"E3.4.5.2"),sQuery(id+"F2.wireOp",EDGE,"E3.4.5.3"),sQuery(id+"F2.wireOp",EDGE,"E3.4.6.0"),sQuery(id+"F2.wireOp",EDGE,"E3.4.6.1"),sQuery(id+"F2.wireOp",EDGE,"E3.4.6.2"),sQuery(id+"F2.wireOp",EDGE,"E3.4.6.3"),sQuery(id+"F2.wireOp",EDGE,"E3.4.7.0"),sQuery(id+"F2.wireOp",EDGE,"E3.4.7.1"),sQuery(id+"F2.wireOp",EDGE,"E3.4.7.2"),sQuery(id+"F2.wireOp",EDGE,"E3.4.7.3"),sQuery(id+"F2.wireOp",EDGE,"E3.4.8.0"),sQuery(id+"F2.wireOp",EDGE,"E3.4.8.1"),sQuery(id+"F2.wireOp",EDGE,"E3.4.8.2"),sQuery(id+"F2.wireOp",EDGE,"E3.4.8.3"),sQuery(id+"F2.wireOp",EDGE,"E3.4.9.0"),sQuery(id+"F2.wireOp",EDGE,"E3.4.9.1"),sQuery(id+"F2.wireOp",EDGE,"E3.4.9.2"),sQuery(id+"F2.wireOp",EDGE,"E3.4.9.3"),sQuery(id+"F2.wireOp",EDGE,"E3.4.10.0"),sQuery(id+"F2.wireOp",EDGE,"E3.4.10.1"),sQuery(id+"F2.wireOp",EDGE,"E3.4.10.2"),sQuery(id+"F2.wireOp",EDGE,"E3.4.10.3"),sQuery(id+"F2.wireOp",EDGE,"E3.4.11.0"),sQuery(id+"F2.wireOp",EDGE,"E3.4.11.1"),sQuery(id+"F2.wireOp",EDGE,"E3.4.11.2"),sQuery(id+"F2.wireOp",EDGE,"E3.4.11.3"),sQuery(id+"F2.wireOp",EDGE,"E3.4.12.0"),sQuery(id+"F2.wireOp",EDGE,"E3.4.12.1"),sQuery(id+"F2.wireOp",EDGE,"E3.4.12.2"),sQuery(id+"F2.wireOp",EDGE,"E3.4.12.3"),sQuery(id+"F2.wireOp",EDGE,"E3.4.13.0"),sQuery(id+"F2.wireOp",EDGE,"E3.4.13.1"),sQuery(id+"F2.wireOp",EDGE,"E3.4.13.2"),sQuery(id+"F2.wireOp",EDGE,"E3.4.13.3"),sQuery(id+"F2.wireOp",EDGE,"E3.4.14.0"),sQuery(id+"F2.wireOp",EDGE,"E3.4.14.1"),sQuery(id+"F2.wireOp",EDGE,"E3.4.14.2"),sQuery(id+"F2.wireOp",EDGE,"E3.4.14.3"),sQuery(id+"F2.wireOp",EDGE,"E3.4.15.0"),sQuery(id+"F2.wireOp",EDGE,"E3.4.15.1"),sQuery(id+"F2.wireOp",EDGE,"E3.4.15.2"),sQuery(id+"F2.wireOp",EDGE,"E3.4.15.3"),sQuery(id+"F2.wireOp",EDGE,"E3.4.16.0"),sQuery(id+"F2.wireOp",EDGE,"E3.4.16.1"),sQuery(id+"F2.wireOp",EDGE,"E3.4.16.2"),sQuery(id+"F2.wireOp",EDGE,"E3.4.16.3"),sQuery(id+"F2.wireOp",EDGE,"E3.4.17.0"),sQuery(id+"F2.wireOp",EDGE,"E3.4.17.1"),sQuery(id+"F2.wireOp",EDGE,"E3.4.17.2"),sQuery(id+"F2.wireOp",EDGE,"E3.4.17.3"),sQuery(id+"F2.wireOp",EDGE,"E3.4.18.0"),sQuery(id+"F2.wireOp",EDGE,"E3.4.18.1"),sQuery(id+"F2.wireOp",EDGE,"E3.4.18.2"),sQuery(id+"F2.wireOp",EDGE,"E3.4.18.3"),sQuery(id+"F2.wireOp",EDGE,"E3.4.19.0"),sQuery(id+"F2.wireOp",EDGE,"E3.4.19.1"),sQuery(id+"F2.wireOp",EDGE,"E3.4.19.2"),sQuery(id+"F2.wireOp",EDGE,"E3.4.19.3"),sQuery(id+"F2.wireOp",EDGE,"E3.4.20.0"),sQuery(id+"F2.wireOp",EDGE,"E3.4.20.1"),sQuery(id+"F2.wireOp",EDGE,"E3.4.20.2"),sQuery(id+"F2.wireOp",EDGE,"E3.4.20.3"),sQuery(id+"F2.wireOp",EDGE,"E3.4.21.0"),sQuery(id+"F2.wireOp",EDGE,"E3.4.21.1"),sQuery(id+"F2.wireOp",EDGE,"E3.4.21.2"),sQuery(id+"F2.wireOp",EDGE,"E3.4.21.3"),sQuery(id+"F2.wireOp",EDGE,"E3.5.0.0"),sQuery(id+"F2.wireOp",EDGE,"E3.5.0.1"),sQuery(id+"F2.wireOp",EDGE,"E3.5.0.2"),sQuery(id+"F2.wireOp",EDGE,"E3.5.0.3"),sQuery(id+"F2.wireOp",EDGE,"E3.5.1.0"),sQuery(id+"F2.wireOp",EDGE,"E3.5.1.1"),sQuery(id+"F2.wireOp",EDGE,"E3.5.1.2"),sQuery(id+"F2.wireOp",EDGE,"E3.5.1.3"),sQuery(id+"F2.wireOp",EDGE,"E3.5.2.0"),sQuery(id+"F2.wireOp",EDGE,"E3.5.2.1"),sQuery(id+"F2.wireOp",EDGE,"E3.5.2.2"),sQuery(id+"F2.wireOp",EDGE,"E3.5.2.3"),sQuery(id+"F2.wireOp",EDGE,"E3.5.3.0"),sQuery(id+"F2.wireOp",EDGE,"E3.5.3.1"),sQuery(id+"F2.wireOp",EDGE,"E3.5.3.2"),sQuery(id+"F2.wireOp",EDGE,"E3.5.3.3"),sQuery(id+"F2.wireOp",EDGE,"E3.5.4.0"),sQuery(id+"F2.wireOp",EDGE,"E3.5.4.1"),sQuery(id+"F2.wireOp",EDGE,"E3.5.4.2"),sQuery(id+"F2.wireOp",EDGE,"E3.5.4.3"),sQuery(id+"F2.wireOp",EDGE,"E3.5.5.0"),sQuery(id+"F2.wireOp",EDGE,"E3.5.5.1"),sQuery(id+"F2.wireOp",EDGE,"E3.5.5.2"),sQuery(id+"F2.wireOp",EDGE,"E3.5.5.3"),sQuery(id+"F2.wireOp",EDGE,"E3.5.6.0"),sQuery(id+"F2.wireOp",EDGE,"E3.5.6.1"),sQuery(id+"F2.wireOp",EDGE,"E3.5.6.2"),sQuery(id+"F2.wireOp",EDGE,"E3.5.6.3"),sQuery(id+"F2.wireOp",EDGE,"E3.5.7.0"),sQuery(id+"F2.wireOp",EDGE,"E3.5.7.1"),sQuery(id+"F2.wireOp",EDGE,"E3.5.7.2"),sQuery(id+"F2.wireOp",EDGE,"E3.5.7.3"),sQuery(id+"F2.wireOp",EDGE,"E3.5.8.0"),sQuery(id+"F2.wireOp",EDGE,"E3.5.8.1"),sQuery(id+"F2.wireOp",EDGE,"E3.5.8.2"),sQuery(id+"F2.wireOp",EDGE,"E3.5.8.3"),sQuery(id+"F2.wireOp",EDGE,"E3.5.9.0"),sQuery(id+"F2.wireOp",EDGE,"E3.5.9.1"),sQuery(id+"F2.wireOp",EDGE,"E3.5.9.2"),sQuery(id+"F2.wireOp",EDGE,"E3.5.9.3"),sQuery(id+"F2.wireOp",EDGE,"E3.5.10.0"),sQuery(id+"F2.wireOp",EDGE,"E3.5.10.1"),sQuery(id+"F2.wireOp",EDGE,"E3.5.10.2"),sQuery(id+"F2.wireOp",EDGE,"E3.5.10.3"),sQuery(id+"F2.wireOp",EDGE,"E3.5.11.0"),sQuery(id+"F2.wireOp",EDGE,"E3.5.11.1"),sQuery(id+"F2.wireOp",EDGE,"E3.5.11.2"),sQuery(id+"F2.wireOp",EDGE,"E3.5.11.3"),sQuery(id+"F2.wireOp",EDGE,"E3.5.12.0"),sQuery(id+"F2.wireOp",EDGE,"E3.5.12.1"),sQuery(id+"F2.wireOp",EDGE,"E3.5.12.2"),sQuery(id+"F2.wireOp",EDGE,"E3.5.12.3"),sQuery(id+"F2.wireOp",EDGE,"E3.5.13.0"),sQuery(id+"F2.wireOp",EDGE,"E3.5.13.1"),sQuery(id+"F2.wireOp",EDGE,"E3.5.13.2"),sQuery(id+"F2.wireOp",EDGE,"E3.5.13.3"),sQuery(id+"F2.wireOp",EDGE,"E3.5.14.0"),sQuery(id+"F2.wireOp",EDGE,"E3.5.14.1"),sQuery(id+"F2.wireOp",EDGE,"E3.5.14.2"),sQuery(id+"F2.wireOp",EDGE,"E3.5.14.3"),sQuery(id+"F2.wireOp",EDGE,"E3.5.15.0"),sQuery(id+"F2.wireOp",EDGE,"E3.5.15.1"),sQuery(id+"F2.wireOp",EDGE,"E3.5.15.2"),sQuery(id+"F2.wireOp",EDGE,"E3.5.15.3"),sQuery(id+"F2.wireOp",EDGE,"E3.5.16.0"),sQuery(id+"F2.wireOp",EDGE,"E3.5.16.1"),sQuery(id+"F2.wireOp",EDGE,"E3.5.16.2"),sQuery(id+"F2.wireOp",EDGE,"E3.5.16.3"),sQuery(id+"F2.wireOp",EDGE,"E3.5.17.0"),sQuery(id+"F2.wireOp",EDGE,"E3.5.17.1"),sQuery(id+"F2.wireOp",EDGE,"E3.5.17.2"),sQuery(id+"F2.wireOp",EDGE,"E3.5.17.3"),sQuery(id+"F2.wireOp",EDGE,"E3.5.18.0"),sQuery(id+"F2.wireOp",EDGE,"E3.5.18.1"),sQuery(id+"F2.wireOp",EDGE,"E3.5.18.2"),sQuery(id+"F2.wireOp",EDGE,"E3.5.18.3"),sQuery(id+"F2.wireOp",EDGE,"E3.5.19.0"),sQuery(id+"F2.wireOp",EDGE,"E3.5.19.1"),sQuery(id+"F2.wireOp",EDGE,"E3.5.19.2"),sQuery(id+"F2.wireOp",EDGE,"E3.5.19.3"),sQuery(id+"F2.wireOp",EDGE,"E3.5.20.0"),sQuery(id+"F2.wireOp",EDGE,"E3.5.20.1"),sQuery(id+"F2.wireOp",EDGE,"E3.5.20.2"),sQuery(id+"F2.wireOp",EDGE,"E3.5.20.3"),sQuery(id+"F2.wireOp",EDGE,"E3.5.21.0"),sQuery(id+"F2.wireOp",EDGE,"E3.5.21.1"),sQuery(id+"F2.wireOp",EDGE,"E3.5.21.2"),sQuery(id+"F2.wireOp",EDGE,"E3.5.21.3"),sQuery(id+"F2.wireOp",EDGE,"E3.6.0.0"),sQuery(id+"F2.wireOp",EDGE,"E3.6.0.1"),sQuery(id+"F2.wireOp",EDGE,"E3.6.0.2"),sQuery(id+"F2.wireOp",EDGE,"E3.6.0.3"),sQuery(id+"F2.wireOp",EDGE,"E3.6.1.0"),sQuery(id+"F2.wireOp",EDGE,"E3.6.1.1"),sQuery(id+"F2.wireOp",EDGE,"E3.6.1.2"),sQuery(id+"F2.wireOp",EDGE,"E3.6.1.3"),sQuery(id+"F2.wireOp",EDGE,"E3.6.2.0"),sQuery(id+"F2.wireOp",EDGE,"E3.6.2.1"),sQuery(id+"F2.wireOp",EDGE,"E3.6.2.2"),sQuery(id+"F2.wireOp",EDGE,"E3.6.2.3"),sQuery(id+"F2.wireOp",EDGE,"E3.6.3.0"),sQuery(id+"F2.wireOp",EDGE,"E3.6.3.1"),sQuery(id+"F2.wireOp",EDGE,"E3.6.3.2"),sQuery(id+"F2.wireOp",EDGE,"E3.6.3.3"),sQuery(id+"F2.wireOp",EDGE,"E3.6.4.0"),sQuery(id+"F2.wireOp",EDGE,"E3.6.4.1"),sQuery(id+"F2.wireOp",EDGE,"E3.6.4.2"),sQuery(id+"F2.wireOp",EDGE,"E3.6.4.3"),sQuery(id+"F2.wireOp",EDGE,"E3.6.5.0"),sQuery(id+"F2.wireOp",EDGE,"E3.6.5.1"),sQuery(id+"F2.wireOp",EDGE,"E3.6.5.2"),sQuery(id+"F2.wireOp",EDGE,"E3.6.5.3"),sQuery(id+"F2.wireOp",EDGE,"E3.6.6.0"),sQuery(id+"F2.wireOp",EDGE,"E3.6.6.1"),sQuery(id+"F2.wireOp",EDGE,"E3.6.6.2"),sQuery(id+"F2.wireOp",EDGE,"E3.6.6.3"),sQuery(id+"F2.wireOp",EDGE,"E3.6.7.0"),sQuery(id+"F2.wireOp",EDGE,"E3.6.7.1"),sQuery(id+"F2.wireOp",EDGE,"E3.6.7.2"),sQuery(id+"F2.wireOp",EDGE,"E3.6.7.3"),sQuery(id+"F2.wireOp",EDGE,"E3.6.8.0"),sQuery(id+"F2.wireOp",EDGE,"E3.6.8.1"),sQuery(id+"F2.wireOp",EDGE,"E3.6.8.2"),sQuery(id+"F2.wireOp",EDGE,"E3.6.8.3"),sQuery(id+"F2.wireOp",EDGE,"E3.6.9.0"),sQuery(id+"F2.wireOp",EDGE,"E3.6.9.1"),sQuery(id+"F2.wireOp",EDGE,"E3.6.9.2"),sQuery(id+"F2.wireOp",EDGE,"E3.6.9.3"),sQuery(id+"F2.wireOp",EDGE,"E3.6.10.0"),sQuery(id+"F2.wireOp",EDGE,"E3.6.10.1"),sQuery(id+"F2.wireOp",EDGE,"E3.6.10.2"),sQuery(id+"F2.wireOp",EDGE,"E3.6.10.3"),sQuery(id+"F2.wireOp",EDGE,"E3.6.11.0"),sQuery(id+"F2.wireOp",EDGE,"E3.6.11.1"),sQuery(id+"F2.wireOp",EDGE,"E3.6.11.2"),sQuery(id+"F2.wireOp",EDGE,"E3.6.11.3"),sQuery(id+"F2.wireOp",EDGE,"E3.6.12.0"),sQuery(id+"F2.wireOp",EDGE,"E3.6.12.1"),sQuery(id+"F2.wireOp",EDGE,"E3.6.12.2"),sQuery(id+"F2.wireOp",EDGE,"E3.6.12.3"),sQuery(id+"F2.wireOp",EDGE,"E3.6.13.0"),sQuery(id+"F2.wireOp",EDGE,"E3.6.13.1"),sQuery(id+"F2.wireOp",EDGE,"E3.6.13.2"),sQuery(id+"F2.wireOp",EDGE,"E3.6.13.3"),sQuery(id+"F2.wireOp",EDGE,"E3.6.14.0"),sQuery(id+"F2.wireOp",EDGE,"E3.6.14.1"),sQuery(id+"F2.wireOp",EDGE,"E3.6.14.2"),sQuery(id+"F2.wireOp",EDGE,"E3.6.14.3"),sQuery(id+"F2.wireOp",EDGE,"E3.6.15.0"),sQuery(id+"F2.wireOp",EDGE,"E3.6.15.1"),sQuery(id+"F2.wireOp",EDGE,"E3.6.15.2"),sQuery(id+"F2.wireOp",EDGE,"E3.6.15.3"),sQuery(id+"F2.wireOp",EDGE,"E3.6.16.0"),sQuery(id+"F2.wireOp",EDGE,"E3.6.16.1"),sQuery(id+"F2.wireOp",EDGE,"E3.6.16.2"),sQuery(id+"F2.wireOp",EDGE,"E3.6.16.3"),sQuery(id+"F2.wireOp",EDGE,"E3.6.17.0"),sQuery(id+"F2.wireOp",EDGE,"E3.6.17.1"),sQuery(id+"F2.wireOp",EDGE,"E3.6.17.2"),sQuery(id+"F2.wireOp",EDGE,"E3.6.17.3"),sQuery(id+"F2.wireOp",EDGE,"E3.6.18.0"),sQuery(id+"F2.wireOp",EDGE,"E3.6.18.1"),sQuery(id+"F2.wireOp",EDGE,"E3.6.18.2"),sQuery(id+"F2.wireOp",EDGE,"E3.6.18.3"),sQuery(id+"F2.wireOp",EDGE,"E3.6.19.0"),sQuery(id+"F2.wireOp",EDGE,"E3.6.19.1"),sQuery(id+"F2.wireOp",EDGE,"E3.6.19.2"),sQuery(id+"F2.wireOp",EDGE,"E3.6.19.3"),sQuery(id+"F2.wireOp",EDGE,"E3.6.20.0"),sQuery(id+"F2.wireOp",EDGE,"E3.6.20.1"),sQuery(id+"F2.wireOp",EDGE,"E3.6.20.2"),sQuery(id+"F2.wireOp",EDGE,"E3.6.20.3"),sQuery(id+"F2.wireOp",EDGE,"E3.6.21.0"),sQuery(id+"F2.wireOp",EDGE,"E3.6.21.1"),sQuery(id+"F2.wireOp",EDGE,"E3.6.21.2"),sQuery(id+"F2.wireOp",EDGE,"E3.6.21.3"),sQuery(id+"F2.wireOp",EDGE,"E3.7.0.0"),sQuery(id+"F2.wireOp",EDGE,"E3.7.0.1"),sQuery(id+"F2.wireOp",EDGE,"E3.7.0.2"),sQuery(id+"F2.wireOp",EDGE,"E3.7.0.3"),sQuery(id+"F2.wireOp",EDGE,"E3.7.1.0"),sQuery(id+"F2.wireOp",EDGE,"E3.7.1.1"),sQuery(id+"F2.wireOp",EDGE,"E3.7.1.2"),sQuery(id+"F2.wireOp",EDGE,"E3.7.1.3"),sQuery(id+"F2.wireOp",EDGE,"E3.7.2.0"),sQuery(id+"F2.wireOp",EDGE,"E3.7.2.1"),sQuery(id+"F2.wireOp",EDGE,"E3.7.2.2"),sQuery(id+"F2.wireOp",EDGE,"E3.7.2.3"),sQuery(id+"F2.wireOp",EDGE,"E3.7.3.0"),sQuery(id+"F2.wireOp",EDGE,"E3.7.3.1"),sQuery(id+"F2.wireOp",EDGE,"E3.7.3.2"),sQuery(id+"F2.wireOp",EDGE,"E3.7.3.3"),sQuery(id+"F2.wireOp",EDGE,"E3.7.4.0"),sQuery(id+"F2.wireOp",EDGE,"E3.7.4.1"),sQuery(id+"F2.wireOp",EDGE,"E3.7.4.2"),sQuery(id+"F2.wireOp",EDGE,"E3.7.4.3"),sQuery(id+"F2.wireOp",EDGE,"E3.7.5.0"),sQuery(id+"F2.wireOp",EDGE,"E3.7.5.1"),sQuery(id+"F2.wireOp",EDGE,"E3.7.5.2"),sQuery(id+"F2.wireOp",EDGE,"E3.7.5.3"),sQuery(id+"F2.wireOp",EDGE,"E3.7.6.0"),sQuery(id+"F2.wireOp",EDGE,"E3.7.6.1"),sQuery(id+"F2.wireOp",EDGE,"E3.7.6.2"),sQuery(id+"F2.wireOp",EDGE,"E3.7.6.3"),sQuery(id+"F2.wireOp",EDGE,"E3.7.7.0"),sQuery(id+"F2.wireOp",EDGE,"E3.7.7.1"),sQuery(id+"F2.wireOp",EDGE,"E3.7.7.2"),sQuery(id+"F2.wireOp",EDGE,"E3.7.7.3"),sQuery(id+"F2.wireOp",EDGE,"E3.7.8.0"),sQuery(id+"F2.wireOp",EDGE,"E3.7.8.1"),sQuery(id+"F2.wireOp",EDGE,"E3.7.8.2"),sQuery(id+"F2.wireOp",EDGE,"E3.7.8.3"),sQuery(id+"F2.wireOp",EDGE,"E3.7.9.0"),sQuery(id+"F2.wireOp",EDGE,"E3.7.9.1"),sQuery(id+"F2.wireOp",EDGE,"E3.7.9.2"),sQuery(id+"F2.wireOp",EDGE,"E3.7.9.3"),sQuery(id+"F2.wireOp",EDGE,"E3.7.10.0"),sQuery(id+"F2.wireOp",EDGE,"E3.7.10.1"),sQuery(id+"F2.wireOp",EDGE,"E3.7.10.2"),sQuery(id+"F2.wireOp",EDGE,"E3.7.10.3"),sQuery(id+"F2.wireOp",EDGE,"E3.7.11.0"),sQuery(id+"F2.wireOp",EDGE,"E3.7.11.1"),sQuery(id+"F2.wireOp",EDGE,"E3.7.11.2"),sQuery(id+"F2.wireOp",EDGE,"E3.7.11.3"),sQuery(id+"F2.wireOp",EDGE,"E3.7.12.0"),sQuery(id+"F2.wireOp",EDGE,"E3.7.12.1"),sQuery(id+"F2.wireOp",EDGE,"E3.7.12.2"),sQuery(id+"F2.wireOp",EDGE,"E3.7.12.3"),sQuery(id+"F2.wireOp",EDGE,"E3.7.13.0"),sQuery(id+"F2.wireOp",EDGE,"E3.7.13.1"),sQuery(id+"F2.wireOp",EDGE,"E3.7.13.2"),sQuery(id+"F2.wireOp",EDGE,"E3.7.13.3"),sQuery(id+"F2.wireOp",EDGE,"E3.7.14.0"),sQuery(id+"F2.wireOp",EDGE,"E3.7.14.1"),sQuery(id+"F2.wireOp",EDGE,"E3.7.14.2"),sQuery(id+"F2.wireOp",EDGE,"E3.7.14.3"),sQuery(id+"F2.wireOp",EDGE,"E3.7.15.0"),sQuery(id+"F2.wireOp",EDGE,"E3.7.15.1"),sQuery(id+"F2.wireOp",EDGE,"E3.7.15.2"),sQuery(id+"F2.wireOp",EDGE,"E3.7.15.3"),sQuery(id+"F2.wireOp",EDGE,"E3.7.16.0"),sQuery(id+"F2.wireOp",EDGE,"E3.7.16.1"),sQuery(id+"F2.wireOp",EDGE,"E3.7.16.2"),sQuery(id+"F2.wireOp",EDGE,"E3.7.16.3"),sQuery(id+"F2.wireOp",EDGE,"E3.7.17.0"),sQuery(id+"F2.wireOp",EDGE,"E3.7.17.1"),sQuery(id+"F2.wireOp",EDGE,"E3.7.17.2"),sQuery(id+"F2.wireOp",EDGE,"E3.7.17.3"),sQuery(id+"F2.wireOp",EDGE,"E3.7.18.0"),sQuery(id+"F2.wireOp",EDGE,"E3.7.18.1"),sQuery(id+"F2.wireOp",EDGE,"E3.7.18.2"),sQuery(id+"F2.wireOp",EDGE,"E3.7.18.3"),sQuery(id+"F2.wireOp",EDGE,"E3.7.19.0"),sQuery(id+"F2.wireOp",EDGE,"E3.7.19.1"),sQuery(id+"F2.wireOp",EDGE,"E3.7.19.2"),sQuery(id+"F2.wireOp",EDGE,"E3.7.19.3"),sQuery(id+"F2.wireOp",EDGE,"E3.7.20.0"),sQuery(id+"F2.wireOp",EDGE,"E3.7.20.1"),sQuery(id+"F2.wireOp",EDGE,"E3.7.20.2"),sQuery(id+"F2.wireOp",EDGE,"E3.7.20.3"),sQuery(id+"F2.wireOp",EDGE,"E3.7.21.0"),sQuery(id+"F2.wireOp",EDGE,"E3.7.21.1"),sQuery(id+"F2.wireOp",EDGE,"E3.7.21.2"),sQuery(id+"F2.wireOp",EDGE,"E3.7.21.3"),sQuery(id+"F2.wireOp",EDGE,"E3.8.0.0"),sQuery(id+"F2.wireOp",EDGE,"E3.8.0.1"),sQuery(id+"F2.wireOp",EDGE,"E3.8.0.2"),sQuery(id+"F2.wireOp",EDGE,"E3.8.0.3"),sQuery(id+"F2.wireOp",EDGE,"E3.8.1.0"),sQuery(id+"F2.wireOp",EDGE,"E3.8.1.1"),sQuery(id+"F2.wireOp",EDGE,"E3.8.1.2"),sQuery(id+"F2.wireOp",EDGE,"E3.8.1.3"),sQuery(id+"F2.wireOp",EDGE,"E3.8.2.0"),sQuery(id+"F2.wireOp",EDGE,"E3.8.2.1"),sQuery(id+"F2.wireOp",EDGE,"E3.8.2.2"),sQuery(id+"F2.wireOp",EDGE,"E3.8.2.3"),sQuery(id+"F2.wireOp",EDGE,"E3.8.3.0"),sQuery(id+"F2.wireOp",EDGE,"E3.8.3.1"),sQuery(id+"F2.wireOp",EDGE,"E3.8.3.2"),sQuery(id+"F2.wireOp",EDGE,"E3.8.3.3"),sQuery(id+"F2.wireOp",EDGE,"E3.8.4.0"),sQuery(id+"F2.wireOp",EDGE,"E3.8.4.1"),sQuery(id+"F2.wireOp",EDGE,"E3.8.4.2"),sQuery(id+"F2.wireOp",EDGE,"E3.8.4.3"),sQuery(id+"F2.wireOp",EDGE,"E3.8.5.0"),sQuery(id+"F2.wireOp",EDGE,"E3.8.5.1"),sQuery(id+"F2.wireOp",EDGE,"E3.8.5.2"),sQuery(id+"F2.wireOp",EDGE,"E3.8.5.3"),sQuery(id+"F2.wireOp",EDGE,"E3.8.6.0"),sQuery(id+"F2.wireOp",EDGE,"E3.8.6.1"),sQuery(id+"F2.wireOp",EDGE,"E3.8.6.2"),sQuery(id+"F2.wireOp",EDGE,"E3.8.6.3"),sQuery(id+"F2.wireOp",EDGE,"E3.8.7.0"),sQuery(id+"F2.wireOp",EDGE,"E3.8.7.1"),sQuery(id+"F2.wireOp",EDGE,"E3.8.7.2"),sQuery(id+"F2.wireOp",EDGE,"E3.8.7.3"),sQuery(id+"F2.wireOp",EDGE,"E3.8.8.0"),sQuery(id+"F2.wireOp",EDGE,"E3.8.8.1"),sQuery(id+"F2.wireOp",EDGE,"E3.8.8.2"),sQuery(id+"F2.wireOp",EDGE,"E3.8.8.3"),sQuery(id+"F2.wireOp",EDGE,"E3.8.9.0"),sQuery(id+"F2.wireOp",EDGE,"E3.8.9.1"),sQuery(id+"F2.wireOp",EDGE,"E3.8.9.2"),sQuery(id+"F2.wireOp",EDGE,"E3.8.9.3"),sQuery(id+"F2.wireOp",EDGE,"E3.8.10.0"),sQuery(id+"F2.wireOp",EDGE,"E3.8.10.1"),sQuery(id+"F2.wireOp",EDGE,"E3.8.10.2"),sQuery(id+"F2.wireOp",EDGE,"E3.8.10.3"),sQuery(id+"F2.wireOp",EDGE,"E3.8.11.0"),sQuery(id+"F2.wireOp",EDGE,"E3.8.11.1"),sQuery(id+"F2.wireOp",EDGE,"E3.8.11.2"),sQuery(id+"F2.wireOp",EDGE,"E3.8.11.3"),sQuery(id+"F2.wireOp",EDGE,"E3.8.12.0"),sQuery(id+"F2.wireOp",EDGE,"E3.8.12.1"),sQuery(id+"F2.wireOp",EDGE,"E3.8.12.2"),sQuery(id+"F2.wireOp",EDGE,"E3.8.12.3"),sQuery(id+"F2.wireOp",EDGE,"E3.8.13.0"),sQuery(id+"F2.wireOp",EDGE,"E3.8.13.1"),sQuery(id+"F2.wireOp",EDGE,"E3.8.13.2"),sQuery(id+"F2.wireOp",EDGE,"E3.8.13.3"),sQuery(id+"F2.wireOp",EDGE,"E3.8.14.0"),sQuery(id+"F2.wireOp",EDGE,"E3.8.14.1"),sQuery(id+"F2.wireOp",EDGE,"E3.8.14.2"),sQuery(id+"F2.wireOp",EDGE,"E3.8.14.3"),sQuery(id+"F2.wireOp",EDGE,"E3.8.15.0"),sQuery(id+"F2.wireOp",EDGE,"E3.8.15.1"),sQuery(id+"F2.wireOp",EDGE,"E3.8.15.2"),sQuery(id+"F2.wireOp",EDGE,"E3.8.15.3"),sQuery(id+"F2.wireOp",EDGE,"E3.8.16.0"),sQuery(id+"F2.wireOp",EDGE,"E3.8.16.1"),sQuery(id+"F2.wireOp",EDGE,"E3.8.16.2"),sQuery(id+"F2.wireOp",EDGE,"E3.8.16.3"),sQuery(id+"F2.wireOp",EDGE,"E3.8.17.0"),sQuery(id+"F2.wireOp",EDGE,"E3.8.17.1"),sQuery(id+"F2.wireOp",EDGE,"E3.8.17.2"),sQuery(id+"F2.wireOp",EDGE,"E3.8.17.3"),sQuery(id+"F2.wireOp",EDGE,"E3.8.18.0"),sQuery(id+"F2.wireOp",EDGE,"E3.8.18.1"),sQuery(id+"F2.wireOp",EDGE,"E3.8.18.2"),sQuery(id+"F2.wireOp",EDGE,"E3.8.18.3"),sQuery(id+"F2.wireOp",EDGE,"E3.8.19.0"),sQuery(id+"F2.wireOp",EDGE,"E3.8.19.1"),sQuery(id+"F2.wireOp",EDGE,"E3.8.19.2"),sQuery(id+"F2.wireOp",EDGE,"E3.8.19.3"),sQuery(id+"F2.wireOp",EDGE,"E3.8.20.0"),sQuery(id+"F2.wireOp",EDGE,"E3.8.20.1"),sQuery(id+"F2.wireOp",EDGE,"E3.8.20.2"),sQuery(id+"F2.wireOp",EDGE,"E3.8.20.3"),sQuery(id+"F2.wireOp",EDGE,"E3.8.21.0"),sQuery(id+"F2.wireOp",EDGE,"E3.8.21.1"),sQuery(id+"F2.wireOp",EDGE,"E3.8.21.2"),sQuery(id+"F2.wireOp",EDGE,"E3.8.21.3"),sQuery(id+"F2.wireOp",EDGE,"E3.9.0.0"),sQuery(id+"F2.wireOp",EDGE,"E3.9.0.1"),sQuery(id+"F2.wireOp",EDGE,"E3.9.0.2"),sQuery(id+"F2.wireOp",EDGE,"E3.9.0.3"),sQuery(id+"F2.wireOp",EDGE,"E3.9.1.0"),sQuery(id+"F2.wireOp",EDGE,"E3.9.1.1"),sQuery(id+"F2.wireOp",EDGE,"E3.9.1.2"),sQuery(id+"F2.wireOp",EDGE,"E3.9.1.3"),sQuery(id+"F2.wireOp",EDGE,"E3.9.2.0"),sQuery(id+"F2.wireOp",EDGE,"E3.9.2.1"),sQuery(id+"F2.wireOp",EDGE,"E3.9.2.2"),sQuery(id+"F2.wireOp",EDGE,"E3.9.2.3"),sQuery(id+"F2.wireOp",EDGE,"E3.9.3.0"),sQuery(id+"F2.wireOp",EDGE,"E3.9.3.1"),sQuery(id+"F2.wireOp",EDGE,"E3.9.3.2"),sQuery(id+"F2.wireOp",EDGE,"E3.9.3.3"),sQuery(id+"F2.wireOp",EDGE,"E3.9.4.0"),sQuery(id+"F2.wireOp",EDGE,"E3.9.4.1"),sQuery(id+"F2.wireOp",EDGE,"E3.9.4.2"),sQuery(id+"F2.wireOp",EDGE,"E3.9.4.3"),sQuery(id+"F2.wireOp",EDGE,"E3.9.5.0"),sQuery(id+"F2.wireOp",EDGE,"E3.9.5.1"),sQuery(id+"F2.wireOp",EDGE,"E3.9.5.2"),sQuery(id+"F2.wireOp",EDGE,"E3.9.5.3"),sQuery(id+"F2.wireOp",EDGE,"E3.9.6.0"),sQuery(id+"F2.wireOp",EDGE,"E3.9.6.1"),sQuery(id+"F2.wireOp",EDGE,"E3.9.6.2"),sQuery(id+"F2.wireOp",EDGE,"E3.9.6.3"),sQuery(id+"F2.wireOp",EDGE,"E3.9.7.0"),sQuery(id+"F2.wireOp",EDGE,"E3.9.7.1"),sQuery(id+"F2.wireOp",EDGE,"E3.9.7.2"),sQuery(id+"F2.wireOp",EDGE,"E3.9.7.3"),sQuery(id+"F2.wireOp",EDGE,"E3.9.8.0"),sQuery(id+"F2.wireOp",EDGE,"E3.9.8.1"),sQuery(id+"F2.wireOp",EDGE,"E3.9.8.2"),sQuery(id+"F2.wireOp",EDGE,"E3.9.8.3"),sQuery(id+"F2.wireOp",EDGE,"E3.9.9.0"),sQuery(id+"F2.wireOp",EDGE,"E3.9.9.1"),sQuery(id+"F2.wireOp",EDGE,"E3.9.9.2"),sQuery(id+"F2.wireOp",EDGE,"E3.9.9.3"),sQuery(id+"F2.wireOp",EDGE,"E3.9.10.0"),sQuery(id+"F2.wireOp",EDGE,"E3.9.10.1"),sQuery(id+"F2.wireOp",EDGE,"E3.9.10.2"),sQuery(id+"F2.wireOp",EDGE,"E3.9.10.3"),sQuery(id+"F2.wireOp",EDGE,"E3.9.11.0"),sQuery(id+"F2.wireOp",EDGE,"E3.9.11.1"),sQuery(id+"F2.wireOp",EDGE,"E3.9.11.2"),sQuery(id+"F2.wireOp",EDGE,"E3.9.11.3"),sQuery(id+"F2.wireOp",EDGE,"E3.9.12.0"),sQuery(id+"F2.wireOp",EDGE,"E3.9.12.1"),sQuery(id+"F2.wireOp",EDGE,"E3.9.12.2"),sQuery(id+"F2.wireOp",EDGE,"E3.9.12.3"),sQuery(id+"F2.wireOp",EDGE,"E3.9.13.0"),sQuery(id+"F2.wireOp",EDGE,"E3.9.13.1"),sQuery(id+"F2.wireOp",EDGE,"E3.9.13.2"),sQuery(id+"F2.wireOp",EDGE,"E3.9.13.3"),sQuery(id+"F2.wireOp",EDGE,"E3.9.14.0"),sQuery(id+"F2.wireOp",EDGE,"E3.9.14.1"),sQuery(id+"F2.wireOp",EDGE,"E3.9.14.2"),sQuery(id+"F2.wireOp",EDGE,"E3.9.14.3"),sQuery(id+"F2.wireOp",EDGE,"E3.9.15.0"),sQuery(id+"F2.wireOp",EDGE,"E3.9.15.1"),sQuery(id+"F2.wireOp",EDGE,"E3.9.15.2"),sQuery(id+"F2.wireOp",EDGE,"E3.9.15.3"),sQuery(id+"F2.wireOp",EDGE,"E3.9.16.0"),sQuery(id+"F2.wireOp",EDGE,"E3.9.16.1"),sQuery(id+"F2.wireOp",EDGE,"E3.9.16.2"),sQuery(id+"F2.wireOp",EDGE,"E3.9.16.3"),sQuery(id+"F2.wireOp",EDGE,"E3.9.17.0"),sQuery(id+"F2.wireOp",EDGE,"E3.9.17.1"),sQuery(id+"F2.wireOp",EDGE,"E3.9.17.2"),sQuery(id+"F2.wireOp",EDGE,"E3.9.17.3"),sQuery(id+"F2.wireOp",EDGE,"E3.9.18.0"),sQuery(id+"F2.wireOp",EDGE,"E3.9.18.1"),sQuery(id+"F2.wireOp",EDGE,"E3.9.18.2"),sQuery(id+"F2.wireOp",EDGE,"E3.9.18.3"),sQuery(id+"F2.wireOp",EDGE,"E3.9.19.0"),sQuery(id+"F2.wireOp",EDGE,"E3.9.19.1"),sQuery(id+"F2.wireOp",EDGE,"E3.9.19.2"),sQuery(id+"F2.wireOp",EDGE,"E3.9.19.3"),sQuery(id+"F2.wireOp",EDGE,"E3.9.20.0"),sQuery(id+"F2.wireOp",EDGE,"E3.9.20.1"),sQuery(id+"F2.wireOp",EDGE,"E3.9.20.2"),sQuery(id+"F2.wireOp",EDGE,"E3.9.20.3"),sQuery(id+"F2.wireOp",EDGE,"E3.9.21.0"),sQuery(id+"F2.wireOp",EDGE,"E3.9.21.1"),sQuery(id+"F2.wireOp",EDGE,"E3.9.21.2"),sQuery(id+"F2.wireOp",EDGE,"E3.9.21.3"),sQuery(id+"F2.wireOp",EDGE,"E3.10.0.0"),sQuery(id+"F2.wireOp",EDGE,"E3.10.0.1"),sQuery(id+"F2.wireOp",EDGE,"E3.10.0.2"),sQuery(id+"F2.wireOp",EDGE,"E3.10.0.3"),sQuery(id+"F2.wireOp",EDGE,"E3.10.1.0"),sQuery(id+"F2.wireOp",EDGE,"E3.10.1.1"),sQuery(id+"F2.wireOp",EDGE,"E3.10.1.2"),sQuery(id+"F2.wireOp",EDGE,"E3.10.1.3"),sQuery(id+"F2.wireOp",EDGE,"E3.10.2.0"),sQuery(id+"F2.wireOp",EDGE,"E3.10.2.1"),sQuery(id+"F2.wireOp",EDGE,"E3.10.2.2"),sQuery(id+"F2.wireOp",EDGE,"E3.10.2.3"),sQuery(id+"F2.wireOp",EDGE,"E3.10.3.0"),sQuery(id+"F2.wireOp",EDGE,"E3.10.3.1"),sQuery(id+"F2.wireOp",EDGE,"E3.10.3.2"),sQuery(id+"F2.wireOp",EDGE,"E3.10.3.3"),sQuery(id+"F2.wireOp",EDGE,"E3.10.4.0"),sQuery(id+"F2.wireOp",EDGE,"E3.10.4.1"),sQuery(id+"F2.wireOp",EDGE,"E3.10.4.2"),sQuery(id+"F2.wireOp",EDGE,"E3.10.4.3"),sQuery(id+"F2.wireOp",EDGE,"E3.10.5.0"),sQuery(id+"F2.wireOp",EDGE,"E3.10.5.1"),sQuery(id+"F2.wireOp",EDGE,"E3.10.5.2"),sQuery(id+"F2.wireOp",EDGE,"E3.10.5.3"),sQuery(id+"F2.wireOp",EDGE,"E3.10.6.0"),sQuery(id+"F2.wireOp",EDGE,"E3.10.6.1"),sQuery(id+"F2.wireOp",EDGE,"E3.10.6.2"),sQuery(id+"F2.wireOp",EDGE,"E3.10.6.3"),sQuery(id+"F2.wireOp",EDGE,"E3.10.7.0"),sQuery(id+"F2.wireOp",EDGE,"E3.10.7.1"),sQuery(id+"F2.wireOp",EDGE,"E3.10.7.2"),sQuery(id+"F2.wireOp",EDGE,"E3.10.7.3"),sQuery(id+"F2.wireOp",EDGE,"E3.10.8.0"),sQuery(id+"F2.wireOp",EDGE,"E3.10.8.1"),sQuery(id+"F2.wireOp",EDGE,"E3.10.8.2"),sQuery(id+"F2.wireOp",EDGE,"E3.10.8.3"),sQuery(id+"F2.wireOp",EDGE,"E3.10.9.0"),sQuery(id+"F2.wireOp",EDGE,"E3.10.9.1"),sQuery(id+"F2.wireOp",EDGE,"E3.10.9.2"),sQuery(id+"F2.wireOp",EDGE,"E3.10.9.3"),sQuery(id+"F2.wireOp",EDGE,"E3.10.10.0"),sQuery(id+"F2.wireOp",EDGE,"E3.10.10.1"),sQuery(id+"F2.wireOp",EDGE,"E3.10.10.2"),sQuery(id+"F2.wireOp",EDGE,"E3.10.10.3"),sQuery(id+"F2.wireOp",EDGE,"E3.10.11.0"),sQuery(id+"F2.wireOp",EDGE,"E3.10.11.1"),sQuery(id+"F2.wireOp",EDGE,"E3.10.11.2"),sQuery(id+"F2.wireOp",EDGE,"E3.10.11.3"),sQuery(id+"F2.wireOp",EDGE,"E3.10.12.0"),sQuery(id+"F2.wireOp",EDGE,"E3.10.12.1"),sQuery(id+"F2.wireOp",EDGE,"E3.10.12.2"),sQuery(id+"F2.wireOp",EDGE,"E3.10.12.3"),sQuery(id+"F2.wireOp",EDGE,"E3.10.13.0"),sQuery(id+"F2.wireOp",EDGE,"E3.10.13.1"),sQuery(id+"F2.wireOp",EDGE,"E3.10.13.2"),sQuery(id+"F2.wireOp",EDGE,"E3.10.13.3"),sQuery(id+"F2.wireOp",EDGE,"E3.10.14.0"),sQuery(id+"F2.wireOp",EDGE,"E3.10.14.1"),sQuery(id+"F2.wireOp",EDGE,"E3.10.14.2"),sQuery(id+"F2.wireOp",EDGE,"E3.10.14.3"),sQuery(id+"F2.wireOp",EDGE,"E3.10.15.0"),sQuery(id+"F2.wireOp",EDGE,"E3.10.15.1"),sQuery(id+"F2.wireOp",EDGE,"E3.10.15.2"),sQuery(id+"F2.wireOp",EDGE,"E3.10.15.3"),sQuery(id+"F2.wireOp",EDGE,"E3.10.16.0"),sQuery(id+"F2.wireOp",EDGE,"E3.10.16.1"),sQuery(id+"F2.wireOp",EDGE,"E3.10.16.2"),sQuery(id+"F2.wireOp",EDGE,"E3.10.16.3"),sQuery(id+"F2.wireOp",EDGE,"E3.10.17.0"),sQuery(id+"F2.wireOp",EDGE,"E3.10.17.1"),sQuery(id+"F2.wireOp",EDGE,"E3.10.17.2"),sQuery(id+"F2.wireOp",EDGE,"E3.10.17.3"),sQuery(id+"F2.wireOp",EDGE,"E3.10.18.0"),sQuery(id+"F2.wireOp",EDGE,"E3.10.18.1"),sQuery(id+"F2.wireOp",EDGE,"E3.10.18.2"),sQuery(id+"F2.wireOp",EDGE,"E3.10.18.3"),sQuery(id+"F2.wireOp",EDGE,"E3.10.19.0"),sQuery(id+"F2.wireOp",EDGE,"E3.10.19.1"),sQuery(id+"F2.wireOp",EDGE,"E3.10.19.2"),sQuery(id+"F2.wireOp",EDGE,"E3.10.19.3"),sQuery(id+"F2.wireOp",EDGE,"E3.10.20.0"),sQuery(id+"F2.wireOp",EDGE,"E3.10.20.1"),sQuery(id+"F2.wireOp",EDGE,"E3.10.20.2"),sQuery(id+"F2.wireOp",EDGE,"E3.10.20.3"),sQuery(id+"F2.wireOp",EDGE,"E3.10.21.0"),sQuery(id+"F2.wireOp",EDGE,"E3.10.21.1"),sQuery(id+"F2.wireOp",EDGE,"E3.10.21.2"),sQuery(id+"F2.wireOp",EDGE,"E3.10.21.3"),sQuery(id+"F2.wireOp",EDGE,"E3.11.0.0"),sQuery(id+"F2.wireOp",EDGE,"E3.11.0.1"),sQuery(id+"F2.wireOp",EDGE,"E3.11.0.2"),sQuery(id+"F2.wireOp",EDGE,"E3.11.0.3"),sQuery(id+"F2.wireOp",EDGE,"E3.11.1.0"),sQuery(id+"F2.wireOp",EDGE,"E3.11.1.1"),sQuery(id+"F2.wireOp",EDGE,"E3.11.1.2"),sQuery(id+"F2.wireOp",EDGE,"E3.11.1.3"),sQuery(id+"F2.wireOp",EDGE,"E3.11.2.0"),sQuery(id+"F2.wireOp",EDGE,"E3.11.2.1"),sQuery(id+"F2.wireOp",EDGE,"E3.11.2.2"),sQuery(id+"F2.wireOp",EDGE,"E3.11.2.3"),sQuery(id+"F2.wireOp",EDGE,"E3.11.3.0"),sQuery(id+"F2.wireOp",EDGE,"E3.11.3.1"),sQuery(id+"F2.wireOp",EDGE,"E3.11.3.2"),sQuery(id+"F2.wireOp",EDGE,"E3.11.3.3"),sQuery(id+"F2.wireOp",EDGE,"E3.11.4.0"),sQuery(id+"F2.wireOp",EDGE,"E3.11.4.1"),sQuery(id+"F2.wireOp",EDGE,"E3.11.4.2"),sQuery(id+"F2.wireOp",EDGE,"E3.11.4.3"),sQuery(id+"F2.wireOp",EDGE,"E3.11.5.0"),sQuery(id+"F2.wireOp",EDGE,"E3.11.5.1"),sQuery(id+"F2.wireOp",EDGE,"E3.11.5.2"),sQuery(id+"F2.wireOp",EDGE,"E3.11.5.3"),sQuery(id+"F2.wireOp",EDGE,"E3.11.6.0"),sQuery(id+"F2.wireOp",EDGE,"E3.11.6.1"),sQuery(id+"F2.wireOp",EDGE,"E3.11.6.2"),sQuery(id+"F2.wireOp",EDGE,"E3.11.6.3"),sQuery(id+"F2.wireOp",EDGE,"E3.11.7.0"),sQuery(id+"F2.wireOp",EDGE,"E3.11.7.1"),sQuery(id+"F2.wireOp",EDGE,"E3.11.7.2"),sQuery(id+"F2.wireOp",EDGE,"E3.11.7.3"),sQuery(id+"F2.wireOp",EDGE,"E3.11.8.0"),sQuery(id+"F2.wireOp",EDGE,"E3.11.8.1"),sQuery(id+"F2.wireOp",EDGE,"E3.11.8.2"),sQuery(id+"F2.wireOp",EDGE,"E3.11.8.3"),sQuery(id+"F2.wireOp",EDGE,"E3.11.9.0"),sQuery(id+"F2.wireOp",EDGE,"E3.11.9.1"),sQuery(id+"F2.wireOp",EDGE,"E3.11.9.2"),sQuery(id+"F2.wireOp",EDGE,"E3.11.9.3"),sQuery(id+"F2.wireOp",EDGE,"E3.11.10.0"),sQuery(id+"F2.wireOp",EDGE,"E3.11.10.1"),sQuery(id+"F2.wireOp",EDGE,"E3.11.10.2"),sQuery(id+"F2.wireOp",EDGE,"E3.11.10.3"),sQuery(id+"F2.wireOp",EDGE,"E3.11.11.0"),sQuery(id+"F2.wireOp",EDGE,"E3.11.11.1"),sQuery(id+"F2.wireOp",EDGE,"E3.11.11.2"),sQuery(id+"F2.wireOp",EDGE,"E3.11.11.3"),sQuery(id+"F2.wireOp",EDGE,"E3.11.12.0"),sQuery(id+"F2.wireOp",EDGE,"E3.11.12.1"),sQuery(id+"F2.wireOp",EDGE,"E3.11.12.2"),sQuery(id+"F2.wireOp",EDGE,"E3.11.12.3"),sQuery(id+"F2.wireOp",EDGE,"E3.11.13.0"),sQuery(id+"F2.wireOp",EDGE,"E3.11.13.1"),sQuery(id+"F2.wireOp",EDGE,"E3.11.13.2"),sQuery(id+"F2.wireOp",EDGE,"E3.11.13.3"),sQuery(id+"F2.wireOp",EDGE,"E3.11.14.0"),sQuery(id+"F2.wireOp",EDGE,"E3.11.14.1"),sQuery(id+"F2.wireOp",EDGE,"E3.11.14.2"),sQuery(id+"F2.wireOp",EDGE,"E3.11.14.3"),sQuery(id+"F2.wireOp",EDGE,"E3.11.15.0"),sQuery(id+"F2.wireOp",EDGE,"E3.11.15.1"),sQuery(id+"F2.wireOp",EDGE,"E3.11.15.2"),sQuery(id+"F2.wireOp",EDGE,"E3.11.15.3"),sQuery(id+"F2.wireOp",EDGE,"E3.11.16.0"),sQuery(id+"F2.wireOp",EDGE,"E3.11.16.1"),sQuery(id+"F2.wireOp",EDGE,"E3.11.16.2"),sQuery(id+"F2.wireOp",EDGE,"E3.11.16.3"),sQuery(id+"F2.wireOp",EDGE,"E3.11.17.0"),sQuery(id+"F2.wireOp",EDGE,"E3.11.17.1"),sQuery(id+"F2.wireOp",EDGE,"E3.11.17.2"),sQuery(id+"F2.wireOp",EDGE,"E3.11.17.3"),sQuery(id+"F2.wireOp",EDGE,"E3.11.18.0"),sQuery(id+"F2.wireOp",EDGE,"E3.11.18.1"),sQuery(id+"F2.wireOp",EDGE,"E3.11.18.2"),sQuery(id+"F2.wireOp",EDGE,"E3.11.18.3"),sQuery(id+"F2.wireOp",EDGE,"E3.11.19.0"),sQuery(id+"F2.wireOp",EDGE,"E3.11.19.1"),sQuery(id+"F2.wireOp",EDGE,"E3.11.19.2"),sQuery(id+"F2.wireOp",EDGE,"E3.11.19.3"),sQuery(id+"F2.wireOp",EDGE,"E3.11.20.0"),sQuery(id+"F2.wireOp",EDGE,"E3.11.20.1"),sQuery(id+"F2.wireOp",EDGE,"E3.11.20.2"),sQuery(id+"F2.wireOp",EDGE,"E3.11.20.3"),sQuery(id+"F2.wireOp",EDGE,"E3.11.21.0"),sQuery(id+"F2.wireOp",EDGE,"E3.11.21.1"),sQuery(id+"F2.wireOp",EDGE,"E3.11.21.2"),sQuery(id+"F2.wireOp",EDGE,"E3.11.21.3"),sQuery(id+"F2.wireOp",EDGE,"E3.12.0.0"),sQuery(id+"F2.wireOp",EDGE,"E3.12.0.1"),sQuery(id+"F2.wireOp",EDGE,"E3.12.0.2"),sQuery(id+"F2.wireOp",EDGE,"E3.12.0.3"),sQuery(id+"F2.wireOp",EDGE,"E3.12.1.0"),sQuery(id+"F2.wireOp",EDGE,"E3.12.1.1"),sQuery(id+"F2.wireOp",EDGE,"E3.12.1.2"),sQuery(id+"F2.wireOp",EDGE,"E3.12.1.3"),sQuery(id+"F2.wireOp",EDGE,"E3.12.2.0"),sQuery(id+"F2.wireOp",EDGE,"E3.12.2.1"),sQuery(id+"F2.wireOp",EDGE,"E3.12.2.2"),sQuery(id+"F2.wireOp",EDGE,"E3.12.2.3"),sQuery(id+"F2.wireOp",EDGE,"E3.12.3.0"),sQuery(id+"F2.wireOp",EDGE,"E3.12.3.1"),sQuery(id+"F2.wireOp",EDGE,"E3.12.3.2"),sQuery(id+"F2.wireOp",EDGE,"E3.12.3.3"),sQuery(id+"F2.wireOp",EDGE,"E3.12.4.0"),sQuery(id+"F2.wireOp",EDGE,"E3.12.4.1"),sQuery(id+"F2.wireOp",EDGE,"E3.12.4.2"),sQuery(id+"F2.wireOp",EDGE,"E3.12.4.3"),sQuery(id+"F2.wireOp",EDGE,"E3.12.5.0"),sQuery(id+"F2.wireOp",EDGE,"E3.12.5.1"),sQuery(id+"F2.wireOp",EDGE,"E3.12.5.2"),sQuery(id+"F2.wireOp",EDGE,"E3.12.5.3"),sQuery(id+"F2.wireOp",EDGE,"E3.12.6.0"),sQuery(id+"F2.wireOp",EDGE,"E3.12.6.1"),sQuery(id+"F2.wireOp",EDGE,"E3.12.6.2"),sQuery(id+"F2.wireOp",EDGE,"E3.12.6.3"),sQuery(id+"F2.wireOp",EDGE,"E3.12.7.0"),sQuery(id+"F2.wireOp",EDGE,"E3.12.7.1"),sQuery(id+"F2.wireOp",EDGE,"E3.12.7.2"),sQuery(id+"F2.wireOp",EDGE,"E3.12.7.3"),sQuery(id+"F2.wireOp",EDGE,"E3.12.8.0"),sQuery(id+"F2.wireOp",EDGE,"E3.12.8.1"),sQuery(id+"F2.wireOp",EDGE,"E3.12.8.2"),sQuery(id+"F2.wireOp",EDGE,"E3.12.8.3"),sQuery(id+"F2.wireOp",EDGE,"E3.12.9.0"),sQuery(id+"F2.wireOp",EDGE,"E3.12.9.1"),sQuery(id+"F2.wireOp",EDGE,"E3.12.9.2"),sQuery(id+"F2.wireOp",EDGE,"E3.12.9.3"),sQuery(id+"F2.wireOp",EDGE,"E3.12.10.0"),sQuery(id+"F2.wireOp",EDGE,"E3.12.10.1"),sQuery(id+"F2.wireOp",EDGE,"E3.12.10.2"),sQuery(id+"F2.wireOp",EDGE,"E3.12.10.3"),sQuery(id+"F2.wireOp",EDGE,"E3.12.11.0"),sQuery(id+"F2.wireOp",EDGE,"E3.12.11.1"),sQuery(id+"F2.wireOp",EDGE,"E3.12.11.2"),sQuery(id+"F2.wireOp",EDGE,"E3.12.11.3"),sQuery(id+"F2.wireOp",EDGE,"E3.12.12.0"),sQuery(id+"F2.wireOp",EDGE,"E3.12.12.1"),sQuery(id+"F2.wireOp",EDGE,"E3.12.12.2"),sQuery(id+"F2.wireOp",EDGE,"E3.12.12.3"),sQuery(id+"F2.wireOp",EDGE,"E3.12.13.0"),sQuery(id+"F2.wireOp",EDGE,"E3.12.13.1"),sQuery(id+"F2.wireOp",EDGE,"E3.12.13.2"),sQuery(id+"F2.wireOp",EDGE,"E3.12.13.3"),sQuery(id+"F2.wireOp",EDGE,"E3.12.14.0"),sQuery(id+"F2.wireOp",EDGE,"E3.12.14.1"),sQuery(id+"F2.wireOp",EDGE,"E3.12.14.2"),sQuery(id+"F2.wireOp",EDGE,"E3.12.14.3"),sQuery(id+"F2.wireOp",EDGE,"E3.12.15.0"),sQuery(id+"F2.wireOp",EDGE,"E3.12.15.1"),sQuery(id+"F2.wireOp",EDGE,"E3.12.15.2"),sQuery(id+"F2.wireOp",EDGE,"E3.12.15.3"),sQuery(id+"F2.wireOp",EDGE,"E3.12.16.0"),sQuery(id+"F2.wireOp",EDGE,"E3.12.16.1"),sQuery(id+"F2.wireOp",EDGE,"E3.12.16.2"),sQuery(id+"F2.wireOp",EDGE,"E3.12.16.3"),sQuery(id+"F2.wireOp",EDGE,"E3.12.17.0"),sQuery(id+"F2.wireOp",EDGE,"E3.12.17.1"),sQuery(id+"F2.wireOp",EDGE,"E3.12.17.2"),sQuery(id+"F2.wireOp",EDGE,"E3.12.17.3"),sQuery(id+"F2.wireOp",EDGE,"E3.12.18.0"),sQuery(id+"F2.wireOp",EDGE,"E3.12.18.1"),sQuery(id+"F2.wireOp",EDGE,"E3.12.18.2"),sQuery(id+"F2.wireOp",EDGE,"E3.12.18.3"),sQuery(id+"F2.wireOp",EDGE,"E3.12.19.0"),sQuery(id+"F2.wireOp",EDGE,"E3.12.19.1"),sQuery(id+"F2.wireOp",EDGE,"E3.12.19.2"),sQuery(id+"F2.wireOp",EDGE,"E3.12.19.3"),sQuery(id+"F2.wireOp",EDGE,"E3.12.20.0"),sQuery(id+"F2.wireOp",EDGE,"E3.12.20.1"),sQuery(id+"F2.wireOp",EDGE,"E3.12.20.2"),sQuery(id+"F2.wireOp",EDGE,"E3.12.20.3"),sQuery(id+"F2.wireOp",EDGE,"E3.12.21.0"),sQuery(id+"F2.wireOp",EDGE,"E3.12.21.1"),sQuery(id+"F2.wireOp",EDGE,"E3.12.21.2"),sQuery(id+"F2.wireOp",EDGE,"E3.12.21.3"),sQuery(id+"F2.wireOp",EDGE,"E3.13.0.0"),sQuery(id+"F2.wireOp",EDGE,"E3.13.0.1"),sQuery(id+"F2.wireOp",EDGE,"E3.13.0.2"),sQuery(id+"F2.wireOp",EDGE,"E3.13.0.3"),sQuery(id+"F2.wireOp",EDGE,"E3.13.1.0"),sQuery(id+"F2.wireOp",EDGE,"E3.13.1.1"),sQuery(id+"F2.wireOp",EDGE,"E3.13.1.2"),sQuery(id+"F2.wireOp",EDGE,"E3.13.1.3"),sQuery(id+"F2.wireOp",EDGE,"E3.13.2.0"),sQuery(id+"F2.wireOp",EDGE,"E3.13.2.1"),sQuery(id+"F2.wireOp",EDGE,"E3.13.2.2"),sQuery(id+"F2.wireOp",EDGE,"E3.13.2.3"),sQuery(id+"F2.wireOp",EDGE,"E3.13.3.0"),sQuery(id+"F2.wireOp",EDGE,"E3.13.3.1"),sQuery(id+"F2.wireOp",EDGE,"E3.13.3.2"),sQuery(id+"F2.wireOp",EDGE,"E3.13.3.3"),sQuery(id+"F2.wireOp",EDGE,"E3.13.4.0"),sQuery(id+"F2.wireOp",EDGE,"E3.13.4.1"),sQuery(id+"F2.wireOp",EDGE,"E3.13.4.2"),sQuery(id+"F2.wireOp",EDGE,"E3.13.4.3"),sQuery(id+"F2.wireOp",EDGE,"E3.13.5.0"),sQuery(id+"F2.wireOp",EDGE,"E3.13.5.1"),sQuery(id+"F2.wireOp",EDGE,"E3.13.5.2"),sQuery(id+"F2.wireOp",EDGE,"E3.13.5.3"),sQuery(id+"F2.wireOp",EDGE,"E3.13.6.0"),sQuery(id+"F2.wireOp",EDGE,"E3.13.6.1"),sQuery(id+"F2.wireOp",EDGE,"E3.13.6.2"),sQuery(id+"F2.wireOp",EDGE,"E3.13.6.3"),sQuery(id+"F2.wireOp",EDGE,"E3.13.7.0"),sQuery(id+"F2.wireOp",EDGE,"E3.13.7.1"),sQuery(id+"F2.wireOp",EDGE,"E3.13.7.2"),sQuery(id+"F2.wireOp",EDGE,"E3.13.7.3"),sQuery(id+"F2.wireOp",EDGE,"E3.13.8.0"),sQuery(id+"F2.wireOp",EDGE,"E3.13.8.1"),sQuery(id+"F2.wireOp",EDGE,"E3.13.8.2"),sQuery(id+"F2.wireOp",EDGE,"E3.13.8.3"),sQuery(id+"F2.wireOp",EDGE,"E3.13.9.0"),sQuery(id+"F2.wireOp",EDGE,"E3.13.9.1"),sQuery(id+"F2.wireOp",EDGE,"E3.13.9.2"),sQuery(id+"F2.wireOp",EDGE,"E3.13.9.3"),sQuery(id+"F2.wireOp",EDGE,"E3.13.10.0"),sQuery(id+"F2.wireOp",EDGE,"E3.13.10.1"),sQuery(id+"F2.wireOp",EDGE,"E3.13.10.2"),sQuery(id+"F2.wireOp",EDGE,"E3.13.10.3"),sQuery(id+"F2.wireOp",EDGE,"E3.13.11.0"),sQuery(id+"F2.wireOp",EDGE,"E3.13.11.1"),sQuery(id+"F2.wireOp",EDGE,"E3.13.11.2"),sQuery(id+"F2.wireOp",EDGE,"E3.13.11.3"),sQuery(id+"F2.wireOp",EDGE,"E3.13.12.0"),sQuery(id+"F2.wireOp",EDGE,"E3.13.12.1"),sQuery(id+"F2.wireOp",EDGE,"E3.13.12.2"),sQuery(id+"F2.wireOp",EDGE,"E3.13.12.3"),sQuery(id+"F2.wireOp",EDGE,"E3.13.13.0"),sQuery(id+"F2.wireOp",EDGE,"E3.13.13.1"),sQuery(id+"F2.wireOp",EDGE,"E3.13.13.2"),sQuery(id+"F2.wireOp",EDGE,"E3.13.13.3"),sQuery(id+"F2.wireOp",EDGE,"E3.13.14.0"),sQuery(id+"F2.wireOp",EDGE,"E3.13.14.1"),sQuery(id+"F2.wireOp",EDGE,"E3.13.14.2"),sQuery(id+"F2.wireOp",EDGE,"E3.13.14.3"),sQuery(id+"F2.wireOp",EDGE,"E3.13.15.0"),sQuery(id+"F2.wireOp",EDGE,"E3.13.15.1"),sQuery(id+"F2.wireOp",EDGE,"E3.13.15.2"),sQuery(id+"F2.wireOp",EDGE,"E3.13.15.3"),sQuery(id+"F2.wireOp",EDGE,"E3.13.16.0"),sQuery(id+"F2.wireOp",EDGE,"E3.13.16.1"),sQuery(id+"F2.wireOp",EDGE,"E3.13.16.2"),sQuery(id+"F2.wireOp",EDGE,"E3.13.16.3"),sQuery(id+"F2.wireOp",EDGE,"E3.13.17.0"),sQuery(id+"F2.wireOp",EDGE,"E3.13.17.1"),sQuery(id+"F2.wireOp",EDGE,"E3.13.17.2"),sQuery(id+"F2.wireOp",EDGE,"E3.13.17.3"),sQuery(id+"F2.wireOp",EDGE,"E3.13.18.0"),sQuery(id+"F2.wireOp",EDGE,"E3.13.18.1"),sQuery(id+"F2.wireOp",EDGE,"E3.13.18.2"),sQuery(id+"F2.wireOp",EDGE,"E3.13.18.3"),sQuery(id+"F2.wireOp",EDGE,"E3.13.19.0"),sQuery(id+"F2.wireOp",EDGE,"E3.13.19.1"),sQuery(id+"F2.wireOp",EDGE,"E3.13.19.2"),sQuery(id+"F2.wireOp",EDGE,"E3.13.19.3"),sQuery(id+"F2.wireOp",EDGE,"E3.13.20.0"),sQuery(id+"F2.wireOp",EDGE,"E3.13.20.1"),sQuery(id+"F2.wireOp",EDGE,"E3.13.20.2"),sQuery(id+"F2.wireOp",EDGE,"E3.13.20.3"),sQuery(id+"F2.wireOp",EDGE,"E3.13.21.0"),sQuery(id+"F2.wireOp",EDGE,"E3.13.21.1"),sQuery(id+"F2.wireOp",EDGE,"E3.13.21.2"),sQuery(id+"F2.wireOp",EDGE,"E3.13.21.3"),sQuery(id+"F2.wireOp",EDGE,"E3.14.0.0"),sQuery(id+"F2.wireOp",EDGE,"E3.14.0.1"),sQuery(id+"F2.wireOp",EDGE,"E3.14.0.2"),sQuery(id+"F2.wireOp",EDGE,"E3.14.0.3"),sQuery(id+"F2.wireOp",EDGE,"E3.14.1.0"),sQuery(id+"F2.wireOp",EDGE,"E3.14.1.1"),sQuery(id+"F2.wireOp",EDGE,"E3.14.1.2"),sQuery(id+"F2.wireOp",EDGE,"E3.14.1.3"),sQuery(id+"F2.wireOp",EDGE,"E3.14.2.0"),sQuery(id+"F2.wireOp",EDGE,"E3.14.2.1"),sQuery(id+"F2.wireOp",EDGE,"E3.14.2.2"),sQuery(id+"F2.wireOp",EDGE,"E3.14.2.3"),sQuery(id+"F2.wireOp",EDGE,"E3.14.3.0"),sQuery(id+"F2.wireOp",EDGE,"E3.14.3.1"),sQuery(id+"F2.wireOp",EDGE,"E3.14.3.2"),sQuery(id+"F2.wireOp",EDGE,"E3.14.3.3"),sQuery(id+"F2.wireOp",EDGE,"E3.14.4.0"),sQuery(id+"F2.wireOp",EDGE,"E3.14.4.1"),sQuery(id+"F2.wireOp",EDGE,"E3.14.4.2"),sQuery(id+"F2.wireOp",EDGE,"E3.14.4.3"),sQuery(id+"F2.wireOp",EDGE,"E3.14.5.0"),sQuery(id+"F2.wireOp",EDGE,"E3.14.5.1"),sQuery(id+"F2.wireOp",EDGE,"E3.14.5.2"),sQuery(id+"F2.wireOp",EDGE,"E3.14.5.3"),sQuery(id+"F2.wireOp",EDGE,"E3.14.6.0"),sQuery(id+"F2.wireOp",EDGE,"E3.14.6.1"),sQuery(id+"F2.wireOp",EDGE,"E3.14.6.2"),sQuery(id+"F2.wireOp",EDGE,"E3.14.6.3"),sQuery(id+"F2.wireOp",EDGE,"E3.14.7.0"),sQuery(id+"F2.wireOp",EDGE,"E3.14.7.1"),sQuery(id+"F2.wireOp",EDGE,"E3.14.7.2"),sQuery(id+"F2.wireOp",EDGE,"E3.14.7.3"),sQuery(id+"F2.wireOp",EDGE,"E3.14.8.0"),sQuery(id+"F2.wireOp",EDGE,"E3.14.8.1"),sQuery(id+"F2.wireOp",EDGE,"E3.14.8.2"),sQuery(id+"F2.wireOp",EDGE,"E3.14.8.3"),sQuery(id+"F2.wireOp",EDGE,"E3.14.9.0"),sQuery(id+"F2.wireOp",EDGE,"E3.14.9.1"),sQuery(id+"F2.wireOp",EDGE,"E3.14.9.2"),sQuery(id+"F2.wireOp",EDGE,"E3.14.9.3"),sQuery(id+"F2.wireOp",EDGE,"E3.14.10.0"),sQuery(id+"F2.wireOp",EDGE,"E3.14.10.1"),sQuery(id+"F2.wireOp",EDGE,"E3.14.10.2"),sQuery(id+"F2.wireOp",EDGE,"E3.14.10.3"),sQuery(id+"F2.wireOp",EDGE,"E3.14.11.0"),sQuery(id+"F2.wireOp",EDGE,"E3.14.11.1"),sQuery(id+"F2.wireOp",EDGE,"E3.14.11.2"),sQuery(id+"F2.wireOp",EDGE,"E3.14.11.3"),sQuery(id+"F2.wireOp",EDGE,"E3.14.12.0"),sQuery(id+"F2.wireOp",EDGE,"E3.14.12.1"),sQuery(id+"F2.wireOp",EDGE,"E3.14.12.2"),sQuery(id+"F2.wireOp",EDGE,"E3.14.12.3"),sQuery(id+"F2.wireOp",EDGE,"E3.14.13.0"),sQuery(id+"F2.wireOp",EDGE,"E3.14.13.1"),sQuery(id+"F2.wireOp",EDGE,"E3.14.13.2"),sQuery(id+"F2.wireOp",EDGE,"E3.14.13.3"),sQuery(id+"F2.wireOp",EDGE,"E3.14.14.0"),sQuery(id+"F2.wireOp",EDGE,"E3.14.14.1"),sQuery(id+"F2.wireOp",EDGE,"E3.14.14.2"),sQuery(id+"F2.wireOp",EDGE,"E3.14.14.3"),sQuery(id+"F2.wireOp",EDGE,"E3.14.15.0"),sQuery(id+"F2.wireOp",EDGE,"E3.14.15.1"),sQuery(id+"F2.wireOp",EDGE,"E3.14.15.2"),sQuery(id+"F2.wireOp",EDGE,"E3.14.15.3"),sQuery(id+"F2.wireOp",EDGE,"E3.14.16.0"),sQuery(id+"F2.wireOp",EDGE,"E3.14.16.1"),sQuery(id+"F2.wireOp",EDGE,"E3.14.16.2"),sQuery(id+"F2.wireOp",EDGE,"E3.14.16.3"),sQuery(id+"F2.wireOp",EDGE,"E3.14.17.0"),sQuery(id+"F2.wireOp",EDGE,"E3.14.17.1"),sQuery(id+"F2.wireOp",EDGE,"E3.14.17.2"),sQuery(id+"F2.wireOp",EDGE,"E3.14.17.3"),sQuery(id+"F2.wireOp",EDGE,"E3.14.18.0"),sQuery(id+"F2.wireOp",EDGE,"E3.14.18.1"),sQuery(id+"F2.wireOp",EDGE,"E3.14.18.2"),sQuery(id+"F2.wireOp",EDGE,"E3.14.18.3"),sQuery(id+"F2.wireOp",EDGE,"E3.14.19.0"),sQuery(id+"F2.wireOp",EDGE,"E3.14.19.1"),sQuery(id+"F2.wireOp",EDGE,"E3.14.19.2"),sQuery(id+"F2.wireOp",EDGE,"E3.14.19.3"),sQuery(id+"F2.wireOp",EDGE,"E3.14.20.0"),sQuery(id+"F2.wireOp",EDGE,"E3.14.20.1"),sQuery(id+"F2.wireOp",EDGE,"E3.14.20.2"),sQuery(id+"F2.wireOp",EDGE,"E3.14.20.3"),sQuery(id+"F2.wireOp",EDGE,"E3.14.21.0"),sQuery(id+"F2.wireOp",EDGE,"E3.14.21.1"),sQuery(id+"F2.wireOp",EDGE,"E3.14.21.2"),sQuery(id+"F2.wireOp",EDGE,"E3.14.21.3"),sQuery(id+"F2.wireOp",EDGE,"E3.15.0.0"),sQuery(id+"F2.wireOp",EDGE,"E3.15.0.1"),sQuery(id+"F2.wireOp",EDGE,"E3.15.0.2"),sQuery(id+"F2.wireOp",EDGE,"E3.15.0.3"),sQuery(id+"F2.wireOp",EDGE,"E3.15.1.0"),sQuery(id+"F2.wireOp",EDGE,"E3.15.1.1"),sQuery(id+"F2.wireOp",EDGE,"E3.15.1.2"),sQuery(id+"F2.wireOp",EDGE,"E3.15.1.3"),sQuery(id+"F2.wireOp",EDGE,"E3.15.2.0"),sQuery(id+"F2.wireOp",EDGE,"E3.15.2.1"),sQuery(id+"F2.wireOp",EDGE,"E3.15.2.2"),sQuery(id+"F2.wireOp",EDGE,"E3.15.2.3"),sQuery(id+"F2.wireOp",EDGE,"E3.15.3.0"),sQuery(id+"F2.wireOp",EDGE,"E3.15.3.1"),sQuery(id+"F2.wireOp",EDGE,"E3.15.3.2"),sQuery(id+"F2.wireOp",EDGE,"E3.15.3.3"),sQuery(id+"F2.wireOp",EDGE,"E3.15.4.0"),sQuery(id+"F2.wireOp",EDGE,"E3.15.4.1"),sQuery(id+"F2.wireOp",EDGE,"E3.15.4.2"),sQuery(id+"F2.wireOp",EDGE,"E3.15.4.3"),sQuery(id+"F2.wireOp",EDGE,"E3.15.5.0"),sQuery(id+"F2.wireOp",EDGE,"E3.15.5.1"),sQuery(id+"F2.wireOp",EDGE,"E3.15.5.2"),sQuery(id+"F2.wireOp",EDGE,"E3.15.5.3"),sQuery(id+"F2.wireOp",EDGE,"E3.15.6.0"),sQuery(id+"F2.wireOp",EDGE,"E3.15.6.1"),sQuery(id+"F2.wireOp",EDGE,"E3.15.6.2"),sQuery(id+"F2.wireOp",EDGE,"E3.15.6.3"),sQuery(id+"F2.wireOp",EDGE,"E3.15.7.0"),sQuery(id+"F2.wireOp",EDGE,"E3.15.7.1"),sQuery(id+"F2.wireOp",EDGE,"E3.15.7.2"),sQuery(id+"F2.wireOp",EDGE,"E3.15.7.3"),sQuery(id+"F2.wireOp",EDGE,"E3.15.8.0"),sQuery(id+"F2.wireOp",EDGE,"E3.15.8.1"),sQuery(id+"F2.wireOp",EDGE,"E3.15.8.2"),sQuery(id+"F2.wireOp",EDGE,"E3.15.8.3"),sQuery(id+"F2.wireOp",EDGE,"E3.15.9.0"),sQuery(id+"F2.wireOp",EDGE,"E3.15.9.1"),sQuery(id+"F2.wireOp",EDGE,"E3.15.9.2"),sQuery(id+"F2.wireOp",EDGE,"E3.15.9.3"),sQuery(id+"F2.wireOp",EDGE,"E3.15.10.0"),sQuery(id+"F2.wireOp",EDGE,"E3.15.10.1"),sQuery(id+"F2.wireOp",EDGE,"E3.15.10.2"),sQuery(id+"F2.wireOp",EDGE,"E3.15.10.3"),sQuery(id+"F2.wireOp",EDGE,"E3.15.11.0"),sQuery(id+"F2.wireOp",EDGE,"E3.15.11.1"),sQuery(id+"F2.wireOp",EDGE,"E3.15.11.2"),sQuery(id+"F2.wireOp",EDGE,"E3.15.11.3"),sQuery(id+"F2.wireOp",EDGE,"E3.15.12.0"),sQuery(id+"F2.wireOp",EDGE,"E3.15.12.1"),sQuery(id+"F2.wireOp",EDGE,"E3.15.12.2"),sQuery(id+"F2.wireOp",EDGE,"E3.15.12.3"),sQuery(id+"F2.wireOp",EDGE,"E3.15.13.0"),sQuery(id+"F2.wireOp",EDGE,"E3.15.13.1"),sQuery(id+"F2.wireOp",EDGE,"E3.15.13.2"),sQuery(id+"F2.wireOp",EDGE,"E3.15.13.3"),sQuery(id+"F2.wireOp",EDGE,"E3.15.14.0"),sQuery(id+"F2.wireOp",EDGE,"E3.15.14.1"),sQuery(id+"F2.wireOp",EDGE,"E3.15.14.2"),sQuery(id+"F2.wireOp",EDGE,"E3.15.14.3"),sQuery(id+"F2.wireOp",EDGE,"E3.15.15.0"),sQuery(id+"F2.wireOp",EDGE,"E3.15.15.1"),sQuery(id+"F2.wireOp",EDGE,"E3.15.15.2"),sQuery(id+"F2.wireOp",EDGE,"E3.15.15.3"),sQuery(id+"F2.wireOp",EDGE,"E3.15.16.0"),sQuery(id+"F2.wireOp",EDGE,"E3.15.16.1"),sQuery(id+"F2.wireOp",EDGE,"E3.15.16.2"),sQuery(id+"F2.wireOp",EDGE,"E3.15.16.3"),sQuery(id+"F2.wireOp",EDGE,"E3.15.17.0"),sQuery(id+"F2.wireOp",EDGE,"E3.15.17.1"),sQuery(id+"F2.wireOp",EDGE,"E3.15.17.2"),sQuery(id+"F2.wireOp",EDGE,"E3.15.17.3"),sQuery(id+"F2.wireOp",EDGE,"E3.15.18.0"),sQuery(id+"F2.wireOp",EDGE,"E3.15.18.1"),sQuery(id+"F2.wireOp",EDGE,"E3.15.18.2"),sQuery(id+"F2.wireOp",EDGE,"E3.15.18.3"),sQuery(id+"F2.wireOp",EDGE,"E3.15.19.0"),sQuery(id+"F2.wireOp",EDGE,"E3.15.19.1"),sQuery(id+"F2.wireOp",EDGE,"E3.15.19.2"),sQuery(id+"F2.wireOp",EDGE,"E3.15.19.3"),sQuery(id+"F2.wireOp",EDGE,"E3.15.20.0"),sQuery(id+"F2.wireOp",EDGE,"E3.15.20.1"),sQuery(id+"F2.wireOp",EDGE,"E3.15.20.2"),sQuery(id+"F2.wireOp",EDGE,"E3.15.20.3"),sQuery(id+"F2.wireOp",EDGE,"E3.15.21.0"),sQuery(id+"F2.wireOp",EDGE,"E3.15.21.1"),sQuery(id+"F2.wireOp",EDGE,"E3.15.21.2"),sQuery(id+"F2.wireOp",EDGE,"E3.15.21.3"),sQuery(id+"F2.wireOp",EDGE,"E3.16.0.0"),sQuery(id+"F2.wireOp",EDGE,"E3.16.0.1"),sQuery(id+"F2.wireOp",EDGE,"E3.16.0.2"),sQuery(id+"F2.wireOp",EDGE,"E3.16.0.3"),sQuery(id+"F2.wireOp",EDGE,"E3.16.1.0"),sQuery(id+"F2.wireOp",EDGE,"E3.16.1.1"),sQuery(id+"F2.wireOp",EDGE,"E3.16.1.2"),sQuery(id+"F2.wireOp",EDGE,"E3.16.1.3"),sQuery(id+"F2.wireOp",EDGE,"E3.16.2.0"),sQuery(id+"F2.wireOp",EDGE,"E3.16.2.1"),sQuery(id+"F2.wireOp",EDGE,"E3.16.2.2"),sQuery(id+"F2.wireOp",EDGE,"E3.16.2.3"),sQuery(id+"F2.wireOp",EDGE,"E3.16.3.0"),sQuery(id+"F2.wireOp",EDGE,"E3.16.3.1"),sQuery(id+"F2.wireOp",EDGE,"E3.16.3.2"),sQuery(id+"F2.wireOp",EDGE,"E3.16.3.3"),sQuery(id+"F2.wireOp",EDGE,"E3.16.4.0"),sQuery(id+"F2.wireOp",EDGE,"E3.16.4.1"),sQuery(id+"F2.wireOp",EDGE,"E3.16.4.2"),sQuery(id+"F2.wireOp",EDGE,"E3.16.4.3"),sQuery(id+"F2.wireOp",EDGE,"E3.16.5.0"),sQuery(id+"F2.wireOp",EDGE,"E3.16.5.1"),sQuery(id+"F2.wireOp",EDGE,"E3.16.5.2"),sQuery(id+"F2.wireOp",EDGE,"E3.16.5.3"),sQuery(id+"F2.wireOp",EDGE,"E3.16.6.0"),sQuery(id+"F2.wireOp",EDGE,"E3.16.6.1"),sQuery(id+"F2.wireOp",EDGE,"E3.16.6.2"),sQuery(id+"F2.wireOp",EDGE,"E3.16.6.3"),sQuery(id+"F2.wireOp",EDGE,"E3.16.7.0"),sQuery(id+"F2.wireOp",EDGE,"E3.16.7.1"),sQuery(id+"F2.wireOp",EDGE,"E3.16.7.2"),sQuery(id+"F2.wireOp",EDGE,"E3.16.7.3"),sQuery(id+"F2.wireOp",EDGE,"E3.16.8.0"),sQuery(id+"F2.wireOp",EDGE,"E3.16.8.1"),sQuery(id+"F2.wireOp",EDGE,"E3.16.8.2"),sQuery(id+"F2.wireOp",EDGE,"E3.16.8.3"),sQuery(id+"F2.wireOp",EDGE,"E3.16.9.0"),sQuery(id+"F2.wireOp",EDGE,"E3.16.9.1"),sQuery(id+"F2.wireOp",EDGE,"E3.16.9.2"),sQuery(id+"F2.wireOp",EDGE,"E3.16.9.3"),sQuery(id+"F2.wireOp",EDGE,"E3.16.10.0"),sQuery(id+"F2.wireOp",EDGE,"E3.16.10.1"),sQuery(id+"F2.wireOp",EDGE,"E3.16.10.2"),sQuery(id+"F2.wireOp",EDGE,"E3.16.10.3"),sQuery(id+"F2.wireOp",EDGE,"E3.16.11.0"),sQuery(id+"F2.wireOp",EDGE,"E3.16.11.1"),sQuery(id+"F2.wireOp",EDGE,"E3.16.11.2"),sQuery(id+"F2.wireOp",EDGE,"E3.16.11.3"),sQuery(id+"F2.wireOp",EDGE,"E3.16.12.0"),sQuery(id+"F2.wireOp",EDGE,"E3.16.12.1"),sQuery(id+"F2.wireOp",EDGE,"E3.16.12.2"),sQuery(id+"F2.wireOp",EDGE,"E3.16.12.3"),sQuery(id+"F2.wireOp",EDGE,"E3.16.13.0"),sQuery(id+"F2.wireOp",EDGE,"E3.16.13.1"),sQuery(id+"F2.wireOp",EDGE,"E3.16.13.2"),sQuery(id+"F2.wireOp",EDGE,"E3.16.13.3"),sQuery(id+"F2.wireOp",EDGE,"E3.16.14.0"),sQuery(id+"F2.wireOp",EDGE,"E3.16.14.1"),sQuery(id+"F2.wireOp",EDGE,"E3.16.14.2"),sQuery(id+"F2.wireOp",EDGE,"E3.16.14.3"),sQuery(id+"F2.wireOp",EDGE,"E3.16.15.0"),sQuery(id+"F2.wireOp",EDGE,"E3.16.15.1"),sQuery(id+"F2.wireOp",EDGE,"E3.16.15.2"),sQuery(id+"F2.wireOp",EDGE,"E3.16.15.3"),sQuery(id+"F2.wireOp",EDGE,"E3.16.16.0"),sQuery(id+"F2.wireOp",EDGE,"E3.16.16.1"),sQuery(id+"F2.wireOp",EDGE,"E3.16.16.2"),sQuery(id+"F2.wireOp",EDGE,"E3.16.16.3"),sQuery(id+"F2.wireOp",EDGE,"E3.16.17.0"),sQuery(id+"F2.wireOp",EDGE,"E3.16.17.1"),sQuery(id+"F2.wireOp",EDGE,"E3.16.17.2"),sQuery(id+"F2.wireOp",EDGE,"E3.16.17.3"),sQuery(id+"F2.wireOp",EDGE,"E3.16.18.0"),sQuery(id+"F2.wireOp",EDGE,"E3.16.18.1"),sQuery(id+"F2.wireOp",EDGE,"E3.16.18.2"),sQuery(id+"F2.wireOp",EDGE,"E3.16.18.3"),sQuery(id+"F2.wireOp",EDGE,"E3.16.19.0"),sQuery(id+"F2.wireOp",EDGE,"E3.16.19.1"),sQuery(id+"F2.wireOp",EDGE,"E3.16.19.2"),sQuery(id+"F2.wireOp",EDGE,"E3.16.19.3"),sQuery(id+"F2.wireOp",EDGE,"E3.16.20.0"),sQuery(id+"F2.wireOp",EDGE,"E3.16.20.1"),sQuery(id+"F2.wireOp",EDGE,"E3.16.20.2"),sQuery(id+"F2.wireOp",EDGE,"E3.16.20.3"),sQuery(id+"F2.wireOp",EDGE,"E3.16.21.0"),sQuery(id+"F2.wireOp",EDGE,"E3.16.21.1"),sQuery(id+"F2.wireOp",EDGE,"E3.16.21.2"),sQuery(id+"F2.wireOp",EDGE,"E3.16.21.3"),sQuery(id+"F2.wireOp",EDGE,"E3.17.0.0"),sQuery(id+"F2.wireOp",EDGE,"E3.17.0.1"),sQuery(id+"F2.wireOp",EDGE,"E3.17.0.2"),sQuery(id+"F2.wireOp",EDGE,"E3.17.0.3"),sQuery(id+"F2.wireOp",EDGE,"E3.17.1.0"),sQuery(id+"F2.wireOp",EDGE,"E3.17.1.1"),sQuery(id+"F2.wireOp",EDGE,"E3.17.1.2"),sQuery(id+"F2.wireOp",EDGE,"E3.17.1.3"),sQuery(id+"F2.wireOp",EDGE,"E3.17.2.0"),sQuery(id+"F2.wireOp",EDGE,"E3.17.2.1"),sQuery(id+"F2.wireOp",EDGE,"E3.17.2.2"),sQuery(id+"F2.wireOp",EDGE,"E3.17.2.3"),sQuery(id+"F2.wireOp",EDGE,"E3.17.3.0"),sQuery(id+"F2.wireOp",EDGE,"E3.17.3.1"),sQuery(id+"F2.wireOp",EDGE,"E3.17.3.2"),sQuery(id+"F2.wireOp",EDGE,"E3.17.3.3"),sQuery(id+"F2.wireOp",EDGE,"E3.17.4.0"),sQuery(id+"F2.wireOp",EDGE,"E3.17.4.1"),sQuery(id+"F2.wireOp",EDGE,"E3.17.4.2"),sQuery(id+"F2.wireOp",EDGE,"E3.17.4.3"),sQuery(id+"F2.wireOp",EDGE,"E3.17.5.0"),sQuery(id+"F2.wireOp",EDGE,"E3.17.5.1"),sQuery(id+"F2.wireOp",EDGE,"E3.17.5.2"),sQuery(id+"F2.wireOp",EDGE,"E3.17.5.3"),sQuery(id+"F2.wireOp",EDGE,"E3.17.6.0"),sQuery(id+"F2.wireOp",EDGE,"E3.17.6.1"),sQuery(id+"F2.wireOp",EDGE,"E3.17.6.2"),sQuery(id+"F2.wireOp",EDGE,"E3.17.6.3"),sQuery(id+"F2.wireOp",EDGE,"E3.17.7.0"),sQuery(id+"F2.wireOp",EDGE,"E3.17.7.1"),sQuery(id+"F2.wireOp",EDGE,"E3.17.7.2"),sQuery(id+"F2.wireOp",EDGE,"E3.17.7.3"),sQuery(id+"F2.wireOp",EDGE,"E3.17.8.0"),sQuery(id+"F2.wireOp",EDGE,"E3.17.8.1"),sQuery(id+"F2.wireOp",EDGE,"E3.17.8.2"),sQuery(id+"F2.wireOp",EDGE,"E3.17.8.3"),sQuery(id+"F2.wireOp",EDGE,"E3.17.9.0"),sQuery(id+"F2.wireOp",EDGE,"E3.17.9.1"),sQuery(id+"F2.wireOp",EDGE,"E3.17.9.2"),sQuery(id+"F2.wireOp",EDGE,"E3.17.9.3"),sQuery(id+"F2.wireOp",EDGE,"E3.17.10.0"),sQuery(id+"F2.wireOp",EDGE,"E3.17.10.1"),sQuery(id+"F2.wireOp",EDGE,"E3.17.10.2"),sQuery(id+"F2.wireOp",EDGE,"E3.17.10.3"),sQuery(id+"F2.wireOp",EDGE,"E3.17.11.0"),sQuery(id+"F2.wireOp",EDGE,"E3.17.11.1"),sQuery(id+"F2.wireOp",EDGE,"E3.17.11.2"),sQuery(id+"F2.wireOp",EDGE,"E3.17.11.3"),sQuery(id+"F2.wireOp",EDGE,"E3.17.12.0"),sQuery(id+"F2.wireOp",EDGE,"E3.17.12.1"),sQuery(id+"F2.wireOp",EDGE,"E3.17.12.2"),sQuery(id+"F2.wireOp",EDGE,"E3.17.12.3"),sQuery(id+"F2.wireOp",EDGE,"E3.17.13.0"),sQuery(id+"F2.wireOp",EDGE,"E3.17.13.1"),sQuery(id+"F2.wireOp",EDGE,"E3.17.13.2"),sQuery(id+"F2.wireOp",EDGE,"E3.17.13.3"),sQuery(id+"F2.wireOp",EDGE,"E3.17.14.0"),sQuery(id+"F2.wireOp",EDGE,"E3.17.14.1"),sQuery(id+"F2.wireOp",EDGE,"E3.17.14.2"),sQuery(id+"F2.wireOp",EDGE,"E3.17.14.3"),sQuery(id+"F2.wireOp",EDGE,"E3.17.15.0"),sQuery(id+"F2.wireOp",EDGE,"E3.17.15.1"),sQuery(id+"F2.wireOp",EDGE,"E3.17.15.2"),sQuery(id+"F2.wireOp",EDGE,"E3.17.15.3"),sQuery(id+"F2.wireOp",EDGE,"E3.17.16.0"),sQuery(id+"F2.wireOp",EDGE,"E3.17.16.1"),sQuery(id+"F2.wireOp",EDGE,"E3.17.16.2"),sQuery(id+"F2.wireOp",EDGE,"E3.17.16.3"),sQuery(id+"F2.wireOp",EDGE,"E3.17.17.0"),sQuery(id+"F2.wireOp",EDGE,"E3.17.17.1"),sQuery(id+"F2.wireOp",EDGE,"E3.17.17.2"),sQuery(id+"F2.wireOp",EDGE,"E3.17.17.3"),sQuery(id+"F2.wireOp",EDGE,"E3.17.18.0"),sQuery(id+"F2.wireOp",EDGE,"E3.17.18.1"),sQuery(id+"F2.wireOp",EDGE,"E3.17.18.2"),sQuery(id+"F2.wireOp",EDGE,"E3.17.18.3"),sQuery(id+"F2.wireOp",EDGE,"E3.17.19.0"),sQuery(id+"F2.wireOp",EDGE,"E3.17.19.1"),sQuery(id+"F2.wireOp",EDGE,"E3.17.19.2"),sQuery(id+"F2.wireOp",EDGE,"E3.17.19.3"),sQuery(id+"F2.wireOp",EDGE,"E3.17.20.0"),sQuery(id+"F2.wireOp",EDGE,"E3.17.20.1"),sQuery(id+"F2.wireOp",EDGE,"E3.17.20.2"),sQuery(id+"F2.wireOp",EDGE,"E3.17.20.3"),sQuery(id+"F2.wireOp",EDGE,"E3.17.21.0"),sQuery(id+"F2.wireOp",EDGE,"E3.17.21.1"),sQuery(id+"F2.wireOp",EDGE,"E3.17.21.2"),sQuery(id+"F2.wireOp",EDGE,"E3.17.21.3"),sQuery(id+"F2.wireOp",EDGE,"E3.18.0.0"),sQuery(id+"F2.wireOp",EDGE,"E3.18.0.1"),sQuery(id+"F2.wireOp",EDGE,"E3.18.0.2"),sQuery(id+"F2.wireOp",EDGE,"E3.18.0.3"),sQuery(id+"F2.wireOp",EDGE,"E3.18.1.0"),sQuery(id+"F2.wireOp",EDGE,"E3.18.1.1"),sQuery(id+"F2.wireOp",EDGE,"E3.18.1.2"),sQuery(id+"F2.wireOp",EDGE,"E3.18.1.3"),sQuery(id+"F2.wireOp",EDGE,"E3.18.2.0"),sQuery(id+"F2.wireOp",EDGE,"E3.18.2.1"),sQuery(id+"F2.wireOp",EDGE,"E3.18.2.2"),sQuery(id+"F2.wireOp",EDGE,"E3.18.2.3"),sQuery(id+"F2.wireOp",EDGE,"E3.18.3.0"),sQuery(id+"F2.wireOp",EDGE,"E3.18.3.1"),sQuery(id+"F2.wireOp",EDGE,"E3.18.3.2"),sQuery(id+"F2.wireOp",EDGE,"E3.18.3.3"),sQuery(id+"F2.wireOp",EDGE,"E3.18.4.0"),sQuery(id+"F2.wireOp",EDGE,"E3.18.4.1"),sQuery(id+"F2.wireOp",EDGE,"E3.18.4.2"),sQuery(id+"F2.wireOp",EDGE,"E3.18.4.3"),sQuery(id+"F2.wireOp",EDGE,"E3.18.5.0"),sQuery(id+"F2.wireOp",EDGE,"E3.18.5.1"),sQuery(id+"F2.wireOp",EDGE,"E3.18.5.2"),sQuery(id+"F2.wireOp",EDGE,"E3.18.5.3"),sQuery(id+"F2.wireOp",EDGE,"E3.18.6.0"),sQuery(id+"F2.wireOp",EDGE,"E3.18.6.1"),sQuery(id+"F2.wireOp",EDGE,"E3.18.6.2"),sQuery(id+"F2.wireOp",EDGE,"E3.18.6.3"),sQuery(id+"F2.wireOp",EDGE,"E3.18.7.0"),sQuery(id+"F2.wireOp",EDGE,"E3.18.7.1"),sQuery(id+"F2.wireOp",EDGE,"E3.18.7.2"),sQuery(id+"F2.wireOp",EDGE,"E3.18.7.3"),sQuery(id+"F2.wireOp",EDGE,"E3.18.8.0"),sQuery(id+"F2.wireOp",EDGE,"E3.18.8.1"),sQuery(id+"F2.wireOp",EDGE,"E3.18.8.2"),sQuery(id+"F2.wireOp",EDGE,"E3.18.8.3"),sQuery(id+"F2.wireOp",EDGE,"E3.18.9.0"),sQuery(id+"F2.wireOp",EDGE,"E3.18.9.1"),sQuery(id+"F2.wireOp",EDGE,"E3.18.9.2"),sQuery(id+"F2.wireOp",EDGE,"E3.18.9.3"),sQuery(id+"F2.wireOp",EDGE,"E3.18.10.0"),sQuery(id+"F2.wireOp",EDGE,"E3.18.10.1"),sQuery(id+"F2.wireOp",EDGE,"E3.18.10.2"),sQuery(id+"F2.wireOp",EDGE,"E3.18.10.3"),sQuery(id+"F2.wireOp",EDGE,"E3.18.11.0"),sQuery(id+"F2.wireOp",EDGE,"E3.18.11.1"),sQuery(id+"F2.wireOp",EDGE,"E3.18.11.2"),sQuery(id+"F2.wireOp",EDGE,"E3.18.11.3"),sQuery(id+"F2.wireOp",EDGE,"E3.18.12.0"),sQuery(id+"F2.wireOp",EDGE,"E3.18.12.1"),sQuery(id+"F2.wireOp",EDGE,"E3.18.12.2"),sQuery(id+"F2.wireOp",EDGE,"E3.18.12.3"),sQuery(id+"F2.wireOp",EDGE,"E3.18.13.0"),sQuery(id+"F2.wireOp",EDGE,"E3.18.13.1"),sQuery(id+"F2.wireOp",EDGE,"E3.18.13.2"),sQuery(id+"F2.wireOp",EDGE,"E3.18.13.3"),sQuery(id+"F2.wireOp",EDGE,"E3.18.14.0"),sQuery(id+"F2.wireOp",EDGE,"E3.18.14.1"),sQuery(id+"F2.wireOp",EDGE,"E3.18.14.2"),sQuery(id+"F2.wireOp",EDGE,"E3.18.14.3"),sQuery(id+"F2.wireOp",EDGE,"E3.18.15.0"),sQuery(id+"F2.wireOp",EDGE,"E3.18.15.1"),sQuery(id+"F2.wireOp",EDGE,"E3.18.15.2"),sQuery(id+"F2.wireOp",EDGE,"E3.18.15.3"),sQuery(id+"F2.wireOp",EDGE,"E3.18.16.0"),sQuery(id+"F2.wireOp",EDGE,"E3.18.16.1"),sQuery(id+"F2.wireOp",EDGE,"E3.18.16.2"),sQuery(id+"F2.wireOp",EDGE,"E3.18.16.3"),sQuery(id+"F2.wireOp",EDGE,"E3.18.17.0"),sQuery(id+"F2.wireOp",EDGE,"E3.18.17.1"),sQuery(id+"F2.wireOp",EDGE,"E3.18.17.2"),sQuery(id+"F2.wireOp",EDGE,"E3.18.17.3"),sQuery(id+"F2.wireOp",EDGE,"E3.18.18.0"),sQuery(id+"F2.wireOp",EDGE,"E3.18.18.1"),sQuery(id+"F2.wireOp",EDGE,"E3.18.18.2"),sQuery(id+"F2.wireOp",EDGE,"E3.18.18.3"),sQuery(id+"F2.wireOp",EDGE,"E3.18.19.0"),sQuery(id+"F2.wireOp",EDGE,"E3.18.19.1"),sQuery(id+"F2.wireOp",EDGE,"E3.18.19.2"),sQuery(id+"F2.wireOp",EDGE,"E3.18.19.3"),sQuery(id+"F2.wireOp",EDGE,"E3.18.20.0"),sQuery(id+"F2.wireOp",EDGE,"E3.18.20.1"),sQuery(id+"F2.wireOp",EDGE,"E3.18.20.2"),sQuery(id+"F2.wireOp",EDGE,"E3.18.20.3"),sQuery(id+"F2.wireOp",EDGE,"E3.18.21.0"),sQuery(id+"F2.wireOp",EDGE,"E3.18.21.1"),sQuery(id+"F2.wireOp",EDGE,"E3.18.21.2"),sQuery(id+"F2.wireOp",EDGE,"E3.18.21.3"),sQuery(id+"F2.wireOp",EDGE,"E3.19.0.0"),sQuery(id+"F2.wireOp",EDGE,"E3.19.0.1"),sQuery(id+"F2.wireOp",EDGE,"E3.19.0.2"),sQuery(id+"F2.wireOp",EDGE,"E3.19.0.3"),sQuery(id+"F2.wireOp",EDGE,"E3.19.1.0"),sQuery(id+"F2.wireOp",EDGE,"E3.19.1.1"),sQuery(id+"F2.wireOp",EDGE,"E3.19.1.2"),sQuery(id+"F2.wireOp",EDGE,"E3.19.1.3"),sQuery(id+"F2.wireOp",EDGE,"E3.19.2.0"),sQuery(id+"F2.wireOp",EDGE,"E3.19.2.1"),sQuery(id+"F2.wireOp",EDGE,"E3.19.2.2"),sQuery(id+"F2.wireOp",EDGE,"E3.19.2.3"),sQuery(id+"F2.wireOp",EDGE,"E3.19.3.0"),sQuery(id+"F2.wireOp",EDGE,"E3.19.3.1"),sQuery(id+"F2.wireOp",EDGE,"E3.19.3.2"),sQuery(id+"F2.wireOp",EDGE,"E3.19.3.3"),sQuery(id+"F2.wireOp",EDGE,"E3.19.4.0"),sQuery(id+"F2.wireOp",EDGE,"E3.19.4.1"),sQuery(id+"F2.wireOp",EDGE,"E3.19.4.2"),sQuery(id+"F2.wireOp",EDGE,"E3.19.4.3"),sQuery(id+"F2.wireOp",EDGE,"E3.19.5.0"),sQuery(id+"F2.wireOp",EDGE,"E3.19.5.1"),sQuery(id+"F2.wireOp",EDGE,"E3.19.5.2"),sQuery(id+"F2.wireOp",EDGE,"E3.19.5.3"),sQuery(id+"F2.wireOp",EDGE,"E3.19.6.0"),sQuery(id+"F2.wireOp",EDGE,"E3.19.6.1"),sQuery(id+"F2.wireOp",EDGE,"E3.19.6.2"),sQuery(id+"F2.wireOp",EDGE,"E3.19.6.3"),sQuery(id+"F2.wireOp",EDGE,"E3.19.7.0"),sQuery(id+"F2.wireOp",EDGE,"E3.19.7.1"),sQuery(id+"F2.wireOp",EDGE,"E3.19.7.2"),sQuery(id+"F2.wireOp",EDGE,"E3.19.7.3"),sQuery(id+"F2.wireOp",EDGE,"E3.19.8.0"),sQuery(id+"F2.wireOp",EDGE,"E3.19.8.1"),sQuery(id+"F2.wireOp",EDGE,"E3.19.8.2"),sQuery(id+"F2.wireOp",EDGE,"E3.19.8.3"),sQuery(id+"F2.wireOp",EDGE,"E3.19.9.0"),sQuery(id+"F2.wireOp",EDGE,"E3.19.9.1"),sQuery(id+"F2.wireOp",EDGE,"E3.19.9.2"),sQuery(id+"F2.wireOp",EDGE,"E3.19.9.3"),sQuery(id+"F2.wireOp",EDGE,"E3.19.10.0"),sQuery(id+"F2.wireOp",EDGE,"E3.19.10.1"),sQuery(id+"F2.wireOp",EDGE,"E3.19.10.2"),sQuery(id+"F2.wireOp",EDGE,"E3.19.10.3"),sQuery(id+"F2.wireOp",EDGE,"E3.19.11.0"),sQuery(id+"F2.wireOp",EDGE,"E3.19.11.1"),sQuery(id+"F2.wireOp",EDGE,"E3.19.11.2"),sQuery(id+"F2.wireOp",EDGE,"E3.19.11.3"),sQuery(id+"F2.wireOp",EDGE,"E3.19.12.0"),sQuery(id+"F2.wireOp",EDGE,"E3.19.12.1"),sQuery(id+"F2.wireOp",EDGE,"E3.19.12.2"),sQuery(id+"F2.wireOp",EDGE,"E3.19.12.3"),sQuery(id+"F2.wireOp",EDGE,"E3.19.13.0"),sQuery(id+"F2.wireOp",EDGE,"E3.19.13.1"),sQuery(id+"F2.wireOp",EDGE,"E3.19.13.2"),sQuery(id+"F2.wireOp",EDGE,"E3.19.13.3"),sQuery(id+"F2.wireOp",EDGE,"E3.19.14.0"),sQuery(id+"F2.wireOp",EDGE,"E3.19.14.1"),sQuery(id+"F2.wireOp",EDGE,"E3.19.14.2"),sQuery(id+"F2.wireOp",EDGE,"E3.19.14.3"),sQuery(id+"F2.wireOp",EDGE,"E3.19.15.0"),sQuery(id+"F2.wireOp",EDGE,"E3.19.15.1"),sQuery(id+"F2.wireOp",EDGE,"E3.19.15.2"),sQuery(id+"F2.wireOp",EDGE,"E3.19.15.3"),sQuery(id+"F2.wireOp",EDGE,"E3.19.16.0"),sQuery(id+"F2.wireOp",EDGE,"E3.19.16.1"),sQuery(id+"F2.wireOp",EDGE,"E3.19.16.2"),sQuery(id+"F2.wireOp",EDGE,"E3.19.16.3"),sQuery(id+"F2.wireOp",EDGE,"E3.19.17.0"),sQuery(id+"F2.wireOp",EDGE,"E3.19.17.1"),sQuery(id+"F2.wireOp",EDGE,"E3.19.17.2"),sQuery(id+"F2.wireOp",EDGE,"E3.19.17.3"),sQuery(id+"F2.wireOp",EDGE,"E3.19.18.0"),sQuery(id+"F2.wireOp",EDGE,"E3.19.18.1"),sQuery(id+"F2.wireOp",EDGE,"E3.19.18.2"),sQuery(id+"F2.wireOp",EDGE,"E3.19.18.3"),sQuery(id+"F2.wireOp",EDGE,"E3.19.19.0"),sQuery(id+"F2.wireOp",EDGE,"E3.19.19.1"),sQuery(id+"F2.wireOp",EDGE,"E3.19.19.2"),sQuery(id+"F2.wireOp",EDGE,"E3.19.19.3"),sQuery(id+"F2.wireOp",EDGE,"E3.19.20.0"),sQuery(id+"F2.wireOp",EDGE,"E3.19.20.1"),sQuery(id+"F2.wireOp",EDGE,"E3.19.20.2"),sQuery(id+"F2.wireOp",EDGE,"E3.19.20.3"),sQuery(id+"F2.wireOp",EDGE,"E3.19.21.0"),sQuery(id+"F2.wireOp",EDGE,"E3.19.21.1"),sQuery(id+"F2.wireOp",EDGE,"E3.19.21.2"),sQuery(id+"F2.wireOp",EDGE,"E3.19.21.3"),sQuery(id+"F2.wireOp",EDGE,"E3.20.0.0"),sQuery(id+"F2.wireOp",EDGE,"E3.20.0.1"),sQuery(id+"F2.wireOp",EDGE,"E3.20.0.2"),sQuery(id+"F2.wireOp",EDGE,"E3.20.0.3"),sQuery(id+"F2.wireOp",EDGE,"E3.20.1.0"),sQuery(id+"F2.wireOp",EDGE,"E3.20.1.1"),sQuery(id+"F2.wireOp",EDGE,"E3.20.1.2"),sQuery(id+"F2.wireOp",EDGE,"E3.20.1.3"),sQuery(id+"F2.wireOp",EDGE,"E3.20.2.0"),sQuery(id+"F2.wireOp",EDGE,"E3.20.2.1"),sQuery(id+"F2.wireOp",EDGE,"E3.20.2.2"),sQuery(id+"F2.wireOp",EDGE,"E3.20.2.3"),sQuery(id+"F2.wireOp",EDGE,"E3.20.3.0"),sQuery(id+"F2.wireOp",EDGE,"E3.20.3.1"),sQuery(id+"F2.wireOp",EDGE,"E3.20.3.2"),sQuery(id+"F2.wireOp",EDGE,"E3.20.3.3"),sQuery(id+"F2.wireOp",EDGE,"E3.20.4.0"),sQuery(id+"F2.wireOp",EDGE,"E3.20.4.1"),sQuery(id+"F2.wireOp",EDGE,"E3.20.4.2"),sQuery(id+"F2.wireOp",EDGE,"E3.20.4.3"),sQuery(id+"F2.wireOp",EDGE,"E3.20.5.0"),sQuery(id+"F2.wireOp",EDGE,"E3.20.5.1"),sQuery(id+"F2.wireOp",EDGE,"E3.20.5.2"),sQuery(id+"F2.wireOp",EDGE,"E3.20.5.3"),sQuery(id+"F2.wireOp",EDGE,"E3.20.6.0"),sQuery(id+"F2.wireOp",EDGE,"E3.20.6.1"),sQuery(id+"F2.wireOp",EDGE,"E3.20.6.2"),sQuery(id+"F2.wireOp",EDGE,"E3.20.6.3"),sQuery(id+"F2.wireOp",EDGE,"E3.20.7.0"),sQuery(id+"F2.wireOp",EDGE,"E3.20.7.1"),sQuery(id+"F2.wireOp",EDGE,"E3.20.7.2"),sQuery(id+"F2.wireOp",EDGE,"E3.20.7.3"),sQuery(id+"F2.wireOp",EDGE,"E3.20.8.0"),sQuery(id+"F2.wireOp",EDGE,"E3.20.8.1"),sQuery(id+"F2.wireOp",EDGE,"E3.20.8.2"),sQuery(id+"F2.wireOp",EDGE,"E3.20.8.3"),sQuery(id+"F2.wireOp",EDGE,"E3.20.9.0"),sQuery(id+"F2.wireOp",EDGE,"E3.20.9.1"),sQuery(id+"F2.wireOp",EDGE,"E3.20.9.2"),sQuery(id+"F2.wireOp",EDGE,"E3.20.9.3"),sQuery(id+"F2.wireOp",EDGE,"E3.20.10.0"),sQuery(id+"F2.wireOp",EDGE,"E3.20.10.1"),sQuery(id+"F2.wireOp",EDGE,"E3.20.10.2"),sQuery(id+"F2.wireOp",EDGE,"E3.20.10.3"),sQuery(id+"F2.wireOp",EDGE,"E3.20.11.0"),sQuery(id+"F2.wireOp",EDGE,"E3.20.11.1"),sQuery(id+"F2.wireOp",EDGE,"E3.20.11.2"),sQuery(id+"F2.wireOp",EDGE,"E3.20.11.3"),sQuery(id+"F2.wireOp",EDGE,"E3.20.12.0"),sQuery(id+"F2.wireOp",EDGE,"E3.20.12.1"),sQuery(id+"F2.wireOp",EDGE,"E3.20.12.2"),sQuery(id+"F2.wireOp",EDGE,"E3.20.12.3"),sQuery(id+"F2.wireOp",EDGE,"E3.20.13.0"),sQuery(id+"F2.wireOp",EDGE,"E3.20.13.1"),sQuery(id+"F2.wireOp",EDGE,"E3.20.13.2"),sQuery(id+"F2.wireOp",EDGE,"E3.20.13.3"),sQuery(id+"F2.wireOp",EDGE,"E3.20.14.0"),sQuery(id+"F2.wireOp",EDGE,"E3.20.14.1"),sQuery(id+"F2.wireOp",EDGE,"E3.20.14.2"),sQuery(id+"F2.wireOp",EDGE,"E3.20.14.3"),sQuery(id+"F2.wireOp",EDGE,"E3.20.15.0"),sQuery(id+"F2.wireOp",EDGE,"E3.20.15.1"),sQuery(id+"F2.wireOp",EDGE,"E3.20.15.2"),sQuery(id+"F2.wireOp",EDGE,"E3.20.15.3"),sQuery(id+"F2.wireOp",EDGE,"E3.20.16.0"),sQuery(id+"F2.wireOp",EDGE,"E3.20.16.1"),sQuery(id+"F2.wireOp",EDGE,"E3.20.16.2"),sQuery(id+"F2.wireOp",EDGE,"E3.20.16.3"),sQuery(id+"F2.wireOp",EDGE,"E3.20.17.0"),sQuery(id+"F2.wireOp",EDGE,"E3.20.17.1"),sQuery(id+"F2.wireOp",EDGE,"E3.20.17.2"),sQuery(id+"F2.wireOp",EDGE,"E3.20.17.3"),sQuery(id+"F2.wireOp",EDGE,"E3.20.18.0"),sQuery(id+"F2.wireOp",EDGE,"E3.20.18.1"),sQuery(id+"F2.wireOp",EDGE,"E3.20.18.2"),sQuery(id+"F2.wireOp",EDGE,"E3.20.18.3"),sQuery(id+"F2.wireOp",EDGE,"E3.20.19.0"),sQuery(id+"F2.wireOp",EDGE,"E3.20.19.1"),sQuery(id+"F2.wireOp",EDGE,"E3.20.19.2"),sQuery(id+"F2.wireOp",EDGE,"E3.20.19.3"),sQuery(id+"F2.wireOp",EDGE,"E3.20.20.0"),sQuery(id+"F2.wireOp",EDGE,"E3.20.20.1"),sQuery(id+"F2.wireOp",EDGE,"E3.20.20.2"),sQuery(id+"F2.wireOp",EDGE,"E3.20.20.3"),sQuery(id+"F2.wireOp",EDGE,"E3.20.21.0"),sQuery(id+"F2.wireOp",EDGE,"E3.20.21.1"),sQuery(id+"F2.wireOp",EDGE,"E3.20.21.2"),sQuery(id+"F2.wireOp",EDGE,"E3.20.21.3"),sQuery(id+"F2.wireOp",EDGE,"E3.21.0.0"),sQuery(id+"F2.wireOp",EDGE,"E3.21.0.1"),sQuery(id+"F2.wireOp",EDGE,"E3.21.0.2"),sQuery(id+"F2.wireOp",EDGE,"E3.21.0.3"),sQuery(id+"F2.wireOp",EDGE,"E3.21.1.0"),sQuery(id+"F2.wireOp",EDGE,"E3.21.1.1"),sQuery(id+"F2.wireOp",EDGE,"E3.21.1.2"),sQuery(id+"F2.wireOp",EDGE,"E3.21.1.3"),sQuery(id+"F2.wireOp",EDGE,"E3.21.2.0"),sQuery(id+"F2.wireOp",EDGE,"E3.21.2.1"),sQuery(id+"F2.wireOp",EDGE,"E3.21.2.2"),sQuery(id+"F2.wireOp",EDGE,"E3.21.2.3"),sQuery(id+"F2.wireOp",EDGE,"E3.21.3.0"),sQuery(id+"F2.wireOp",EDGE,"E3.21.3.1"),sQuery(id+"F2.wireOp",EDGE,"E3.21.3.2"),sQuery(id+"F2.wireOp",EDGE,"E3.21.3.3"),sQuery(id+"F2.wireOp",EDGE,"E3.21.4.0"),sQuery(id+"F2.wireOp",EDGE,"E3.21.4.1"),sQuery(id+"F2.wireOp",EDGE,"E3.21.4.2"),sQuery(id+"F2.wireOp",EDGE,"E3.21.4.3"),sQuery(id+"F2.wireOp",EDGE,"E3.21.5.0"),sQuery(id+"F2.wireOp",EDGE,"E3.21.5.1"),sQuery(id+"F2.wireOp",EDGE,"E3.21.5.2"),sQuery(id+"F2.wireOp",EDGE,"E3.21.5.3"),sQuery(id+"F2.wireOp",EDGE,"E3.21.6.0"),sQuery(id+"F2.wireOp",EDGE,"E3.21.6.1"),sQuery(id+"F2.wireOp",EDGE,"E3.21.6.2"),sQuery(id+"F2.wireOp",EDGE,"E3.21.6.3"),sQuery(id+"F2.wireOp",EDGE,"E3.21.7.0"),sQuery(id+"F2.wireOp",EDGE,"E3.21.7.1"),sQuery(id+"F2.wireOp",EDGE,"E3.21.7.2"),sQuery(id+"F2.wireOp",EDGE,"E3.21.7.3"),sQuery(id+"F2.wireOp",EDGE,"E3.21.8.0"),sQuery(id+"F2.wireOp",EDGE,"E3.21.8.1"),sQuery(id+"F2.wireOp",EDGE,"E3.21.8.2"),sQuery(id+"F2.wireOp",EDGE,"E3.21.8.3"),sQuery(id+"F2.wireOp",EDGE,"E3.21.9.0"),sQuery(id+"F2.wireOp",EDGE,"E3.21.9.1"),sQuery(id+"F2.wireOp",EDGE,"E3.21.9.2"),sQuery(id+"F2.wireOp",EDGE,"E3.21.9.3"),sQuery(id+"F2.wireOp",EDGE,"E3.21.10.0"),sQuery(id+"F2.wireOp",EDGE,"E3.21.10.1"),sQuery(id+"F2.wireOp",EDGE,"E3.21.10.2"),sQuery(id+"F2.wireOp",EDGE,"E3.21.10.3"),sQuery(id+"F2.wireOp",EDGE,"E3.21.11.0"),sQuery(id+"F2.wireOp",EDGE,"E3.21.11.1"),sQuery(id+"F2.wireOp",EDGE,"E3.21.11.2"),sQuery(id+"F2.wireOp",EDGE,"E3.21.11.3"),sQuery(id+"F2.wireOp",EDGE,"E3.21.12.0"),sQuery(id+"F2.wireOp",EDGE,"E3.21.12.1"),sQuery(id+"F2.wireOp",EDGE,"E3.21.12.2"),sQuery(id+"F2.wireOp",EDGE,"E3.21.12.3"),sQuery(id+"F2.wireOp",EDGE,"E3.21.13.0"),sQuery(id+"F2.wireOp",EDGE,"E3.21.13.1"),sQuery(id+"F2.wireOp",EDGE,"E3.21.13.2"),sQuery(id+"F2.wireOp",EDGE,"E3.21.13.3"),sQuery(id+"F2.wireOp",EDGE,"E3.21.14.0"),sQuery(id+"F2.wireOp",EDGE,"E3.21.14.1"),sQuery(id+"F2.wireOp",EDGE,"E3.21.14.2"),sQuery(id+"F2.wireOp",EDGE,"E3.21.14.3"),sQuery(id+"F2.wireOp",EDGE,"E3.21.15.0"),sQuery(id+"F2.wireOp",EDGE,"E3.21.15.1"),sQuery(id+"F2.wireOp",EDGE,"E3.21.15.2"),sQuery(id+"F2.wireOp",EDGE,"E3.21.15.3"),sQuery(id+"F2.wireOp",EDGE,"E3.21.16.0"),sQuery(id+"F2.wireOp",EDGE,"E3.21.16.1"),sQuery(id+"F2.wireOp",EDGE,"E3.21.16.2"),sQuery(id+"F2.wireOp",EDGE,"E3.21.16.3"),sQuery(id+"F2.wireOp",EDGE,"E3.21.17.0"),sQuery(id+"F2.wireOp",EDGE,"E3.21.17.1"),sQuery(id+"F2.wireOp",EDGE,"E3.21.17.2"),sQuery(id+"F2.wireOp",EDGE,"E3.21.17.3"),sQuery(id+"F2.wireOp",EDGE,"E3.21.18.0"),sQuery(id+"F2.wireOp",EDGE,"E3.21.18.1"),sQuery(id+"F2.wireOp",EDGE,"E3.21.18.2"),sQuery(id+"F2.wireOp",EDGE,"E3.21.18.3"),sQuery(id+"F2.wireOp",EDGE,"E3.21.19.0"),sQuery(id+"F2.wireOp",EDGE,"E3.21.19.1"),sQuery(id+"F2.wireOp",EDGE,"E3.21.19.2"),sQuery(id+"F2.wireOp",EDGE,"E3.21.19.3"),sQuery(id+"F2.wireOp",EDGE,"E3.21.20.0"),sQuery(id+"F2.wireOp",EDGE,"E3.21.20.1"),sQuery(id+"F2.wireOp",EDGE,"E3.21.20.2"),sQuery(id+"F2.wireOp",EDGE,"E3.21.20.3"),sQuery(id+"F2.wireOp",EDGE,"E3.21.21.0"),sQuery(id+"F2.wireOp",EDGE,"E3.21.21.1"),sQuery(id+"F2.wireOp",EDGE,"E3.21.21.2"),sQuery(id+"F2.wireOp",EDGE,"E3.21.21.3"),sQuery(id+"F2.wireOp",EDGE,"E3.22.0.0"),sQuery(id+"F2.wireOp",EDGE,"E3.22.0.1"),sQuery(id+"F2.wireOp",EDGE,"E3.22.0.2"),sQuery(id+"F2.wireOp",EDGE,"E3.22.0.3"),sQuery(id+"F2.wireOp",EDGE,"E3.22.1.0"),sQuery(id+"F2.wireOp",EDGE,"E3.22.1.1"),sQuery(id+"F2.wireOp",EDGE,"E3.22.1.2"),sQuery(id+"F2.wireOp",EDGE,"E3.22.1.3"),sQuery(id+"F2.wireOp",EDGE,"E3.22.2.0"),sQuery(id+"F2.wireOp",EDGE,"E3.22.2.1"),sQuery(id+"F2.wireOp",EDGE,"E3.22.2.2"),sQuery(id+"F2.wireOp",EDGE,"E3.22.2.3"),sQuery(id+"F2.wireOp",EDGE,"E3.22.3.0"),sQuery(id+"F2.wireOp",EDGE,"E3.22.3.1"),sQuery(id+"F2.wireOp",EDGE,"E3.22.3.2"),sQuery(id+"F2.wireOp",EDGE,"E3.22.3.3"),sQuery(id+"F2.wireOp",EDGE,"E3.22.4.0"),sQuery(id+"F2.wireOp",EDGE,"E3.22.4.1"),sQuery(id+"F2.wireOp",EDGE,"E3.22.4.2"),sQuery(id+"F2.wireOp",EDGE,"E3.22.4.3"),sQuery(id+"F2.wireOp",EDGE,"E3.22.5.0"),sQuery(id+"F2.wireOp",EDGE,"E3.22.5.1"),sQuery(id+"F2.wireOp",EDGE,"E3.22.5.2"),sQuery(id+"F2.wireOp",EDGE,"E3.22.5.3"),sQuery(id+"F2.wireOp",EDGE,"E3.22.6.0"),sQuery(id+"F2.wireOp",EDGE,"E3.22.6.1"),sQuery(id+"F2.wireOp",EDGE,"E3.22.6.2"),sQuery(id+"F2.wireOp",EDGE,"E3.22.6.3"),sQuery(id+"F2.wireOp",EDGE,"E3.22.7.0"),sQuery(id+"F2.wireOp",EDGE,"E3.22.7.1"),sQuery(id+"F2.wireOp",EDGE,"E3.22.7.2"),sQuery(id+"F2.wireOp",EDGE,"E3.22.7.3"),sQuery(id+"F2.wireOp",EDGE,"E3.22.8.0"),sQuery(id+"F2.wireOp",EDGE,"E3.22.8.1"),sQuery(id+"F2.wireOp",EDGE,"E3.22.8.2"),sQuery(id+"F2.wireOp",EDGE,"E3.22.8.3"),sQuery(id+"F2.wireOp",EDGE,"E3.22.9.0"),sQuery(id+"F2.wireOp",EDGE,"E3.22.9.1"),sQuery(id+"F2.wireOp",EDGE,"E3.22.9.2"),sQuery(id+"F2.wireOp",EDGE,"E3.22.9.3"),sQuery(id+"F2.wireOp",EDGE,"E3.22.10.0"),sQuery(id+"F2.wireOp",EDGE,"E3.22.10.1"),sQuery(id+"F2.wireOp",EDGE,"E3.22.10.2"),sQuery(id+"F2.wireOp",EDGE,"E3.22.10.3"),sQuery(id+"F2.wireOp",EDGE,"E3.22.11.0"),sQuery(id+"F2.wireOp",EDGE,"E3.22.11.1"),sQuery(id+"F2.wireOp",EDGE,"E3.22.11.2"),sQuery(id+"F2.wireOp",EDGE,"E3.22.11.3"),sQuery(id+"F2.wireOp",EDGE,"E3.22.12.0"),sQuery(id+"F2.wireOp",EDGE,"E3.22.12.1"),sQuery(id+"F2.wireOp",EDGE,"E3.22.12.2"),sQuery(id+"F2.wireOp",EDGE,"E3.22.12.3"),sQuery(id+"F2.wireOp",EDGE,"E3.22.13.0"),sQuery(id+"F2.wireOp",EDGE,"E3.22.13.1"),sQuery(id+"F2.wireOp",EDGE,"E3.22.13.2"),sQuery(id+"F2.wireOp",EDGE,"E3.22.13.3"),sQuery(id+"F2.wireOp",EDGE,"E3.22.14.0"),sQuery(id+"F2.wireOp",EDGE,"E3.22.14.1"),sQuery(id+"F2.wireOp",EDGE,"E3.22.14.2"),sQuery(id+"F2.wireOp",EDGE,"E3.22.14.3"),sQuery(id+"F2.wireOp",EDGE,"E3.22.15.0"),sQuery(id+"F2.wireOp",EDGE,"E3.22.15.1"),sQuery(id+"F2.wireOp",EDGE,"E3.22.15.2"),sQuery(id+"F2.wireOp",EDGE,"E3.22.15.3"),sQuery(id+"F2.wireOp",EDGE,"E3.22.16.0"),sQuery(id+"F2.wireOp",EDGE,"E3.22.16.1"),sQuery(id+"F2.wireOp",EDGE,"E3.22.16.2"),sQuery(id+"F2.wireOp",EDGE,"E3.22.16.3"),sQuery(id+"F2.wireOp",EDGE,"E3.22.17.0"),sQuery(id+"F2.wireOp",EDGE,"E3.22.17.1"),sQuery(id+"F2.wireOp",EDGE,"E3.22.17.2"),sQuery(id+"F2.wireOp",EDGE,"E3.22.17.3"),sQuery(id+"F2.wireOp",EDGE,"E3.22.18.0"),sQuery(id+"F2.wireOp",EDGE,"E3.22.18.1"),sQuery(id+"F2.wireOp",EDGE,"E3.22.18.2"),sQuery(id+"F2.wireOp",EDGE,"E3.22.18.3"),sQuery(id+"F2.wireOp",EDGE,"E3.22.19.0"),sQuery(id+"F2.wireOp",EDGE,"E3.22.19.1"),sQuery(id+"F2.wireOp",EDGE,"E3.22.19.2"),sQuery(id+"F2.wireOp",EDGE,"E3.22.19.3"),sQuery(id+"F2.wireOp",EDGE,"E3.22.20.0"),sQuery(id+"F2.wireOp",EDGE,"E3.22.20.1"),sQuery(id+"F2.wireOp",EDGE,"E3.22.20.2"),sQuery(id+"F2.wireOp",EDGE,"E3.22.20.3"),sQuery(id+"F2.wireOp",EDGE,"E3.22.21.0"),sQuery(id+"F2.wireOp",EDGE,"E3.22.21.1"),sQuery(id+"F2.wireOp",EDGE,"E3.22.21.2"),sQuery(id+"F2.wireOp",EDGE,"E3.22.21.3"),sQuery(id+"F2.wireOp",EDGE,"E3.23.0.0"),sQuery(id+"F2.wireOp",EDGE,"E3.23.0.1"),sQuery(id+"F2.wireOp",EDGE,"E3.23.0.2"),sQuery(id+"F2.wireOp",EDGE,"E3.23.0.3"),sQuery(id+"F2.wireOp",EDGE,"E3.23.1.0"),sQuery(id+"F2.wireOp",EDGE,"E3.23.1.1"),sQuery(id+"F2.wireOp",EDGE,"E3.23.1.2"),sQuery(id+"F2.wireOp",EDGE,"E3.23.1.3"),sQuery(id+"F2.wireOp",EDGE,"E3.23.2.0"),sQuery(id+"F2.wireOp",EDGE,"E3.23.2.1"),sQuery(id+"F2.wireOp",EDGE,"E3.23.2.2"),sQuery(id+"F2.wireOp",EDGE,"E3.23.2.3"),sQuery(id+"F2.wireOp",EDGE,"E3.23.3.0"),sQuery(id+"F2.wireOp",EDGE,"E3.23.3.1"),sQuery(id+"F2.wireOp",EDGE,"E3.23.3.2"),sQuery(id+"F2.wireOp",EDGE,"E3.23.3.3"),sQuery(id+"F2.wireOp",EDGE,"E3.23.4.0"),sQuery(id+"F2.wireOp",EDGE,"E3.23.4.1"),sQuery(id+"F2.wireOp",EDGE,"E3.23.4.2"),sQuery(id+"F2.wireOp",EDGE,"E3.23.4.3"),sQuery(id+"F2.wireOp",EDGE,"E3.23.5.0"),sQuery(id+"F2.wireOp",EDGE,"E3.23.5.1"),sQuery(id+"F2.wireOp",EDGE,"E3.23.5.2"),sQuery(id+"F2.wireOp",EDGE,"E3.23.5.3"),sQuery(id+"F2.wireOp",EDGE,"E3.23.6.0"),sQuery(id+"F2.wireOp",EDGE,"E3.23.6.1"),sQuery(id+"F2.wireOp",EDGE,"E3.23.6.2"),sQuery(id+"F2.wireOp",EDGE,"E3.23.6.3"),sQuery(id+"F2.wireOp",EDGE,"E3.23.7.0"),sQuery(id+"F2.wireOp",EDGE,"E3.23.7.1"),sQuery(id+"F2.wireOp",EDGE,"E3.23.7.2"),sQuery(id+"F2.wireOp",EDGE,"E3.23.7.3"),sQuery(id+"F2.wireOp",EDGE,"E3.23.8.0"),sQuery(id+"F2.wireOp",EDGE,"E3.23.8.1"),sQuery(id+"F2.wireOp",EDGE,"E3.23.8.2"),sQuery(id+"F2.wireOp",EDGE,"E3.23.8.3"),sQuery(id+"F2.wireOp",EDGE,"E3.23.9.0"),sQuery(id+"F2.wireOp",EDGE,"E3.23.9.1"),sQuery(id+"F2.wireOp",EDGE,"E3.23.9.2"),sQuery(id+"F2.wireOp",EDGE,"E3.23.9.3"),sQuery(id+"F2.wireOp",EDGE,"E3.23.10.0"),sQuery(id+"F2.wireOp",EDGE,"E3.23.10.1"),sQuery(id+"F2.wireOp",EDGE,"E3.23.10.2"),sQuery(id+"F2.wireOp",EDGE,"E3.23.10.3"),sQuery(id+"F2.wireOp",EDGE,"E3.23.11.0"),sQuery(id+"F2.wireOp",EDGE,"E3.23.11.1"),sQuery(id+"F2.wireOp",EDGE,"E3.23.11.2"),sQuery(id+"F2.wireOp",EDGE,"E3.23.11.3"),sQuery(id+"F2.wireOp",EDGE,"E3.23.12.0"),sQuery(id+"F2.wireOp",EDGE,"E3.23.12.1"),sQuery(id+"F2.wireOp",EDGE,"E3.23.12.2"),sQuery(id+"F2.wireOp",EDGE,"E3.23.12.3"),sQuery(id+"F2.wireOp",EDGE,"E3.23.13.0"),sQuery(id+"F2.wireOp",EDGE,"E3.23.13.1"),sQuery(id+"F2.wireOp",EDGE,"E3.23.13.2"),sQuery(id+"F2.wireOp",EDGE,"E3.23.13.3"),sQuery(id+"F2.wireOp",EDGE,"E3.23.14.0"),sQuery(id+"F2.wireOp",EDGE,"E3.23.14.1"),sQuery(id+"F2.wireOp",EDGE,"E3.23.14.2"),sQuery(id+"F2.wireOp",EDGE,"E3.23.14.3"),sQuery(id+"F2.wireOp",EDGE,"E3.23.15.0"),sQuery(id+"F2.wireOp",EDGE,"E3.23.15.1"),sQuery(id+"F2.wireOp",EDGE,"E3.23.15.2"),sQuery(id+"F2.wireOp",EDGE,"E3.23.15.3"),sQuery(id+"F2.wireOp",EDGE,"E3.23.16.0"),sQuery(id+"F2.wireOp",EDGE,"E3.23.16.1"),sQuery(id+"F2.wireOp",EDGE,"E3.23.16.2"),sQuery(id+"F2.wireOp",EDGE,"E3.23.16.3"),sQuery(id+"F2.wireOp",EDGE,"E3.23.17.0"),sQuery(id+"F2.wireOp",EDGE,"E3.23.17.1"),sQuery(id+"F2.wireOp",EDGE,"E3.23.17.2"),sQuery(id+"F2.wireOp",EDGE,"E3.23.17.3"),sQuery(id+"F2.wireOp",EDGE,"E3.23.18.0"),sQuery(id+"F2.wireOp",EDGE,"E3.23.18.1"),sQuery(id+"F2.wireOp",EDGE,"E3.23.18.2"),sQuery(id+"F2.wireOp",EDGE,"E3.23.18.3"),sQuery(id+"F2.wireOp",EDGE,"E3.23.19.0"),sQuery(id+"F2.wireOp",EDGE,"E3.23.19.1"),sQuery(id+"F2.wireOp",EDGE,"E3.23.19.2"),sQuery(id+"F2.wireOp",EDGE,"E3.23.19.3"),sQuery(id+"F2.wireOp",EDGE,"E3.23.20.0"),sQuery(id+"F2.wireOp",EDGE,"E3.23.20.1"),sQuery(id+"F2.wireOp",EDGE,"E3.23.20.2"),sQuery(id+"F2.wireOp",EDGE,"E3.23.20.3"),sQuery(id+"F2.wireOp",EDGE,"E3.23.21.0"),sQuery(id+"F2.wireOp",EDGE,"E3.23.21.1"),sQuery(id+"F2.wireOp",EDGE,"E3.23.21.2"),sQuery(id+"F2.wireOp",EDGE,"E3.23.21.3"),sQuery(id+"F2.wireOp",EDGE,"E3.24.0.0"),sQuery(id+"F2.wireOp",EDGE,"E3.24.0.1"),sQuery(id+"F2.wireOp",EDGE,"E3.24.0.2"),sQuery(id+"F2.wireOp",EDGE,"E3.24.0.3"),sQuery(id+"F2.wireOp",EDGE,"E3.24.1.0"),sQuery(id+"F2.wireOp",EDGE,"E3.24.1.1"),sQuery(id+"F2.wireOp",EDGE,"E3.24.1.2"),sQuery(id+"F2.wireOp",EDGE,"E3.24.1.3"),sQuery(id+"F2.wireOp",EDGE,"E3.24.2.0"),sQuery(id+"F2.wireOp",EDGE,"E3.24.2.1"),sQuery(id+"F2.wireOp",EDGE,"E3.24.2.2"),sQuery(id+"F2.wireOp",EDGE,"E3.24.2.3"),sQuery(id+"F2.wireOp",EDGE,"E3.24.3.0"),sQuery(id+"F2.wireOp",EDGE,"E3.24.3.1"),sQuery(id+"F2.wireOp",EDGE,"E3.24.3.2"),sQuery(id+"F2.wireOp",EDGE,"E3.24.3.3"),sQuery(id+"F2.wireOp",EDGE,"E3.24.4.0"),sQuery(id+"F2.wireOp",EDGE,"E3.24.4.1"),sQuery(id+"F2.wireOp",EDGE,"E3.24.4.2"),sQuery(id+"F2.wireOp",EDGE,"E3.24.4.3"),sQuery(id+"F2.wireOp",EDGE,"E3.24.5.0"),sQuery(id+"F2.wireOp",EDGE,"E3.24.5.1"),sQuery(id+"F2.wireOp",EDGE,"E3.24.5.2"),sQuery(id+"F2.wireOp",EDGE,"E3.24.5.3"),sQuery(id+"F2.wireOp",EDGE,"E3.24.6.0"),sQuery(id+"F2.wireOp",EDGE,"E3.24.6.1"),sQuery(id+"F2.wireOp",EDGE,"E3.24.6.2"),sQuery(id+"F2.wireOp",EDGE,"E3.24.6.3"),sQuery(id+"F2.wireOp",EDGE,"E3.24.7.0"),sQuery(id+"F2.wireOp",EDGE,"E3.24.7.1"),sQuery(id+"F2.wireOp",EDGE,"E3.24.7.2"),sQuery(id+"F2.wireOp",EDGE,"E3.24.7.3"),sQuery(id+"F2.wireOp",EDGE,"E3.24.8.0"),sQuery(id+"F2.wireOp",EDGE,"E3.24.8.1"),sQuery(id+"F2.wireOp",EDGE,"E3.24.8.2"),sQuery(id+"F2.wireOp",EDGE,"E3.24.8.3"),sQuery(id+"F2.wireOp",EDGE,"E3.24.9.0"),sQuery(id+"F2.wireOp",EDGE,"E3.24.9.1"),sQuery(id+"F2.wireOp",EDGE,"E3.24.9.2"),sQuery(id+"F2.wireOp",EDGE,"E3.24.9.3"),sQuery(id+"F2.wireOp",EDGE,"E3.24.10.0"),sQuery(id+"F2.wireOp",EDGE,"E3.24.10.1"),sQuery(id+"F2.wireOp",EDGE,"E3.24.10.2"),sQuery(id+"F2.wireOp",EDGE,"E3.24.10.3"),sQuery(id+"F2.wireOp",EDGE,"E3.24.11.0"),sQuery(id+"F2.wireOp",EDGE,"E3.24.11.1"),sQuery(id+"F2.wireOp",EDGE,"E3.24.11.2"),sQuery(id+"F2.wireOp",EDGE,"E3.24.11.3"),sQuery(id+"F2.wireOp",EDGE,"E3.24.12.0"),sQuery(id+"F2.wireOp",EDGE,"E3.24.12.1"),sQuery(id+"F2.wireOp",EDGE,"E3.24.12.2"),sQuery(id+"F2.wireOp",EDGE,"E3.24.12.3"),sQuery(id+"F2.wireOp",EDGE,"E3.24.13.0"),sQuery(id+"F2.wireOp",EDGE,"E3.24.13.1"),sQuery(id+"F2.wireOp",EDGE,"E3.24.13.2"),sQuery(id+"F2.wireOp",EDGE,"E3.24.13.3"),sQuery(id+"F2.wireOp",EDGE,"E3.24.14.0"),sQuery(id+"F2.wireOp",EDGE,"E3.24.14.1"),sQuery(id+"F2.wireOp",EDGE,"E3.24.14.2"),sQuery(id+"F2.wireOp",EDGE,"E3.24.14.3"),sQuery(id+"F2.wireOp",EDGE,"E3.24.15.0"),sQuery(id+"F2.wireOp",EDGE,"E3.24.15.1"),sQuery(id+"F2.wireOp",EDGE,"E3.24.15.2"),sQuery(id+"F2.wireOp",EDGE,"E3.24.15.3"),sQuery(id+"F2.wireOp",EDGE,"E3.24.16.0"),sQuery(id+"F2.wireOp",EDGE,"E3.24.16.1"),sQuery(id+"F2.wireOp",EDGE,"E3.24.16.2"),sQuery(id+"F2.wireOp",EDGE,"E3.24.16.3"),sQuery(id+"F2.wireOp",EDGE,"E3.24.17.0"),sQuery(id+"F2.wireOp",EDGE,"E3.24.17.1"),sQuery(id+"F2.wireOp",EDGE,"E3.24.17.2"),sQuery(id+"F2.wireOp",EDGE,"E3.24.17.3"),sQuery(id+"F2.wireOp",EDGE,"E3.24.18.0"),sQuery(id+"F2.wireOp",EDGE,"E3.24.18.1"),sQuery(id+"F2.wireOp",EDGE,"E3.24.18.2"),sQuery(id+"F2.wireOp",EDGE,"E3.24.18.3"),sQuery(id+"F2.wireOp",EDGE,"E3.24.19.0"),sQuery(id+"F2.wireOp",EDGE,"E3.24.19.1"),sQuery(id+"F2.wireOp",EDGE,"E3.24.19.2"),sQuery(id+"F2.wireOp",EDGE,"E3.24.19.3"),sQuery(id+"F2.wireOp",EDGE,"E3.24.20.0"),sQuery(id+"F2.wireOp",EDGE,"E3.24.20.1"),sQuery(id+"F2.wireOp",EDGE,"E3.24.20.2"),sQuery(id+"F2.wireOp",EDGE,"E3.24.20.3"),sQuery(id+"F2.wireOp",EDGE,"E3.24.21.0"),sQuery(id+"F2.wireOp",EDGE,"E3.24.21.1"),sQuery(id+"F2.wireOp",EDGE,"E3.24.21.2"),sQuery(id+"F2.wireOp",EDGE,"E3.24.21.3"),sQuery(id+"F2.wireOp",EDGE,"E3.25.0.0"),sQuery(id+"F2.wireOp",EDGE,"E3.25.0.1"),sQuery(id+"F2.wireOp",EDGE,"E3.25.0.2"),sQuery(id+"F2.wireOp",EDGE,"E3.25.0.3"),sQuery(id+"F2.wireOp",EDGE,"E3.25.1.0"),sQuery(id+"F2.wireOp",EDGE,"E3.25.1.1"),sQuery(id+"F2.wireOp",EDGE,"E3.25.1.2"),sQuery(id+"F2.wireOp",EDGE,"E3.25.1.3"),sQuery(id+"F2.wireOp",EDGE,"E3.25.2.0"),sQuery(id+"F2.wireOp",EDGE,"E3.25.2.1"),sQuery(id+"F2.wireOp",EDGE,"E3.25.2.2"),sQuery(id+"F2.wireOp",EDGE,"E3.25.2.3"),sQuery(id+"F2.wireOp",EDGE,"E3.25.3.0"),sQuery(id+"F2.wireOp",EDGE,"E3.25.3.1"),sQuery(id+"F2.wireOp",EDGE,"E3.25.3.2"),sQuery(id+"F2.wireOp",EDGE,"E3.25.3.3"),sQuery(id+"F2.wireOp",EDGE,"E3.25.4.0"),sQuery(id+"F2.wireOp",EDGE,"E3.25.4.1"),sQuery(id+"F2.wireOp",EDGE,"E3.25.4.2"),sQuery(id+"F2.wireOp",EDGE,"E3.25.4.3"),sQuery(id+"F2.wireOp",EDGE,"E3.25.5.0"),sQuery(id+"F2.wireOp",EDGE,"E3.25.5.1"),sQuery(id+"F2.wireOp",EDGE,"E3.25.5.2"),sQuery(id+"F2.wireOp",EDGE,"E3.25.5.3"),sQuery(id+"F2.wireOp",EDGE,"E3.25.6.0"),sQuery(id+"F2.wireOp",EDGE,"E3.25.6.1"),sQuery(id+"F2.wireOp",EDGE,"E3.25.6.2"),sQuery(id+"F2.wireOp",EDGE,"E3.25.6.3"),sQuery(id+"F2.wireOp",EDGE,"E3.25.7.0"),sQuery(id+"F2.wireOp",EDGE,"E3.25.7.1"),sQuery(id+"F2.wireOp",EDGE,"E3.25.7.2"),sQuery(id+"F2.wireOp",EDGE,"E3.25.7.3"),sQuery(id+"F2.wireOp",EDGE,"E3.25.8.0"),sQuery(id+"F2.wireOp",EDGE,"E3.25.8.1"),sQuery(id+"F2.wireOp",EDGE,"E3.25.8.2"),sQuery(id+"F2.wireOp",EDGE,"E3.25.8.3"),sQuery(id+"F2.wireOp",EDGE,"E3.25.9.0"),sQuery(id+"F2.wireOp",EDGE,"E3.25.9.1"),sQuery(id+"F2.wireOp",EDGE,"E3.25.9.2"),sQuery(id+"F2.wireOp",EDGE,"E3.25.9.3"),sQuery(id+"F2.wireOp",EDGE,"E3.25.10.0"),sQuery(id+"F2.wireOp",EDGE,"E3.25.10.1"),sQuery(id+"F2.wireOp",EDGE,"E3.25.10.2"),sQuery(id+"F2.wireOp",EDGE,"E3.25.10.3"),sQuery(id+"F2.wireOp",EDGE,"E3.25.11.0"),sQuery(id+"F2.wireOp",EDGE,"E3.25.11.1"),sQuery(id+"F2.wireOp",EDGE,"E3.25.11.2"),sQuery(id+"F2.wireOp",EDGE,"E3.25.11.3"),sQuery(id+"F2.wireOp",EDGE,"E3.25.12.0"),sQuery(id+"F2.wireOp",EDGE,"E3.25.12.1"),sQuery(id+"F2.wireOp",EDGE,"E3.25.12.2"),sQuery(id+"F2.wireOp",EDGE,"E3.25.12.3"),sQuery(id+"F2.wireOp",EDGE,"E3.25.13.0"),sQuery(id+"F2.wireOp",EDGE,"E3.25.13.1"),sQuery(id+"F2.wireOp",EDGE,"E3.25.13.2"),sQuery(id+"F2.wireOp",EDGE,"E3.25.13.3"),sQuery(id+"F2.wireOp",EDGE,"E3.25.14.0"),sQuery(id+"F2.wireOp",EDGE,"E3.25.14.1"),sQuery(id+"F2.wireOp",EDGE,"E3.25.14.2"),sQuery(id+"F2.wireOp",EDGE,"E3.25.14.3"),sQuery(id+"F2.wireOp",EDGE,"E3.25.15.0"),sQuery(id+"F2.wireOp",EDGE,"E3.25.15.1"),sQuery(id+"F2.wireOp",EDGE,"E3.25.15.2"),sQuery(id+"F2.wireOp",EDGE,"E3.25.15.3"),sQuery(id+"F2.wireOp",EDGE,"E3.25.16.0"),sQuery(id+"F2.wireOp",EDGE,"E3.25.16.1"),sQuery(id+"F2.wireOp",EDGE,"E3.25.16.2"),sQuery(id+"F2.wireOp",EDGE,"E3.25.16.3"),sQuery(id+"F2.wireOp",EDGE,"E3.25.17.0"),sQuery(id+"F2.wireOp",EDGE,"E3.25.17.1"),sQuery(id+"F2.wireOp",EDGE,"E3.25.17.2"),sQuery(id+"F2.wireOp",EDGE,"E3.25.17.3"),sQuery(id+"F2.wireOp",EDGE,"E3.25.18.0"),sQuery(id+"F2.wireOp",EDGE,"E3.25.18.1"),sQuery(id+"F2.wireOp",EDGE,"E3.25.18.2"),sQuery(id+"F2.wireOp",EDGE,"E3.25.18.3"),sQuery(id+"F2.wireOp",EDGE,"E3.25.19.0"),sQuery(id+"F2.wireOp",EDGE,"E3.25.19.1"),sQuery(id+"F2.wireOp",EDGE,"E3.25.19.2"),sQuery(id+"F2.wireOp",EDGE,"E3.25.19.3"),sQuery(id+"F2.wireOp",EDGE,"E3.25.20.0"),sQuery(id+"F2.wireOp",EDGE,"E3.25.20.1"),sQuery(id+"F2.wireOp",EDGE,"E3.25.20.2"),sQuery(id+"F2.wireOp",EDGE,"E3.25.20.3"),sQuery(id+"F2.wireOp",EDGE,"E3.25.21.0"),sQuery(id+"F2.wireOp",EDGE,"E3.25.21.1"),sQuery(id+"F2.wireOp",EDGE,"E3.25.21.2"),sQuery(id+"F2.wireOp",EDGE,"E3.25.21.3"),sQuery(id+"F2.wireOp",EDGE,"E3.26.0.0"),sQuery(id+"F2.wireOp",EDGE,"E3.26.0.1"),sQuery(id+"F2.wireOp",EDGE,"E3.26.0.2"),sQuery(id+"F2.wireOp",EDGE,"E3.26.0.3"),sQuery(id+"F2.wireOp",EDGE,"E3.26.1.0"),sQuery(id+"F2.wireOp",EDGE,"E3.26.1.1"),sQuery(id+"F2.wireOp",EDGE,"E3.26.1.2"),sQuery(id+"F2.wireOp",EDGE,"E3.26.1.3"),sQuery(id+"F2.wireOp",EDGE,"E3.26.2.0"),sQuery(id+"F2.wireOp",EDGE,"E3.26.2.1"),sQuery(id+"F2.wireOp",EDGE,"E3.26.2.2"),sQuery(id+"F2.wireOp",EDGE,"E3.26.2.3"),sQuery(id+"F2.wireOp",EDGE,"E3.26.3.0"),sQuery(id+"F2.wireOp",EDGE,"E3.26.3.1"),sQuery(id+"F2.wireOp",EDGE,"E3.26.3.2"),sQuery(id+"F2.wireOp",EDGE,"E3.26.3.3"),sQuery(id+"F2.wireOp",EDGE,"E3.26.4.0"),sQuery(id+"F2.wireOp",EDGE,"E3.26.4.1"),sQuery(id+"F2.wireOp",EDGE,"E3.26.4.2"),sQuery(id+"F2.wireOp",EDGE,"E3.26.4.3"),sQuery(id+"F2.wireOp",EDGE,"E3.26.5.0"),sQuery(id+"F2.wireOp",EDGE,"E3.26.5.1"),sQuery(id+"F2.wireOp",EDGE,"E3.26.5.2"),sQuery(id+"F2.wireOp",EDGE,"E3.26.5.3"),sQuery(id+"F2.wireOp",EDGE,"E3.26.6.0"),sQuery(id+"F2.wireOp",EDGE,"E3.26.6.1"),sQuery(id+"F2.wireOp",EDGE,"E3.26.6.2"),sQuery(id+"F2.wireOp",EDGE,"E3.26.6.3"),sQuery(id+"F2.wireOp",EDGE,"E3.26.7.0"),sQuery(id+"F2.wireOp",EDGE,"E3.26.7.1"),sQuery(id+"F2.wireOp",EDGE,"E3.26.7.2"),sQuery(id+"F2.wireOp",EDGE,"E3.26.7.3"),sQuery(id+"F2.wireOp",EDGE,"E3.26.8.0"),sQuery(id+"F2.wireOp",EDGE,"E3.26.8.1"),sQuery(id+"F2.wireOp",EDGE,"E3.26.8.2"),sQuery(id+"F2.wireOp",EDGE,"E3.26.8.3"),sQuery(id+"F2.wireOp",EDGE,"E3.26.9.0"),sQuery(id+"F2.wireOp",EDGE,"E3.26.9.1"),sQuery(id+"F2.wireOp",EDGE,"E3.26.9.2"),sQuery(id+"F2.wireOp",EDGE,"E3.26.9.3"),sQuery(id+"F2.wireOp",EDGE,"E3.26.10.0"),sQuery(id+"F2.wireOp",EDGE,"E3.26.10.1"),sQuery(id+"F2.wireOp",EDGE,"E3.26.10.2"),sQuery(id+"F2.wireOp",EDGE,"E3.26.10.3"),sQuery(id+"F2.wireOp",EDGE,"E3.26.11.0"),sQuery(id+"F2.wireOp",EDGE,"E3.26.11.1"),sQuery(id+"F2.wireOp",EDGE,"E3.26.11.2"),sQuery(id+"F2.wireOp",EDGE,"E3.26.11.3"),sQuery(id+"F2.wireOp",EDGE,"E3.26.12.0"),sQuery(id+"F2.wireOp",EDGE,"E3.26.12.1"),sQuery(id+"F2.wireOp",EDGE,"E3.26.12.2"),sQuery(id+"F2.wireOp",EDGE,"E3.26.12.3"),sQuery(id+"F2.wireOp",EDGE,"E3.26.13.0"),sQuery(id+"F2.wireOp",EDGE,"E3.26.13.1"),sQuery(id+"F2.wireOp",EDGE,"E3.26.13.2"),sQuery(id+"F2.wireOp",EDGE,"E3.26.13.3"),sQuery(id+"F2.wireOp",EDGE,"E3.26.14.0"),sQuery(id+"F2.wireOp",EDGE,"E3.26.14.1"),sQuery(id+"F2.wireOp",EDGE,"E3.26.14.2"),sQuery(id+"F2.wireOp",EDGE,"E3.26.14.3"),sQuery(id+"F2.wireOp",EDGE,"E3.26.15.0"),sQuery(id+"F2.wireOp",EDGE,"E3.26.15.1"),sQuery(id+"F2.wireOp",EDGE,"E3.26.15.2"),sQuery(id+"F2.wireOp",EDGE,"E3.26.15.3"),sQuery(id+"F2.wireOp",EDGE,"E3.26.16.0"),sQuery(id+"F2.wireOp",EDGE,"E3.26.16.1"),sQuery(id+"F2.wireOp",EDGE,"E3.26.16.2"),sQuery(id+"F2.wireOp",EDGE,"E3.26.16.3"),sQuery(id+"F2.wireOp",EDGE,"E3.26.17.0"),sQuery(id+"F2.wireOp",EDGE,"E3.26.17.1"),sQuery(id+"F2.wireOp",EDGE,"E3.26.17.2"),sQuery(id+"F2.wireOp",EDGE,"E3.26.17.3"),sQuery(id+"F2.wireOp",EDGE,"E3.26.18.0"),sQuery(id+"F2.wireOp",EDGE,"E3.26.18.1"),sQuery(id+"F2.wireOp",EDGE,"E3.26.18.2"),sQuery(id+"F2.wireOp",EDGE,"E3.26.18.3"),sQuery(id+"F2.wireOp",EDGE,"E3.26.19.0"),sQuery(id+"F2.wireOp",EDGE,"E3.26.19.1"),sQuery(id+"F2.wireOp",EDGE,"E3.26.19.2"),sQuery(id+"F2.wireOp",EDGE,"E3.26.19.3"),sQuery(id+"F2.wireOp",EDGE,"E3.26.20.0"),sQuery(id+"F2.wireOp",EDGE,"E3.26.20.1"),sQuery(id+"F2.wireOp",EDGE,"E3.26.20.2"),sQuery(id+"F2.wireOp",EDGE,"E3.26.20.3"),sQuery(id+"F2.wireOp",EDGE,"E3.26.21.0"),sQuery(id+"F2.wireOp",EDGE,"E3.26.21.1"),sQuery(id+"F2.wireOp",EDGE,"E3.26.21.2"),sQuery(id+"F2.wireOp",EDGE,"E3.26.21.3"),sQuery(id+"F2.wireOp",EDGE,"E3.27.0.0"),sQuery(id+"F2.wireOp",EDGE,"E3.27.0.1"),sQuery(id+"F2.wireOp",EDGE,"E3.27.0.2"),sQuery(id+"F2.wireOp",EDGE,"E3.27.0.3"),sQuery(id+"F2.wireOp",EDGE,"E3.27.1.0"),sQuery(id+"F2.wireOp",EDGE,"E3.27.1.1"),sQuery(id+"F2.wireOp",EDGE,"E3.27.1.2"),sQuery(id+"F2.wireOp",EDGE,"E3.27.1.3"),sQuery(id+"F2.wireOp",EDGE,"E3.27.2.0"),sQuery(id+"F2.wireOp",EDGE,"E3.27.2.1"),sQuery(id+"F2.wireOp",EDGE,"E3.27.2.2"),sQuery(id+"F2.wireOp",EDGE,"E3.27.2.3"),sQuery(id+"F2.wireOp",EDGE,"E3.27.3.0"),sQuery(id+"F2.wireOp",EDGE,"E3.27.3.1"),sQuery(id+"F2.wireOp",EDGE,"E3.27.3.2"),sQuery(id+"F2.wireOp",EDGE,"E3.27.3.3"),sQuery(id+"F2.wireOp",EDGE,"E3.27.4.0"),sQuery(id+"F2.wireOp",EDGE,"E3.27.4.1"),sQuery(id+"F2.wireOp",EDGE,"E3.27.4.2"),sQuery(id+"F2.wireOp",EDGE,"E3.27.4.3"),sQuery(id+"F2.wireOp",EDGE,"E3.27.5.0"),sQuery(id+"F2.wireOp",EDGE,"E3.27.5.1"),sQuery(id+"F2.wireOp",EDGE,"E3.27.5.2"),sQuery(id+"F2.wireOp",EDGE,"E3.27.5.3"),sQuery(id+"F2.wireOp",EDGE,"E3.27.6.0"),sQuery(id+"F2.wireOp",EDGE,"E3.27.6.1"),sQuery(id+"F2.wireOp",EDGE,"E3.27.6.2"),sQuery(id+"F2.wireOp",EDGE,"E3.27.6.3"),sQuery(id+"F2.wireOp",EDGE,"E3.27.7.0"),sQuery(id+"F2.wireOp",EDGE,"E3.27.7.1"),sQuery(id+"F2.wireOp",EDGE,"E3.27.7.2"),sQuery(id+"F2.wireOp",EDGE,"E3.27.7.3"),sQuery(id+"F2.wireOp",EDGE,"E3.27.8.0"),sQuery(id+"F2.wireOp",EDGE,"E3.27.8.1"),sQuery(id+"F2.wireOp",EDGE,"E3.27.8.2"),sQuery(id+"F2.wireOp",EDGE,"E3.27.8.3"),sQuery(id+"F2.wireOp",EDGE,"E3.27.9.0"),sQuery(id+"F2.wireOp",EDGE,"E3.27.9.1"),sQuery(id+"F2.wireOp",EDGE,"E3.27.9.2"),sQuery(id+"F2.wireOp",EDGE,"E3.27.9.3"),sQuery(id+"F2.wireOp",EDGE,"E3.27.10.0"),sQuery(id+"F2.wireOp",EDGE,"E3.27.10.1"),sQuery(id+"F2.wireOp",EDGE,"E3.27.10.2"),sQuery(id+"F2.wireOp",EDGE,"E3.27.10.3"),sQuery(id+"F2.wireOp",EDGE,"E3.27.11.0"),sQuery(id+"F2.wireOp",EDGE,"E3.27.11.1"),sQuery(id+"F2.wireOp",EDGE,"E3.27.11.2"),sQuery(id+"F2.wireOp",EDGE,"E3.27.11.3"),sQuery(id+"F2.wireOp",EDGE,"E3.27.12.0"),sQuery(id+"F2.wireOp",EDGE,"E3.27.12.1"),sQuery(id+"F2.wireOp",EDGE,"E3.27.12.2"),sQuery(id+"F2.wireOp",EDGE,"E3.27.12.3"),sQuery(id+"F2.wireOp",EDGE,"E3.27.13.0"),sQuery(id+"F2.wireOp",EDGE,"E3.27.13.1"),sQuery(id+"F2.wireOp",EDGE,"E3.27.13.2"),sQuery(id+"F2.wireOp",EDGE,"E3.27.13.3"),sQuery(id+"F2.wireOp",EDGE,"E3.27.14.0"),sQuery(id+"F2.wireOp",EDGE,"E3.27.14.1"),sQuery(id+"F2.wireOp",EDGE,"E3.27.14.2"),sQuery(id+"F2.wireOp",EDGE,"E3.27.14.3"),sQuery(id+"F2.wireOp",EDGE,"E3.27.15.0"),sQuery(id+"F2.wireOp",EDGE,"E3.27.15.1"),sQuery(id+"F2.wireOp",EDGE,"E3.27.15.2"),sQuery(id+"F2.wireOp",EDGE,"E3.27.15.3"),sQuery(id+"F2.wireOp",EDGE,"E3.27.16.0"),sQuery(id+"F2.wireOp",EDGE,"E3.27.16.1"),sQuery(id+"F2.wireOp",EDGE,"E3.27.16.2"),sQuery(id+"F2.wireOp",EDGE,"E3.27.16.3"),sQuery(id+"F2.wireOp",EDGE,"E3.27.17.0"),sQuery(id+"F2.wireOp",EDGE,"E3.27.17.1"),sQuery(id+"F2.wireOp",EDGE,"E3.27.17.2"),sQuery(id+"F2.wireOp",EDGE,"E3.27.17.3"),sQuery(id+"F2.wireOp",EDGE,"E3.27.18.0"),sQuery(id+"F2.wireOp",EDGE,"E3.27.18.1"),sQuery(id+"F2.wireOp",EDGE,"E3.27.18.2"),sQuery(id+"F2.wireOp",EDGE,"E3.27.18.3"),sQuery(id+"F2.wireOp",EDGE,"E3.27.19.0"),sQuery(id+"F2.wireOp",EDGE,"E3.27.19.1"),sQuery(id+"F2.wireOp",EDGE,"E3.27.19.2"),sQuery(id+"F2.wireOp",EDGE,"E3.27.19.3"),sQuery(id+"F2.wireOp",EDGE,"E3.27.20.0"),sQuery(id+"F2.wireOp",EDGE,"E3.27.20.1"),sQuery(id+"F2.wireOp",EDGE,"E3.27.20.2"),sQuery(id+"F2.wireOp",EDGE,"E3.27.20.3"),sQuery(id+"F2.wireOp",EDGE,"E3.27.21.0"),sQuery(id+"F2.wireOp",EDGE,"E3.27.21.1"),sQuery(id+"F2.wireOp",EDGE,"E3.27.21.2"),sQuery(id+"F2.wireOp",EDGE,"E3.27.21.3"),sQuery(id+"F2.wireOp",EDGE,"E3.28.0.0"),sQuery(id+"F2.wireOp",EDGE,"E3.28.0.1"),sQuery(id+"F2.wireOp",EDGE,"E3.28.0.2"),sQuery(id+"F2.wireOp",EDGE,"E3.28.0.3"),sQuery(id+"F2.wireOp",EDGE,"E3.28.1.0"),sQuery(id+"F2.wireOp",EDGE,"E3.28.1.1"),sQuery(id+"F2.wireOp",EDGE,"E3.28.1.2"),sQuery(id+"F2.wireOp",EDGE,"E3.28.1.3"),sQuery(id+"F2.wireOp",EDGE,"E3.28.2.0"),sQuery(id+"F2.wireOp",EDGE,"E3.28.2.1"),sQuery(id+"F2.wireOp",EDGE,"E3.28.2.2"),sQuery(id+"F2.wireOp",EDGE,"E3.28.2.3"),sQuery(id+"F2.wireOp",EDGE,"E3.28.3.0"),sQuery(id+"F2.wireOp",EDGE,"E3.28.3.1"),sQuery(id+"F2.wireOp",EDGE,"E3.28.3.2"),sQuery(id+"F2.wireOp",EDGE,"E3.28.3.3"),sQuery(id+"F2.wireOp",EDGE,"E3.28.4.0"),sQuery(id+"F2.wireOp",EDGE,"E3.28.4.1"),sQuery(id+"F2.wireOp",EDGE,"E3.28.4.2"),sQuery(id+"F2.wireOp",EDGE,"E3.28.4.3"),sQuery(id+"F2.wireOp",EDGE,"E3.28.5.0"),sQuery(id+"F2.wireOp",EDGE,"E3.28.5.1"),sQuery(id+"F2.wireOp",EDGE,"E3.28.5.2"),sQuery(id+"F2.wireOp",EDGE,"E3.28.5.3"),sQuery(id+"F2.wireOp",EDGE,"E3.28.6.0"),sQuery(id+"F2.wireOp",EDGE,"E3.28.6.1"),sQuery(id+"F2.wireOp",EDGE,"E3.28.6.2"),sQuery(id+"F2.wireOp",EDGE,"E3.28.6.3"),sQuery(id+"F2.wireOp",EDGE,"E3.28.7.0"),sQuery(id+"F2.wireOp",EDGE,"E3.28.7.1"),sQuery(id+"F2.wireOp",EDGE,"E3.28.7.2"),sQuery(id+"F2.wireOp",EDGE,"E3.28.7.3"),sQuery(id+"F2.wireOp",EDGE,"E3.28.8.0"),sQuery(id+"F2.wireOp",EDGE,"E3.28.8.1"),sQuery(id+"F2.wireOp",EDGE,"E3.28.8.2"),sQuery(id+"F2.wireOp",EDGE,"E3.28.8.3"),sQuery(id+"F2.wireOp",EDGE,"E3.28.9.0"),sQuery(id+"F2.wireOp",EDGE,"E3.28.9.1"),sQuery(id+"F2.wireOp",EDGE,"E3.28.9.2"),sQuery(id+"F2.wireOp",EDGE,"E3.28.9.3"),sQuery(id+"F2.wireOp",EDGE,"E3.28.10.0"),sQuery(id+"F2.wireOp",EDGE,"E3.28.10.1"),sQuery(id+"F2.wireOp",EDGE,"E3.28.10.2"),sQuery(id+"F2.wireOp",EDGE,"E3.28.10.3"),sQuery(id+"F2.wireOp",EDGE,"E3.28.11.0"),sQuery(id+"F2.wireOp",EDGE,"E3.28.11.1"),sQuery(id+"F2.wireOp",EDGE,"E3.28.11.2"),sQuery(id+"F2.wireOp",EDGE,"E3.28.11.3"),sQuery(id+"F2.wireOp",EDGE,"E3.28.12.0"),sQuery(id+"F2.wireOp",EDGE,"E3.28.12.1"),sQuery(id+"F2.wireOp",EDGE,"E3.28.12.2"),sQuery(id+"F2.wireOp",EDGE,"E3.28.12.3"),sQuery(id+"F2.wireOp",EDGE,"E3.28.13.0"),sQuery(id+"F2.wireOp",EDGE,"E3.28.13.1"),sQuery(id+"F2.wireOp",EDGE,"E3.28.13.2"),sQuery(id+"F2.wireOp",EDGE,"E3.28.13.3"),sQuery(id+"F2.wireOp",EDGE,"E3.28.14.0"),sQuery(id+"F2.wireOp",EDGE,"E3.28.14.1"),sQuery(id+"F2.wireOp",EDGE,"E3.28.14.2"),sQuery(id+"F2.wireOp",EDGE,"E3.28.14.3"),sQuery(id+"F2.wireOp",EDGE,"E3.28.15.0"),sQuery(id+"F2.wireOp",EDGE,"E3.28.15.1"),sQuery(id+"F2.wireOp",EDGE,"E3.28.15.2"),sQuery(id+"F2.wireOp",EDGE,"E3.28.15.3"),sQuery(id+"F2.wireOp",EDGE,"E3.28.16.0"),sQuery(id+"F2.wireOp",EDGE,"E3.28.16.1"),sQuery(id+"F2.wireOp",EDGE,"E3.28.16.2"),sQuery(id+"F2.wireOp",EDGE,"E3.28.16.3"),sQuery(id+"F2.wireOp",EDGE,"E3.28.17.0"),sQuery(id+"F2.wireOp",EDGE,"E3.28.17.1"),sQuery(id+"F2.wireOp",EDGE,"E3.28.17.2"),sQuery(id+"F2.wireOp",EDGE,"E3.28.17.3"),sQuery(id+"F2.wireOp",EDGE,"E3.28.18.0"),sQuery(id+"F2.wireOp",EDGE,"E3.28.18.1"),sQuery(id+"F2.wireOp",EDGE,"E3.28.18.2"),sQuery(id+"F2.wireOp",EDGE,"E3.28.18.3"),sQuery(id+"F2.wireOp",EDGE,"E3.28.19.0"),sQuery(id+"F2.wireOp",EDGE,"E3.28.19.1"),sQuery(id+"F2.wireOp",EDGE,"E3.28.19.2"),sQuery(id+"F2.wireOp",EDGE,"E3.28.19.3"),sQuery(id+"F2.wireOp",EDGE,"E3.28.20.0"),sQuery(id+"F2.wireOp",EDGE,"E3.28.20.1"),sQuery(id+"F2.wireOp",EDGE,"E3.28.20.2"),sQuery(id+"F2.wireOp",EDGE,"E3.28.20.3"),sQuery(id+"F2.wireOp",EDGE,"E3.28.21.0"),sQuery(id+"F2.wireOp",EDGE,"E3.28.21.1"),sQuery(id+"F2.wireOp",EDGE,"E3.28.21.2"),sQuery(id+"F2.wireOp",EDGE,"E3.28.21.3"),sQuery(id+"F2.wireOp",EDGE,"E3.29.0.0"),sQuery(id+"F2.wireOp",EDGE,"E3.29.0.1"),sQuery(id+"F2.wireOp",EDGE,"E3.29.0.2"),sQuery(id+"F2.wireOp",EDGE,"E3.29.0.3"),sQuery(id+"F2.wireOp",EDGE,"E3.29.1.0"),sQuery(id+"F2.wireOp",EDGE,"E3.29.1.1"),sQuery(id+"F2.wireOp",EDGE,"E3.29.1.2"),sQuery(id+"F2.wireOp",EDGE,"E3.29.1.3"),sQuery(id+"F2.wireOp",EDGE,"E3.29.2.0"),sQuery(id+"F2.wireOp",EDGE,"E3.29.2.1"),sQuery(id+"F2.wireOp",EDGE,"E3.29.2.2"),sQuery(id+"F2.wireOp",EDGE,"E3.29.2.3"),sQuery(id+"F2.wireOp",EDGE,"E3.29.3.0"),sQuery(id+"F2.wireOp",EDGE,"E3.29.3.1"),sQuery(id+"F2.wireOp",EDGE,"E3.29.3.2"),sQuery(id+"F2.wireOp",EDGE,"E3.29.3.3"),sQuery(id+"F2.wireOp",EDGE,"E3.29.4.0"),sQuery(id+"F2.wireOp",EDGE,"E3.29.4.1"),sQuery(id+"F2.wireOp",EDGE,"E3.29.4.2"),sQuery(id+"F2.wireOp",EDGE,"E3.29.4.3"),sQuery(id+"F2.wireOp",EDGE,"E3.29.5.0"),sQuery(id+"F2.wireOp",EDGE,"E3.29.5.1"),sQuery(id+"F2.wireOp",EDGE,"E3.29.5.2"),sQuery(id+"F2.wireOp",EDGE,"E3.29.5.3"),sQuery(id+"F2.wireOp",EDGE,"E3.29.6.0"),sQuery(id+"F2.wireOp",EDGE,"E3.29.6.1"),sQuery(id+"F2.wireOp",EDGE,"E3.29.6.2"),sQuery(id+"F2.wireOp",EDGE,"E3.29.6.3"),sQuery(id+"F2.wireOp",EDGE,"E3.29.7.0"),sQuery(id+"F2.wireOp",EDGE,"E3.29.7.1"),sQuery(id+"F2.wireOp",EDGE,"E3.29.7.2"),sQuery(id+"F2.wireOp",EDGE,"E3.29.7.3"),sQuery(id+"F2.wireOp",EDGE,"E3.29.8.0"),sQuery(id+"F2.wireOp",EDGE,"E3.29.8.1"),sQuery(id+"F2.wireOp",EDGE,"E3.29.8.2"),sQuery(id+"F2.wireOp",EDGE,"E3.29.8.3"),sQuery(id+"F2.wireOp",EDGE,"E3.29.9.0"),sQuery(id+"F2.wireOp",EDGE,"E3.29.9.1"),sQuery(id+"F2.wireOp",EDGE,"E3.29.9.2"),sQuery(id+"F2.wireOp",EDGE,"E3.29.9.3"),sQuery(id+"F2.wireOp",EDGE,"E3.29.10.0"),sQuery(id+"F2.wireOp",EDGE,"E3.29.10.1"),sQuery(id+"F2.wireOp",EDGE,"E3.29.10.2"),sQuery(id+"F2.wireOp",EDGE,"E3.29.10.3"),sQuery(id+"F2.wireOp",EDGE,"E3.29.11.0"),sQuery(id+"F2.wireOp",EDGE,"E3.29.11.1"),sQuery(id+"F2.wireOp",EDGE,"E3.29.11.2"),sQuery(id+"F2.wireOp",EDGE,"E3.29.11.3"),sQuery(id+"F2.wireOp",EDGE,"E3.29.12.0"),sQuery(id+"F2.wireOp",EDGE,"E3.29.12.1"),sQuery(id+"F2.wireOp",EDGE,"E3.29.12.2"),sQuery(id+"F2.wireOp",EDGE,"E3.29.12.3"),sQuery(id+"F2.wireOp",EDGE,"E3.29.13.0"),sQuery(id+"F2.wireOp",EDGE,"E3.29.13.1"),sQuery(id+"F2.wireOp",EDGE,"E3.29.13.2"),sQuery(id+"F2.wireOp",EDGE,"E3.29.13.3"),sQuery(id+"F2.wireOp",EDGE,"E3.29.14.0"),sQuery(id+"F2.wireOp",EDGE,"E3.29.14.1"),sQuery(id+"F2.wireOp",EDGE,"E3.29.14.2"),sQuery(id+"F2.wireOp",EDGE,"E3.29.14.3"),sQuery(id+"F2.wireOp",EDGE,"E3.29.15.0"),sQuery(id+"F2.wireOp",EDGE,"E3.29.15.1"),sQuery(id+"F2.wireOp",EDGE,"E3.29.15.2"),sQuery(id+"F2.wireOp",EDGE,"E3.29.15.3"),sQuery(id+"F2.wireOp",EDGE,"E3.29.16.0"),sQuery(id+"F2.wireOp",EDGE,"E3.29.16.1"),sQuery(id+"F2.wireOp",EDGE,"E3.29.16.2"),sQuery(id+"F2.wireOp",EDGE,"E3.29.16.3"),sQuery(id+"F2.wireOp",EDGE,"E3.29.17.0"),sQuery(id+"F2.wireOp",EDGE,"E3.29.17.1"),sQuery(id+"F2.wireOp",EDGE,"E3.29.17.2"),sQuery(id+"F2.wireOp",EDGE,"E3.29.17.3"),sQuery(id+"F2.wireOp",EDGE,"E3.29.18.0"),sQuery(id+"F2.wireOp",EDGE,"E3.29.18.1"),sQuery(id+"F2.wireOp",EDGE,"E3.29.18.2"),sQuery(id+"F2.wireOp",EDGE,"E3.29.18.3"),sQuery(id+"F2.wireOp",EDGE,"E3.29.19.0"),sQuery(id+"F2.wireOp",EDGE,"E3.29.19.1"),sQuery(id+"F2.wireOp",EDGE,"E3.29.19.2"),sQuery(id+"F2.wireOp",EDGE,"E3.29.19.3"),sQuery(id+"F2.wireOp",EDGE,"E3.29.20.0"),sQuery(id+"F2.wireOp",EDGE,"E3.29.20.1"),sQuery(id+"F2.wireOp",EDGE,"E3.29.20.2"),sQuery(id+"F2.wireOp",EDGE,"E3.29.20.3"),sQuery(id+"F2.wireOp",EDGE,"E3.29.21.0"),sQuery(id+"F2.wireOp",EDGE,"E3.29.21.1"),sQuery(id+"F2.wireOp",EDGE,"E3.29.21.2"),sQuery(id+"F2.wireOp",EDGE,"E3.29.21.3"),sQuery(id+"F2.wireOp",EDGE,"E4.filletArc"),sQuery(id+"F2.wireOp",EDGE,"E5.filletArc"),sQuery(id+"F2.wireOp",EDGE,"E6.filletArc"),sQuery(id+"F2.wireOp",EDGE,"E7.filletArc")])],"isStart":false})});
            var sketch = newSketch(context, id + "F4", { "sketchPlane" : qUnion([Q0])});
            skCircle(sketch, "E8", {"center": v(203.2, 279.4) * mm, "radius": 1.2 * mm});
            skSolve(sketch);
        }
        {
            var Q0;
            Q0=qSketchRegion(id+"F4",true);
            extrude(context, id + "F5", {"entities" : qUnion([Q0]), "operationType" : NewBodyOperationType.REMOVE, "oppositeDirection" : true, "depth" : 6.35 * mm});
        }
        {
            var Q0;
            {var subQ0=sQuery(id+"F0.wireOp",EDGE,"E0.left");var subQ1=sQuery(id+"F0.wireOp",EDGE,"E0.bottom");var subQ2=sQuery(id+"F0.wireOp",EDGE,"E0.top");var subQ3=sQuery(id+"F0.wireOp",EDGE,"E0.right");Q0=makeQuery(id+"F3.boolean.opBoolean","SPLIT",FACE,{"disambiguationData":[TD([makeQuery(id+"F1.opExtrude","SWEPT_FACE",FACE,{"disambiguationData":[OSD([subQ1])]})])],"derivedFrom":makeQuery(id+"F1.opExtrude","CAP_FACE",FACE,{"disambiguationData":[OSD([subQ1,subQ2,subQ0,subQ3])],"isStart":false})});}
            var sketch = newSketch(context, id + "F6", { "sketchPlane" : qUnion([Q0])});
            skLineSegment(sketch, "E9.bottom", {"start": v(0, 304.8) * mm, "end": v(406.4, 304.8) * mm});
            skLineSegment(sketch, "E9.top", {"start": v(0, 300.84) * mm, "end": v(406.4, 300.84) * mm});
            skLineSegment(sketch, "E9.left", {"start": v(0, 304.8) * mm, "end": v(0, 300.84) * mm});
            skLineSegment(sketch, "E9.right", {"start": v(406.4, 304.8) * mm, "end": v(406.4, 300.84) * mm});
            skLineSegment(sketch, "E10.bottom", {"start": v(0, 0) * mm, "end": v(406.4, 0) * mm});
            skLineSegment(sketch, "E10.top", {"start": v(0, 3.96) * mm, "end": v(406.4, 3.96) * mm});
            skLineSegment(sketch, "E10.left", {"start": v(0, 0) * mm, "end": v(0, 3.96) * mm});
            skLineSegment(sketch, "E10.right", {"start": v(406.4, 0) * mm, "end": v(406.4, 3.96) * mm});
            skLineSegment(sketch, "E11.bottom", {"start": v(0, 3.96) * mm, "end": v(3.96, 3.96) * mm});
            skLineSegment(sketch, "E11.top", {"start": v(0, 304.8) * mm, "end": v(3.96, 304.8) * mm});
            skLineSegment(sketch, "E11.left", {"start": v(0, 3.96) * mm, "end": v(0, 304.8) * mm});
            skLineSegment(sketch, "E11.right", {"start": v(3.96, 3.96) * mm, "end": v(3.96, 304.8) * mm});
            skLineSegment(sketch, "E12.bottom", {"start": v(406.4, 3.96) * mm, "end": v(402.44, 3.96) * mm});
            skLineSegment(sketch, "E12.top", {"start": v(406.4, 300.84) * mm, "end": v(402.44, 300.84) * mm});
            skLineSegment(sketch, "E12.left", {"start": v(406.4, 3.96) * mm, "end": v(406.4, 300.84) * mm});
            skLineSegment(sketch, "E12.right", {"start": v(402.44, 3.96) * mm, "end": v(402.44, 300.84) * mm});
            skSolve(sketch);
        }
        {
            var Q0;
            Q0=qSketchRegion(id+"F6",true);
            extrude(context, id + "F7", {"entities" : qUnion([Q0]), "operationType" : NewBodyOperationType.REMOVE, "oppositeDirection" : true, "depth" : 15.88 * mm});
        }
        {
            var Q0;
            Q0=makeQuery(id+"F7.boolean.opBoolean","COPY",FACE,{"derivedFrom":makeQuery(id+"F7.opExtrude","SWEPT_FACE",FACE,{"disambiguationData":[OSD([sQuery(id+"F6.wireOp",EDGE,"E9.top")])]})});
            var sketch = newSketch(context, id + "F8", { "sketchPlane" : qUnion([Q0])});
            skCircle(sketch, "E13", {"center": v(-204.4, 11.13) * mm, "radius": 5.08 * mm});
            skSolve(sketch);
        }
        {
            var Q0;
            Q0=qSketchRegion(id+"F8",true);
            extrude(context, id + "F9", {"entities" : qUnion([Q0]), "operationType" : NewBodyOperationType.REMOVE, "oppositeDirection" : true, "depth" : 6.35 * mm});
        }
        {
            var Q0;
            Q0=makeQuery(id+"F9.boolean.opBoolean","COPY",FACE,{"derivedFrom":makeQuery(id+"F9.opExtrude","CAP_FACE",FACE,{"disambiguationData":[OSD([sQuery(id+"F8.wireOp",EDGE,"E13")])],"isStart":false})});
            var sketch = newSketch(context, id + "F10", { "sketchPlane" : qUnion([Q0])});
            skCircle(sketch, "E14", {"center": v(-204.4, 11.13) * mm, "radius": 3.18 * mm});
            skSolve(sketch);
        }
        {
            var Q0;
            Q0=qSketchRegion(id+"F10",true);
            extrude(context, id + "F11", {"entities" : qUnion([Q0]), "operationType" : NewBodyOperationType.REMOVE, "oppositeDirection" : true, "depth" : 19.05 * mm});
        }
        {
            var Q0;
            Q0=makeQuery(id+"F7.boolean.opBoolean","COPY",FACE,{"derivedFrom":makeQuery(id+"F7.opExtrude","CAP_FACE",FACE,{"disambiguationData":[OSD([sQuery(id+"F6.wireOp",EDGE,"E9.bottom"),sQuery(id+"F6.wireOp",EDGE,"E9.top"),sQuery(id+"F6.wireOp",EDGE,"E9.right"),sQuery(id+"F6.wireOp",EDGE,"E10.bottom"),sQuery(id+"F6.wireOp",EDGE,"E10.top"),sQuery(id+"F6.wireOp",EDGE,"E10.left"),sQuery(id+"F6.wireOp",EDGE,"E10.right"),sQuery(id+"F6.wireOp",EDGE,"E11.top"),sQuery(id+"F6.wireOp",EDGE,"E11.left"),sQuery(id+"F6.wireOp",EDGE,"E11.right"),sQuery(id+"F6.wireOp",EDGE,"E12.left"),sQuery(id+"F6.wireOp",EDGE,"E12.right")])],"isStart":false})});
            var sketch = newSketch(context, id + "F12", { "sketchPlane" : qUnion([Q0])});
            skLineSegment(sketch, "E15.bottom", {"start": v(0, 304.8) * mm, "end": v(3.96, 304.8) * mm});
            skLineSegment(sketch, "E15.top", {"start": v(0, 0) * mm, "end": v(3.96, 0) * mm});
            skLineSegment(sketch, "E15.left", {"start": v(0, 304.8) * mm, "end": v(0, 0) * mm});
            skLineSegment(sketch, "E15.right", {"start": v(3.96, 304.8) * mm, "end": v(3.96, 0) * mm});
            skLineSegment(sketch, "E16.bottom", {"start": v(406.4, 304.8) * mm, "end": v(402.44, 304.8) * mm});
            skLineSegment(sketch, "E16.top", {"start": v(406.4, 0) * mm, "end": v(402.44, 0) * mm});
            skLineSegment(sketch, "E16.left", {"start": v(406.4, 304.8) * mm, "end": v(406.4, 0) * mm});
            skLineSegment(sketch, "E16.right", {"start": v(402.44, 304.8) * mm, "end": v(402.44, 0) * mm});
            skLineSegment(sketch, "E17.bottom", {"start": v(3.96, 304.8) * mm, "end": v(402.44, 304.8) * mm});
            skLineSegment(sketch, "E17.top", {"start": v(3.96, 300.84) * mm, "end": v(402.44, 300.84) * mm});
            skLineSegment(sketch, "E17.left", {"start": v(3.96, 304.8) * mm, "end": v(3.96, 300.84) * mm});
            skLineSegment(sketch, "E17.right", {"start": v(402.44, 304.8) * mm, "end": v(402.44, 300.84) * mm});
            skLineSegment(sketch, "E18.bottom", {"start": v(3.96, 0) * mm, "end": v(402.44, 0) * mm});
            skLineSegment(sketch, "E18.top", {"start": v(3.96, 3.96) * mm, "end": v(402.44, 3.96) * mm});
            skLineSegment(sketch, "E18.left", {"start": v(3.96, 0) * mm, "end": v(3.96, 3.96) * mm});
            skLineSegment(sketch, "E18.right", {"start": v(402.44, 0) * mm, "end": v(402.44, 3.96) * mm});
            skSolve(sketch);
        }
        {
            var Q0;
            Q0 = qSketchRegion(id + "F12", true);
            extrude(context, id + "F13", {"entities" : qUnion([Q0]), "operationType" : NewBodyOperationType.REMOVE, "endBound" : BoundingType.THROUGH_ALL, "oppositeDirection" : true, "depth" : 25.4 * mm});
        }
    });
